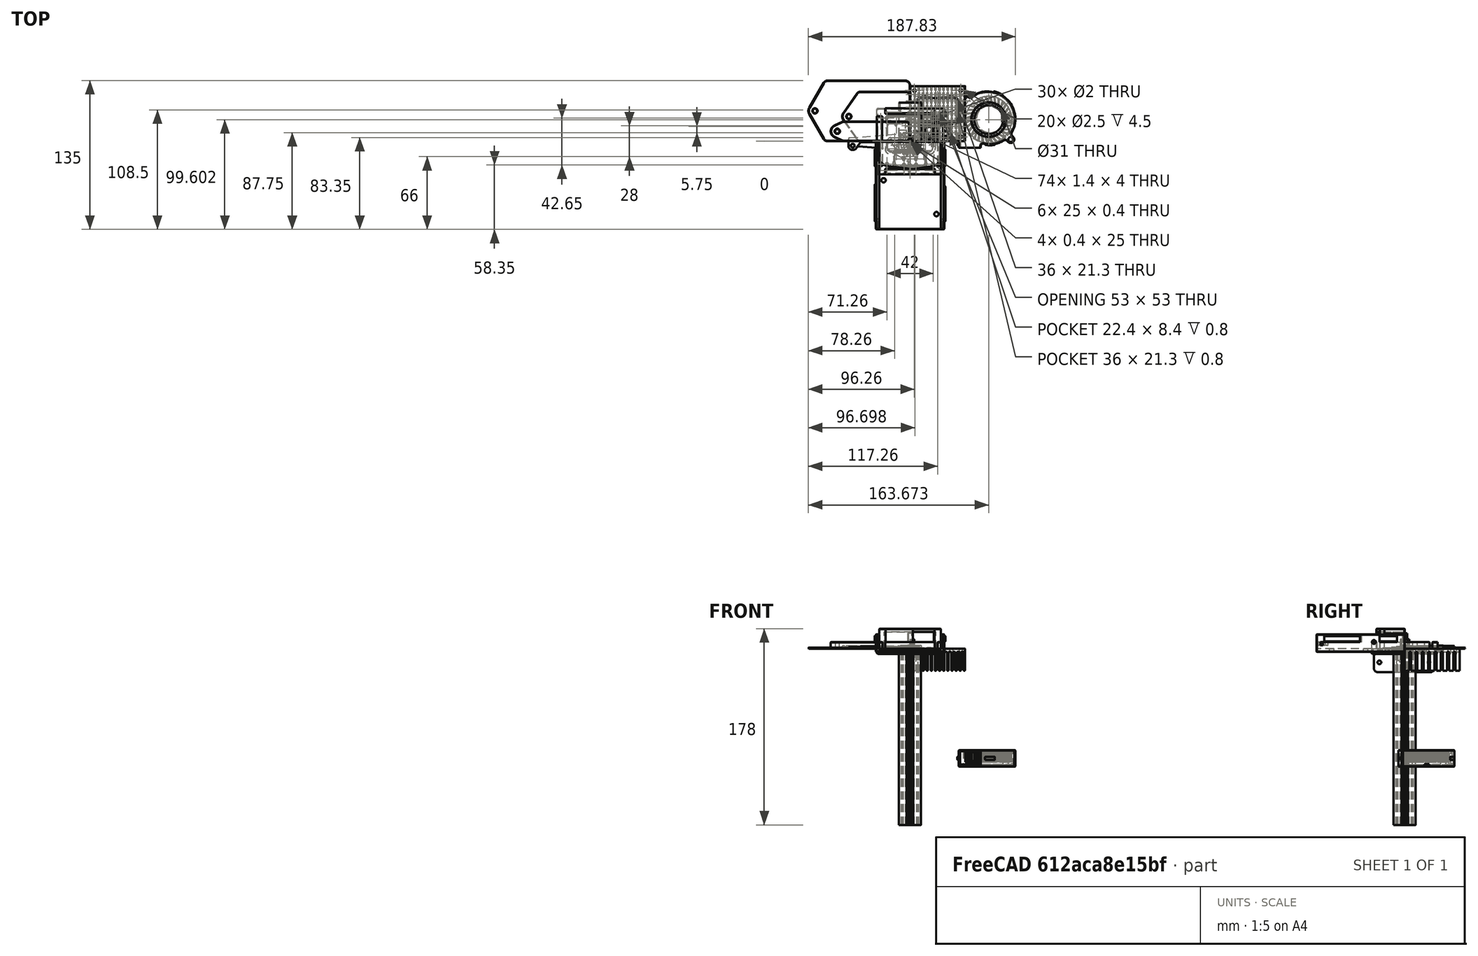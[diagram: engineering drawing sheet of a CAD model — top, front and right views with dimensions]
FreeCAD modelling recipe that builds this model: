
FCSTD DOCUMENT  (FreeCAD 1.1R20260325 (Git shallow))
Label: bedburner
License: All rights reserved
LicenseURL: https://www.gnu.org/licenses/gpl-3.0.html
objects: TechDraw::DrawViewDimension×98, App::FeaturePython×65, Sketcher::SketchObject×46, App::Point×28, App::Link×27, PartDesign::Pocket×26, PartDesign::Body×25, PartDesign::Chamfer×22, Part::Cut×16, PartDesign::Pad×14, PartDesign::FeatureBase×14, Part::Feature×13, PartDesign::Fillet×12, TechDraw::DrawProjGroupItem×12, App::DocumentObjectGroup×10, Part::Part2DObjectPython×6, Part::Extrusion×6, PartDesign::FeaturePython×6, App::VarSet×4, TechDraw::DrawSVGTemplate×4, +8 more types
note: 609 computed .brp shape members not serialized (recipe doc carries the construction recipe); baked Part::Feature solids carry a one-line shape summary decoded from their .brp

FEATURE [Sketcher::SketchObject] Sketch059  label="hhtb_base_face_s"
  ArcFitTolerance = 0
  AttachmentSupport = -> [XY_Plane036]
  ExternalTypes = [0]
  FullyConstrained = true
  MakeInternals = false
  MapMode = 5
  _ExternalGeoVersion = 0
  expr: .Constraints.width = <<block_params>>.heatsink_width + 2 * <<template_params>>.feature_side_width
  sketch-geometry (5):
    g0: LineSegment StartX=-30 StartY=30 StartZ=0 EndX=30 EndY=30 EndZ=0
    g1: LineSegment StartX=30 StartY=30 StartZ=0 EndX=30 EndY=-30 EndZ=0
    g2: LineSegment StartX=30 StartY=-30 StartZ=0 EndX=-30 EndY=-30 EndZ=0
    g3: LineSegment StartX=-30 StartY=-30 StartZ=0 EndX=-30 EndY=30 EndZ=0
    g4: Circle [constr] CenterX=0 CenterY=0 CenterZ=0 NormalX=0 NormalY=0 NormalZ=1 AngleXU=0 Radius=30
  constraints (14):
    c: Coincident(g0,g1)
    c: Coincident(g1,g2)
    c: Coincident(g2,g3)
    c: Coincident(g3,g0)
    c: Horizontal(g0)
    c: Horizontal(g2)
    c: Vertical(g1)
    c: Vertical(g3)
    c: Coincident(g4,g-1)
    c: Tangent(g4,g0)
    c: Tangent(g4,g1)
    c: Tangent(g4,g2)
    c: Tangent(g3,g4)
    c: Diameter(g4) = 60  'width'
FEATURE [PartDesign::Pad] Pad021  label="hhtb_base_face"
  Direction = (0,0,1)
  Length = 5
  Length2 = 10
  Profile = -> Sketch059
  ReferenceAxis = -> Sketch059 [N_Axis]
  Reversed = true
  SideType = 0
  Suppressed = false
  Type = 0
  Type2 = 0
FEATURE [Sketcher::SketchObject] Sketch060  label="hhtb_base_side_s"
  ArcFitTolerance = 0
  AttachmentSupport = -> [XZ_Plane036]
  ExternalTypes = [0]
  FullyConstrained = true
  MakeInternals = false
  MapMode = 5
  Placement = pos=(0,0,0) rot=(1,0,0;1.5708rad)
  _ExternalGeoVersion = 0
  expr: .Constraints.height = <<template_params>>.feature_side_height
  expr: .Constraints.outer_offset = <<hhtb_base_face_s>>.Constraints.width / 2
  expr: .Constraints.relief = <<template_params>>.feature_side_relief
  expr: .Constraints.width = <<template_params>>.feature_side_width - <<template_params>>.feature_side_clearance
  sketch-geometry (7):
    g0: LineSegment StartX=-30 StartY=6 StartZ=0 EndX=-30 EndY=0 EndZ=0
    g1: LineSegment StartX=-30 StartY=0 StartZ=0 EndX=-25.6 EndY=0 EndZ=0
    g2: LineSegment StartX=-25.6 StartY=0 StartZ=0 EndX=-25 EndY=0.6 EndZ=0
    g3: LineSegment StartX=-25 StartY=0.6 StartZ=0 EndX=-25 EndY=6 EndZ=0
    g4: LineSegment StartX=-25 StartY=6 StartZ=0 EndX=-30 EndY=6 EndZ=0
    g5: LineSegment [constr] StartX=-25.6 StartY=0 StartZ=0 EndX=-25 EndY=0 EndZ=0
    g6: LineSegment [constr] StartX=-25 StartY=0 StartZ=0 EndX=-25 EndY=0.6 EndZ=0
  constraints (20):
    c: Vertical(g0)
    c: Coincident(g0,g1)
    c: Horizontal(g1)
    c: Coincident(g1,g2)
    c: Coincident(g2,g3)
    c: Vertical(g3)
    c: Coincident(g3,g4)
    c: Coincident(g4,g0)
    c: Coincident(g1,g5)
    c: Horizontal(g5)
    c: Coincident(g5,g6)
    c: Coincident(g6,g2)
    c: Vertical(g6)
    c: Equal(g5,g6)
    c: Horizontal(g4)
    c: PointOnObject(g0,g-1)
    c: Distance(g6) = 0.6  'relief'
    c: DistanceX(g0,g-1) = 30  'outer_offset'
    c: Distance(g4) = 5  'width'
    c: Distance(g0) = 6  'height'
FEATURE [PartDesign::Pad] Pad022  label="hhtb_base_side1"
  BaseFeature = -> Pad021
  Direction = (0,-1,2e-16)
  Length = 45
  Length2 = 10
  Profile = -> Sketch060
  ReferenceAxis = -> Sketch060 [N_Axis]
  SideType = 2
  Suppressed = false
  Type = 0
  Type2 = 0
  expr: Length = <<template_params>>.feature_side_length
FEATURE [PartDesign::PolarPattern] PolarPattern001  label="hhtb_base_side234"
  Angle = 360
  Axis = -> Z_Axis036
  BaseFeature = -> Pad022
  Mode = 0
  Occurrences = 4
  Offset = 120
  Originals = -> [Pad022]
  SpacingPattern = [0]
  Spacings = [-1,-1,-1]
  Suppressed = false
  TransformMode = 0
FEATURE [PartDesign::Chamfer] Chamfer021  label="hhtb_base_corner_chmf"
  Angle = 45
  Base = -> PolarPattern001 [Edge12,Edge7,Edge1,Edge2]
  BaseFeature = -> PolarPattern001
  ChamferType = 0
  FlipDirection = false
  Size = 1
  Size2 = 1
  SupportTransform = false
  Suppressed = false
  UseAllEdges = false
FEATURE [PartDesign::Chamfer] Chamfer022  label="hhtb_base_bottom_chmf"
  Angle = 45
  Base = -> Chamfer021 [Face5]
  BaseFeature = -> Chamfer021
  ChamferType = 0
  FlipDirection = false
  Size = 0.8
  Size2 = 1
  SupportTransform = false
  Suppressed = false
  UseAllEdges = false
FEATURE [PartDesign::Fillet] Fillet013  label="hhtb_base_inner_flt"
  Base = -> Chamfer022 [Edge51,Edge52,Edge57,Edge58,Edge63,Edge65,Edge80,Edge86,Edge82,Edge83,Edge89,Edge91,Edge73,Edge74,Edge60,Edge55]
  BaseFeature = -> Chamfer022
  Radius = 0.4
  SupportTransform = false
  Suppressed = false
  UseAllEdges = false
FEATURE [Sketcher::SketchObject] Sketch061  label="hhdg_holes_s"
  ArcFitTolerance = 0
  AttachmentSupport = -> [XY_Plane037]
  ExternalTypes = [0]
  FullyConstrained = true
  MakeInternals = false
  MapMode = 5
  _ExternalGeoVersion = 0
  expr: .Constraints.block_spacing = <<block_params>>.heatsink_screw_spacing
  expr: .Constraints.block_width = <<block_params>>.heatsink_width
  expr: .Constraints.hole_diam = <<template_params>>.drill_hole_diam
  sketch-geometry (14):
    g0: Circle CenterX=-21 CenterY=21 CenterZ=0 NormalX=0 NormalY=0 NormalZ=1 AngleXU=0 Radius=1
    g1: Circle CenterX=21 CenterY=21 CenterZ=0 NormalX=0 NormalY=0 NormalZ=1 AngleXU=0 Radius=1
    g2: Circle CenterX=-21 CenterY=-21 CenterZ=0 NormalX=0 NormalY=0 NormalZ=1 AngleXU=0 Radius=1
    g3: Circle CenterX=21 CenterY=-21 CenterZ=0 NormalX=0 NormalY=0 NormalZ=1 AngleXU=0 Radius=1
    g4: LineSegment [constr] StartX=-25 StartY=25 StartZ=0 EndX=-25 EndY=-25 EndZ=0
    g5: LineSegment [constr] StartX=-25 StartY=-25 StartZ=0 EndX=25 EndY=-25 EndZ=0
    g6: LineSegment [constr] StartX=25 StartY=-25 StartZ=0 EndX=25 EndY=25 EndZ=0
    g7: LineSegment [constr] StartX=25 StartY=25 StartZ=0 EndX=-25 EndY=25 EndZ=0
    g8: Circle [constr] CenterX=0 CenterY=0 CenterZ=0 NormalX=0 NormalY=0 NormalZ=1 AngleXU=0 Radius=25
    g9: Circle [constr] CenterX=0 CenterY=0 CenterZ=0 NormalX=0 NormalY=0 NormalZ=1 AngleXU=0 Radius=21
    g10: LineSegment [constr] StartX=-21 StartY=21 StartZ=0 EndX=-21 EndY=-21 EndZ=0
    g11: LineSegment [constr] StartX=-21 StartY=-21 StartZ=0 EndX=21 EndY=-21 EndZ=0
    g12: LineSegment [constr] StartX=21 StartY=-21 StartZ=0 EndX=21 EndY=21 EndZ=0
    g13: LineSegment [constr] StartX=21 StartY=21 StartZ=0 EndX=-21 EndY=21 EndZ=0
  constraints (36):
    c: Diameter(g2) = 2  'hole_diam'
    c: Equal(g2,g0)
    c: Equal(g2,g3)
    c: Equal(g2,g1)
    c: Coincident(g4,g5)
    c: Coincident(g5,g6)
    c: Coincident(g6,g7)
    c: Coincident(g7,g4)
    c: Vertical(g4)
    c: Vertical(g6)
    c: Horizontal(g5)
    c: Horizontal(g7)
    c: Coincident(g8,g-1)
    c: Tangent(g8,g7)
    c: Tangent(g8,g6)
    c: Tangent(g8,g4)
    c: Tangent(g8,g5)
    c: Diameter(g8) = 50  'block_width'
    c: Coincident(g9,g8)
    c: Coincident(g10,g11)
    c: Coincident(g11,g12)
    c: Coincident(g12,g13)
    c: Coincident(g13,g10)
    c: Vertical(g10)
    c: Vertical(g12)
    c: Horizontal(g11)
    c: Horizontal(g13)
    c: Tangent(g9,g13)
    c: Tangent(g9,g12)
    c: Tangent(g9,g11)
    c: Tangent(g9,g10)
    c: Diameter(g9) = 42  'block_spacing'
    c: Coincident(g2,g10)
    c: Coincident(g3,g11)
    c: Coincident(g12,g1)
    c: Coincident(g10,g0)
FEATURE [Sketcher::SketchObject] Sketch062  label="hht_ptc_1-16_pocket_s"
  ArcFitTolerance = 0
  AttachmentSupport = -> [XY_Plane038]
  ExternalTypes = [0]
  FullyConstrained = true
  MakeInternals = false
  MapMode = 5
  _ExternalGeoVersion = 0
  expr: .Constraints.block_width = <<block_params>>.heatsink_width
  expr: .Constraints.corner_length = <<block_params>>.ptc_pocket_length + 2 * <<template_params>>.router_dogbone
  expr: .Constraints.corner_width = <<block_params>>.ptc_pocket_width + 2 * <<template_params>>.router_dogbone
  expr: .Constraints.edge_length = <<block_params>>.ptc_pocket_length + 2 * <<template_params>>.router_offset_1_16
  expr: .Constraints.edge_width = <<block_params>>.ptc_pocket_width + 2 * <<template_params>>.router_offset_1_16
  expr: .Constraints.placement_length = <<block_params>>.ptc_placement_length
  expr: .Constraints.placement_width = <<block_params>>.ptc_placement_width
  expr: .Constraints.router_bushing = <<template_params>>.router_bushing
  sketch-geometry (21):
    g0: LineSegment [constr] StartX=-18.3 StartY=14.45 StartZ=0 EndX=18.3 EndY=14.45 EndZ=0
    g1: LineSegment [constr] StartX=18.3 StartY=14.45 StartZ=0 EndX=18.3 EndY=-7.45 EndZ=0
    g2: LineSegment [constr] StartX=18.3 StartY=-7.45 StartZ=0 EndX=-18.3 EndY=-7.45 EndZ=0
    g3: LineSegment [constr] StartX=-18.3 StartY=-7.45 StartZ=0 EndX=-18.3 EndY=14.45 EndZ=0
    g4: LineSegment StartX=-21.375 StartY=11.9409 StartZ=0 EndX=-21.375 EndY=-4.94095 EndZ=0
    g5: LineSegment StartX=-15.7909 StartY=-10.525 StartZ=0 EndX=15.7909 EndY=-10.525 EndZ=0
    g6: LineSegment StartX=21.375 StartY=11.9409 StartZ=0 EndX=21.375 EndY=-4.94095 EndZ=0
    g7: LineSegment StartX=-15.7909 StartY=17.525 StartZ=0 EndX=15.7909 EndY=17.525 EndZ=0
    g8: ArcOfCircle CenterX=18.3 CenterY=14.45 CenterZ=0 NormalX=0 NormalY=0 NormalZ=1 AngleXU=0 Radius=3.96875 StartAngle=5.59879 EndAngle=8.53837
    g9: ArcOfCircle CenterX=18.3 CenterY=-7.45 CenterZ=0 NormalX=0 NormalY=0 NormalZ=1 AngleXU=0 Radius=3.96875 StartAngle=4.028 EndAngle=6.96758
    g10: ArcOfCircle CenterX=-18.3 CenterY=14.45 CenterZ=0 NormalX=0 NormalY=0 NormalZ=1 AngleXU=0 Radius=3.96875 StartAngle=0.886404 EndAngle=3.82599
    g11: ArcOfCircle CenterX=-18.3 CenterY=-7.45 CenterZ=0 NormalX=0 NormalY=0 NormalZ=1 AngleXU=0 Radius=3.96875 StartAngle=2.4572 EndAngle=5.39678
    g12: Circle [constr] CenterX=-1.8e-15 CenterY=3.5 CenterZ=0 NormalX=0 NormalY=0 NormalZ=1 AngleXU=0 Radius=14.025
    g13: Circle [constr] CenterX=-1.8e-15 CenterY=3.5 CenterZ=0 NormalX=0 NormalY=0 NormalZ=1 AngleXU=0 Radius=21.375
    g14: Circle [constr] CenterX=0 CenterY=0 CenterZ=0 NormalX=0 NormalY=0 NormalZ=1 AngleXU=0 Radius=25
    g15: LineSegment [constr] StartX=-25 StartY=25 StartZ=0 EndX=-25 EndY=-25 EndZ=0
    g16: LineSegment [constr] StartX=-25 StartY=-25 StartZ=0 EndX=25 EndY=-25 EndZ=0
    g17: LineSegment [constr] StartX=25 StartY=-25 StartZ=0 EndX=25 EndY=25 EndZ=0
    g18: LineSegment [constr] StartX=25 StartY=25 StartZ=0 EndX=-25 EndY=25 EndZ=0
    g19: Circle [constr] CenterX=-1.8e-15 CenterY=3.5 CenterZ=0 NormalX=0 NormalY=0 NormalZ=1 AngleXU=0 Radius=18.3
    g20: Circle [constr] CenterX=-1.8e-15 CenterY=3.5 CenterZ=0 NormalX=0 NormalY=0 NormalZ=1 AngleXU=0 Radius=10.95
  constraints (59):
    c: Coincident(g0,g1)
    c: Coincident(g1,g2)
    c: Coincident(g2,g3)
    c: Coincident(g3,g0)
    c: Horizontal(g0)
    c: Horizontal(g2)
    c: Vertical(g1)
    c: Vertical(g3)
    c: Vertical(g4)
    c: Horizontal(g5)
    c: Vertical(g6)
    c: Horizontal(g7)
    c: Equal(g10,g11)
    c: Equal(g11,g9)
    c: Equal(g9,g8)
    c: Diameter(g9) = 7.9375  'router_bushing'
    c: Coincident(g4,g10)
    c: Coincident(g10,g7)
    c: Coincident(g7,g8)
    c: Coincident(g6,g8)
    c: Coincident(g6,g9)
    c: Coincident(g5,g9)
    c: Coincident(g11,g5)
    c: Coincident(g11,g4)
    c: Coincident(g0,g8)
    c: Coincident(g1,g9)
    c: Coincident(g2,g11)
    c: Coincident(g0,g10)
    c: Coincident(g13,g12)
    c: Coincident(g14,g-1)
    c: Diameter(g14) = 50  'block_width'
    c: Coincident(g15,g16)
    c: Coincident(g16,g17)
    c: Coincident(g17,g18)
    c: Coincident(g18,g15)
    c: Vertical(g15)
    c: Vertical(g17)
    c: Horizontal(g16)
    c: Horizontal(g18)
    c: Tangent(g18,g14)
    c: Tangent(g17,g14)
    c: Tangent(g16,g14)
    c: Tangent(g15,g14)
    c: Tangent(g6,g13)
    c: Tangent(g13,g4)
    c: Tangent(g12,g7)
    c: Tangent(g12,g5)
    c: Diameter(g13) = 42.75  'edge_length'
    c: Diameter(g12) = 28.05  'edge_width'
    c: Coincident(g19,g12)
    c: Diameter(g19) = 36.6  'corner_length'
    c: Tangent(g1,g19)
    c: Tangent(g3,g19)
    c: Coincident(g20,g12)
    c: Tangent(g20,g0)
    c: Tangent(g20,g2)
    c: Diameter(g20) = 21.9  'corner_width'
    c: DistanceY(g16,g12) = 28.5  'placement_width'
    c: DistanceX(g12,g16) = 25  'placement_length'
FEATURE [Sketcher::SketchObject] Sketch064  label="hht_tswitch_1-16_pocket_s"
  ArcFitTolerance = 0
  AttachmentSupport = -> [XY_Plane039]
  ExternalTypes = [0]
  FullyConstrained = true
  MakeInternals = false
  MapMode = 5
  _ExternalGeoVersion = 0
  expr: .Constraints.block_width = <<block_params>>.heatsink_width
  expr: .Constraints.corner_length = <<block_params>>.tswitch_pocket_length + 2 * <<template_params>>.router_dogbone
  expr: .Constraints.corner_width = <<block_params>>.tswitch_pocket_width + 2 * <<template_params>>.router_dogbone
  expr: .Constraints.edge_length = <<block_params>>.tswitch_pocket_length + 2 * <<template_params>>.router_offset_1_16
  expr: .Constraints.edge_width = <<block_params>>.tswitch_pocket_width + 2 * <<template_params>>.router_offset_1_16
  expr: .Constraints.placement_length = <<block_params>>.tswitch_placement_length
  expr: .Constraints.placement_width = <<block_params>>.tswitch_placement_width
  expr: .Constraints.router_bushing = <<template_params>>.router_bushing
  sketch-geometry (21):
    g0: ArcOfCircle CenterX=-11.5 CenterY=-11.5 CenterZ=0 NormalX=0 NormalY=0 NormalZ=1 AngleXU=0 Radius=3.96875 StartAngle=0.886404 EndAngle=3.82599
    g1: ArcOfCircle CenterX=11.5 CenterY=-11.5 CenterZ=0 NormalX=0 NormalY=0 NormalZ=1 AngleXU=0 Radius=3.96875 StartAngle=5.59879 EndAngle=8.53837
    g2: ArcOfCircle CenterX=-11.5 CenterY=-20.5 CenterZ=0 NormalX=0 NormalY=0 NormalZ=1 AngleXU=0 Radius=3.96875 StartAngle=2.4572 EndAngle=5.39678
    g3: ArcOfCircle CenterX=11.5 CenterY=-20.5 CenterZ=0 NormalX=0 NormalY=0 NormalZ=1 AngleXU=0 Radius=3.96875 StartAngle=4.028 EndAngle=6.96758
    g4: LineSegment StartX=-8.99095 StartY=-8.425 StartZ=0 EndX=8.99095 EndY=-8.425 EndZ=0
    g5: LineSegment StartX=-8.99095 StartY=-23.575 StartZ=0 EndX=8.99095 EndY=-23.575 EndZ=0
    g6: LineSegment StartX=-14.575 StartY=-14.0091 StartZ=0 EndX=-14.575 EndY=-17.9909 EndZ=0
    g7: LineSegment StartX=14.575 StartY=-14.0091 StartZ=0 EndX=14.575 EndY=-17.9909 EndZ=0
    g8: LineSegment [constr] StartX=-11.5 StartY=-11.5 StartZ=0 EndX=-11.5 EndY=-20.5 EndZ=0
    g9: LineSegment [constr] StartX=-11.5 StartY=-20.5 StartZ=0 EndX=11.5 EndY=-20.5 EndZ=0
    g10: LineSegment [constr] StartX=11.5 StartY=-20.5 StartZ=0 EndX=11.5 EndY=-11.5 EndZ=0
    g11: LineSegment [constr] StartX=11.5 StartY=-11.5 StartZ=0 EndX=-11.5 EndY=-11.5 EndZ=0
    g12: Circle [constr] CenterX=0 CenterY=0 CenterZ=0 NormalX=0 NormalY=0 NormalZ=1 AngleXU=0 Radius=25
    g13: LineSegment [constr] StartX=-25 StartY=25 StartZ=0 EndX=-25 EndY=-25 EndZ=0
    g14: LineSegment [constr] StartX=-25 StartY=-25 StartZ=0 EndX=25 EndY=-25 EndZ=0
    g15: LineSegment [constr] StartX=25 StartY=-25 StartZ=0 EndX=25 EndY=25 EndZ=0
    g16: LineSegment [constr] StartX=25 StartY=25 StartZ=0 EndX=-25 EndY=25 EndZ=0
    g17: Circle [constr] CenterX=3e-16 CenterY=-16 CenterZ=0 NormalX=0 NormalY=0 NormalZ=1 AngleXU=0 Radius=4.5
    g18: Circle [constr] CenterX=3e-16 CenterY=-16 CenterZ=0 NormalX=0 NormalY=0 NormalZ=1 AngleXU=0 Radius=11.5
    g19: Circle [constr] CenterX=3e-16 CenterY=-16 CenterZ=0 NormalX=0 NormalY=0 NormalZ=1 AngleXU=0 Radius=7.575
    g20: Circle [constr] CenterX=3e-16 CenterY=-16 CenterZ=0 NormalX=0 NormalY=0 NormalZ=1 AngleXU=0 Radius=14.575
  constraints (59):
    c: Equal(g0,g1)
    c: Equal(g1,g3)
    c: Equal(g3,g2)
    c: Horizontal(g4)
    c: Horizontal(g5)
    c: Vertical(g6)
    c: Vertical(g7)
    c: Diameter(g1) = 7.9375  'router_bushing'
    c: Coincident(g0,g4)
    c: Coincident(g4,g1)
    c: Coincident(g6,g0)
    c: Coincident(g2,g6)
    c: Coincident(g2,g5)
    c: Coincident(g5,g3)
    c: Coincident(g3,g7)
    c: Coincident(g7,g1)
    c: Coincident(g8,g9)
    c: Coincident(g9,g10)
    c: Coincident(g10,g11)
    c: Coincident(g11,g8)
    c: Vertical(g8)
    c: Vertical(g10)
    c: Horizontal(g9)
    c: Horizontal(g11)
    c: Coincident(g10,g1)
    c: Coincident(g8,g0)
    c: Coincident(g8,g2)
    c: Coincident(g9,g3)
    c: Coincident(g12,g-1)
    c: Coincident(g13,g14)
    c: Coincident(g14,g15)
    c: Coincident(g15,g16)
    c: Coincident(g16,g13)
    c: Vertical(g13)
    c: Vertical(g15)
    c: Horizontal(g14)
    c: Horizontal(g16)
    c: Tangent(g15,g12)
    c: Tangent(g12,g16)
    c: Tangent(g13,g12)
    c: Tangent(g14,g12)
    c: Diameter(g12) = 50  'block_width'
    c: Coincident(g18,g17)
    c: Coincident(g19,g17)
    c: Coincident(g20,g17)
    c: Tangent(g20,g7)
    c: Tangent(g20,g6)
    c: Diameter(g20) = 29.15  'edge_length'
    c: Tangent(g19,g4)
    c: Tangent(g19,g5)
    c: Diameter(g19) = 15.15  'edge_width'
    c: Tangent(g18,g10)
    c: Tangent(g18,g8)
    c: Diameter(g18) = 23  'corner_length'
    c: Tangent(g17,g11)
    c: Tangent(g17,g9)
    c: Diameter(g17) = 9  'corner_width'
    c: DistanceY(g14,g17) = 9  'placement_width'
    c: DistanceX(g17,g14) = 25  'placement_length'
FEATURE [PartDesign::Chamfer] Chamfer026  label="hhtb_base_top_chmf"
  Angle = 45
  Base = -> Fillet013 [Edge121,Edge108,Edge131,Edge141]
  BaseFeature = -> Fillet013
  ChamferType = 0
  FlipDirection = false
  Size = 0.39
  Size2 = 1
  SupportTransform = false
  Suppressed = false
  UseAllEdges = false
FEATURE [Part::Part2DObjectPython] ShapeString001  label="hht_text_1-16_s"  # Draft 2D object (typed FeaturePython)
  FontFile = <userpath>/Documents/fdm/fdm_fonts/Overpass/static/Overpass-Bold.ttf
  Fuse = false
  Justification = 6
  JustificationReference = 0
  KeepLeftMargin = true
  MakeFace = true
  ObliqueAngle = 0
  Placement = pos=(22,22,-5) rot=(0,1,0;3.14159rad)
  ScaleToSize = false
  Size = 4
  String = 1/16" bit
  Tracking = 0
  expr: .Placement.Base.z = -<<hhtb_base_face>>.Length
FEATURE [Part::Part2DObjectPython] ShapeString002  label="hht_text_1-8_s"  # Draft 2D object (typed FeaturePython)
  FontFile = <userpath>/Documents/fdm/fdm_fonts/Overpass/static/Overpass-Bold.ttf
  Fuse = false
  Justification = 6
  JustificationReference = 0
  KeepLeftMargin = true
  MakeFace = true
  ObliqueAngle = 0
  Placement = pos=(22,22,-5) rot=(0,1,0;3.14159rad)
  ScaleToSize = false
  Size = 4
  String = 1/8" bit
  Tracking = 0
  expr: .Placement.Base.z = -<<hhtb_base_face>>.Length
FEATURE [Part::Extrusion] Extrude001  label="hht_text_l_1-16"
  Base = -> ShapeString001
  Dir = (0,0,-1)
  DirMode = 2
  FaceMakerClass = Part::FaceMakerBullseye
  FaceMakerMode = 3
  InnerWireTaper = 1
  LengthFwd = 0.2
  LengthRev = 0
  Reversed = true
  Solid = false
  Symmetric = false
FEATURE [Part::Extrusion] Extrude002  label="hht_text_l_1-8"
  Base = -> ShapeString002
  Dir = (0,0,-1)
  DirMode = 2
  FaceMakerClass = Part::FaceMakerBullseye
  FaceMakerMode = 3
  InnerWireTaper = 1
  LengthFwd = 0.2
  LengthRev = 0
  Reversed = true
  Solid = true
  Symmetric = false
FEATURE [Sketcher::SketchObject] Sketch080  label="hht_ptc_1-8_pocket_s"
  ArcFitTolerance = 0
  AttachmentSupport = -> [XY_Plane043]
  ExternalTypes = [0]
  FullyConstrained = true
  MakeInternals = false
  MapMode = 5
  _ExternalGeoVersion = 0
  expr: .Constraints.block_width = <<block_params>>.heatsink_width
  expr: .Constraints.edge_length = <<block_params>>.ptc_pocket_length + 2 * <<template_params>>.router_offset_1_8
  expr: .Constraints.edge_width = <<block_params>>.ptc_pocket_width + 2 * <<template_params>>.router_offset_1_8
  expr: .Constraints.placement_length = <<block_params>>.ptc_placement_length
  expr: .Constraints.placement_width = <<block_params>>.ptc_placement_width
  expr: .Constraints.router_bushing = <<template_params>>.router_bushing
  sketch-geometry (15):
    g0: LineSegment StartX=-16.6125 StartY=16.7313 StartZ=0 EndX=16.6125 EndY=16.7313 EndZ=0
    g1: LineSegment StartX=20.5813 StartY=12.7625 StartZ=0 EndX=20.5813 EndY=-5.7625 EndZ=0
    g2: LineSegment StartX=16.6125 StartY=-9.73125 StartZ=0 EndX=-16.6125 EndY=-9.73125 EndZ=0
    g3: LineSegment StartX=-20.5812 StartY=-5.7625 StartZ=0 EndX=-20.5812 EndY=12.7625 EndZ=0
    g4: ArcOfCircle CenterX=-16.6125 CenterY=12.7625 CenterZ=0 NormalX=0 NormalY=0 NormalZ=1 AngleXU=0 Radius=3.96875 StartAngle=1.5708 EndAngle=3.14159
    g5: ArcOfCircle CenterX=16.6125 CenterY=12.7625 CenterZ=0 NormalX=0 NormalY=0 NormalZ=1 AngleXU=0 Radius=3.96875 StartAngle=0 EndAngle=1.5708
    g6: ArcOfCircle CenterX=16.6125 CenterY=-5.7625 CenterZ=0 NormalX=0 NormalY=0 NormalZ=1 AngleXU=0 Radius=3.96875 StartAngle=4.71239 EndAngle=6.28319
    g7: ArcOfCircle CenterX=-16.6125 CenterY=-5.7625 CenterZ=0 NormalX=0 NormalY=0 NormalZ=1 AngleXU=0 Radius=3.96875 StartAngle=3.14159 EndAngle=4.71239
    g8: Circle [constr] CenterX=0 CenterY=0 CenterZ=0 NormalX=0 NormalY=0 NormalZ=1 AngleXU=0 Radius=25
    g9: LineSegment [constr] StartX=-25 StartY=25 StartZ=0 EndX=-25 EndY=-25 EndZ=0
    g10: LineSegment [constr] StartX=-25 StartY=-25 StartZ=0 EndX=25 EndY=-25 EndZ=0
    g11: LineSegment [constr] StartX=25 StartY=-25 StartZ=0 EndX=25 EndY=25 EndZ=0
    g12: LineSegment [constr] StartX=25 StartY=25 StartZ=0 EndX=-25 EndY=25 EndZ=0
    g13: Circle [constr] CenterX=8e-16 CenterY=3.5 CenterZ=0 NormalX=0 NormalY=0 NormalZ=1 AngleXU=0 Radius=13.2313
    g14: Circle [constr] CenterX=8e-16 CenterY=3.5 CenterZ=0 NormalX=0 NormalY=0 NormalZ=1 AngleXU=0 Radius=20.5813
  constraints (39):
    c: Horizontal(g0)
    c: Horizontal(g2)
    c: Vertical(g1)
    c: Vertical(g3)
    c: Tangent(g3,g4) = 1.5708
    c: Tangent(g0,g4) = 1.5708
    c: Tangent(g0,g5) = 1.5708
    c: Tangent(g1,g5) = 1.5708
    c: Tangent(g1,g6) = 1.5708
    c: Tangent(g2,g6) = 1.5708
    c: Tangent(g2,g7) = 1.5708
    c: Tangent(g3,g7) = 1.5708
    c: Equal(g4,g5)
    c: Equal(g5,g6)
    c: Equal(g6,g7)
    c: Diameter(g6) = 7.9375  'router_bushing'
    c: Coincident(g8,g-1)
    c: Coincident(g9,g10)
    c: Coincident(g10,g11)
    c: Coincident(g11,g12)
    c: Coincident(g12,g9)
    c: Vertical(g9)
    c: Vertical(g11)
    c: Horizontal(g10)
    c: Horizontal(g12)
    c: Tangent(g8,g11)
    c: Tangent(g8,g12)
    c: Tangent(g8,g9)
    c: Tangent(g8,g10)
    c: Diameter(g8) = 50  'block_width'
    c: Coincident(g14,g13)
    c: Tangent(g14,g1)
    c: Tangent(g14,g3)
    c: Tangent(g13,g0)
    c: Tangent(g13,g2)
    c: Diameter(g14) = 41.1625  'edge_length'
    c: Diameter(g13) = 26.4625  'edge_width'
    c: DistanceX(g13,g10) = 25  'placement_length'
    c: DistanceY(g10,g13) = 28.5  'placement_width'
FEATURE [Sketcher::SketchObject] Sketch081  label="hht_tswitch_1-8_pocket_s"
  ArcFitTolerance = 0
  AttachmentSupport = -> [XY_Plane044]
  ExternalTypes = [0]
  FullyConstrained = true
  MakeInternals = false
  MapMode = 5
  _ExternalGeoVersion = 0
  expr: .Constraints.block_width = <<block_params>>.heatsink_width
  expr: .Constraints.edge_length = <<block_params>>.tswitch_pocket_length + 2 * <<template_params>>.router_offset_1_8
  expr: .Constraints.edge_width = <<block_params>>.tswitch_pocket_width + 2 * <<template_params>>.router_offset_1_8
  expr: .Constraints.placement_length = <<block_params>>.tswitch_placement_length
  expr: .Constraints.placement_width = <<block_params>>.tswitch_placement_width
  expr: .Constraints.router_bushing = <<template_params>>.router_bushing
  sketch-geometry (15):
    g0: LineSegment StartX=-9.8125 StartY=-9.21875 StartZ=0 EndX=9.8125 EndY=-9.21875 EndZ=0
    g1: LineSegment StartX=13.7813 StartY=-13.1875 StartZ=0 EndX=13.7813 EndY=-18.8125 EndZ=0
    g2: LineSegment StartX=9.8125 StartY=-22.7812 StartZ=0 EndX=-9.8125 EndY=-22.7812 EndZ=0
    g3: LineSegment StartX=-13.7813 StartY=-18.8125 StartZ=0 EndX=-13.7813 EndY=-13.1875 EndZ=0
    g4: ArcOfCircle CenterX=9.8125 CenterY=-13.1875 CenterZ=0 NormalX=0 NormalY=0 NormalZ=1 AngleXU=0 Radius=3.96875 StartAngle=0 EndAngle=1.5708
    g5: ArcOfCircle CenterX=-9.8125 CenterY=-18.8125 CenterZ=0 NormalX=0 NormalY=0 NormalZ=1 AngleXU=0 Radius=3.96875 StartAngle=3.14159 EndAngle=4.71239
    g6: ArcOfCircle CenterX=9.8125 CenterY=-18.8125 CenterZ=0 NormalX=0 NormalY=0 NormalZ=1 AngleXU=0 Radius=3.96875 StartAngle=4.71239 EndAngle=6.28319
    g7: ArcOfCircle CenterX=-9.8125 CenterY=-13.1875 CenterZ=0 NormalX=0 NormalY=0 NormalZ=1 AngleXU=0 Radius=3.96875 StartAngle=1.5708 EndAngle=3.14159
    g8: Circle [constr] CenterX=0 CenterY=0 CenterZ=0 NormalX=0 NormalY=0 NormalZ=1 AngleXU=0 Radius=25
    g9: LineSegment [constr] StartX=-25 StartY=25 StartZ=0 EndX=-25 EndY=-25 EndZ=0
    g10: LineSegment [constr] StartX=-25 StartY=-25 StartZ=0 EndX=25 EndY=-25 EndZ=0
    g11: LineSegment [constr] StartX=25 StartY=-25 StartZ=0 EndX=25 EndY=25 EndZ=0
    g12: LineSegment [constr] StartX=25 StartY=25 StartZ=0 EndX=-25 EndY=25 EndZ=0
    g13: Circle [constr] CenterX=7e-16 CenterY=-16 CenterZ=0 NormalX=0 NormalY=0 NormalZ=1 AngleXU=0 Radius=6.78125
    g14: Circle [constr] CenterX=7e-16 CenterY=-16 CenterZ=0 NormalX=0 NormalY=0 NormalZ=1 AngleXU=0 Radius=13.7812
  constraints (39):
    c: Horizontal(g0)
    c: Horizontal(g2)
    c: Vertical(g1)
    c: Vertical(g3)
    c: Tangent(g0,g4) = 1.5708
    c: Tangent(g1,g4) = 1.5708
    c: Tangent(g3,g5) = 1.5708
    c: Tangent(g2,g5) = 1.5708
    c: Tangent(g1,g6) = 1.5708
    c: Tangent(g2,g6) = 1.5708
    c: Tangent(g3,g7) = 1.5708
    c: Tangent(g0,g7) = 1.5708
    c: Equal(g6,g4)
    c: Equal(g6,g7)
    c: Equal(g6,g5)
    c: Diameter(g6) = 7.9375  'router_bushing'
    c: Coincident(g8,g-1)
    c: Coincident(g9,g10)
    c: Coincident(g10,g11)
    c: Coincident(g11,g12)
    c: Coincident(g12,g9)
    c: Vertical(g9)
    c: Vertical(g11)
    c: Horizontal(g10)
    c: Horizontal(g12)
    c: Tangent(g8,g12)
    c: Tangent(g8,g9)
    c: Tangent(g8,g10)
    c: Tangent(g8,g11)
    c: Diameter(g8) = 50  'block_width'
    c: Coincident(g14,g13)
    c: Tangent(g14,g1)
    c: Tangent(g14,g3)
    c: Diameter(g14) = 27.5625  'edge_length'
    c: Tangent(g13,g0)
    c: Tangent(g13,g2)
    c: Diameter(g13) = 13.5625  'edge_width'
    c: DistanceY(g10,g13) = 9  'placement_width'
    c: DistanceX(g13,g10) = 25  'placement_length'
FEATURE [Part::Part2DObjectPython] ShapeString004  label="hht_text_screws_s"  # Draft 2D object (typed FeaturePython)
  FontFile = <userpath>/Documents/fdm/fdm_fonts/Overpass/static/Overpass-Bold.ttf
  Fuse = false
  Justification = 6
  JustificationReference = 0
  KeepLeftMargin = true
  MakeFace = true
  ObliqueAngle = 0
  Placement = pos=(-2,22,-5) rot=(0,1,0;3.14159rad)
  ScaleToSize = false
  Size = 4
  String = Screws
  Tracking = 0
  expr: .Placement.Base.z = -<<hhtb_base_face>>.Length
FEATURE [Part::Part2DObjectPython] ShapeString005  label="hht_text_ptc_s"  # Draft 2D object (typed FeaturePython)
  FontFile = <userpath>/Documents/fdm/fdm_fonts/Overpass/static/Overpass-Bold.ttf
  Fuse = false
  Justification = 6
  JustificationReference = 0
  KeepLeftMargin = true
  MakeFace = true
  ObliqueAngle = 0
  Placement = pos=(-2,22,-5) rot=(0,1,0;3.14159rad)
  ScaleToSize = false
  Size = 4
  String = PTC
  Tracking = 0
  expr: .Placement.Base.z = -<<hhtb_base_face>>.Length
FEATURE [Part::Part2DObjectPython] ShapeString006  label="hht_text_tswitch_s"  # Draft 2D object (typed FeaturePython)
  FontFile = <userpath>/Documents/fdm/fdm_fonts/Overpass/static/Overpass-Bold.ttf
  Fuse = false
  Justification = 6
  JustificationReference = 0
  KeepLeftMargin = true
  MakeFace = true
  ObliqueAngle = 0
  Placement = pos=(-2,22,-5) rot=(0,1,0;3.14159rad)
  ScaleToSize = false
  Size = 4
  String = TSwitch
  Tracking = 0
  expr: .Placement.Base.z = -<<hhtb_base_face>>.Length
FEATURE [Sketcher::SketchObject] Sketch085  label="hrb_block_plate_s"
  ArcFitTolerance = 0
  AttachmentSupport = -> [XY_Plane138]
  ExternalTypes = [0]
  FullyConstrained = true
  MakeInternals = false
  MapMode = 5
  _ExternalGeoVersion = 0
  expr: .Constraints.bend_straight = <<bracket_params>>.feature_bend_straight
  expr: .Constraints.block_screw_spacing = <<block_params>>.heatsink_screw_spacing
  expr: .Constraints.block_side_offset = <<bracket_params>>.feature_block_offset
  expr: .Constraints.block_width = <<block_params>>.heatsink_width
  expr: .Constraints.height_block_bottom = <<bracket_params>>.feature_deck_clear_block
  expr: .Constraints.height_block_top = <<bracket_params>>.feature_deck_clear_block + <<block_params>>.heatsink_height
  expr: .Constraints.height_bracket_bottom = <<bracket_params>>.feature_deck_clear_bracket
  expr: .Constraints.height_component_top = <<bracket_params>>.feature_deck_clear_block + <<block_params>>.heatsink_height + <<bracket_params>>.height_componets
  expr: .Constraints.height_extrusion = <<bracket_params>>.height_extrusion
  expr: .Constraints.height_stock_bed = <<bracket_params>>.height_extrusion + <<bracket_params>>.height_stock
  expr: .Constraints.height_stock_silicone = <<bracket_params>>.height_extrusion + <<bracket_params>>.height_stock - <<bracket_params>>.height_silicone_heater
  expr: .Constraints.height_whop_bed = <<bracket_params>>.height_extrusion + <<bracket_params>>.height_whopKinematic
  expr: .Constraints.height_whop_silicone = <<bracket_params>>.height_extrusion + <<bracket_params>>.height_whopKinematic - <<bracket_params>>.height_silicone_heater
  expr: .Constraints.plate_block_overlap = <<bracket_params>>.rear_overlap
  expr: .Constraints.plate_overhang = <<bracket_params>>.rear_overhang_inner
  expr: .Constraints.plate_overhang_outer = <<bracket_params>>.rear_overhang_outer
  expr: .Constraints.screw_head = <<bracket_params>>.feature_screw_head
  expr: .Constraints.screw_hole = <<bracket_params>>.feature_screw_hole
  expr: .Constraints.screw_pad_diam = <<bracket_params>>.rear_pad_diam
  expr: .Constraints.side_extension = <<bracket_params>>.rear_side_extension
  expr: .Constraints.side_screw_inset1 = <<bracket_params>>.rear_side_screw_inset
  expr: .Constraints.side_screw_inset2 = <<bracket_params>>.rear_side_screw_inset + <<bracket_params>>.rear_side_screw_spacing
  sketch-geometry (50):
    g0: Circle CenterX=-10 CenterY=-4 CenterZ=0 NormalX=0 NormalY=0 NormalZ=1 AngleXU=0 Radius=1.7
    g1: Circle CenterX=-52 CenterY=-4 CenterZ=0 NormalX=0 NormalY=0 NormalZ=1 AngleXU=0 Radius=1.7
    g2: ArcOfCircle CenterX=-52 CenterY=-4 CenterZ=0 NormalX=0 NormalY=0 NormalZ=1 AngleXU=0 Radius=4 StartAngle=3.14159 EndAngle=5.67232
    g3: ArcOfCircle CenterX=-10 CenterY=-4 CenterZ=0 NormalX=0 NormalY=0 NormalZ=1 AngleXU=0 Radius=4 StartAngle=3.75246 EndAngle=6.28319
    g4: LineSegment [constr] StartX=-52 StartY=-2.3 StartZ=0 EndX=-52 EndY=0 EndZ=0
    g5: LineSegment StartX=-48.7234 StartY=-6.29431 StartZ=0 EndX=-45.0163 EndY=-1 EndZ=0
    g6: LineSegment StartX=-13.2766 StartY=-6.29431 StartZ=0 EndX=-16.9837 EndY=-1 EndZ=0
    g7: LineSegment StartX=-56 StartY=-4 StartZ=0 EndX=-56 EndY=3 EndZ=0
    g8: LineSegment StartX=-45.0163 StartY=-1 StartZ=0 EndX=-16.9837 EndY=-1 EndZ=0
    g9: LineSegment StartX=-6 StartY=-1 StartZ=0 EndX=-6 EndY=-4 EndZ=0
    g10: LineSegment StartX=-6 StartY=-1 StartZ=0 EndX=0 EndY=-1 EndZ=0
    g11: LineSegment StartX=0 StartY=-1 StartZ=0 EndX=0 EndY=7 EndZ=0
    g12: LineSegment [constr] StartX=0 StartY=0 StartZ=0 EndX=20 EndY=0 EndZ=0
    g13: LineSegment [constr] StartX=20 StartY=0 StartZ=0 EndX=20 EndY=-20 EndZ=0
    g14: LineSegment [constr] StartX=20 StartY=-20 StartZ=0 EndX=0 EndY=-20 EndZ=0
    g15: LineSegment [constr] StartX=0 StartY=-20 StartZ=0 EndX=0 EndY=0 EndZ=0
    g16: Circle [constr] CenterX=10 CenterY=-10 CenterZ=0 NormalX=0 NormalY=0 NormalZ=1 AngleXU=0 Radius=10
    g17: LineSegment [constr] StartX=29.5 StartY=0 StartZ=0 EndX=29.5 EndY=-20 EndZ=0
    g18: LineSegment [constr] StartX=35.5 StartY=0 StartZ=0 EndX=35.5 EndY=-20 EndZ=0
    g19: LineSegment [constr] StartX=29.5 StartY=-20 StartZ=0 EndX=27.5 EndY=-20 EndZ=0
    g20: LineSegment [constr] StartX=27.5 StartY=-20 StartZ=0 EndX=27.5 EndY=-10 EndZ=0
    g21: LineSegment [constr] StartX=35.5 StartY=-20 StartZ=0 EndX=33.5 EndY=-20 EndZ=0
    g22: LineSegment [constr] StartX=33.5 StartY=-20 StartZ=0 EndX=33.5 EndY=-10 EndZ=0
    g23: Circle [constr] CenterX=0 CenterY=5 CenterZ=0 NormalX=0 NormalY=0 NormalZ=1 AngleXU=0 Radius=1.7
    g24: Circle [constr] CenterX=0 CenterY=5 CenterZ=0 NormalX=0 NormalY=0 NormalZ=1 AngleXU=0 Radius=2.75
    g25: Circle [constr] CenterX=0 CenterY=22 CenterZ=0 NormalX=0 NormalY=0 NormalZ=1 AngleXU=0 Radius=1.7
    g26: Circle [constr] CenterX=0 CenterY=22 CenterZ=0 NormalX=0 NormalY=0 NormalZ=1 AngleXU=0 Radius=2.75
    g27: LineSegment [constr] StartX=0 StartY=27 StartZ=0 EndX=0 EndY=23.7 EndZ=0
    g28: LineSegment StartX=-56 StartY=3 StartZ=0 EndX=-4 EndY=7 EndZ=0
    g29: LineSegment StartX=-4 StartY=7 StartZ=0 EndX=0 EndY=7 EndZ=0
    g30: LineSegment [constr] StartX=-56 StartY=0 StartZ=0 EndX=-56 EndY=-50 EndZ=0
    g31: LineSegment [constr] StartX=-56 StartY=-50 StartZ=0 EndX=-6 EndY=-50 EndZ=0
    g32: LineSegment [constr] StartX=-6 StartY=-50 StartZ=0 EndX=-6 EndY=0 EndZ=0
    g33: LineSegment [constr] StartX=-6 StartY=0 StartZ=0 EndX=-56 EndY=0 EndZ=0
    g34: LineSegment [constr] StartX=-52 StartY=-4 StartZ=0 EndX=-52 EndY=-46 EndZ=0
    g35: LineSegment [constr] StartX=-52 StartY=-46 StartZ=0 EndX=-10 EndY=-46 EndZ=0
    g36: LineSegment [constr] StartX=-10 StartY=-46 StartZ=0 EndX=-10 EndY=-4 EndZ=0
    g37: LineSegment [constr] StartX=-10 StartY=-4 StartZ=0 EndX=-52 EndY=-4 EndZ=0
    g38: Circle [constr] CenterX=-31 CenterY=-25 CenterZ=0 NormalX=0 NormalY=0 NormalZ=1 AngleXU=0 Radius=21
    g39: Circle [constr] CenterX=-31 CenterY=-25 CenterZ=0 NormalX=0 NormalY=0 NormalZ=1 AngleXU=0 Radius=25
    g40: Circle [constr] CenterX=-10 CenterY=-4 CenterZ=0 NormalX=0 NormalY=0 NormalZ=1 AngleXU=0 Radius=2.75
    g41: Circle [constr] CenterX=-52 CenterY=-4 CenterZ=0 NormalX=0 NormalY=0 NormalZ=1 AngleXU=0 Radius=2.75
    g42: LineSegment [constr] StartX=29 StartY=0 StartZ=0 EndX=22.5 EndY=0 EndZ=0
    g43: LineSegment [constr] StartX=22.5 StartY=-10 StartZ=0 EndX=29 EndY=-10 EndZ=0
    g44: LineSegment [constr] StartX=29 StartY=-10 StartZ=0 EndX=29 EndY=0 EndZ=0
    g45: LineSegment [constr] StartX=2.5 StartY=0 StartZ=0 EndX=2.5 EndY=-20 EndZ=0
    g46: LineSegment [constr] StartX=2.5 StartY=-20 StartZ=0 EndX=22.5 EndY=-20 EndZ=0
    g47: LineSegment [constr] StartX=22.5 StartY=-20 StartZ=0 EndX=22.5 EndY=0 EndZ=0
    g48: LineSegment [constr] StartX=22.5 StartY=0 StartZ=0 EndX=2.5 EndY=0 EndZ=0
    g49: LineSegment [constr] StartX=1 StartY=0 StartZ=0 EndX=1 EndY=-20 EndZ=0
  constraints (147):
    c: Equal(g0,g1)
    c: Diameter(g1) = 3.4  'screw_hole'
    c: Coincident(g2,g1)
    c: Coincident(g3,g0)
    c: Equal(g2,g3)
    c: PointOnObject(g4,g1)
    c: PointOnObject(g4,g2)
    c: Vertical(g4)
    c: PointOnObject(g1,g4)
    c: Diameter(g2) = 8  'screw_pad_diam'
    c: Vertical(g7)
    c: Tangent(g7,g2) = 1.5708
    c: Tangent(g2,g5) = -1.5708
    c: Tangent(g6,g3) = 1.5708
    c: Coincident(g8,g5)
    c: Coincident(g8,g6)
    c: Horizontal(g8)
    c: Equal(g5,g6)
    c: Angle(g5,g7) = 0.610865  'screw_pad_angle'
    c: Distance(g8) = 28.0326  'plate_overlay_width'
    c: Vertical(g9)
    c: Coincident(g10,g9)
    c: PointOnObject(g10,g-2)
    c: Horizontal(g10)
    c: Tangent(g9,g3) = 1.5708
    c: Coincident(g11,g10)
    c: PointOnObject(g11,g-2)
    c: DistanceY(g-1,g11) = 7  'plate_overhang'
    c: PointOnObject(g10,g8)
    c: Coincident(g12,g13)
    c: Coincident(g13,g14)
    c: Coincident(g14,g15)
    c: Coincident(g15,g12)
    c: Horizontal(g12)
    c: Horizontal(g14)
    c: Vertical(g13)
    c: Vertical(g15)
    c: Tangent(g15,g16)
    c: Tangent(g16,g12)
    c: Tangent(g16,g13)
    c: Tangent(g14,g16)
    c: Distance(g14) = 20  'height_extrusion'
    c: Vertical(g17)
    c: Vertical(g18)
    c: PointOnObject(g17,g14)
    c: PointOnObject(g18,g14)
    c: PointOnObject(g17,g12)
    c: PointOnObject(g18,g12)
    c: Coincident(g19,g17)
    c: Coincident(g20,g19)
    c: Coincident(g21,g18)
    c: Coincident(g22,g21)
    c: Vertical(g22)
    c: Horizontal(g21)
    c: Horizontal(g19)
    c: Coincident(g24,g23)
    c: Coincident(g26,g25)
    c: Equal(g23,g25)
    c: Equal(g26,g24)
    c: Equal(g23,g0)
    c: PointOnObject(g25,g-2)
    c: PointOnObject(g23,g-2)
    c: PointOnObject(g27,g25)
    c: PointOnObject(g27,g-2)
    c: PointOnObject(g27,g-2)
    c: Distance(g27) = 3.3  'side_screw_outer'
    c: DistanceY(g11,g27) = 20  'side_extension'
    c: Coincident(g7,g28)
    c: Coincident(g28,g29)
    c: Coincident(g29,g11)
    c: Horizontal(g29)
    c: DistanceX(g29,g29) = 4  'bend_straight'
    c: Coincident(g30,g31)
    c: Coincident(g31,g32)
    c: Coincident(g32,g33)
    c: Coincident(g33,g30)
    c: Vertical(g30)
    c: Vertical(g32)
    c: Horizontal(g31)
    c: Horizontal(g33)
    c: Coincident(g34,g35)
    c: Coincident(g35,g36)
    c: Coincident(g36,g37)
    c: Coincident(g37,g34)
    c: Vertical(g34)
    c: Vertical(g36)
    c: Horizontal(g35)
    c: Horizontal(g37)
    c: Coincident(g39,g38)
    c: Tangent(g39,g33)
    c: Tangent(g39,g32)
    c: Tangent(g39,g31)
    c: Tangent(g39,g30)
    c: Diameter(g39) = 50  'block_width'
    c: Tangent(g37,g38)
    c: Tangent(g38,g36)
    c: Tangent(g38,g35)
    c: Tangent(g38,g34)
    c: Diameter(g38) = 42  'block_screw_spacing'
    c: Distance(g6,g-1) = 1  'plate_block_overlap'
    c: DistanceY(g-1,g7) = 3  'plate_overhang_outer'
    c: Coincident(g34,g1)
    c: Coincident(g36,g0)
    c: PointOnObject(g32,g-1)
    c: Distance(g32,g-1) = 6  'block_side_offset'
    c: Coincident(g40,g0)
    c: Coincident(g41,g1)
    c: Equal(g24,g40)
    c: Equal(g40,g41)
    c: Diameter(g41) = 5.5  'screw_head'
    c: DistanceY(g-1,g23) = 5  'side_screw_inset1'
    c: DistanceY(g-1,g25) = 22  'side_screw_inset2'
    c: Coincident(g12,g-1)
    c: DistanceX(g-1,g17) = 29.5  'height_stock_bed'
    c: DistanceX(g-1,g19) = 27.5  'height_stock_silicone'
    c: DistanceX(g-1,g21) = 33.5  'height_whop_silicone'
    c: DistanceX(g-1,g18) = 35.5  'height_whop_bed'
    c: Coincident(g43,g44)
    c: Coincident(g44,g42)
    c: Horizontal(g42)
    c: Horizontal(g43)
    c: Vertical(g44)
    c: PointOnObject(g20,g43)
    c: PointOnObject(g22,g43)
    c: PointOnObject(g16,g43)
    c: PointOnObject(g42,g-1)
    c: Coincident(g45,g46)
    c: Coincident(g46,g47)
    c: Coincident(g47,g48)
    c: Coincident(g48,g45)
    c: Vertical(g45)
    c: Vertical(g47)
    c: Horizontal(g46)
    c: Horizontal(g48)
    c: Coincident(g47,g42)
    c: PointOnObject(g43,g47)
    c: Vertical(g49)
    c: PointOnObject(g49,g12)
    c: PointOnObject(g49,g14)
    c: DistanceX(g-1,g45) = 2.5  'height_block_bottom'
    c: PointOnObject(g45,g14)
    c: DistanceX(g-1,g49) = 1  'height_bracket_bottom'
    c: DistanceX(g-1,g46) = 22.5  'height_block_top'
    c: DistanceX(g-1,g43) = 29  'height_component_top'
    c: DistanceX(g43,g22) = 4.5  'height_clear_whop'
    c: DistanceX(g19,g43) = 1.5  'height_crash_stock'
    c: Vertical(g20)
FEATURE [Sketcher::SketchObject] Sketch086  label="hrb_side_features_s"
  ArcFitTolerance = 0
  AttachmentSupport = -> [YZ_Plane138]
  ExternalTypes = [0]
  FullyConstrained = true
  MakeInternals = false
  MapMode = 5
  Placement = pos=(0,0,0) rot=(0.57735,0.57735,0.57735;2.0944rad)
  _ExternalGeoVersion = 0
  expr: .Constraints.cut_end = <<bracket_params>>.rear_overhang_inner + <<bracket_params>>.rear_side_extension + 1 mm
  expr: .Constraints.plate_overhang = <<bracket_params>>.rear_overhang_inner
  expr: .Constraints.screw_head = <<bracket_params>>.feature_screw_head
  expr: .Constraints.screw_height = <<bracket_params>>.feature_side_height + <<bracket_params>>.feature_deck_clear_bracket - <<bracket_params>>.height_extrusion / 2
  expr: .Constraints.screw_hole = <<bracket_params>>.feature_screw_hole
  expr: .Constraints.screw_inset1 = <<bracket_params>>.rear_side_screw_inset
  expr: .Constraints.screw_inset2 = <<bracket_params>>.rear_side_screw_inset + <<bracket_params>>.rear_side_screw_spacing
  expr: .Constraints.side_recess_top = <<bracket_params>>.feature_side_height + <<bracket_params>>.feature_deck_clear_bracket - <<bracket_params>>.height_extrusion + <<bracket_params>>.feature_side_recess
  sketch-geometry (9):
    g0: Circle CenterX=5 CenterY=-12.5 CenterZ=0 NormalX=0 NormalY=0 NormalZ=1 AngleXU=0 Radius=1.7
    g1: Circle CenterX=22 CenterY=-12.5 CenterZ=0 NormalX=0 NormalY=0 NormalZ=1 AngleXU=0 Radius=1.7
    g2: LineSegment [constr] StartX=5 StartY=-12.5 StartZ=0 EndX=22 EndY=-12.5 EndZ=0
    g3: Circle [constr] CenterX=5 CenterY=-12.5 CenterZ=0 NormalX=0 NormalY=0 NormalZ=1 AngleXU=0 Radius=2.75
    g4: Circle [constr] CenterX=22 CenterY=-12.5 CenterZ=0 NormalX=0 NormalY=0 NormalZ=1 AngleXU=0 Radius=2.75
    g5: LineSegment StartX=28 StartY=-3.5 StartZ=0 EndX=28 EndY=0 EndZ=0
    g6: LineSegment StartX=7 StartY=0 StartZ=0 EndX=7 EndY=-3.5 EndZ=0
    g7: LineSegment StartX=7 StartY=-3.5 StartZ=0 EndX=28 EndY=-3.5 EndZ=0
    g8: LineSegment StartX=7 StartY=0 StartZ=0 EndX=28 EndY=0 EndZ=0
  constraints (24):
    c: Coincident(g2,g0)
    c: Coincident(g2,g1)
    c: Horizontal(g2)
    c: Diameter(g0) = 3.4  'screw_hole'
    c: Equal(g1,g0)
    c: Coincident(g3,g0)
    c: Coincident(g4,g1)
    c: Diameter(g3) = 5.5  'screw_head'
    c: Equal(g3,g4)
    c: Coincident(g6,g7)
    c: Coincident(g7,g5)
    c: Vertical(g5)
    c: Vertical(g6)
    c: Horizontal(g7)
    c: PointOnObject(g5,g-1)
    c: Coincident(g8,g6)
    c: PointOnObject(g6,g-1)
    c: DistanceX(g-1,g6) = 7  'plate_overhang'
    c: Coincident(g8,g5)
    c: DistanceX(g-1,g5) = 28  'cut_end'
    c: DistanceY(g0,g-1) = 12.5  'screw_height'
    c: DistanceX(g-1,g0) = 5  'screw_inset1'
    c: DistanceX(g-1,g1) = 22  'screw_inset2'
    c: DistanceY(g6,g-1) = 3.5  'side_recess_top'
FEATURE [PartDesign::FeaturePython] BaseBend  label="hrb_block_plate"  # WARN: FeaturePython — macro-defined, semantics opaque (R4)
  BendSide = 0
  BendSketch = -> Sketch085
  MidPlane = false
  Reverse = false
  Suppressed = false
  length = 100
  radius = 1.6
  thickness = 1.5
  expr: radius = <<bracket_params>>.material_bend
  expr: thickness = <<bracket_params>>.material_thickness
FEATURE [PartDesign::FeaturePython] Bend  label="hrb_side_bend"  # WARN: FeaturePython — macro-defined, semantics opaque (R4)
  AutoMiter = true
  BaseFeature = -> BaseBend
  BendType = 1
  LengthList = [21.5]
  LengthSpec = 2
  NonperforationMaxLength = 5
  Perforate = false
  PerforationAngle = 0
  PerforationInitialLength = 5
  PerforationMaxLength = 5
  ReliefFactor = 0.7
  Suppressed = false
  UseReliefFactor = false
  angle = 90
  baseObject = -> BaseBend [Edge27]
  bendAList = [90]
  extend1 = 0
  extend2 = 0
  gap1 = 0
  gap2 = 0
  invert = false
  kfactor = 0.5
  length = 21.5
  maxExtendDist = 5
  minGap = 0.2
  minReliefGap = 1
  miterangle1 = 0
  miterangle2 = 0
  offset = 0
  radius = 1.6
  reliefType = 0
  reliefd = 1
  reliefw = 0.8
  sketchflip = false
  sketchinvert = false
  unfold = false
  expr: length = <<bracket_params>>.feature_side_height
  expr: radius = <<bracket_params>>.material_bend
FEATURE [Sketcher::SketchObject] Sketch087  label="hcs_ptc_s"
  ArcFitTolerance = 1e-06
  AttachmentSupport = -> [XY_Plane]
  ExternalTypes = [0]
  FullyConstrained = true
  MakeInternals = false
  MapMode = 5
  _ExternalGeoVersion = 0
  expr: .Constraints.hole_spacing = sqrt(<<block_params>>.ptc_screw_spacing_length ^ 2 + <<block_params>>.ptc_screw_spacing_width ^ 2)
  expr: .Constraints.screw_hole = <<block_params>>.strap_hole
  expr: .Constraints.width = <<block_params>>.strap_width
  sketch-geometry (6):
    g0: Circle CenterX=17.3971 CenterY=0 CenterZ=0 NormalX=0 NormalY=0 NormalZ=1 AngleXU=0 Radius=1.65
    g1: Circle CenterX=-17.3971 CenterY=0 CenterZ=0 NormalX=0 NormalY=0 NormalZ=1 AngleXU=0 Radius=1.65
    g2: LineSegment StartX=-17.3971 StartY=3.25 StartZ=0 EndX=17.3971 EndY=3.25 EndZ=0
    g3: LineSegment StartX=-17.3971 StartY=-3.25 StartZ=0 EndX=17.3971 EndY=-3.25 EndZ=0
    g4: ArcOfCircle CenterX=17.3971 CenterY=0 CenterZ=0 NormalX=0 NormalY=0 NormalZ=1 AngleXU=0 Radius=3.25 StartAngle=4.71239 EndAngle=7.85398
    g5: ArcOfCircle CenterX=-17.3971 CenterY=0 CenterZ=0 NormalX=0 NormalY=0 NormalZ=1 AngleXU=0 Radius=3.25 StartAngle=1.5708 EndAngle=4.71239
  constraints (13):
    c: Coincident(g4,g0)
    c: Coincident(g5,g1)
    c: Diameter(g1) = 3.3  'screw_hole'
    c: Equal(g5,g4)
    c: Equal(g1,g0)
    c: Diameter(g5) = 6.5  'width'
    c: Tangent(g2,g5) = 1.5708
    c: Tangent(g3,g5) = -1.5708
    c: Tangent(g2,g4) = 1.5708
    c: Tangent(g4,g3) = -1.5708
    c: Distance(g1,g0) = 34.7943  'hole_spacing'
    c: Symmetric(g0,g1,g-2)
    c: PointOnObject(g0,g-1)
FEATURE [Sketcher::SketchObject] Sketch088  label="hcs_tswitch_s"
  ArcFitTolerance = 1e-06
  AttachmentSupport = -> [XY_Plane139]
  ExternalTypes = [0]
  FullyConstrained = true
  MakeInternals = false
  MapMode = 5
  _ExternalGeoVersion = 0
  expr: .Constraints.hole_spacing = sqrt(<<block_params>>.tswitch_screw_spacing_length ^ 2 + <<block_params>>.tswitch_screw_spacing_width ^ 2)
  expr: .Constraints.screw_hole = <<block_params>>.strap_hole
  expr: .Constraints.width = <<block_params>>.strap_width
  sketch-geometry (6):
    g0: LineSegment StartX=7.88495 StartY=3.25 StartZ=0 EndX=-7.88495 EndY=3.25 EndZ=0
    g1: LineSegment StartX=7.88495 StartY=-3.25 StartZ=0 EndX=-7.88495 EndY=-3.25 EndZ=0
    g2: Circle CenterX=7.88495 CenterY=0 CenterZ=0 NormalX=0 NormalY=0 NormalZ=1 AngleXU=0 Radius=1.65
    g3: Circle CenterX=-7.88495 CenterY=0 CenterZ=0 NormalX=0 NormalY=0 NormalZ=1 AngleXU=0 Radius=1.65
    g4: ArcOfCircle CenterX=-7.88495 CenterY=0 CenterZ=0 NormalX=0 NormalY=0 NormalZ=1 AngleXU=0 Radius=3.25 StartAngle=1.5708 EndAngle=4.71239
    g5: ArcOfCircle CenterX=7.88495 CenterY=0 CenterZ=0 NormalX=0 NormalY=0 NormalZ=1 AngleXU=0 Radius=3.25 StartAngle=4.71239 EndAngle=7.85398
  constraints (13):
    c: Equal(g3,g2)
    c: Equal(g4,g5)
    c: Diameter(g3) = 3.3  'screw_hole'
    c: Diameter(g4) = 6.5  'width'
    c: Tangent(g4,g0) = -1.5708
    c: Tangent(g4,g1) = 1.5708
    c: Tangent(g0,g5) = -1.5708
    c: Tangent(g1,g5) = 1.5708
    c: Distance(g3,g2) = 15.7699  'hole_spacing'
    c: Coincident(g3,g4)
    c: Coincident(g2,g5)
    c: Symmetric(g3,g2,g-2)
    c: PointOnObject(g2,g-1)
FEATURE [PartDesign::FeaturePython] Extend  label="hrb_side_ext"  # WARN: FeaturePython — macro-defined, semantics opaque (R4)
  BaseFeature = -> Bend
  Offset = 0.02
  Refine = true
  Suppressed = false
  UseSubtraction = false
  baseObject = -> Bend [Face21]
  gap1 = 0
  gap2 = 0
  length = 20
  expr: length = <<bracket_params>>.rear_side_extension
FEATURE [PartDesign::Pocket] Pocket  label="hrb_side_features"
  BaseFeature = -> Extend
  Direction = (-1,0,0)
  Length = 1.5
  Length2 = 5
  Profile = -> Sketch086
  ReferenceAxis = -> Sketch086 [N_Axis]
  Refine = true
  SideType = 0
  Suppressed = false
  Type = 0
  Type2 = 0
  expr: Length = <<bracket_params>>.material_thickness
FEATURE [PartDesign::Fillet] Fillet  label="hrb_outer_flt"
  Base = -> Pocket [Edge2]
  BaseFeature = -> Pocket
  Radius = 1.5
  Refine = true
  SupportTransform = false
  Suppressed = false
  UseAllEdges = false
FEATURE [PartDesign::Fillet] Fillet014  label="hrb_side_flt"
  Base = -> Fillet [Edge59,Edge46,Edge65]
  BaseFeature = -> Fillet
  Radius = 4
  Refine = true
  SupportTransform = false
  Suppressed = false
  UseAllEdges = false
FEATURE [PartDesign::Fillet] Fillet015  label="hrb_ext_flt"
  Base = -> Fillet014 [Edge62]
  BaseFeature = -> Fillet014
  Radius = 1.5
  Refine = true
  SupportTransform = false
  Suppressed = false
  UseAllEdges = false
FEATURE [Sketcher::SketchObject] Sketch  label="hfd_base_s"
  ArcFitTolerance = 1e-06
  AttachmentSupport = -> [XY_Plane140]
  ExternalTypes = [0]
  FullyConstrained = true
  MakeInternals = false
  MapMode = 5
  _ExternalGeoVersion = 0
  expr: .Constraints.base_width = <<block_params>>.heatsink_width + 2 * <<bracket_params>>.feature_block_offset
  expr: .Constraints.ref_block_spacing = <<bracket_params>>.feature_block_offset
  expr: .Constraints.ref_block_width = <<block_params>>.heatsink_width
  sketch-geometry (65):
    g0: LineSegment [constr] StartX=21.7128 StartY=-20.5407 StartZ=0 EndX=-28.635 EndY=-28.6713 EndZ=0
    g1: LineSegment [constr] StartX=-28.635 StartY=-28.6713 StartZ=0 EndX=-20.5044 EndY=-79.019 EndZ=0
    g2: LineSegment [constr] StartX=-20.5044 StartY=-79.019 StartZ=0 EndX=29.8433 EndY=-70.8884 EndZ=0
    g3: LineSegment [constr] StartX=29.8433 StartY=-70.8884 StartZ=0 EndX=21.7128 EndY=-20.5407 EndZ=0
    g4: LineSegment [constr] StartX=2.46216 StartY=-23.6495 StartZ=0 EndX=2.781 EndY=-25.6239 EndZ=0
    g5: Circle [constr] CenterX=24 CenterY=-66.1595 CenterZ=0 NormalX=0 NormalY=0 NormalZ=1 AngleXU=0 Radius=2.25
    g6: Circle [constr] CenterX=-24 CenterY=-35.4187 CenterZ=0 NormalX=0 NormalY=0 NormalZ=1 AngleXU=0 Radius=2.25
    g7: Circle [constr] CenterX=-1.38618 CenterY=-50 CenterZ=0 NormalX=0 NormalY=0 NormalZ=1 AngleXU=0 Radius=16.25
    g8: LineSegment [constr] StartX=-5.43552 StartY=-24.9249 StartZ=0 EndX=-1.38618 EndY=-50 EndZ=0
    g9: LineSegment [constr] StartX=-1.38618 StartY=-50 StartZ=0 EndX=2.69506 EndY=-75.2726 EndZ=0
    g10: LineSegment [constr] StartX=-24.5856 StartY=-53.7464 StartZ=0 EndX=-1.38618 EndY=-50 EndZ=0
    g11: LineSegment [constr] StartX=-1.38618 StartY=-50 StartZ=0 EndX=25.7621 EndY=-45.6159 EndZ=0
    g12: LineSegment [constr] StartX=-25 StartY=50 StartZ=0 EndX=-25 EndY=0 EndZ=0
    g13: LineSegment [constr] StartX=-25 StartY=0 StartZ=0 EndX=25 EndY=0 EndZ=0
    g14: LineSegment [constr] StartX=25 StartY=0 StartZ=0 EndX=25 EndY=50 EndZ=0
    g15: LineSegment [constr] StartX=25 StartY=50 StartZ=0 EndX=-25 EndY=50 EndZ=0
    g16: LineSegment [constr] StartX=-24 StartY=-35.4187 StartZ=0 EndX=24 EndY=-66.1595 EndZ=0
    g17: LineSegment [constr] StartX=-21.1304 StartY=-53.1885 StartZ=0 EndX=-24 EndY=-35.4187 EndZ=0
    g18: LineSegment [constr] StartX=-24 StartY=-35.4187 StartZ=0 EndX=-4.25579 EndY=-32.2302 EndZ=0
    g19: LineSegment [constr] StartX=20.8115 StartY=-46.4153 StartZ=0 EndX=24 EndY=-66.1595 EndZ=0
    g20: LineSegment [constr] StartX=24 StartY=-66.1595 StartZ=0 EndX=1.80229 EndY=-69.7442 EndZ=0
    g21: LineSegment [constr] StartX=25 StartY=0 StartZ=0 EndX=31 EndY=0 EndZ=0
    g22: LineSegment [constr] StartX=-25 StartY=0 StartZ=0 EndX=-31 EndY=0 EndZ=0
    g23: LineSegment [constr] StartX=8.51935 StartY=0 StartZ=0 EndX=12.0875 EndY=-22.0951 EndZ=0
    g24: LineSegment [constr] StartX=-31 StartY=0 StartZ=0 EndX=-31 EndY=-50 EndZ=0
    g25: LineSegment [constr] StartX=-31 StartY=-50 StartZ=0 EndX=-31 EndY=-100 EndZ=0
    g26: LineSegment [constr] StartX=-31 StartY=-100 StartZ=0 EndX=-31 EndY=-150 EndZ=0
    g27: LineSegment [constr] StartX=31 StartY=0 StartZ=0 EndX=31 EndY=-50 EndZ=0
    g28: LineSegment [constr] StartX=31 StartY=-50 StartZ=0 EndX=31 EndY=-100 EndZ=0
    g29: LineSegment [constr] StartX=31 StartY=-100 StartZ=0 EndX=31 EndY=-150 EndZ=0
    g30: Circle [constr] CenterX=-24 CenterY=-35.4187 CenterZ=0 NormalX=0 NormalY=0 NormalZ=1 AngleXU=0 Radius=3.5
    g31: Circle [constr] CenterX=24 CenterY=-66.1595 CenterZ=0 NormalX=0 NormalY=0 NormalZ=1 AngleXU=0 Radius=3.5
    g32: LineSegment [constr] StartX=31 StartY=-66.1595 StartZ=0 EndX=27.5 EndY=-66.1595 EndZ=0
    g33: ArcOfCircle [constr] CenterX=9.43542 CenterY=-50.8861 CenterZ=0 NormalX=0 NormalY=0 NormalZ=1 AngleXU=0 Radius=16.9581 StartAngle=5.41384 EndAngle=6.44329
    g34: ArcOfCircle [constr] CenterX=-2.46465 CenterY=-50.1742 CenterZ=0 NormalX=0 NormalY=0 NormalZ=1 AngleXU=0 Radius=22.4076 StartAngle=2.53575 EndAngle=3.3017
    g35: LineSegment [constr] StartX=21.7128 StartY=-20.5407 StartZ=0 EndX=18.3957 EndY=0 EndZ=0
    g36: LineSegment [constr] StartX=2.46216 StartY=-23.6495 StartZ=0 EndX=-1.35696 EndY=0 EndZ=0
    g37: Circle CenterX=-24 CenterY=-35.4187 CenterZ=0 NormalX=0 NormalY=0 NormalZ=1 AngleXU=0 Radius=2
    g38: Circle CenterX=24 CenterY=-66.1595 CenterZ=0 NormalX=0 NormalY=0 NormalZ=1 AngleXU=0 Radius=2
    g39: LineSegment StartX=-31 StartY=0 StartZ=0 EndX=-31 EndY=-80 EndZ=0
    g40: LineSegment StartX=-31 StartY=-80 StartZ=0 EndX=31 EndY=-80 EndZ=0
    g41: LineSegment StartX=31 StartY=-80 StartZ=0 EndX=31 EndY=0 EndZ=0
    g42: LineSegment StartX=31 StartY=0 StartZ=0 EndX=-31 EndY=0 EndZ=0
    g43: LineSegment [constr] StartX=-31 StartY=-19.6 StartZ=0 EndX=-31 EndY=-36.4 EndZ=0
    g44: LineSegment [constr] StartX=-31 StartY=-36.4 StartZ=0 EndX=-28 EndY=-36.4 EndZ=0
    g45: LineSegment [constr] StartX=-28 StartY=-19.6 StartZ=0 EndX=-31 EndY=-19.6 EndZ=0
    g46: LineSegment [constr] StartX=-28 StartY=-19.6 StartZ=0 EndX=-28 EndY=-25.2 EndZ=0
    g47: LineSegment [constr] StartX=-28 StartY=-25.2 StartZ=0 EndX=-28 EndY=-30.8 EndZ=0
    g48: LineSegment [constr] StartX=-28 StartY=-30.8 StartZ=0 EndX=-28 EndY=-36.4 EndZ=0
    g49: LineSegment [constr] StartX=28 StartY=-19.6 StartZ=0 EndX=28 EndY=-25.2 EndZ=0
    g50: LineSegment [constr] StartX=28 StartY=-25.2 StartZ=0 EndX=28 EndY=-30.8 EndZ=0
    g51: LineSegment [constr] StartX=28 StartY=-30.8 StartZ=0 EndX=28 EndY=-36.4 EndZ=0
    g52: LineSegment [constr] StartX=28 StartY=-36.4 StartZ=0 EndX=31 EndY=-36.4 EndZ=0
    g53: LineSegment [constr] StartX=31 StartY=-36.4 StartZ=0 EndX=31 EndY=-19.6 EndZ=0
    g54: LineSegment [constr] StartX=31 StartY=-19.6 StartZ=0 EndX=28 EndY=-19.6 EndZ=0
    g55: LineSegment [constr] StartX=-28 StartY=-25.2 StartZ=0 EndX=-28 EndY=-30.8 EndZ=0
    g56: LineSegment [constr] StartX=-28 StartY=-30.8 StartZ=0 EndX=-25.2 EndY=-30.8 EndZ=0
    g57: LineSegment [constr] StartX=-25.2 StartY=-30.8 StartZ=0 EndX=-25.2 EndY=-25.2 EndZ=0
    g58: LineSegment [constr] StartX=-25.2 StartY=-25.2 StartZ=0 EndX=-28 EndY=-25.2 EndZ=0
    g59: LineSegment [constr] StartX=28 StartY=-25.2 StartZ=0 EndX=25.2 EndY=-25.2 EndZ=0
    g60: LineSegment [constr] StartX=25.2 StartY=-25.2 StartZ=0 EndX=25.2 EndY=-30.8 EndZ=0
    g61: LineSegment [constr] StartX=25.2 StartY=-30.8 StartZ=0 EndX=28 EndY=-30.8 EndZ=0
    g62: LineSegment [constr] StartX=28 StartY=-30.8 StartZ=0 EndX=28 EndY=-25.2 EndZ=0
    g63: LineSegment [constr] StartX=31 StartY=-28 StartZ=0 EndX=28 EndY=-28 EndZ=0
    g64: LineSegment [constr] StartX=-31 StartY=-28 StartZ=0 EndX=-28 EndY=-28 EndZ=0
  constraints (186):
    c: Coincident(g0,g1)
    c: Coincident(g1,g2)
    c: Coincident(g2,g3)
    c: Coincident(g3,g0)
    c: Parallel(g0,g2)
    c: Perpendicular(g2,g3)
    c: Perpendicular(g1,g2)
    c: Perpendicular(g0,g4)
    c: Diameter(g7) = 32.5  'fan_spec_open'
    c: Equal(g6,g5)
    c: Diameter(g5) = 4.5  'fan_spec_screw_diam'
    c: Coincident(g8,g9)
    c: Coincident(g8,g7)
    c: Perpendicular(g8,g0) = 4.71239
    c: Perpendicular(g9,g2) = 1.5708
    c: Coincident(g10,g7)
    c: Coincident(g10,g11)
    c: Perpendicular(g11,g3) = 1.5708
    c: Perpendicular(g10,g1) = 4.71239
    c: Distance(g8,g8) = 25.4  'fan_spec_center_offset1'
    c: Distance(g11,g11) = 27.5  'fan_spec_center_offset2'
    c: Coincident(g12,g13)
    c: Coincident(g13,g14)
    c: Coincident(g14,g15)
    c: Coincident(g15,g12)
    c: Vertical(g12)
    c: Vertical(g14)
    c: Horizontal(g13)
    c: Equal(g15,g12)
    c: Symmetric(g12,g14,g-2)
    c: Distance(g1,g1) = 51  'fan_spec_width1'
    c: Distance(g2,g2) = 51  'fan_spec_width2'
    c: Coincident(g16,g6)
    c: Coincident(g16,g5)
    c: Distance(g16,g16) = 57  'fan_spec_screw_spacing'
    c: Coincident(g17,g18)
    c: Coincident(g19,g20)
    c: Perpendicular(g20,g9) = 1.5708
    c: Perpendicular(g19,g11) = 1.5708
    c: Perpendicular(g18,g8) = 4.71239
    c: Perpendicular(g17,g10) = 4.71239
    c: Coincident(g17,g6)
    c: Coincident(g5,g19)
    c: Distance(g18,g18) = 20  'fan_spec_screw1_offset2'
    c: Distance(g17,g17) = 18  'fan_spec_screw1_offset1'
    c: Distance(g19,g19) = 20  'fan_spec_screw2_offset1'
    c: Distance(g20,g20) = 22.4853  'fan_spec_screw2_offset2'
    c: Distance(g4,g0) = 19.5  'fan_spec_opening_width'
    c: Distance(g4,g4) = 2  'fan_spec_opening_depth'
    c: Coincident(g21,g13)
    c: Horizontal(g21)
    c: Coincident(g22,g12)
    c: Horizontal(g22)
    c: Equal(g21,g22)
    c: DistanceX(g15,g15) = 50  'ref_block_width'
    c: DistanceX(g21,g21) = 6  'ref_block_spacing'
    c: Perpendicular(g23,g0) = 4.71239
    c: PointOnObject(g13,g-1)
    c: PointOnObject(g23,g-1)
    c: Coincident(g22,g24)
    c: Coincident(g24,g25)
    c: Coincident(g25,g26)
    c: Coincident(g21,g27)
    c: Coincident(g27,g28)
    c: Coincident(g28,g29)
    c: Equal(g29,g26)
    c: Equal(g28,g25)
    c: Equal(g27,g24)
    c: Equal(g26,g25)
    c: Equal(g28,g27)
    c: Equal(g24,g12)
    c: Vertical(g24)
    c: Vertical(g25)
    c: Vertical(g26)
    c: Vertical(g27)
    c: Vertical(g28)
    c: Vertical(g29)
    c: Symmetric(g4,g0,g23)
    c: Distance(g23,g23) = 22.3813  'duct_flow_length'
    c: DistanceY(g6,g-1) = 35.4187  'screw1_offset_y'
    c: DistanceX(g6,g-1) = 24  'screw1_offset_x'
    c: DistanceY(g5,g-1) = 66.1595  'screw2_offset_y'
    c: DistanceX(g-1,g5) = 24  'screw2_offset_x'
    c: Coincident(g30,g6)
    c: Coincident(g31,g5)
    c: Equal(g30,g31)
    c: Diameter(g31) = 7  'fan_spec_screw_knob'
    c: Horizontal(g32)
    c: PointOnObject(g32,g28)
    c: DistanceX(g32,g32) = 3.5  'screw_knob_clearance'
    c: Perpendicular(g32,g31) = 4.71239
    c: Tangent(g33,g3) = -1.5708
    c: PointOnObject(g33,g16)
    c: Tangent(g34,g1) = -1.5708
    c: PointOnObject(g34,g16)
    c: Distance(g34,g6) = 3.7  'fan_spec_aprox_scroll_intersect1'
    c: PointOnObject(g34,g10)
    c: Distance(g33,g5) = 4.3  'fan_spec_aprox_scroll_intersect2'
    c: Distance(g33,g0) = 28  'fan_spec_aprox_scroll_intersect3'
    c: DistanceY(g7,g-1) = 50  'fan_center_offset'
    c: Coincident(g36,g4)
    c: Coincident(g35,g0)
    c: PointOnObject(g35,g-1)
    c: PointOnObject(g36,g-1)
    c: Parallel(g23,g35)
    c: Parallel(g23,g36)
    c: Angle(g-1,g0) = 0.160106  'fan_angle'
    c: Coincident(g37,g6)
    c: Coincident(g38,g5)
    c: Equal(g37,g38)
    c: Diameter(g37) = 4  'fan_screw_insert'
    c: DistanceY(g0,g-1) = 20.5407  'fan_corner_offset_y'
    c: DistanceX(g-1,g0) = 21.7128  'fan_corner_offset_x'
    c: Coincident(g39,g40)
    c: Coincident(g40,g41)
    c: Coincident(g41,g42)
    c: Coincident(g42,g39)
    c: Vertical(g39)
    c: Vertical(g41)
    c: Horizontal(g40)
    c: Symmetric(g41,g39,g-2)
    c: PointOnObject(g39,g-1)
    c: DistanceY(g41,g41) = 80  'base_length'
    c: DistanceX(g40,g40) = 62  'base_width'
    c: Coincident(g43,g44)
    c: Coincident(g45,g43)
    c: Vertical(g43)
    c: Horizontal(g44)
    c: Horizontal(g45)
    c: Coincident(g45,g46)
    c: Vertical(g46)
    c: Coincident(g46,g47)
    c: Vertical(g47)
    c: Coincident(g47,g48)
    c: Coincident(g48,g44)
    c: Vertical(g48)
    c: Coincident(g49,g50)
    c: Vertical(g50)
    c: Coincident(g50,g51)
    c: Vertical(g51)
    c: Coincident(g51,g52)
    c: Horizontal(g52)
    c: Coincident(g52,g53)
    c: Vertical(g53)
    c: Coincident(g53,g54)
    c: Coincident(g54,g49)
    c: Horizontal(g54)
    c: Equal(g48,g47)
    c: Equal(g47,g46)
    c: Equal(g51,g50)
    c: Equal(g50,g49)
    c: Equal(g50,g47)
    c: Coincident(g55,g56)
    c: Coincident(g56,g57)
    c: Coincident(g57,g58)
    c: Coincident(g58,g55)
    c: Vertical(g57)
    c: Horizontal(g56)
    c: Horizontal(g58)
    c: Coincident(g55,g46)
    c: Coincident(g59,g60)
    c: Coincident(g60,g61)
    c: Coincident(g61,g62)
    c: Coincident(g62,g59)
    c: Horizontal(g59)
    c: Horizontal(g61)
    c: Vertical(g60)
    c: Coincident(g59,g49)
    c: Coincident(g61,g50)
    c: Coincident(g55,g47)
    c: Equal(g58,g59)
    c: Equal(g54,g45)
    c: Vertical(g49)
    c: Distance(g45,g45) = 3  'estimated_side_thickness'
    c: Distance(g58,g58) = 2.8  'estimated_screw_head_height'
    c: DistanceY(g57,g57) = 5.6  'estimated_screw_head_width'
    c: PointOnObject(g64,g47)
    c: PointOnObject(g63,g51)
    c: Symmetric(g50,g49,g63)
    c: Symmetric(g46,g47,g64)
    c: PointOnObject(g63,g53)
    c: PointOnObject(g64,g43)
    c: PointOnObject(g43,g39)
    c: PointOnObject(g53,g41)
    c: DistanceY(g63,g-1) = 28  'estimated_side_screw_offset_right'
    c: DistanceY(g64,g-1) = 28  'estimated_side_screw_offset_left'
FEATURE [PartDesign::Pad] Pad  label="hfd_base"
  Direction = (0,0,1)
  Length = 3
  Length2 = 10
  Profile = -> Sketch
  ReferenceAxis = -> Sketch [N_Axis]
  Refine = true
  Reversed = true
  SideType = 0
  Suppressed = false
  Type = 0
  Type2 = 0
FEATURE [Sketcher::SketchObject] Sketch089  label="hfd_side_s"
  ArcFitTolerance = 1e-06
  AttachmentSupport = -> [XZ_Plane140]
  ExternalTypes = [0]
  FullyConstrained = true
  MakeInternals = false
  MapMode = 5
  Placement = pos=(0,0,0) rot=(1,0,0;1.5708rad)
  _ExternalGeoVersion = 0
  expr: .Constraints.base_thickness = <<hfd_base>>.Length
  expr: .Constraints.base_width = <<hfd_base_s>>.Constraints.base_width
  expr: .Constraints.duct_edge = <<bracket_params>>.feature_block_offset
  sketch-geometry (31):
    g0: LineSegment StartX=-31 StartY=0 StartZ=0 EndX=-28 EndY=0 EndZ=0
    g1: LineSegment StartX=-28 StartY=0 StartZ=0 EndX=-28 EndY=13 EndZ=0
    g2: LineSegment StartX=-28 StartY=13 StartZ=0 EndX=-31 EndY=13 EndZ=0
    g3: LineSegment [constr] StartX=-31 StartY=9 StartZ=0 EndX=-32 EndY=9 EndZ=0
    g4: LineSegment [constr] StartX=-32 StartY=9 StartZ=0 EndX=-32 EndY=3 EndZ=0
    g5: LineSegment [constr] StartX=-32 StartY=3 StartZ=0 EndX=-31 EndY=3 EndZ=0
    g6: LineSegment StartX=31 StartY=0 StartZ=0 EndX=28 EndY=0 EndZ=0
    g7: LineSegment StartX=28 StartY=0 StartZ=0 EndX=28 EndY=13 EndZ=0
    g8: LineSegment StartX=28 StartY=13 StartZ=0 EndX=31 EndY=13 EndZ=0
    g9: LineSegment [constr] StartX=31 StartY=9 StartZ=0 EndX=32 EndY=9 EndZ=0
    g10: LineSegment [constr] StartX=32 StartY=9 StartZ=0 EndX=32 EndY=3 EndZ=0
    g11: LineSegment [constr] StartX=32 StartY=3 StartZ=0 EndX=31 EndY=3 EndZ=0
    g12: LineSegment [constr] StartX=-28 StartY=13 StartZ=0 EndX=28 EndY=13 EndZ=0
    g13: LineSegment [constr] StartX=-31 StartY=9 StartZ=0 EndX=31 EndY=9 EndZ=0
    g14: LineSegment [constr] StartX=-31 StartY=3 StartZ=0 EndX=31 EndY=3 EndZ=0
    g15: LineSegment [constr] StartX=-32 StartY=6 StartZ=0 EndX=-31 EndY=6 EndZ=0
    g16: LineSegment [constr] StartX=-31 StartY=6 StartZ=0 EndX=0 EndY=6 EndZ=0
    g17: LineSegment [constr] StartX=0 StartY=6 StartZ=0 EndX=31 EndY=6 EndZ=0
    g18: LineSegment [constr] StartX=31 StartY=6 StartZ=0 EndX=32 EndY=6 EndZ=0
    g19: LineSegment [constr] StartX=-10 StartY=16 StartZ=0 EndX=-10 EndY=-4 EndZ=0
    g20: LineSegment [constr] StartX=-10 StartY=-4 StartZ=0 EndX=10 EndY=-4 EndZ=0
    g21: LineSegment [constr] StartX=10 StartY=-4 StartZ=0 EndX=10 EndY=16 EndZ=0
    g22: LineSegment [constr] StartX=10 StartY=16 StartZ=0 EndX=-10 EndY=16 EndZ=0
    g23: Circle [constr] CenterX=0 CenterY=6 CenterZ=0 NormalX=0 NormalY=0 NormalZ=1 AngleXU=0 Radius=10
    g24: LineSegment [constr] StartX=-28 StartY=0 StartZ=0 EndX=-28 EndY=-3 EndZ=0
    g25: LineSegment [constr] StartX=0 StartY=15 StartZ=0 EndX=28 EndY=15 EndZ=0
    g26: LineSegment [constr] StartX=0 StartY=16.2 StartZ=0 EndX=28 EndY=16.2 EndZ=0
    g27: LineSegment [constr] StartX=25 StartY=16.2 StartZ=0 EndX=25 EndY=13 EndZ=0
    g28: LineSegment [constr] StartX=25.4 StartY=16.2 StartZ=0 EndX=28 EndY=13.6 EndZ=0
    g29: LineSegment StartX=-31 StartY=0 StartZ=0 EndX=-31 EndY=13 EndZ=0
    g30: LineSegment StartX=31 StartY=13 StartZ=0 EndX=31 EndY=0 EndZ=0
  constraints (99):
    c: Coincident(g0,g1)
    c: Vertical(g1)
    c: Coincident(g1,g2)
    c: Coincident(g3,g4)
    c: Coincident(g4,g5)
    c: Coincident(g6,g7)
    c: Vertical(g7)
    c: Coincident(g7,g8)
    c: Horizontal(g8)
    c: Coincident(g9,g10)
    c: Coincident(g10,g11)
    c: Coincident(g12,g1)
    c: Coincident(g12,g7)
    c: Horizontal(g12)
    c: Horizontal(g13)
    c: Coincident(g14,g5)
    c: Horizontal(g14)
    c: Vertical(g4)
    c: Horizontal(g2)
    c: Vertical(g10)
    c: PointOnObject(g6,g-1)
    c: PointOnObject(g0,g-1)
    c: PointOnObject(g0,g-1)
    c: Equal(g2,g8)
    c: Symmetric(g0,g6,g-2)
    c: DistanceX(g2,g8) = 62  'base_width'
    c: Distance(g2,g2) = 3  'side_width'
    c: Horizontal(g15)
    c: Coincident(g15,g16)
    c: Horizontal(g16)
    c: Coincident(g16,g17)
    c: Horizontal(g17)
    c: Coincident(g17,g18)
    c: Equal(g15,g18)
    c: Equal(g17,g16)
    c: PointOnObject(g16,g-2)
    c: PointOnObject(g15,g4)
    c: PointOnObject(g18,g10)
    c: Symmetric(g10,g9,g18)
    c: Horizontal(g9)
    c: Horizontal(g11)
    c: Horizontal(g3)
    c: Horizontal(g5)
    c: DistanceY(g4,g4) = 6  'tab_width'
    c: Coincident(g19,g20)
    c: Coincident(g20,g21)
    c: Coincident(g21,g22)
    c: Coincident(g22,g19)
    c: Vertical(g19)
    c: Vertical(g21)
    c: Horizontal(g20)
    c: Horizontal(g22)
    c: Tangent(g23,g22)
    c: Tangent(g23,g19)
    c: Tangent(g23,g20)
    c: Tangent(g23,g21)
    c: DistanceX(g22,g22) = 20  'extrusion_width'
    c: Coincident(g23,g16)
    c: Coincident(g24,g0)
    c: DistanceY(g24,g24) = 3  'base_thickness'
    c: DistanceY(g19,g24) = 1  'base_rise'
    c: Distance(g3,g3) = 1  'tab_depth'
    c: DistanceY(g1,g19) = 3  'side_recess'
    c: DistanceY(g0,g5) = 3  'height_side_to_tab'
    c: DistanceY(g24,g4) = 6  'height_base_to_tab'
    c: Distance(g2,g3) = 4  'height_side_above_tab'
    c: Vertical(g24)
    c: DistanceY(g24,g7) = 16  'side_height'
    c: Horizontal(g25)
    c: Horizontal(g26)
    c: PointOnObject(g25,g7)
    c: PointOnObject(g26,g7)
    c: PointOnObject(g25,g-2)
    c: PointOnObject(g26,g-2)
    c: DistanceY(g-1,g25) = 15  'fan_top'
    c: DistanceY(g25,g26) = 1.2  'estimate_duct_thick'
    c: PointOnObject(g27,g26)
    c: PointOnObject(g27,g12)
    c: Vertical(g27)
    c: DistanceX(g27,g8) = 6  'duct_edge'
    c: PointOnObject(g28,g26)
    c: PointOnObject(g28,g7)
    c: Angle(g28,g26) = 0.785398  'estimate_duct_chmf_angle'
    c: Distance(g26,g28) = 2.6  'estimate_duct_chmf'
    c: Coincident(g29,g0)
    c: Coincident(g29,g2)
    c: Vertical(g29)
    c: Coincident(g3,g13)
    c: Coincident(g9,g13)
    c: Coincident(g11,g14)
    c: Coincident(g30,g8)
    c: Coincident(g30,g6)
    c: Vertical(g30)
    c: PointOnObject(g3,g29)
    c: PointOnObject(g15,g29)
    c: PointOnObject(g5,g29)
    c: PointOnObject(g9,g30)
    c: PointOnObject(g11,g30)
    c: Distance(g-1,g16) = 6  'tab_plane'
FEATURE [PartDesign::Pad] Pad023  label="hfd_side"
  BaseFeature = -> Pad
  Direction = (0,-1,2e-16)
  Length = 80
  Length2 = 10
  Profile = -> Sketch089
  ReferenceAxis = -> Sketch089 [N_Axis]
  Refine = true
  SideType = 0
  Suppressed = false
  Type = 0
  Type2 = 0
  expr: Length = <<hfd_base_s>>.Constraints.base_length
FEATURE [Sketcher::SketchObject] Sketch090  label="hfd_side_tabs_s"
  ArcFitTolerance = 1e-06
  AttachmentOffset = pos=(0,0,6) rot=(0,0,1;0rad)
  AttachmentSupport = -> [XY_Plane140]
  ExternalTypes = [0]
  FullyConstrained = true
  MakeInternals = false
  MapMode = 5
  Placement = pos=(0,0,6) rot=(0,0,1;0rad)
  _ExternalGeoVersion = 0
  expr: .AttachmentOffset.Base.z = <<hfd_side_s>>.Constraints.tab_plane
  expr: .Constraints.base_length = <<hfd_base_s>>.Constraints.base_length
  expr: .Constraints.base_width = <<hfd_base_s>>.Constraints.base_width
  sketch-geometry (29):
    g0: LineSegment StartX=-32 StartY=-7 StartZ=0 EndX=-32 EndY=-23 EndZ=0
    g1: LineSegment StartX=-32 StartY=-23 StartZ=0 EndX=-31 EndY=-23 EndZ=0
    g2: LineSegment StartX=-31 StartY=-23 StartZ=0 EndX=-31 EndY=-7 EndZ=0
    g3: LineSegment StartX=-31 StartY=-7 StartZ=0 EndX=-32 EndY=-7 EndZ=0
    g4: LineSegment StartX=-32 StartY=-39 StartZ=0 EndX=-32 EndY=-73 EndZ=0
    g5: LineSegment StartX=-32 StartY=-73 StartZ=0 EndX=-31 EndY=-73 EndZ=0
    g6: LineSegment StartX=-31 StartY=-73 StartZ=0 EndX=-31 EndY=-39 EndZ=0
    g7: LineSegment StartX=-31 StartY=-39 StartZ=0 EndX=-32 EndY=-39 EndZ=0
    g8: LineSegment StartX=31 StartY=-7 StartZ=0 EndX=31 EndY=-23 EndZ=0
    g9: LineSegment StartX=31 StartY=-23 StartZ=0 EndX=32 EndY=-23 EndZ=0
    g10: LineSegment StartX=32 StartY=-23 StartZ=0 EndX=32 EndY=-7 EndZ=0
    g11: LineSegment StartX=32 StartY=-7 StartZ=0 EndX=31 EndY=-7 EndZ=0
    g12: LineSegment StartX=31 StartY=-40.5 StartZ=0 EndX=31 EndY=-73 EndZ=0
    g13: LineSegment StartX=31 StartY=-73 StartZ=0 EndX=32 EndY=-73 EndZ=0
    g14: LineSegment StartX=32 StartY=-73 StartZ=0 EndX=32 EndY=-40.5 EndZ=0
    g15: LineSegment StartX=32 StartY=-40.5 StartZ=0 EndX=31 EndY=-40.5 EndZ=0
    g16: LineSegment [constr] StartX=-31 StartY=-23 StartZ=0 EndX=-31 EndY=-39 EndZ=0
    g17: LineSegment [constr] StartX=31 StartY=-23 StartZ=0 EndX=31 EndY=-40.5 EndZ=0
    g18: LineSegment [constr] StartX=31 StartY=-73 StartZ=0 EndX=31 EndY=-80 EndZ=0
    g19: LineSegment [constr] StartX=31 StartY=-80 StartZ=0 EndX=-31 EndY=-80 EndZ=0
    g20: LineSegment [constr] StartX=-31 StartY=-80 StartZ=0 EndX=-31 EndY=-73 EndZ=0
    g21: LineSegment [constr] StartX=-31 StartY=-7 StartZ=0 EndX=-31 EndY=0 EndZ=0
    g22: LineSegment [constr] StartX=31 StartY=-7 StartZ=0 EndX=31 EndY=0 EndZ=0
    g23: LineSegment [constr] StartX=0 StartY=-28 StartZ=0 EndX=-32 EndY=-28 EndZ=0
    g24: LineSegment [constr] StartX=0 StartY=-28 StartZ=0 EndX=32 EndY=-28 EndZ=0
    g25: LineSegment [constr] StartX=32 StartY=-23 StartZ=0 EndX=32 EndY=-28 EndZ=0
    g26: LineSegment [constr] StartX=32 StartY=-28 StartZ=0 EndX=32 EndY=-40.5 EndZ=0
    g27: LineSegment [constr] StartX=-32 StartY=-23 StartZ=0 EndX=-32 EndY=-28 EndZ=0
    g28: LineSegment [constr] StartX=-32 StartY=-28 StartZ=0 EndX=-32 EndY=-39 EndZ=0
  constraints (85):
    c: Coincident(g0,g1)
    c: Coincident(g1,g2)
    c: Coincident(g2,g3)
    c: Coincident(g3,g0)
    c: Vertical(g0)
    c: Vertical(g2)
    c: Horizontal(g1)
    c: Horizontal(g3)
    c: Coincident(g4,g5)
    c: Coincident(g5,g6)
    c: Coincident(g6,g7)
    c: Coincident(g7,g4)
    c: Vertical(g4)
    c: Vertical(g6)
    c: Horizontal(g5)
    c: Horizontal(g7)
    c: Coincident(g8,g9)
    c: Coincident(g9,g10)
    c: Coincident(g10,g11)
    c: Coincident(g11,g8)
    c: Vertical(g8)
    c: Vertical(g10)
    c: Horizontal(g9)
    c: Horizontal(g11)
    c: Coincident(g12,g13)
    c: Coincident(g13,g14)
    c: Coincident(g14,g15)
    c: Coincident(g15,g12)
    c: Vertical(g12)
    c: Vertical(g14)
    c: Horizontal(g13)
    c: Horizontal(g15)
    c: Coincident(g16,g1)
    c: Coincident(g16,g6)
    c: Coincident(g17,g8)
    c: Coincident(g17,g12)
    c: Vertical(g17)
    c: Coincident(g18,g12)
    c: Coincident(g19,g18)
    c: Horizontal(g19)
    c: Coincident(g20,g19)
    c: Coincident(g20,g5)
    c: Coincident(g21,g2)
    c: PointOnObject(g21,g-1)
    c: Coincident(g22,g8)
    c: Vertical(g21)
    c: Vertical(g22)
    c: Vertical(g16)
    c: Vertical(g20)
    c: Vertical(g18)
    c: Equal(g1,g9)
    c: Equal(g9,g15)
    c: Equal(g15,g7)
    c: Distance(g3,g3) = 1  'tab_depth'
    c: Symmetric(g21,g22,g-2)
    c: DistanceX(g21,g22) = 62  'base_width'
    c: DistanceY(g18,g-1) = 80  'base_length'
    c: Equal(g20,g18)
    c: Equal(g21,g22)
    c: DistanceY(g21,g21) = 7  'end_offset1'
    c: DistanceY(g20,g20) = 7  'end_offset2'
    c: PointOnObject(g23,g-2)
    c: PointOnObject(g24,g-2)
    c: Coincident(g25,g9)
    c: Coincident(g26,g25)
    c: Coincident(g26,g14)
    c: Coincident(g27,g0)
    c: Coincident(g28,g27)
    c: Coincident(g28,g4)
    c: Vertical(g27)
    c: Vertical(g25)
    c: Coincident(g24,g25)
    c: Coincident(g23,g27)
    c: Horizontal(g24)
    c: Horizontal(g23)
    c: DistanceY(g10,g10) = 16  'tab1_right'
    c: DistanceY(g0,g0) = 16  'tab1_left'
    c: DistanceY(g4,g4) = 34  'tab2_left'
    c: DistanceY(g14,g14) = 32.5  'tab2_right'
    c: DistanceY(g23,g-1) = 28  'screw_placement_left'
    c: DistanceY(g24,g-1) = 28  'screw_placement_right'
    c: DistanceY(g27,g27) = 5  'nut_clear_left_front'
    c: Distance(g25,g25) = 5  'nut_clear_right_front'
    c: Distance(g28,g28) = 11  'nut_clear_left_rear'
    c: Distance(g26,g26) = 12.5  'nut_clear_right_rear'
FEATURE [PartDesign::Pad] Pad024  label="hfd_side_tabs"
  BaseFeature = -> Pad023
  Direction = (0,0,1)
  Length = 6
  Length2 = 10
  Profile = -> Sketch090
  ReferenceAxis = -> Sketch090 [N_Axis]
  Refine = true
  SideType = 0
  Suppressed = false
  Type = 0
  Type2 = 0
  expr: Length = <<hfd_side_s>>.Constraints.tab_width
FEATURE [PartDesign::Chamfer] Chamfer  label="hfd_side_tab_chmf"
  Angle = 45
  Base = -> Pad024 [Edge67,Edge70,Edge75,Edge78,Edge58,Edge62,Edge50,Edge54]
  BaseFeature = -> Pad024
  ChamferType = 0
  FlipDirection = false
  Refine = true
  Size = 0.6
  Size2 = 1
  SupportTransform = false
  Suppressed = false
  UseAllEdges = false
FEATURE [PartDesign::Fillet] Fillet016  label="hfd_side_tab_flt"
  Base = -> Chamfer [Edge82,Edge7,Edge1,Edge52,Edge45,Edge94,Edge87,Edge75]
  BaseFeature = -> Chamfer
  Radius = 0.8
  Refine = true
  SupportTransform = false
  Suppressed = false
  UseAllEdges = false
FEATURE [Sketcher::SketchObject] Sketch091  label="hfd_side_screw_left_s"
  ArcFitTolerance = 1e-06
  AttachmentSupport = -> [YZ_Plane140]
  ExternalTypes = [0]
  FullyConstrained = true
  MakeInternals = false
  MapMode = 5
  Placement = pos=(0,0,0) rot=(0.57735,0.57735,0.57735;2.0944rad)
  _ExternalGeoVersion = 0
  expr: .Constraints.screw_height = <<hfd_side_s>>.Constraints.tab_plane
  expr: .Constraints.screw_offset = <<hfd_side_tabs_s>>.Constraints.screw_placement_left
  sketch-geometry (2):
    g0: Circle CenterX=-28 CenterY=6 CenterZ=0 NormalX=0 NormalY=0 NormalZ=1 AngleXU=0 Radius=1.7
    g1: Circle [constr] CenterX=-28 CenterY=6 CenterZ=0 NormalX=0 NormalY=0 NormalZ=1 AngleXU=0 Radius=2.8
  constraints (5):
    c: Coincident(g1,g0)
    c: Diameter(g0) = 3.4  'hole_diam'
    c: Diameter(g1) = 5.6  'screw_head'
    c: DistanceY(g-1,g0) = 6  'screw_height'
    c: DistanceX(g0,g-1) = 28  'screw_offset'
FEATURE [PartDesign::Pocket] Pocket031  label="hfd_side_screw_left"
  BaseFeature = -> Fillet016
  Direction = (-1,0,0)
  Length = 5
  Length2 = 5
  Profile = -> Sketch091
  ReferenceAxis = -> Sketch091 [N_Axis]
  Refine = true
  SideType = 0
  Suppressed = false
  Type = 1
  Type2 = 0
FEATURE [Sketcher::SketchObject] Sketch092  label="hfd_side_screw_right_s"
  ArcFitTolerance = 1e-06
  AttachmentSupport = -> [YZ_Plane140]
  ExternalTypes = [0]
  FullyConstrained = true
  MakeInternals = false
  MapMode = 5
  Placement = pos=(0,0,0) rot=(0.57735,0.57735,0.57735;2.0944rad)
  _ExternalGeoVersion = 0
  expr: .Constraints.hole_diam = <<hfd_side_screw_left_s>>.Constraints.hole_diam
  expr: .Constraints.screw_head = <<hfd_side_screw_left_s>>.Constraints.screw_head
  expr: .Constraints.screw_height = <<hfd_side_s>>.Constraints.tab_plane
  expr: .Constraints.screw_offset = <<hfd_side_tabs_s>>.Constraints.screw_placement_right
  sketch-geometry (2):
    g0: Circle CenterX=-28 CenterY=6 CenterZ=0 NormalX=0 NormalY=0 NormalZ=1 AngleXU=0 Radius=1.7
    g1: Circle [constr] CenterX=-28 CenterY=6 CenterZ=0 NormalX=0 NormalY=0 NormalZ=1 AngleXU=0 Radius=2.8
  constraints (5):
    c: Coincident(g1,g0)
    c: Diameter(g0) = 3.4  'hole_diam'
    c: Diameter(g1) = 5.6  'screw_head'
    c: DistanceY(g-1,g0) = 6  'screw_height'
    c: DistanceX(g0,g-1) = 28  'screw_offset'
FEATURE [PartDesign::Pocket] Pocket032  label="hfd_side_screw_right"
  BaseFeature = -> Pocket031
  Direction = (-1,0,0)
  Length = 5
  Length2 = 5
  Profile = -> Sketch092
  ReferenceAxis = -> Sketch092 [N_Axis]
  Refine = true
  Reversed = true
  SideType = 0
  Suppressed = false
  Type = 1
  Type2 = 0
FEATURE [Sketcher::SketchObject] Sketch093  label="hfd_duct_wall_s"
  ArcFitTolerance = 1e-06
  AttachmentSupport = -> [XY_Plane140]
  ExternalTypes = [0]
  FullyConstrained = false
  MakeInternals = false
  MapMode = 5
  _ExternalGeoVersion = 0
  expr: .Constraints.block_width = <<hfd_base_s>>.Constraints.ref_block_width
  expr: .Constraints.fan_angle = <<hfd_base_s>>.Constraints.fan_angle
  expr: .Constraints.fan_corner_x = <<hfd_base_s>>.Constraints.fan_corner_offset_x
  expr: .Constraints.fan_corner_y = <<hfd_base_s>>.Constraints.fan_corner_offset_y
  expr: .Constraints.fan_open_depth = <<hfd_base_s>>.Constraints.fan_spec_opening_depth
  expr: .Constraints.fan_opening = <<hfd_base_s>>.Constraints.fan_spec_opening_width
  expr: .Constraints.inner_width = <<hfd_side_s>>.Constraints.base_width - 2 * <<hfd_side_s>>.Constraints.side_width
  sketch-geometry (40):
    g0: LineSegment [constr] StartX=2.46216 StartY=-23.6495 StartZ=0 EndX=2.781 EndY=-25.6239 EndZ=0
    g1: LineSegment [constr] StartX=2.781 StartY=-25.6239 StartZ=0 EndX=22.0316 EndY=-22.5151 EndZ=0
    g2: LineSegment [constr] StartX=22.0316 StartY=-22.5151 StartZ=0 EndX=21.7128 EndY=-20.5407 EndZ=0
    g3: LineSegment [constr] StartX=21.7128 StartY=-20.5407 StartZ=0 EndX=2.46216 EndY=-23.6495 EndZ=0
    g4: LineSegment [constr] StartX=-25 StartY=0 StartZ=0 EndX=25 EndY=0 EndZ=0
    g5: LineSegment StartX=21.8495 StartY=-19.5057 StartZ=0 EndX=22.3278 EndY=-22.4673 EndZ=0
    g6: LineSegment StartX=23.6 StartY=0 StartZ=0 EndX=23.6 EndY=-1 EndZ=0
    g7: LineSegment StartX=-23.6 StartY=0 StartZ=0 EndX=-23.6 EndY=-1 EndZ=0
    g8: LineSegment [constr] StartX=-25 StartY=0 StartZ=0 EndX=-23.6 EndY=0 EndZ=0
    g9: LineSegment [constr] StartX=25 StartY=0 StartZ=0 EndX=23.6 EndY=0 EndZ=0
    g10: LineSegment [constr] StartX=21.7128 StartY=-20.5407 StartZ=0 EndX=22.0089 EndY=-20.4929 EndZ=0
    g11: LineSegment [constr] StartX=2.46216 StartY=-23.6495 StartZ=0 EndX=2.16599 EndY=-23.6973 EndZ=0
    g12: LineSegment [constr] StartX=2.48484 StartY=-25.6717 StartZ=0 EndX=22.3278 EndY=-22.4673 EndZ=0
    g13: LineSegment StartX=2.48484 StartY=-25.6717 StartZ=0 EndX=2.00657 EndY=-22.7101 EndZ=0
    g14: LineSegment [constr] StartX=2.00657 StartY=-22.7101 StartZ=0 EndX=21.8495 EndY=-19.5057 EndZ=0
    g15-g18: Circle [constr] x4 (B-spline internal-alignment scaffolding for g19; pole/knot coordinates omitted)
    g19: BSplineCurve PolesCount=4 KnotsCount=2 Degree=3 IsPeriodic=0
    g20: GeomPoint [constr] X=21.8495 Y=-19.5057 Z=0
    g21: GeomPoint [constr] X=23.6 Y=-1 Z=0
    g22-g25: Circle [constr] x4 (B-spline internal-alignment scaffolding for g26; pole/knot coordinates omitted)
    g26: BSplineCurve PolesCount=4 KnotsCount=2 Degree=3 IsPeriodic=0
    g27: GeomPoint [constr] X=2.00657 Y=-22.7101 Z=0
    g28: GeomPoint [constr] X=-23.6 Y=-1 Z=0
    g29: LineSegment StartX=28 StartY=0 StartZ=0 EndX=23.6 EndY=0 EndZ=0
    g30: LineSegment StartX=-23.6 StartY=0 StartZ=0 EndX=-28 EndY=0 EndZ=0
    g31: LineSegment StartX=28 StartY=0 StartZ=0 EndX=28 EndY=-18.4956 EndZ=0
    g32: LineSegment StartX=2.48484 StartY=-25.6717 StartZ=0 EndX=-22.3278 EndY=-22.4673 EndZ=0
    g33: LineSegment StartX=22.3278 StartY=-22.4673 StartZ=0 EndX=28 EndY=-18.4956 EndZ=0
    g34: LineSegment [constr] StartX=28 StartY=-18.4956 StartZ=0 EndX=28 EndY=-21.5513 EndZ=0
    g35: LineSegment [constr] StartX=-28 StartY=-18.4956 StartZ=0 EndX=28 EndY=-18.4956 EndZ=0
    g36: LineSegment StartX=-28 StartY=0 StartZ=0 EndX=-28 EndY=-18.4956 EndZ=0
    g37: LineSegment StartX=-28 StartY=-18.4956 StartZ=0 EndX=-22.3278 EndY=-22.4673 EndZ=0
    g38: LineSegment [constr] StartX=-28 StartY=-18.4956 StartZ=0 EndX=-28 EndY=-21.5513 EndZ=0
    g39: LineSegment [constr] StartX=-22.3278 StartY=-22.4673 StartZ=0 EndX=22.3278 EndY=-22.4673 EndZ=0
  constraints (92):
    c: Coincident(g0,g1)
    c: Coincident(g1,g2)
    c: Coincident(g2,g3)
    c: Coincident(g3,g0)
    c: DistanceY(g2,g-1) = 20.5407  'fan_corner_y'
    c: DistanceX(g-1,g2) = 21.7128  'fan_corner_x'
    c: Angle(g-1,g3) = 0.160106  'fan_angle'
    c: Distance(g3,g3) = 19.5  'fan_opening'
    c: Perpendicular(g3,g0)
    c: Perpendicular(g3,g2)
    c: Parallel(g1,g3)
    c: Distance(g0,g0) = 2  'fan_open_depth'
    c: Symmetric(g4,g4,g-2)
    c: DistanceX(g4,g4) = 50  'block_width'
    c: PointOnObject(g4,g-1)
    c: Equal(g8,g9)
    c: Coincident(g8,g4)
    c: Coincident(g7,g8)
    c: Coincident(g9,g4)
    c: Coincident(g6,g9)
    c: Equal(g7,g6)
    c: Distance(g8,g8) = 1.4  'block_inset'
    c: PointOnObject(g7,g-1)
    c: PointOnObject(g6,g-1)
    c: Vertical(g7)
    c: Vertical(g6)
    c: Distance(g7,g7) = 1  'duct_final_straight'
    c: Perpendicular(g3,g5)
    c: Coincident(g10,g2)
    c: PointOnObject(g10,g5)
    c: Coincident(g11,g0)
    c: Equal(g11,g10)
    c: Parallel(g11,g3)
    c: Parallel(g3,g10)
    c: Coincident(g12,g5)
    c: Parallel(g12,g3)
    c: Distance(g10,g10) = 0.3  'fan_clear'
    c: Distance(g11,g12) = 2  'fan_overlap'
    c: Coincident(g13,g12)
    c: PointOnObject(g11,g13)
    c: Perpendicular(g3,g13)
    c: Coincident(g14,g13)
    c: Coincident(g14,g5)
    c: Parallel(g14,g3)
    c: Distance(g11,g13) = 1  'start_straight'
    c: Weight(g15) = 1
    c: Equal(g15,g16)
    c: Equal(g15,g17)
    c: Equal(g15,g18)
    c: InternalAlignment(g15-g18 -> g19) x4
    c: InternalAlignment(g20,g19)
    c: InternalAlignment(g21,g19)
    c: Weight(g22) = 1
    c: Equal(g22,g23)
    c: Equal(g22,g24)
    c: Equal(g22,g25)
    c: InternalAlignment(g22-g25 -> g26) x4
    c: InternalAlignment(g27,g26)
    c: InternalAlignment(g28,g26)
    c: Tangent(g19,g6) = 1.5708
    c: Tangent(g26,g7) = 1.5708
    c: Tangent(g26,g13) = -1.5708
    c: Tangent(g19,g5) = 1.5708
    c: Coincident(g31,g29)
    c: Coincident(g6,g29)
    c: Coincident(g30,g7)
    c: Equal(g30,g29)
    c: PointOnObject(g29,g-1)
    c: PointOnObject(g30,g-1)
    c: DistanceX(g30,g29) = 56  'inner_width'
    c: Vertical(g31)
    c: Coincident(g32,g12)
    c: Coincident(g33,g5)
    c: Coincident(g33,g31)
    c: Coincident(g34,g31)
    c: Parallel(g34,g31)
    c: PointOnObject(g34,g1)
    c: Angle(g33,g34) = 0.959931  'back_angle_wall_right'
    c: Horizontal(g35)
    c: Coincident(g35,g31)
    c: Coincident(g30,g36)
    c: Vertical(g36)
    c: Coincident(g36,g37)
    c: Coincident(g37,g32)
    c: Coincident(g35,g36)
    c: Coincident(g38,g35)
    c: Vertical(g38)
    c: Angle(g38,g37) = 0.959931  'back_angle_wall_left'
    c: Equal(g34,g38)
    c: Horizontal(g39)
    c: Coincident(g39,g32)
    c: Coincident(g39,g5)
FEATURE [PartDesign::Pad] Pad025  label="hfd_duct_wall"
  BaseFeature = -> Pocket032
  Direction = (0,0,1)
  Length = 15.2
  Length2 = 10
  Profile = -> Sketch093
  ReferenceAxis = -> Sketch093 [N_Axis]
  Refine = true
  SideType = 0
  Suppressed = false
  Type = 0
  Type2 = 0
FEATURE [Sketcher::SketchObject] Sketch094  label="hfd_duct_top_s"
  ArcFitTolerance = 1e-06
  AttachmentSupport = -> [Pad025]
  ExternalGeometry = -> [Pad025]
  ExternalTypes = [0]
  FullyConstrained = true
  MakeInternals = false
  MapMode = 5
  Placement = pos=(0,0,15.2) rot=(0,0,1;0rad)
  _ExternalGeoVersion = 0
  expr: .Constraints.base_rise = <<hfd_side_s>>.Constraints.base_rise
  expr: .Constraints.depth_base = <<hfd_base>>.Length
  expr: .Constraints.depth_duct_side = <<hfd_duct_wall>>.Length
  sketch-geometry (14):
    g0: LineSegment StartX=-28 StartY=0 StartZ=0 EndX=28 EndY=0 EndZ=0
    g1: LineSegment StartX=28 StartY=0 StartZ=0 EndX=28 EndY=-18.4956 EndZ=0
    g2: LineSegment StartX=28 StartY=-18.4956 StartZ=0 EndX=22.3278 EndY=-22.4673 EndZ=0
    g3: LineSegment StartX=22.3278 StartY=-22.4673 StartZ=0 EndX=2.48484 EndY=-25.6717 EndZ=0
    g4: LineSegment StartX=-28 StartY=0 StartZ=0 EndX=-28 EndY=-18.4956 EndZ=0
    g5: LineSegment StartX=-28 StartY=-18.4956 StartZ=0 EndX=-22.3278 EndY=-22.4673 EndZ=0
    g6: LineSegment StartX=-22.3278 StartY=-22.4673 StartZ=0 EndX=2.48484 EndY=-25.6717 EndZ=0
    g7: GeomPoint [constr] X=0 Y=1 Z=0
    g8: GeomPoint [constr] X=0 Y=4 Z=0
    g9: GeomPoint [constr] X=0 Y=19.2 Z=0
    g10: GeomPoint [constr] X=0 Y=22 Z=0
    g11: GeomPoint [constr] X=0 Y=2.5 Z=0
    g12: GeomPoint [constr] X=0 Y=22.5 Z=0
    g13: GeomPoint [constr] X=0 Y=19.6 Z=0
  constraints (29):
    c: Coincident(g0,g-5)
    c: Coincident(g0,g1)
    c: Coincident(g1,g-4)
    c: Coincident(g1,g2)
    c: Coincident(g2,g-3)
    c: Coincident(g2,g3)
    c: Coincident(g3,g-7)
    c: Coincident(g4,g0)
    c: Coincident(g4,g-9)
    c: Coincident(g5,g4)
    c: Coincident(g5,g-8)
    c: Coincident(g6,g5)
    c: Coincident(g6,g3)
    c: Coincident(g0,g-6)
    c: PointOnObject(g7,g-2)
    c: PointOnObject(g8,g-2)
    c: PointOnObject(g9,g-2)
    c: PointOnObject(g10,g-2)
    c: Distance(g-1,g7) = 1  'base_rise'
    c: DistanceY(g7,g8) = 3  'depth_base'
    c: DistanceY(g8,g9) = 15.2  'depth_duct_side'
    c: Distance(g9,g10) = 2.8  'extrude'
    c: PointOnObject(g11,g-2)
    c: PointOnObject(g12,g-2)
    c: DistanceY(g11,g12) = 20  'depth_block'
    c: PointOnObject(g13,g-2)
    c: Distance(g13,g12) = 2.9  'depth_block_base'
    c: Distance(g-1,g10) = 22  'height_duct_top'
    c: Distance(g-1,g11) = 2.5  'block_rise'
FEATURE [Sketcher::SketchObject] Sketch095  label="hfss_s"
  ArcFitTolerance = 1e-06
  AttachmentSupport = -> [XY_Plane141]
  ExternalTypes = [0]
  FullyConstrained = true
  MakeInternals = false
  MapMode = 5
  _ExternalGeoVersion = 0
  sketch-geometry (10):
    g0: Circle [constr] CenterX=0 CenterY=0 CenterZ=0 NormalX=0 NormalY=0 NormalZ=1 AngleXU=0 Radius=1.45
    g1: Circle [constr] CenterX=0 CenterY=0 CenterZ=0 NormalX=0 NormalY=0 NormalZ=1 AngleXU=0 Radius=2.25
    g2: Circle CenterX=0 CenterY=0 CenterZ=0 NormalX=0 NormalY=0 NormalZ=1 AngleXU=0 Radius=2.2
    g3: Circle CenterX=0 CenterY=0 CenterZ=0 NormalX=0 NormalY=0 NormalZ=1 AngleXU=0 Radius=1.55
    g4: GeomPoint X=-2.25 Y=0 Z=0
    g5: GeomPoint X=-2.2 Y=0 Z=0
    g6: GeomPoint X=1.55 Y=0 Z=0
    g7: GeomPoint X=1.45 Y=0 Z=0
    g8: GeomPoint X=0 Y=-2.2 Z=0
    g9: GeomPoint X=0 Y=-1.55 Z=0
  constraints (23):
    c: Coincident(g0,g-1)
    c: Coincident(g1,g0)
    c: Diameter(g0) = 2.9  'screw_diam'
    c: Diameter(g1) = 4.5  'fan_hole_diam'
    c: Coincident(g2,g0)
    c: Coincident(g3,g0)
    c: PointOnObject(g4,g1)
    c: PointOnObject(g5,g2)
    c: PointOnObject(g6,g3)
    c: PointOnObject(g7,g0)
    c: PointOnObject(g4,g-1)
    c: PointOnObject(g5,g-1)
    c: PointOnObject(g7,g-1)
    c: PointOnObject(g6,g-1)
    c: Distance(g5,g4) = 0.05  'fan_clearance'
    c: Distance(g7,g6) = 0.1  'screw_clearance'
    c: PointOnObject(g8,g2)
    c: PointOnObject(g9,g3)
    c: PointOnObject(g9,g-2)
    c: PointOnObject(g8,g-2)
    c: Distance(g9,g8) = 0.65  'thickness'
    c: Diameter(g3) = 3.1  'inner_diam'
    c: Diameter(g2) = 4.4  'outer_diam'
FEATURE [PartDesign::Pad] Pad027  label="hfss_e"
  Direction = (0,0,1)
  Length = 14
  Length2 = 10
  Profile = -> Sketch095
  ReferenceAxis = -> Sketch095 [N_Axis]
  Refine = true
  SideType = 0
  Suppressed = false
  Type = 0
  Type2 = 0
FEATURE [PartDesign::Body] Body051  label="heater_fan_screw_spacer"
  AllowCompound = false
  Group = -> [Sketch095,Pad027]
  Origin = -> Origin141
  Tip = -> Pad027
FEATURE [PartDesign::Pad] Pad028  label="hfd_duct_top"
  BaseFeature = -> Pad025
  Direction = (0,0,1)
  Length = 2.8
  Length2 = 10
  Profile = -> Sketch094
  ReferenceAxis = -> Sketch094 [N_Axis]
  Refine = true
  SideType = 0
  Suppressed = false
  Type = 0
  Type2 = 0
  expr: Length = <<hfd_duct_top_s>>.Constraints.extrude
FEATURE [PartDesign::Chamfer] Chamfer037  label="hfd_outer_chmf"
  Angle = 45
  Base = -> Pad028 [Edge35,Edge34,Edge14,Edge36,Edge63,Edge39,Edge16,Edge43,Edge42,Edge41,Edge15,Edge17,Edge44,Edge62,Edge40,Edge170,Edge97,Edge47,Edge169,Edge163,Edge164,Edge165,Edge162,Edge166,Edge167,Edge168,Edge95,Edge45]
  BaseFeature = -> Pad028
  ChamferType = 0
  FlipDirection = false
  Refine = true
  Size = 0.4
  Size2 = 1
  SupportTransform = false
  Suppressed = false
  UseAllEdges = false
FEATURE [Sketcher::SketchObject] Sketch096  label="hfd_wire_tie_slot_s"
  ArcFitTolerance = 1e-06
  AttachmentOffset = pos=(0,0,6) rot=(0,0,1;0rad)
  AttachmentSupport = -> [XY_Plane140]
  ExternalTypes = [0]
  FullyConstrained = true
  MakeInternals = false
  MapMode = 5
  Placement = pos=(0,0,6) rot=(0,0,1;0rad)
  _ExternalGeoVersion = 0
  expr: .AttachmentOffset.Base.z = <<hfd_side_s>>.Constraints.tab_plane
  expr: .Constraints.base_length = <<hfd_base_s>>.Constraints.base_length
  expr: .Constraints.side_inner = <<hfd_base_s>>.Constraints.base_width - 2 * <<hfd_side_s>>.Constraints.side_width
  sketch-geometry (13):
    g0: Circle CenterX=24.1 CenterY=-75.3129 CenterZ=0 NormalX=0 NormalY=0 NormalZ=1 AngleXU=0 Radius=5.5
    g1: Circle CenterX=24.1 CenterY=-75.3129 CenterZ=0 NormalX=0 NormalY=0 NormalZ=1 AngleXU=0 Radius=7
    g2: Circle CenterX=-24.1 CenterY=-75.3129 CenterZ=0 NormalX=0 NormalY=0 NormalZ=1 AngleXU=0 Radius=5.5
    g3: Circle CenterX=-24.1 CenterY=-75.3129 CenterZ=0 NormalX=0 NormalY=0 NormalZ=1 AngleXU=0 Radius=7
    g4: LineSegment [constr] StartX=-24.1 StartY=-75.3129 StartZ=0 EndX=0 EndY=-75.3129 EndZ=0
    g5: LineSegment [constr] StartX=0 StartY=-75.3129 StartZ=0 EndX=24.1 EndY=-75.3129 EndZ=0
    g6: LineSegment [constr] StartX=24.1 StartY=-69.8129 StartZ=0 EndX=24.1 EndY=-68.3129 EndZ=0
    g7: LineSegment [constr] StartX=-28 StartY=-69.5 StartZ=0 EndX=-28 EndY=-81.1258 EndZ=0
    g8: LineSegment [constr] StartX=28 StartY=-69.5 StartZ=0 EndX=28 EndY=-81.1258 EndZ=0
    g9: LineSegment [constr] StartX=-28 StartY=-75.3129 StartZ=0 EndX=-29.6 EndY=-75.3129 EndZ=0
    g10: GeomPoint [constr] X=-28 Y=-71.4348 Z=0
    g11: GeomPoint [constr] X=-28 Y=-79.1911 Z=0
    g12: GeomPoint [constr] X=-28 Y=-80 Z=0
  constraints (37):
    c: Coincident(g1,g0)
    c: Coincident(g3,g2)
    c: Equal(g0,g2)
    c: Equal(g1,g3)
    c: Coincident(g4,g2)
    c: PointOnObject(g4,g-2)
    c: Coincident(g5,g4)
    c: Coincident(g5,g0)
    c: Horizontal(g5)
    c: Horizontal(g4)
    c: Equal(g5,g4)
    c: PointOnObject(g6,g0)
    c: PointOnObject(g6,g1)
    c: Vertical(g6)
    c: PointOnObject(g0,g6)
    c: Distance(g6,g6) = 1.5  'tie_thickness'
    c: Radius(g2) = 5.5  'loop_radius'
    c: DistanceY(g4,g-1) = 75.3129  'slot_front_inset'
    c: Vertical(g7)
    c: PointOnObject(g7,g3)
    c: PointOnObject(g7,g3)
    c: PointOnObject(g8,g1)
    c: Vertical(g8)
    c: Symmetric(g7,g8,g-2)
    c: DistanceX(g7,g8) = 56  'side_inner'
    c: Horizontal(g9)
    c: PointOnObject(g9,g2)
    c: PointOnObject(g9,g7)
    c: PointOnObject(g2,g9)
    c: Distance(g9,g9) = 1.6  'inset_depth'
    c: PointOnObject(g10,g2)
    c: PointOnObject(g11,g2)
    c: PointOnObject(g11,g7)
    c: PointOnObject(g10,g7)
    c: PointOnObject(g12,g7)
    c: DistanceY(g12,g-1) = 80  'base_length'
    c: DistanceY(g12,g7) = 10.5  'slot_end_inset'
FEATURE [PartDesign::Pocket] Pocket033  label="hfd_wire_tie_slot"
  BaseFeature = -> Chamfer037
  Direction = (0,0,-1)
  Length = 3
  Length2 = 5
  Profile = -> Sketch096
  ReferenceAxis = -> Sketch096 [N_Axis]
  Refine = true
  SideType = 0
  Suppressed = false
  Type = 0
  Type2 = 0
FEATURE [PartDesign::Fillet] Fillet017  label="hfd_wire_tie_slot_flt"
  Base = -> Pocket033 [Edge120,Edge124,Edge243,Edge245]
  BaseFeature = -> Pocket033
  Radius = 0.4
  Refine = true
  SupportTransform = false
  Suppressed = false
  UseAllEdges = false
FEATURE [PartDesign::Body] Body050  label="heater_fan_duct"
  AllowCompound = false
  Group = -> [Sketch,Pad,Sketch089,Pad023,Sketch090,Pad024,Chamfer,Fillet016,Sketch091,Pocket031,Sketch092,Pocket032,Sketch093,Pad025,Sketch094,Pad028,Chamfer037,Sketch096,Pocket033,Fillet017]
  Origin = -> Origin140
  Tip = -> Fillet017
FEATURE [App::DocumentObjectGroup] Group022  label="heater_fan"
  Group = -> [Body050,Body051]
FEATURE [Sketcher::SketchObject] Sketch097  label="hij_spc_blockframe_s"
  ArcFitTolerance = 1e-06
  AttachmentSupport = -> [XY_Plane142]
  ExternalTypes = [0]
  FullyConstrained = true
  MakeInternals = false
  MapMode = 5
  _ExternalGeoVersion = 0
  sketch-geometry (14):
    g0: LineSegment StartX=-60 StartY=0 StartZ=0 EndX=-4 EndY=0 EndZ=0
    g1: LineSegment StartX=0 StartY=4 StartZ=0 EndX=0 EndY=14 EndZ=0
    g2: LineSegment StartX=-4 StartY=18 StartZ=0 EndX=-60 EndY=18 EndZ=0
    g3: Circle CenterX=-65.9901 CenterY=9 CenterZ=0 NormalX=0 NormalY=0 NormalZ=1 AngleXU=0 Radius=2
    g4: ArcOfCircle CenterX=-65.9901 CenterY=9 CenterZ=0 NormalX=0 NormalY=0 NormalZ=1 AngleXU=0 Radius=6 StartAngle=2.00713 EndAngle=4.27606
    g5: ArcOfCircle CenterX=-60 CenterY=14 CenterZ=0 NormalX=0 NormalY=0 NormalZ=1 AngleXU=0 Radius=4 StartAngle=1.5708 EndAngle=2.00713
    g6: ArcOfCircle CenterX=-60 CenterY=4 CenterZ=0 NormalX=0 NormalY=0 NormalZ=1 AngleXU=0 Radius=4 StartAngle=4.27606 EndAngle=4.71239
    g7: ArcOfCircle CenterX=-4 CenterY=14 CenterZ=0 NormalX=0 NormalY=0 NormalZ=1 AngleXU=0 Radius=4 StartAngle=1e-16 EndAngle=1.5708
    g8: GeomPoint [constr] X=0 Y=18 Z=0
    g9: ArcOfCircle CenterX=-4 CenterY=4 CenterZ=0 NormalX=0 NormalY=0 NormalZ=1 AngleXU=0 Radius=4 StartAngle=4.71239 EndAngle=6.28319
    g10: GeomPoint [constr] X=0 Y=0 Z=0
    g11: LineSegment StartX=-61.6905 StartY=17.6252 StartZ=0 EndX=-68.5258 EndY=14.4378 EndZ=0
    g12: LineSegment StartX=-68.5258 StartY=3.56215 StartZ=0 EndX=-61.6905 EndY=0.374769 EndZ=0
    g13: LineSegment [constr] StartX=-71.9901 StartY=9 StartZ=0 EndX=-67.9901 EndY=9 EndZ=0
  constraints (35):
    c: Vertical(g1)
    c: Horizontal(g0)
    c: Horizontal(g2)
    c: Coincident(g4,g3)
    c: PointOnObject(g8,g2)
    c: PointOnObject(g8,g1)
    c: Tangent(g2,g7) = -1.5708
    c: Tangent(g1,g7) = -1.5708
    c: PointOnObject(g10,g1)
    c: PointOnObject(g10,g0)
    c: Tangent(g1,g9) = -1.5708
    c: Tangent(g0,g9) = -1.5708
    c: Tangent(g4,g12) = -1.5708
    c: Tangent(g4,g11) = -1.5708
    c: Tangent(g5,g2) = -1.5708
    c: Tangent(g6,g0) = -1.5708
    c: Tangent(g6,g12) = -1.5708
    c: Tangent(g5,g11) = -1.5708
    c: Equal(g5,g6)
    c: Equal(g9,g7)
    c: Equal(g11,g12)
    c: Equal(g0,g2)
    c: Equal(g5,g7)
    c: PointOnObject(g1,g-2)
    c: PointOnObject(g0,g-1)
    c: DistanceY(g0,g2) = 18  'width'
    c: DistanceX(g5,g1) = 60  'length'
    c: Diameter(g3) = 4
    c: PointOnObject(g13,g3)
    c: PointOnObject(g13,g4)
    c: PointOnObject(g3,g13)
    c: Horizontal(g13)
    c: Distance(g13,g13) = 4
    c: Radius(g7) = 4
    c: Angle(g12,g-1) = 0.436332
FEATURE [PartDesign::Pad] Pad029  label="hij_spc_blockframe_e"
  Direction = (0,0,1)
  Length = 6
  Length2 = 10
  Profile = -> Sketch097
  ReferenceAxis = -> Sketch097 [N_Axis]
  Refine = true
  SideType = 0
  Suppressed = false
  Type = 0
  Type2 = 0
  expr: Length = <<bracket_params>>.feature_block_offset
FEATURE [PartDesign::Chamfer] Chamfer038  label="hij_spc_blockframe_chmf"
  Angle = 45
  Base = -> Pad029 [Face13,Face12]
  BaseFeature = -> Pad029
  ChamferType = 0
  FlipDirection = false
  Refine = true
  Size = 0.4
  Size2 = 1
  SupportTransform = false
  Suppressed = false
  UseAllEdges = false
FEATURE [PartDesign::Body] Body052  label="spacer_block_frame"
  AllowCompound = false
  Group = -> [Sketch097,Pad029,Chamfer038]
  Origin = -> Origin142
  Tip = -> Chamfer038
FEATURE [Sketcher::SketchObject] Sketch098  label="hij_spc_blockdeck_s"
  ArcFitTolerance = 1e-06
  AttachmentSupport = -> [XY_Plane143]
  ExternalTypes = [0]
  FullyConstrained = true
  MakeInternals = false
  MapMode = 5
  _ExternalGeoVersion = 0
  sketch-geometry (14):
    g0: LineSegment StartX=-45 StartY=0 StartZ=0 EndX=-4 EndY=0 EndZ=0
    g1: LineSegment StartX=0 StartY=4 StartZ=0 EndX=0 EndY=41 EndZ=0
    g2: LineSegment StartX=-4 StartY=45 StartZ=0 EndX=-45 EndY=45 EndZ=0
    g3: ArcOfCircle CenterX=-4 CenterY=41 CenterZ=0 NormalX=0 NormalY=0 NormalZ=1 AngleXU=0 Radius=4 StartAngle=-9e-16 EndAngle=1.5708
    g4: GeomPoint [constr] X=0 Y=45 Z=0
    g5: ArcOfCircle CenterX=-4 CenterY=4 CenterZ=0 NormalX=0 NormalY=0 NormalZ=1 AngleXU=0 Radius=4 StartAngle=4.71239 EndAngle=6.28319
    g6: GeomPoint [constr] X=0 Y=0 Z=0
    g7: ArcOfCircle CenterX=-45 CenterY=4 CenterZ=0 NormalX=0 NormalY=0 NormalZ=1 AngleXU=0 Radius=4 StartAngle=3.75246 EndAngle=4.71239
    g8: ArcOfCircle CenterX=-45 CenterY=41 CenterZ=0 NormalX=0 NormalY=0 NormalZ=1 AngleXU=0 Radius=4 StartAngle=1.5708 EndAngle=2.53073
    g9: Circle CenterX=-55.5123 CenterY=22.5 CenterZ=0 NormalX=0 NormalY=0 NormalZ=1 AngleXU=0 Radius=2
    g10: ArcOfCircle CenterX=-55.5123 CenterY=22.5 CenterZ=0 NormalX=0 NormalY=0 NormalZ=1 AngleXU=0 Radius=6 StartAngle=2.53073 EndAngle=3.75246
    g11: LineSegment StartX=-48.2766 StartY=43.2943 StartZ=0 EndX=-60.4272 EndY=25.9415 EndZ=0
    g12: LineSegment StartX=-60.4272 StartY=19.0585 StartZ=0 EndX=-48.2766 EndY=1.70569 EndZ=0
    g13: LineSegment [constr] StartX=-57.5123 StartY=22.5 StartZ=0 EndX=-61.5123 EndY=22.5 EndZ=0
  constraints (35):
    c: Vertical(g1)
    c: Horizontal(g0)
    c: Horizontal(g2)
    c: PointOnObject(g4,g2)
    c: PointOnObject(g4,g1)
    c: Tangent(g2,g3) = -1.5708
    c: Tangent(g1,g3) = -1.5708
    c: PointOnObject(g6,g1)
    c: PointOnObject(g6,g0)
    c: Tangent(g1,g5) = -1.5708
    c: Tangent(g0,g5) = -1.5708
    c: Tangent(g0,g7) = -1.5708
    c: Tangent(g2,g8) = -1.5708
    c: Equal(g8,g7)
    c: Equal(g3,g5)
    c: Equal(g8,g3)
    c: Radius(g3) = 4
    c: PointOnObject(g1,g-2)
    c: PointOnObject(g0,g-1)
    c: DistanceX(g8,g1) = 45  'length'
    c: DistanceY(g0,g2) = 45  'width'
    c: Coincident(g10,g9)
    c: Tangent(g11,g8) = -1.5708
    c: Tangent(g12,g7) = -1.5708
    c: Tangent(g12,g10) = -1.5708
    c: Tangent(g11,g10) = -1.5708
    c: Equal(g0,g2)
    c: Equal(g11,g12)
    c: PointOnObject(g13,g9)
    c: PointOnObject(g13,g10)
    c: PointOnObject(g9,g13)
    c: Horizontal(g13)
    c: Diameter(g9) = 4
    c: Distance(g13,g13) = 4
    c: Angle(g12,g-1) = 0.959931
FEATURE [PartDesign::Pad] Pad030  label="hij_spc_blockdeck_e"
  Direction = (0,0,1)
  Length = 2.5
  Length2 = 10
  Profile = -> Sketch098
  ReferenceAxis = -> Sketch098 [N_Axis]
  Refine = true
  SideType = 0
  Suppressed = false
  Type = 0
  Type2 = 0
  expr: Length = <<bracket_params>>.feature_deck_clear_block
FEATURE [PartDesign::Chamfer] Chamfer039  label="hij_spc_blockdeck_chmf"
  Angle = 45
  Base = -> Pad030 [Face13,Face12]
  BaseFeature = -> Pad030
  ChamferType = 0
  FlipDirection = false
  Refine = true
  Size = 0.4
  Size2 = 1
  SupportTransform = false
  Suppressed = false
  UseAllEdges = false
FEATURE [PartDesign::Body] Body053  label="spacer_block_deck"
  AllowCompound = false
  Group = -> [Sketch098,Pad030,Chamfer039]
  Origin = -> Origin143
  Tip = -> Chamfer039
FEATURE [Sketcher::SketchObject] Sketch099  label="hij_spc_ductdeck_s"
  ArcFitTolerance = 1e-06
  AttachmentSupport = -> [XY_Plane144]
  ExternalTypes = [0]
  FullyConstrained = true
  MakeInternals = false
  MapMode = 5
  _ExternalGeoVersion = 0
  sketch-geometry (12):
    g0: LineSegment [constr] StartX=-88.2583 StartY=27.5 StartZ=0 EndX=-92.2583 EndY=27.5 EndZ=0
    g1: LineSegment StartX=-75 StartY=0 StartZ=0 EndX=-4 EndY=0 EndZ=0
    g2: LineSegment StartX=0 StartY=4 StartZ=0 EndX=0 EndY=51 EndZ=0
    g3: LineSegment StartX=-4 StartY=55 StartZ=0 EndX=-75 EndY=55 EndZ=0
    g4: LineSegment StartX=-78.4641 StartY=53 StartZ=0 EndX=-91.4545 EndY=30.5 EndZ=0
    g5: LineSegment StartX=-91.4545 StartY=24.5 StartZ=0 EndX=-78.4641 EndY=2 EndZ=0
    g6: Circle CenterX=-86.2583 CenterY=27.5 CenterZ=0 NormalX=0 NormalY=0 NormalZ=1 AngleXU=0 Radius=2
    g7: ArcOfCircle CenterX=-86.2583 CenterY=27.5 CenterZ=0 NormalX=0 NormalY=0 NormalZ=1 AngleXU=0 Radius=6 StartAngle=2.61799 EndAngle=3.66519
    g8: ArcOfCircle CenterX=-75 CenterY=51 CenterZ=0 NormalX=0 NormalY=0 NormalZ=1 AngleXU=0 Radius=4 StartAngle=1.5708 EndAngle=2.61799
    g9: ArcOfCircle CenterX=-4 CenterY=51 CenterZ=0 NormalX=0 NormalY=0 NormalZ=1 AngleXU=0 Radius=4 StartAngle=0 EndAngle=1.5708
    g10: ArcOfCircle CenterX=-4 CenterY=4 CenterZ=0 NormalX=0 NormalY=0 NormalZ=1 AngleXU=0 Radius=4 StartAngle=4.71239 EndAngle=6.28319
    g11: ArcOfCircle CenterX=-75 CenterY=4 CenterZ=0 NormalX=0 NormalY=0 NormalZ=1 AngleXU=0 Radius=4 StartAngle=3.66519 EndAngle=4.71239
  constraints (31):
    c: Horizontal(g0)
    c: Vertical(g2)
    c: Horizontal(g1)
    c: Horizontal(g3)
    c: Coincident(g7,g6)
    c: Tangent(g3,g8) = -1.5708
    c: Tangent(g3,g9) = -1.5708
    c: Tangent(g2,g9) = -1.5708
    c: Tangent(g2,g10) = -1.5708
    c: Tangent(g1,g10) = -1.5708
    c: Tangent(g1,g11) = -1.5708
    c: Equal(g8,g11)
    c: Equal(g1,g3)
    c: Equal(g9,g8)
    c: Equal(g4,g5)
    c: PointOnObject(g0,g6)
    c: PointOnObject(g0,g7)
    c: DistanceX(g0,g0) = 4
    c: Diameter(g6) = 4
    c: Tangent(g7,g4) = -1.5708
    c: Tangent(g7,g5) = -1.5708
    c: Tangent(g5,g11) = -1.5708
    c: Tangent(g4,g8) = -1.5708
    c: Radius(g9) = 4
    c: PointOnObject(g6,g0)
    c: DistanceY(g1,g3) = 55  'width'
    c: DistanceX(g8,g2) = 75  'length'
    c: PointOnObject(g2,g-2)
    c: PointOnObject(g1,g-1)
    c: Equal(g10,g9)
    c: Angle(g5,g-1) = 1.0472
FEATURE [PartDesign::Pad] Pad031  label="hij_spc_ductdeck_e"
  Direction = (0,0,1)
  Length = 1
  Length2 = 10
  Profile = -> Sketch099
  ReferenceAxis = -> Sketch099 [N_Axis]
  Refine = true
  SideType = 0
  Suppressed = false
  Type = 0
  Type2 = 0
  expr: Length = <<fan_params>>.feature_deck_clearance
FEATURE [PartDesign::Chamfer] Chamfer040  label="hij_spc_ductduck_chmf"
  Angle = 45
  Base = -> Pad031 [Face13,Face12]
  BaseFeature = -> Pad031
  ChamferType = 0
  FlipDirection = false
  Refine = true
  Size = 0.4
  Size2 = 1
  SupportTransform = false
  Suppressed = false
  UseAllEdges = false
FEATURE [PartDesign::Body] Body054  label="spacer_duct_deck"
  AllowCompound = false
  Group = -> [Sketch099,Pad031,Chamfer040]
  Origin = -> Origin144
  Tip = -> Chamfer040
FEATURE [App::DocumentObjectGroup] Group024  label="heater_install_spacers"
  Group = -> [Body052,Body053,Body054]
FEATURE [Sketcher::SketchObject] Sketch100  label="hhb_base_s"
  ArcFitTolerance = 1e-06
  AttachmentSupport = -> [XY_Plane145]
  ExternalTypes = [0]
  FullyConstrained = true
  MakeInternals = false
  MapMode = 5
  _ExternalGeoVersion = 0
  expr: .Constraints.width = <<block_params>>.heatsink_width
  sketch-geometry (5):
    g0: LineSegment StartX=0 StartY=50 StartZ=0 EndX=0 EndY=0 EndZ=0
    g1: LineSegment StartX=0 StartY=0 StartZ=0 EndX=50 EndY=0 EndZ=0
    g2: LineSegment StartX=50 StartY=0 StartZ=0 EndX=50 EndY=50 EndZ=0
    g3: LineSegment StartX=50 StartY=50 StartZ=0 EndX=0 EndY=50 EndZ=0
    g4: Circle [constr] CenterX=25 CenterY=25 CenterZ=0 NormalX=0 NormalY=0 NormalZ=1 AngleXU=0 Radius=25
  constraints (14):
    c: Coincident(g0,g1)
    c: Coincident(g1,g2)
    c: Coincident(g2,g3)
    c: Coincident(g3,g0)
    c: Vertical(g0)
    c: Vertical(g2)
    c: Horizontal(g1)
    c: Horizontal(g3)
    c: Coincident(g-1,g0)
    c: Tangent(g4,g3)
    c: Tangent(g4,g2)
    c: Tangent(g4,g1)
    c: Tangent(g4,g0)
    c: Diameter(g4) = 50  'width'
FEATURE [PartDesign::Pad] Pad032  label="hhb_base"
  Direction = (0,0,1)
  Length = 20
  Length2 = 10
  Profile = -> Sketch100
  ReferenceAxis = -> Sketch100 [N_Axis]
  Refine = true
  Reversed = true
  SideType = 0
  Suppressed = false
  Type = 0
  Type2 = 0
  expr: Length = <<block_params>>.heatsink_height
FEATURE [PartDesign::Pad] Pad033  label="hcs_ptc_e"
  Direction = (0,0,1)
  Length = 0.76
  Length2 = 10
  Profile = -> Sketch087
  ReferenceAxis = -> Sketch087 [N_Axis]
  Refine = true
  SideType = 0
  Suppressed = false
  Type = 0
  Type2 = 0
  expr: Length = <<block_params>>.strap_thickness
FEATURE [PartDesign::Body] Body  label="heater_strap_ptc"
  AllowCompound = false
  Group = -> [Sketch087,Pad033]
  Origin = -> Origin
  Tip = -> Pad033
FEATURE [PartDesign::Pad] Pad034  label="hcs_tswitch_e"
  Direction = (0,0,1)
  Length = 0.76
  Length2 = 10
  Profile = -> Sketch088
  ReferenceAxis = -> Sketch088 [N_Axis]
  Refine = true
  SideType = 0
  Suppressed = false
  Type = 0
  Type2 = 0
  expr: Length = <<block_params>>.strap_thickness
FEATURE [PartDesign::Body] Body049  label="heater_strap_tswitch"
  AllowCompound = false
  Group = -> [Sketch088,Pad034]
  Origin = -> Origin139
  Tip = -> Pad034
FEATURE [App::DocumentObjectGroup] Group021  label="heater_strap"
  Group = -> [Body,Body049]
FEATURE [Part::Feature] Part__Feature001  label="m3x4_bhcs"
  shape: bbox 5.7 x 5.7 x 5.65 mm, 20 faces (baked)
FEATURE [Part::Feature] Part__Feature002  label="m3x6_bhcs"
  shape: bbox 5.7 x 5.7 x 7.65 mm, 20 faces (baked)
FEATURE [Part::Feature] Part__Feature003  label="m3x8_bhcs"
  shape: bbox 5.7 x 5.7 x 9.65 mm, 20 faces (baked)
FEATURE [Part::Feature] Part__Feature  label="heatset_m3_short_cnck"
  shape: bbox 4.752 x 4.752 x 3.322 mm, 313 faces (baked)
FEATURE [Part::Feature] Part__Feature004  label="ptc_mini_element_v1"
  shape: bbox 20.8 x 49 x 5.3 mm, 42 faces (baked)
FEATURE [Part::Feature] Part__Feature005  label="thermal_switch_ksd9700_v1"
  shape: bbox 8.4 x 28.4 x 4.4 mm, 35 faces (baked)
FEATURE [Part::Feature] Part__Feature006  label="fan_radial_50x15"
  shape: bbox 52.61 x 51.31 x 15 mm, 310 faces (baked)
FEATURE [Part::Feature] Part__Feature007  label="m3x18_bhcs"
  shape: bbox 5.7 x 5.7 x 19.65 mm, 20 faces (baked)
FEATURE [App::DocumentObjectGroup] Group025  label="screws"
  Group = -> [Part__Feature001,Part__Feature002,Part__Feature003,Part__Feature007]
FEATURE [Part::Feature] Part__Feature008  label="tnut_2020_m3_roll"
  shape: bbox 4.7 x 8.3 x 17 mm, 28 faces (baked)
FEATURE [App::DocumentObjectGroup] Group026  label="nut"
  Group = -> [Part__Feature,Part__Feature008]
FEATURE [Part::Feature] Part__Feature009  label="HFS5-2020-160"
  shape: bbox 20 x 20 x 160 mm, 63 faces (baked)
FEATURE [App::DocumentObjectGroup] Group  label="hardware"
  Group = -> [Group025,Group026,Part__Feature004,Part__Feature005,Part__Feature006,Part__Feature009]
FEATURE [App::VarSet] VarSet  label="block_params"
  heatsink_base = 3
  heatsink_base_roundover = 0.2
  heatsink_fin_count = 14
  heatsink_fin_roundover = 0.58
  heatsink_fin_segment_count = 9
  heatsink_fin_segment_length = 4
  heatsink_fin_segment_spacing = 5.75
  heatsink_fin_spacing = 3.738
  heatsink_fin_thickness = 1.4
  heatsink_height = 20
  heatsink_screw_spacing = 42
  heatsink_width = 50
  ptc_clearance_length = 1
  ptc_clearance_width = 0.8
  ptc_length = 35
  ptc_offset_length = 0
  ptc_offset_width = 3.5
  ptc_placement_length = 25
  ptc_placement_width = 28.5
  ptc_pocket_depth = 0.8
  ptc_pocket_length = 36
  ptc_pocket_width = 21.3
  ptc_screw_spacing_length = 25
  ptc_screw_spacing_width = 24.2
  ptc_width = 20.5
  screw_drill_depth = 4.5
  screw_drill_diam = 2.5
  screw_head_diam = 5.5
  screw_thread_diam = 2.9
  strap_hole = 3.3
  strap_thickness = 0.76
  strap_width = 6.5
  tfuse_clearance_length = 1.2
  tfuse_clearance_width = 0.6
  tfuse_length = 22
  tfuse_offset_length = 0
  tfuse_offset_width = -16
  tfuse_placement_length = 25
  tfuse_placement_width = 9
  tfuse_pocket_depth = 0.8
  tfuse_pocket_length = 23.2
  tfuse_pocket_width = 11.6
  tfuse_screw_hole = 5
  tfuse_screw_spacing = 11
  tfuse_width = 11
  tswitch_clearance_length = 0.4
  tswitch_clearance_width = 0.4
  tswitch_length = 22
  tswitch_offset_length = 0
  tswitch_offset_width = -16
  tswitch_placement_length = 25
  tswitch_placement_width = 9
  tswitch_pocket_depth = 0.8
  tswitch_pocket_length = 22.4
  tswitch_pocket_width = 8.4
  tswitch_screw_spacing_length = 11
  tswitch_screw_spacing_width = 11.3
  tswitch_width = 8
  expr: ptc_placement_length = heatsink_width / 2 + ptc_offset_length
  expr: ptc_placement_width = heatsink_width / 2 + ptc_offset_width
  expr: ptc_pocket_length = ptc_length + ptc_clearance_length
  expr: ptc_pocket_width = ptc_width + ptc_clearance_width
  expr: tfuse_placement_length = heatsink_width / 2 + tfuse_offset_length
  expr: tfuse_placement_width = heatsink_width / 2 + tfuse_offset_width
  expr: tfuse_pocket_length = tfuse_length + tfuse_clearance_length
  expr: tfuse_pocket_width = tfuse_width + tfuse_clearance_width
  expr: tfuse_screw_spacing = tfuse_length - tfuse_width
  expr: tswitch_placement_length = heatsink_width / 2 + tswitch_offset_length
  expr: tswitch_placement_width = heatsink_width / 2 + tswitch_offset_width
  expr: tswitch_pocket_length = tswitch_length + tswitch_clearance_length
  expr: tswitch_pocket_width = tswitch_width + tswitch_clearance_width
FEATURE [PartDesign::Fillet] Fillet018  label="hhb_base_flt"
  Base = -> Pad032 [Edge3,Edge9]
  BaseFeature = -> Pad032
  Radius = 0.2
  Refine = true
  SupportTransform = false
  Suppressed = false
  UseAllEdges = false
  expr: Radius = <<block_params>>.heatsink_base_roundover
FEATURE [Sketcher::SketchObject] Sketch107  label="hhb_fin_outerRound_s"
  ArcFitTolerance = 1e-06
  AttachmentSupport = -> [XZ_Plane145]
  ExternalTypes = [0]
  FullyConstrained = true
  MakeInternals = false
  MapMode = 5
  Placement = pos=(0,0,0) rot=(1,0,0;1.5708rad)
  _ExternalGeoVersion = 0
  expr: .Constraints.radius = <<block_params>>.heatsink_fin_roundover
  expr: Constraints[13] = <<block_params>>.heatsink_height
  expr: Constraints[29] = <<block_params>>.heatsink_width
  sketch-geometry (11):
    g0: LineSegment StartX=0.58 StartY=-20 StartZ=0 EndX=0.58 EndY=-21 EndZ=0
    g1: LineSegment StartX=0.58 StartY=-21 StartZ=0 EndX=-1 EndY=-21 EndZ=0
    g2: LineSegment StartX=-1 StartY=-21 StartZ=0 EndX=-1 EndY=-19.42 EndZ=0
    g3: LineSegment StartX=-1 StartY=-19.42 StartZ=0 EndX=0 EndY=-19.42 EndZ=0
    g4: ArcOfCircle CenterX=0.58 CenterY=-19.42 CenterZ=0 NormalX=0 NormalY=0 NormalZ=1 AngleXU=0 Radius=0.58 StartAngle=3.14159 EndAngle=4.71239
    g5: LineSegment StartX=50 StartY=-19.42 StartZ=0 EndX=51 EndY=-19.42 EndZ=0
    g6: LineSegment StartX=51 StartY=-19.42 StartZ=0 EndX=51 EndY=-21 EndZ=0
    g7: LineSegment StartX=51 StartY=-21 StartZ=0 EndX=49.42 EndY=-21 EndZ=0
    g8: LineSegment StartX=49.42 StartY=-21 StartZ=0 EndX=49.42 EndY=-20 EndZ=0
    g9: ArcOfCircle CenterX=49.42 CenterY=-19.42 CenterZ=0 NormalX=0 NormalY=0 NormalZ=1 AngleXU=0 Radius=0.58 StartAngle=4.71239 EndAngle=6.28319
    g10: LineSegment [constr] StartX=0.58 StartY=-20 StartZ=0 EndX=49.42 EndY=-20 EndZ=0
  constraints (30):
    c: Vertical(g0)
    c: Coincident(g0,g1)
    c: Horizontal(g1)
    c: Coincident(g1,g2)
    c: Vertical(g2)
    c: Coincident(g2,g3)
    c: Horizontal(g3)
    c: Perpendicular(g4,g3) = 1.5708
    c: Perpendicular(g4,g0) = 4.71239
    c: Equal(g0,g3)
    c: Distance(g0,g0) = 1  'overcut'
    c: Radius(g4) = 0.58  'radius'
    c: PointOnObject(g3,g-2)
    c: DistanceY(g0,g-1) = 20
    c: Horizontal(g5)
    c: Coincident(g5,g6)
    c: Vertical(g6)
    c: Coincident(g6,g7)
    c: Horizontal(g7)
    c: Coincident(g7,g8)
    c: Vertical(g8)
    c: Perpendicular(g9,g5) = 4.71239
    c: Perpendicular(g9,g8) = 1.5708
    c: Equal(g9,g4)
    c: Equal(g0,g5)
    c: Equal(g5,g8)
    c: Coincident(g10,g0)
    c: Coincident(g10,g8)
    c: Horizontal(g10)
    c: DistanceX(g-1,g5) = 50
FEATURE [Sketcher::SketchObject] Sketch108  label="hhb_fin_cut_s001"
  ArcFitTolerance = 1e-06
  AttachmentSupport = -> [XZ_Plane145]
  ExternalTypes = [0]
  FullyConstrained = true
  MakeInternals = false
  MapMode = 5
  Placement = pos=(0,0,0) rot=(1,0,0;1.5708rad)
  _ExternalGeoVersion = 0
  expr: .Constraints.base_thickness = <<block_params>>.heatsink_base
  expr: .Constraints.fin_spacing = <<block_params>>.heatsink_fin_spacing
  expr: .Constraints.fin_thickness = <<block_params>>.heatsink_fin_thickness
  expr: .Constraints.roundover = <<block_params>>.heatsink_fin_roundover
  expr: Constraints[17] = <<block_params>>.heatsink_height
  sketch-geometry (8):
    g0: LineSegment StartX=1.4 StartY=-3 StartZ=0 EndX=1.4 EndY=-19.42 EndZ=0
    g1: LineSegment StartX=3.738 StartY=-19.42 StartZ=0 EndX=3.738 EndY=-3 EndZ=0
    g2: LineSegment StartX=3.738 StartY=-3 StartZ=0 EndX=1.4 EndY=-3 EndZ=0
    g3: ArcOfCircle CenterX=0.82 CenterY=-19.42 CenterZ=0 NormalX=0 NormalY=0 NormalZ=1 AngleXU=0 Radius=0.58 StartAngle=4.71239 EndAngle=6.28319
    g4: ArcOfCircle CenterX=4.318 CenterY=-19.42 CenterZ=0 NormalX=0 NormalY=0 NormalZ=1 AngleXU=0 Radius=0.58 StartAngle=3.14159 EndAngle=4.71239
    g5: LineSegment StartX=0.82 StartY=-20 StartZ=0 EndX=0.82 EndY=-21 EndZ=0
    g6: LineSegment StartX=0.82 StartY=-21 StartZ=0 EndX=4.318 EndY=-21 EndZ=0
    g7: LineSegment StartX=4.318 StartY=-21 StartZ=0 EndX=4.318 EndY=-20 EndZ=0
  constraints (22):
    c: Coincident(g1,g2)
    c: Coincident(g2,g0)
    c: Vertical(g0)
    c: Vertical(g1)
    c: Horizontal(g2)
    c: Vertical(g5)
    c: Coincident(g5,g6)
    c: Horizontal(g6)
    c: Coincident(g6,g7)
    c: Vertical(g7)
    c: Tangent(g3,g0) = 1.5708
    c: Tangent(g4,g1) = 1.5708
    c: Perpendicular(g3,g5) = 4.71239
    c: Perpendicular(g4,g7) = 1.5708
    c: Equal(g3,g4)
    c: Equal(g5,g7)
    c: Radius(g3) = 0.58  'roundover'
    c: DistanceY(g3,g-1) = 20
    c: DistanceY(g0,g-1) = 3  'base_thickness'
    c: DistanceX(g-1,g0) = 1.4  'fin_thickness'
    c: DistanceX(g-1,g1) = 3.738  'fin_spacing'
    c: DistanceY(g5,g5) = 1  'overcut'
FEATURE [PartDesign::Pocket] Pocket040  label="hhb_fin_outerRound"
  BaseFeature = -> Fillet018
  Direction = (0,1,-2e-16)
  Length = 5
  Length2 = 5
  Profile = -> Sketch107
  ReferenceAxis = -> Sketch107 [N_Axis]
  Refine = true
  SideType = 0
  Suppressed = false
  Type = 1
  Type2 = 0
FEATURE [PartDesign::Pocket] Pocket041  label="hhb_fin_cut"
  BaseFeature = -> Pocket040
  Direction = (0,1,-2e-16)
  Length = 5
  Length2 = 5
  Profile = -> Sketch108
  ReferenceAxis = -> Sketch108 [N_Axis]
  Refine = true
  SideType = 0
  Suppressed = false
  Type = 1
  Type2 = 0
FEATURE [PartDesign::LinearPattern] LinearPattern  label="hhb_fin_cuts"
  BaseFeature = -> Pocket041
  Direction = -> Sketch108 [H_Axis]
  Length = 44.856
  Length2 = 100
  Mode = 1
  Mode2 = 0
  Occurrences = 13
  Occurrences2 = 1
  Offset = 3.738
  Offset2 = 10
  Originals = -> [Pocket041]
  Refine = true
  Reversed2 = false
  SpacingPattern = [0]
  SpacingPattern2 = [0]
  Spacings = [-1,-1,-1,-1,-1,-1,-1,-1,-1,-1,-1,-1]
  Suppressed = false
  TransformMode = 0
  expr: Occurrences = <<block_params>>.heatsink_fin_count - 1
  expr: Offset = <<block_params>>.heatsink_fin_spacing
FEATURE [Sketcher::SketchObject] Sketch109  label="hhb_segment_cut_s"
  ArcFitTolerance = 1e-06
  AttachmentSupport = -> [YZ_Plane145]
  ExternalTypes = [0]
  FullyConstrained = true
  MakeInternals = false
  MapMode = 5
  Placement = pos=(0,0,0) rot=(0.57735,0.57735,0.57735;2.0944rad)
  _ExternalGeoVersion = 0
  expr: .Constraints.base_thickness = <<block_params>>.heatsink_base
  expr: .Constraints.fin_segment_length = <<block_params>>.heatsink_fin_segment_length
  expr: .Constraints.fin_segment_spacing = <<block_params>>.heatsink_fin_segment_spacing
  expr: Constraints[11] = <<block_params>>.heatsink_height + 1 mm
  sketch-geometry (4):
    g0: LineSegment StartX=4 StartY=-21 StartZ=0 EndX=5.75 EndY=-21 EndZ=0
    g1: LineSegment StartX=5.75 StartY=-21 StartZ=0 EndX=5.75 EndY=-3 EndZ=0
    g2: LineSegment StartX=5.75 StartY=-3 StartZ=0 EndX=4 EndY=-3 EndZ=0
    g3: LineSegment StartX=4 StartY=-3 StartZ=0 EndX=4 EndY=-21 EndZ=0
  constraints (12):
    c: Coincident(g0,g1)
    c: Coincident(g1,g2)
    c: Coincident(g2,g3)
    c: Coincident(g3,g0)
    c: Horizontal(g0)
    c: Horizontal(g2)
    c: Vertical(g1)
    c: Vertical(g3)
    c: DistanceX(g-1,g2) = 4  'fin_segment_length'
    c: DistanceX(g-1,g1) = 5.75  'fin_segment_spacing'
    c: DistanceY(g2,g-1) = 3  'base_thickness'
    c: DistanceY(g0,g-1) = 21
FEATURE [PartDesign::Pocket] Pocket042  label="hhb_segment_cut"
  BaseFeature = -> LinearPattern
  Direction = (-1,0,0)
  Length = 5
  Length2 = 5
  Profile = -> Sketch109
  ReferenceAxis = -> Sketch109 [N_Axis]
  Refine = true
  Reversed = true
  SideType = 0
  Suppressed = false
  Type = 1
  Type2 = 0
FEATURE [PartDesign::LinearPattern] LinearPattern001  label="hhb_segment_cuts"
  BaseFeature = -> Pocket042
  Direction = -> Sketch109 [H_Axis]
  Length = 40.25
  Length2 = 100
  Mode = 1
  Mode2 = 0
  Occurrences = 8
  Occurrences2 = 1
  Offset = 5.75
  Offset2 = 10
  Originals = -> [Pocket042]
  Refine = true
  Reversed2 = false
  SpacingPattern = [0]
  SpacingPattern2 = [0]
  Spacings = [-1,-1,-1,-1,-1,-1,-1]
  Suppressed = false
  TransformMode = 0
  expr: Occurrences = <<block_params>>.heatsink_fin_segment_count - 1
  expr: Offset = <<block_params>>.heatsink_fin_segment_spacing
FEATURE [PartDesign::Body] Body055  label="heater_heatsink_blank"
  AllowCompound = false
  Group = -> [Sketch100,Pad032,Fillet018,Sketch107,Sketch108,Pocket040,Pocket041,LinearPattern,Sketch109,Pocket042,LinearPattern001]
  Origin = -> Origin145
  Tip = -> LinearPattern001
FEATURE [PartDesign::FeatureBase] Clone  label="hhm_cln"
  BaseFeature = -> Body055
  Suppressed = false
FEATURE [Sketcher::SketchObject] Sketch103  label="hhm_mount_holes_s"
  ArcFitTolerance = 1e-06
  AttachmentSupport = -> [XY_Plane146]
  ExternalTypes = [0]
  FullyConstrained = true
  MakeInternals = false
  MapMode = 5
  _ExternalGeoVersion = 0
  expr: .Constraints.diam = <<block_params>>.screw_drill_diam
  expr: .Constraints.heatsink = <<block_params>>.heatsink_width
  expr: .Constraints.spacing = <<block_params>>.heatsink_screw_spacing
  sketch-geometry (10):
    g0: Circle CenterX=4 CenterY=4 CenterZ=0 NormalX=0 NormalY=0 NormalZ=1 AngleXU=0 Radius=1.25
    g1: Circle CenterX=46 CenterY=4 CenterZ=0 NormalX=0 NormalY=0 NormalZ=1 AngleXU=0 Radius=1.25
    g2: Circle CenterX=46 CenterY=46 CenterZ=0 NormalX=0 NormalY=0 NormalZ=1 AngleXU=0 Radius=1.25
    g3: Circle CenterX=4 CenterY=46 CenterZ=0 NormalX=0 NormalY=0 NormalZ=1 AngleXU=0 Radius=1.25
    g4: LineSegment [constr] StartX=4 StartY=46 StartZ=0 EndX=46 EndY=46 EndZ=0
    g5: LineSegment [constr] StartX=4 StartY=4 StartZ=0 EndX=46 EndY=4 EndZ=0
    g6: LineSegment [constr] StartX=4 StartY=4 StartZ=0 EndX=4 EndY=46 EndZ=0
    g7: LineSegment [constr] StartX=46 StartY=46 StartZ=0 EndX=46 EndY=4 EndZ=0
    g8: Circle [constr] CenterX=25 CenterY=25 CenterZ=0 NormalX=0 NormalY=0 NormalZ=1 AngleXU=0 Radius=21
    g9: Circle [constr] CenterX=25 CenterY=25 CenterZ=0 NormalX=0 NormalY=0 NormalZ=1 AngleXU=0 Radius=25
  constraints (25):
    c: Equal(g0,g3)
    c: Equal(g3,g2)
    c: Equal(g2,g1)
    c: Diameter(g0) = 2.5  'diam'
    c: Coincident(g4,g3)
    c: Coincident(g4,g2)
    c: Horizontal(g4)
    c: Coincident(g5,g0)
    c: Coincident(g5,g1)
    c: Horizontal(g5)
    c: Coincident(g6,g0)
    c: Coincident(g6,g3)
    c: Vertical(g6)
    c: Coincident(g7,g2)
    c: Coincident(g7,g1)
    c: Vertical(g7)
    c: Tangent(g8,g4)
    c: Tangent(g8,g6)
    c: Tangent(g8,g5)
    c: Tangent(g8,g7)
    c: Diameter(g8) = 42  'spacing'
    c: Coincident(g9,g8)
    c: Diameter(g9) = 50  'heatsink'
    c: Tangent(g9,g-1)
    c: Tangent(g9,g-2)
FEATURE [PartDesign::Pocket] Pocket036  label="hhm_mount_holes"
  BaseFeature = -> Clone
  Direction = (0,0,-1)
  Length = 4.5
  Length2 = 5
  Profile = -> Sketch103
  ReferenceAxis = -> Sketch103 [N_Axis]
  Refine = true
  SideType = 0
  Suppressed = false
  Type = 0
  Type2 = 0
  expr: Length = <<block_params>>.screw_drill_depth
FEATURE [PartDesign::Body] Body056  label="heater_heatsink_mounted"
  AllowCompound = false
  Group = -> [Clone,Sketch103,Pocket036]
  Origin = -> Origin146
  Tip = -> Pocket036
FEATURE [PartDesign::FeatureBase] Clone024  label="hhp_cln"
  BaseFeature = -> Body056
  Suppressed = false
FEATURE [Sketcher::SketchObject] Sketch110  label="hhp_pocket_s"
  ArcFitTolerance = 1e-06
  AttachmentSupport = -> [XY_Plane147]
  ExternalTypes = [0]
  FullyConstrained = true
  MakeInternals = false
  MapMode = 5
  _ExternalGeoVersion = 0
  expr: .Constraints.placement_length = <<block_params>>.ptc_placement_length
  expr: .Constraints.placement_width = <<block_params>>.ptc_placement_width
  expr: .Constraints.pocket_length = <<block_params>>.ptc_pocket_length
  expr: .Constraints.pocket_width = <<block_params>>.ptc_pocket_width
  sketch-geometry (6):
    g0: Circle [constr] CenterX=25 CenterY=28.5 CenterZ=0 NormalX=0 NormalY=0 NormalZ=1 AngleXU=0 Radius=18
    g1: Circle [constr] CenterX=25 CenterY=28.5 CenterZ=0 NormalX=0 NormalY=0 NormalZ=1 AngleXU=0 Radius=10.65
    g2: LineSegment StartX=7 StartY=39.15 StartZ=0 EndX=7 EndY=17.85 EndZ=0
    g3: LineSegment StartX=7 StartY=17.85 StartZ=0 EndX=43 EndY=17.85 EndZ=0
    g4: LineSegment StartX=43 StartY=17.85 StartZ=0 EndX=43 EndY=39.15 EndZ=0
    g5: LineSegment StartX=43 StartY=39.15 StartZ=0 EndX=7 EndY=39.15 EndZ=0
  constraints (17):
    c: Coincident(g1,g0)
    c: DistanceY(g-1,g0) = 28.5  'placement_width'
    c: DistanceX(g-1,g0) = 25  'placement_length'
    c: Coincident(g2,g3)
    c: Coincident(g3,g4)
    c: Coincident(g4,g5)
    c: Coincident(g5,g2)
    c: Vertical(g2)
    c: Vertical(g4)
    c: Horizontal(g3)
    c: Horizontal(g5)
    c: Tangent(g1,g5)
    c: Tangent(g1,g3)
    c: Tangent(g0,g4)
    c: Tangent(g0,g2)
    c: Diameter(g0) = 36  'pocket_length'
    c: Diameter(g1) = 21.3  'pocket_width'
FEATURE [Sketcher::SketchObject] Sketch111  label="hhp_screws_s"
  ArcFitTolerance = 1e-06
  AttachmentSupport = -> [XY_Plane147]
  ExternalTypes = [0]
  FullyConstrained = true
  MakeInternals = false
  MapMode = 5
  _ExternalGeoVersion = 0
  expr: .Constraints.diam = <<block_params>>.screw_drill_diam
  expr: .Constraints.placement_length = <<block_params>>.ptc_placement_length
  expr: .Constraints.placement_width = <<block_params>>.ptc_placement_width
  expr: .Constraints.spacing_length = <<block_params>>.ptc_screw_spacing_length
  expr: .Constraints.spacing_width = <<block_params>>.ptc_screw_spacing_width
  sketch-geometry (10):
    g0: LineSegment [constr] StartX=12.5 StartY=40.6 StartZ=0 EndX=12.5 EndY=16.4 EndZ=0
    g1: LineSegment [constr] StartX=12.5 StartY=16.4 StartZ=0 EndX=37.5 EndY=16.4 EndZ=0
    g2: LineSegment [constr] StartX=37.5 StartY=16.4 StartZ=0 EndX=37.5 EndY=40.6 EndZ=0
    g3: LineSegment [constr] StartX=37.5 StartY=40.6 StartZ=0 EndX=12.5 EndY=40.6 EndZ=0
    g4: Circle CenterX=37.5 CenterY=40.6 CenterZ=0 NormalX=0 NormalY=0 NormalZ=1 AngleXU=0 Radius=1.25
    g5: Circle CenterX=12.5 CenterY=40.6 CenterZ=0 NormalX=0 NormalY=0 NormalZ=1 AngleXU=0 Radius=1.25
    g6: Circle CenterX=12.5 CenterY=16.4 CenterZ=0 NormalX=0 NormalY=0 NormalZ=1 AngleXU=0 Radius=1.25
    g7: Circle CenterX=37.5 CenterY=16.4 CenterZ=0 NormalX=0 NormalY=0 NormalZ=1 AngleXU=0 Radius=1.25
    g8: Circle [constr] CenterX=25 CenterY=28.5 CenterZ=0 NormalX=0 NormalY=0 NormalZ=1 AngleXU=0 Radius=12.1
    g9: Circle [constr] CenterX=25 CenterY=28.5 CenterZ=0 NormalX=0 NormalY=0 NormalZ=1 AngleXU=0 Radius=12.5
  constraints (25):
    c: Coincident(g0,g1)
    c: Coincident(g1,g2)
    c: Coincident(g2,g3)
    c: Coincident(g3,g0)
    c: Vertical(g0)
    c: Vertical(g2)
    c: Horizontal(g1)
    c: Horizontal(g3)
    c: Coincident(g4,g2)
    c: Coincident(g5,g0)
    c: Coincident(g6,g0)
    c: Coincident(g7,g1)
    c: Equal(g5,g4)
    c: Equal(g4,g7)
    c: Equal(g7,g6)
    c: Coincident(g9,g8)
    c: Tangent(g9,g2)
    c: Tangent(g9,g0)
    c: Tangent(g8,g3)
    c: Tangent(g8,g1)
    c: DistanceY(g-1,g8) = 28.5  'placement_width'
    c: DistanceX(g-1,g8) = 25  'placement_length'
    c: Diameter(g9) = 25  'spacing_length'
    c: Diameter(g8) = 24.2  'spacing_width'
    c: Diameter(g6) = 2.5  'diam'
FEATURE [PartDesign::Pocket] Pocket043  label="hhp_pocket"
  BaseFeature = -> Clone024
  Direction = (0,0,-1)
  Length = 0.8
  Length2 = 5
  Profile = -> Sketch110
  ReferenceAxis = -> Sketch110 [N_Axis]
  Refine = true
  SideType = 0
  Suppressed = false
  Type = 0
  Type2 = 0
  expr: Length = <<block_params>>.ptc_pocket_depth
FEATURE [PartDesign::Pocket] Pocket044  label="hhp_screws"
  BaseFeature = -> Pocket043
  Direction = (0,0,-1)
  Length = 4.5
  Length2 = 5
  Profile = -> Sketch111
  ReferenceAxis = -> Sketch111 [N_Axis]
  Refine = true
  SideType = 0
  Suppressed = false
  Type = 0
  Type2 = 0
  expr: Length = <<block_params>>.screw_drill_depth
FEATURE [PartDesign::Body] Body057  label="heater_heatsink_ptc"
  AllowCompound = false
  Group = -> [Clone024,Sketch110,Sketch111,Pocket043,Pocket044]
  Origin = -> Origin147
  Tip = -> Pocket044
FEATURE [PartDesign::FeatureBase] Clone025  label="hhp_ts_cln"
  BaseFeature = -> Body057
  Suppressed = false
FEATURE [Sketcher::SketchObject] Sketch112  label="hhp_ts_pocket_s"
  ArcFitTolerance = 1e-06
  AttachmentSupport = -> [XY_Plane148]
  ExternalTypes = [0]
  FullyConstrained = true
  MakeInternals = false
  MapMode = 5
  _ExternalGeoVersion = 0
  expr: .Constraints.placement_length = <<block_params>>.tswitch_placement_length
  expr: .Constraints.placement_width = <<block_params>>.tswitch_placement_width
  expr: .Constraints.pocket_length = <<block_params>>.tswitch_pocket_length
  expr: .Constraints.pocket_width = <<block_params>>.tswitch_pocket_width
  sketch-geometry (6):
    g0: Circle [constr] CenterX=25 CenterY=9 CenterZ=0 NormalX=0 NormalY=0 NormalZ=1 AngleXU=0 Radius=4.2
    g1: Circle [constr] CenterX=25 CenterY=9 CenterZ=0 NormalX=0 NormalY=0 NormalZ=1 AngleXU=0 Radius=11.2
    g2: LineSegment StartX=13.8 StartY=13.2 StartZ=0 EndX=13.8 EndY=4.8 EndZ=0
    g3: LineSegment StartX=13.8 StartY=4.8 StartZ=0 EndX=36.2 EndY=4.8 EndZ=0
    g4: LineSegment StartX=36.2 StartY=4.8 StartZ=0 EndX=36.2 EndY=13.2 EndZ=0
    g5: LineSegment StartX=36.2 StartY=13.2 StartZ=0 EndX=13.8 EndY=13.2 EndZ=0
  constraints (17):
    c: Coincident(g1,g0)
    c: DistanceY(g-1,g0) = 9  'placement_width'
    c: DistanceX(g-1,g0) = 25  'placement_length'
    c: Coincident(g2,g3)
    c: Coincident(g3,g4)
    c: Coincident(g4,g5)
    c: Coincident(g5,g2)
    c: Vertical(g2)
    c: Vertical(g4)
    c: Horizontal(g3)
    c: Horizontal(g5)
    c: Tangent(g1,g4)
    c: Tangent(g1,g2)
    c: Tangent(g0,g5)
    c: Tangent(g0,g3)
    c: Diameter(g1) = 22.4  'pocket_length'
    c: Diameter(g0) = 8.4  'pocket_width'
FEATURE [Sketcher::SketchObject] Sketch113  label="hhp_ts_screws_s"
  ArcFitTolerance = 1e-06
  AttachmentSupport = -> [XY_Plane148]
  ExternalTypes = [0]
  FullyConstrained = true
  MakeInternals = false
  MapMode = 5
  _ExternalGeoVersion = 0
  expr: .Constraints.diam = <<block_params>>.screw_drill_diam
  expr: .Constraints.placement_length = <<block_params>>.tswitch_placement_length
  expr: .Constraints.placement_width = <<block_params>>.tswitch_placement_width
  expr: .Constraints.spacing_length = <<block_params>>.tswitch_screw_spacing_length
  expr: .Constraints.spacing_width = <<block_params>>.tswitch_screw_spacing_width
  sketch-geometry (10):
    g0: Circle [constr] CenterX=25 CenterY=9 CenterZ=0 NormalX=0 NormalY=0 NormalZ=1 AngleXU=0 Radius=5.65
    g1: Circle [constr] CenterX=25 CenterY=9 CenterZ=0 NormalX=0 NormalY=0 NormalZ=1 AngleXU=0 Radius=5.5
    g2: LineSegment [constr] StartX=19.5 StartY=14.65 StartZ=0 EndX=19.5 EndY=3.35 EndZ=0
    g3: LineSegment [constr] StartX=19.5 StartY=3.35 StartZ=0 EndX=30.5 EndY=3.35 EndZ=0
    g4: LineSegment [constr] StartX=30.5 StartY=3.35 StartZ=0 EndX=30.5 EndY=14.65 EndZ=0
    g5: LineSegment [constr] StartX=30.5 StartY=14.65 StartZ=0 EndX=19.5 EndY=14.65 EndZ=0
    g6: Circle CenterX=30.5 CenterY=14.65 CenterZ=0 NormalX=0 NormalY=0 NormalZ=1 AngleXU=0 Radius=1.25
    g7: Circle CenterX=19.5 CenterY=14.65 CenterZ=0 NormalX=0 NormalY=0 NormalZ=1 AngleXU=0 Radius=1.25
    g8: Circle CenterX=19.5 CenterY=3.35 CenterZ=0 NormalX=0 NormalY=0 NormalZ=1 AngleXU=0 Radius=1.25
    g9: Circle CenterX=30.5 CenterY=3.35 CenterZ=0 NormalX=0 NormalY=0 NormalZ=1 AngleXU=0 Radius=1.25
  constraints (25):
    c: Coincident(g1,g0)
    c: DistanceY(g-1,g0) = 9  'placement_width'
    c: DistanceX(g-1,g0) = 25  'placement_length'
    c: Coincident(g2,g3)
    c: Coincident(g3,g4)
    c: Coincident(g4,g5)
    c: Coincident(g5,g2)
    c: Vertical(g2)
    c: Vertical(g4)
    c: Horizontal(g3)
    c: Horizontal(g5)
    c: Tangent(g0,g5)
    c: Tangent(g0,g3)
    c: Tangent(g1,g4)
    c: Tangent(g1,g2)
    c: Diameter(g1) = 11  'spacing_length'
    c: Diameter(g0) = 11.3  'spacing_width'
    c: Coincident(g6,g4)
    c: Coincident(g7,g2)
    c: Coincident(g8,g2)
    c: Coincident(g9,g3)
    c: Equal(g7,g6)
    c: Equal(g6,g9)
    c: Equal(g9,g8)
    c: Diameter(g8) = 2.5  'diam'
FEATURE [PartDesign::Pocket] Pocket045  label="hhp_ts_pocket"
  BaseFeature = -> Clone025
  Direction = (0,0,-1)
  Length = 0.8
  Length2 = 5
  Profile = -> Sketch112
  ReferenceAxis = -> Sketch112 [N_Axis]
  Refine = true
  SideType = 0
  Suppressed = false
  Type = 0
  Type2 = 0
  expr: Length = <<block_params>>.tswitch_pocket_depth
FEATURE [PartDesign::Pocket] Pocket046  label="hhp_ts_screws"
  BaseFeature = -> Pocket045
  Direction = (0,0,-1)
  Length = 4.5
  Length2 = 5
  Profile = -> Sketch113
  ReferenceAxis = -> Sketch113 [N_Axis]
  Refine = true
  SideType = 0
  Suppressed = false
  Type = 0
  Type2 = 0
  expr: Length = <<block_params>>.screw_drill_depth
FEATURE [PartDesign::Body] Body058  label="heater_heatsink_ptc_tswitch"
  AllowCompound = false
  Group = -> [Clone025,Sketch112,Sketch113,Pocket045,Pocket046]
  Origin = -> Origin148
  Tip = -> Pocket046
FEATURE [App::VarSet] VarSet003  label="bracket_params"
  feature_bend_flat = 4
  feature_bend_straight = 4
  feature_block_offset = 6
  feature_block_spacing = 6
  feature_deck_clear_block = 2.5
  feature_deck_clear_bracket = 1
  feature_screw_head = 5.5
  feature_screw_hole = 3.4
  feature_side_height = 21.5
  feature_side_recess = 1
  front_overlap_inner = 8
  front_overlap_outer = 4
  front_pad_diam = 8
  front_side_extension = 20
  front_side_screw_inset = 6
  front_side_screw_spacing = 17
  height_componets = 6.5
  height_extrusion = 20
  height_silicone_heater = 2
  height_stock = 9.5
  height_whopKinematic = 15.5
  material_bend = 1.6
  material_kfactor = 0.4
  material_thickness = 1.5
  rear_overhang_inner = 7
  rear_overhang_outer = 3
  rear_overlap = 1
  rear_pad_diam = 8
  rear_side_extension = 20
  rear_side_screw_inset = 5
  rear_side_screw_spacing = 17
FEATURE [PartDesign::Fillet] Fillet019  label="hrb_overlay_flt"
  Base = -> Fillet015 [Edge75,Edge76]
  BaseFeature = -> Fillet015
  Radius = 1.5
  Refine = true
  SupportTransform = false
  Suppressed = false
  UseAllEdges = false
FEATURE [PartDesign::Body] Body048  label="heater_rear_bracket"
  AllowCompound = false
  Group = -> [Sketch085,Sketch086,BaseBend,Bend,Extend,Pocket,Fillet,Fillet014,Fillet015,Fillet019]
  Origin = -> Origin138
  Tip = -> Fillet019
FEATURE [Part::FeaturePython] Unfold001  label="heater_rear_bracket_unfold"  # WARN: FeaturePython — macro-defined, semantics opaque (R4)
  baseObject = -> Fillet019 [Face19]
  kFactorStandard = 0
  kfactor = 0.4
  useManualKFactor = true
FEATURE [Sketcher::SketchObject] Unfold_Sketch002  label="heater_rear_bracket_unfold_cut"
  ArcFitTolerance = 1e-06
  ExternalTypes = [0]
  FullyConstrained = false
  MakeInternals = false
  _ExternalGeoVersion = 0
  sketch-geometry (25):
    g0: LineSegment StartX=47.4791 StartY=6.29431 StartZ=0 EndX=44.2199 EndY=1.63964 EndZ=0
    g1: ArcOfCircle CenterX=42.9912 CenterY=2.5 CenterZ=0 NormalX=0 NormalY=0 NormalZ=1 AngleXU=1.5708 Radius=1.5 StartAngle=3.14159 EndAngle=4.10152
    g2: LineSegment StartX=42.9912 StartY=1 StartZ=0 EndX=16.5203 EndY=1 EndZ=0
    g3: ArcOfCircle CenterX=16.5203 CenterY=2.5 CenterZ=0 NormalX=0 NormalY=0 NormalZ=1 AngleXU=1.5708 Radius=1.5 StartAngle=2.18166 EndAngle=3.14159
    g4: LineSegment StartX=12.0324 StartY=6.29431 StartZ=0 EndX=15.2916 EndY=1.63964 EndZ=0
    g5: ArcOfCircle CenterX=8.75575 CenterY=4 CenterZ=0 NormalX=0 NormalY=0 NormalZ=1 AngleXU=-3.14159 Radius=4 StartAngle=3.75246 EndAngle=6.28319
    g6: LineSegment StartX=4.75575 StartY=1 StartZ=0 EndX=4.75575 EndY=4 EndZ=0
    g7: LineSegment StartX=4.75575 StartY=1 StartZ=0 EndX=-17.5 EndY=1 EndZ=0
    g8: ArcOfCircle CenterX=-17.5 CenterY=-3 CenterZ=0 NormalX=0 NormalY=0 NormalZ=1 AngleXU=0 Radius=4 StartAngle=1.5708 EndAngle=3.14159
    g9: LineSegment StartX=-21.5 StartY=-3 StartZ=0 EndX=-21.5 EndY=-23 EndZ=0
    g10: ArcOfCircle CenterX=-17.5 CenterY=-23 CenterZ=0 NormalX=0 NormalY=0 NormalZ=1 AngleXU=0 Radius=4 StartAngle=3.14159 EndAngle=4.71239
    g11: LineSegment StartX=-17.5 StartY=-27 StartZ=0 EndX=-7.5 EndY=-27 EndZ=0
    g12: ArcOfCircle CenterX=-7.5 CenterY=-23 CenterZ=0 NormalX=0 NormalY=0 NormalZ=1 AngleXU=0 Radius=4 StartAngle=4.71239 EndAngle=6.28319
    g13: LineSegment StartX=-3.5 StartY=-8.5 StartZ=0 EndX=-3.5 EndY=-23 EndZ=0
    g14: ArcOfCircle CenterX=-2 CenterY=-8.5 CenterZ=0 NormalX=0 NormalY=0 NormalZ=1 AngleXU=-3.14159 Radius=1.5 StartAngle=4.71239 EndAngle=6.28319
    g15: LineSegment StartX=1.85575 StartY=-7 StartZ=0 EndX=-2 EndY=-7 EndZ=0
    g16: LineSegment StartX=2.75575 StartY=-7 StartZ=0 EndX=1.85575 EndY=-7 EndZ=0
    g17: LineSegment StartX=53.3708 StartY=-3.10654 StartZ=0 EndX=2.75575 EndY=-7 EndZ=0
    g18: ArcOfCircle CenterX=53.2558 CenterY=-1.61095 CenterZ=0 NormalX=0 NormalY=0 NormalZ=1 AngleXU=1.5708 Radius=1.5 StartAngle=3.21836 EndAngle=4.71239
    g19: LineSegment StartX=54.7558 StartY=4 StartZ=0 EndX=54.7558 EndY=-1.61095 EndZ=0
    g20: ArcOfCircle CenterX=50.7558 CenterY=4 CenterZ=0 NormalX=0 NormalY=0 NormalZ=1 AngleXU=-3.14159 Radius=4 StartAngle=3.14159 EndAngle=5.67232
    g21: Circle CenterX=50.7558 CenterY=4 CenterZ=0 NormalX=0 NormalY=0 NormalZ=1 AngleXU=-3.14159 Radius=1.7
    g22: Circle CenterX=8.75575 CenterY=4 CenterZ=0 NormalX=0 NormalY=0 NormalZ=1 AngleXU=-3.14159 Radius=1.7
    g23: Circle CenterX=-12.5 CenterY=-5 CenterZ=0 NormalX=0 NormalY=0 NormalZ=1 AngleXU=-1.5708 Radius=1.7
    g24: Circle CenterX=-12.5 CenterY=-22 CenterZ=0 NormalX=0 NormalY=0 NormalZ=1 AngleXU=-1.5708 Radius=1.7
FEATURE [Sketcher::SketchObject] Unfold_Sketch_bends001  label="heater_rear_bracket_unfold_bend"
  ArcFitTolerance = 1e-06
  ExternalTypes = [0]
  FullyConstrained = false
  MakeInternals = false
  Placement = pos=(0.063938,0,0.063938) rot=(0,1,0;0.785398rad)
  _ExternalGeoVersion = 0
  sketch-geometry (1):
    g0: LineSegment StartX=0.0904219 StartY=1 StartZ=0 EndX=0.0904219 EndY=-7 EndZ=0
FEATURE [App::VarSet] VarSet004  label="fan_params"
  feature_deck_clearance = 1
FEATURE [App::VarSet] VarSet005  label="template_params"
  drill_chamfer_face = 0.6
  drill_chamfer_inner = 0.4
  drill_hole_diam = 2
  feature_face_thickness = 5
  feature_side_clearance = 0
  feature_side_height = 6
  feature_side_length = 45
  feature_side_relief = 0.6
  feature_side_width = 5
  router_bit_1_16 = 1.5875
  router_bit_1_8 = 3.175
  router_bushing = 7.9375
  router_chamfer_face = 0.6
  router_clearance = 0.2
  router_dogbone = 0.3
  router_offset_1_16 = 3.375
  router_offset_1_8 = 2.58125
  expr: router_offset_1_16 = (router_bushing - router_bit_1_16) / 2 + router_clearance
  expr: router_offset_1_8 = (router_bushing - router_bit_1_8) / 2 + router_clearance
FEATURE [TechDraw::DrawSVGTemplate] Template
  EditableTexts = date_of_issue=1/28/26; document_type=Component Drawing; general_tolerances=ISO 2768-m; language_code=EN; part_material=6061/6063 Aluminum; revision_index=AAA; scale=1 : 1; sheet_number=1 / 1; title=Bedburner - Block (PTC & TSwitch)
  Height = 210
  Orientation = 1
  Template = <path>
  Width = 297
FEATURE [TechDraw::DrawProjGroupItem] View  label="td_block_ptc-ts_face_view"
  CoarseView = false
  Direction = (0,0,1)
  Focus = 100
  HardHidden = false
  IsoCount = 0
  IsoHidden = false
  IsoVisible = false
  LockPosition = false
  Perspective = false
  Rotation = 0
  RotationVector = (1,0,0)
  ScaleType = 0
  ScrubCount = 1
  SeamHidden = false
  SeamVisible = false
  SmoothHidden = false
  SmoothVisible = true
  Source = -> [Body058]
  Type = 0
  X = 197.566
  XDirection = (1,0,0)
  Y = 130.74
FEATURE [TechDraw::DrawViewSection] SectionView001  label="td_block_ptc-ts_cross-section"
  BaseView = -> View
  CoarseView = false
  CutSurfaceDisplay = 2
  Direction = (-1,-1e-16,0)
  FileGeomPattern = <path>
  FileHatchPattern = <path>
  Focus = 100
  FuseBeforeCut = false
  HardHidden = false
  HatchOffset = (0,0,0)
  HatchRotation = 0
  HatchScale = 1
  IsoCount = 0
  IsoHidden = false
  IsoVisible = false
  LockPosition = false
  NameGeomPattern = Diamond
  Perspective = false
  Rotation = -90
  ScaleType = 0
  ScrubCount = 1
  SeamHidden = false
  SeamVisible = false
  SectionDirection = 4
  SectionLineStretch = 1
  SectionNormal = (-1,-1e-16,0)
  SectionOrigin = (19.5,25,-10)
  SmoothHidden = false
  SmoothVisible = true
  Source = -> [Body058]
  TrimAfterCut = false
  UsePreviousCut = false
  X = 67.4829
  XDirection = (1e-16,-1,0)
  Y = 77.4189
FEATURE [TechDraw::DrawProjGroupItem] View008  label="td_block_ptc-ts_view"
  CoarseView = false
  Direction = (0.57735,-0.57735,0.57735)
  Focus = 100
  HardHidden = false
  IsoCount = 0
  IsoHidden = false
  IsoVisible = false
  LockPosition = false
  Perspective = false
  Rotation = 0
  RotationVector = (1,0,0)
  ScaleType = 0
  ScrubCount = 1
  SeamHidden = false
  SeamVisible = false
  SmoothHidden = false
  SmoothVisible = true
  Source = -> [Body058]
  Type = 0
  X = 86.1186
  XDirection = (0.707107,0.707107,0)
  Y = 155.198
FEATURE [TechDraw::DrawViewDimension] Dimension056
  AngleOverride = false
  Arbitrary = false
  ArbitraryTolerances = false
  BoxCorners = (2) [(-10,-25,-1e-07),(10,25,1e-07)]
  EqualTolerance = true
  ExtensionAngle = 0
  FormatSpec = %.2w
  FormatSpecOverTolerance = %+.2w
  FormatSpecUnderTolerance = %+.2w
  Inverted = false
  LineAngle = 0
  LockPosition = false
  MeasureType = 1
  OverTolerance = 0
  References2D = -> [SectionView001]
  Rotation = 0
  ScaleType = 0
  ShowUnits = false
  TheoreticalExact = false
  Type = 0
  UnderTolerance = 0
  UseActualArea = true
  X = -19.569
  Y = 38.7887
FEATURE [TechDraw::DrawViewDimension] Dimension057
  AngleOverride = false
  Arbitrary = false
  ArbitraryTolerances = false
  BoxCorners = (2) [(-10,-25,-1e-07),(10,25,1e-07)]
  EqualTolerance = true
  ExtensionAngle = 0
  FormatSpec = %.2w
  FormatSpecOverTolerance = %+.2w
  FormatSpecUnderTolerance = %+.2w
  Inverted = false
  LineAngle = 0
  LockPosition = false
  MeasureType = 1
  OverTolerance = 0
  References2D = -> [SectionView001]
  Rotation = 0
  ScaleType = 0
  ShowUnits = false
  TheoreticalExact = false
  Type = 0
  UnderTolerance = 0
  UseActualArea = true
  X = 22.222
  Y = 29.9809
FEATURE [TechDraw::DrawViewDimension] Dimension058
  AngleOverride = false
  Arbitrary = false
  ArbitraryTolerances = false
  BoxCorners = (2) [(-10,-25,-1e-07),(10,25,1e-07)]
  EqualTolerance = true
  ExtensionAngle = 0
  FormatSpec = %.2w
  FormatSpecOverTolerance = %+.2w
  FormatSpecUnderTolerance = %+.2w
  Inverted = false
  LineAngle = 0
  LockPosition = false
  MeasureType = 1
  OverTolerance = 0
  References2D = -> [SectionView001]
  Rotation = 0
  ScaleType = 0
  ShowUnits = false
  TheoreticalExact = false
  Type = 0
  UnderTolerance = 0
  UseActualArea = true
  X = 24.9277
  Y = 16.2793
FEATURE [TechDraw::DrawViewDimension] Dimension059
  AngleOverride = false
  Arbitrary = false
  ArbitraryTolerances = false
  BoxCorners = (2) [(-10,-25,-1e-07),(10,25,1e-07)]
  EqualTolerance = true
  ExtensionAngle = 0
  FormatSpec = %.2w
  FormatSpecOverTolerance = %+.2w
  FormatSpecUnderTolerance = %+.2w
  Inverted = false
  LineAngle = 0
  LockPosition = false
  MeasureType = 1
  OverTolerance = 0
  References2D = -> [SectionView001]
  Rotation = 0
  ScaleType = 0
  ShowUnits = false
  TheoreticalExact = false
  Type = 0
  UnderTolerance = 0
  UseActualArea = true
  X = 29.9087
  Y = -3.24971
FEATURE [TechDraw::DrawViewDimension] Dimension060
  AngleOverride = false
  Arbitrary = false
  ArbitraryTolerances = false
  BoxCorners = (2) [(-10,-25,-1e-07),(10,25,1e-07)]
  EqualTolerance = true
  ExtensionAngle = 0
  FormatSpec = %.2w
  FormatSpecOverTolerance = %+.2w
  FormatSpecUnderTolerance = %+.2w
  Inverted = false
  LineAngle = 0
  LockPosition = false
  MeasureType = 1
  OverTolerance = 0
  References2D = -> [SectionView001]
  Rotation = 0
  ScaleType = 0
  ShowUnits = false
  TheoreticalExact = false
  Type = 0
  UnderTolerance = 0
  UseActualArea = true
  X = 18.6223
  Y = -12.3299
FEATURE [TechDraw::DrawViewDimension] Dimension061
  AngleOverride = false
  Arbitrary = false
  ArbitraryTolerances = false
  BoxCorners = (2) [(-10,-25,-1e-07),(10,25,1e-07)]
  EqualTolerance = true
  ExtensionAngle = 0
  FormatSpec = %.2w
  FormatSpecOverTolerance = %+.2w
  FormatSpecUnderTolerance = %+.2w
  Inverted = false
  LineAngle = 0
  LockPosition = false
  MeasureType = 1
  OverTolerance = 0
  References2D = -> [SectionView001]
  Rotation = 0
  ScaleType = 0
  ShowUnits = false
  TheoreticalExact = false
  Type = 0
  UnderTolerance = 0
  UseActualArea = true
  X = 18.8586
  Y = 3.75029
FEATURE [TechDraw::DrawViewDimension] Dimension064
  AngleOverride = false
  Arbitrary = false
  ArbitraryTolerances = false
  BoxCorners = (2) [(-25,-25,-1e-07),(25,25,1e-07)]
  EqualTolerance = true
  ExtensionAngle = 0
  FormatSpec = %.2w
  FormatSpecOverTolerance = %+.2w
  FormatSpecUnderTolerance = %+.2w
  Inverted = false
  LineAngle = 0
  LockPosition = false
  MeasureType = 1
  OverTolerance = 0
  References2D = -> [View]
  Rotation = 0
  ScaleType = 0
  ShowUnits = false
  TheoreticalExact = false
  Type = 2
  UnderTolerance = 0
  UseActualArea = true
  X = 43.0458
  Y = 3.5
FEATURE [TechDraw::DrawViewDimension] Dimension067
  AngleOverride = false
  Arbitrary = false
  ArbitraryTolerances = false
  BoxCorners = (2) [(-25,-25,-1e-07),(25,25,1e-07)]
  EqualTolerance = true
  ExtensionAngle = 0
  FormatSpec = %.2w
  FormatSpecOverTolerance = %+.2w
  FormatSpecUnderTolerance = %+.2w
  Inverted = false
  LineAngle = 0
  LockPosition = false
  MeasureType = 1
  OverTolerance = 0
  References2D = -> [View]
  Rotation = 0
  ScaleType = 0
  ShowUnits = false
  TheoreticalExact = false
  Type = 2
  UnderTolerance = 0
  UseActualArea = true
  X = 50.0458
  Y = 32.1238
FEATURE [TechDraw::DrawViewDimension] Dimension068
  AngleOverride = false
  Arbitrary = false
  ArbitraryTolerances = false
  BoxCorners = (2) [(-25,-25,-1e-07),(25,25,1e-07)]
  EqualTolerance = true
  ExtensionAngle = 0
  FormatSpec = %.2w
  FormatSpecOverTolerance = %+.2w
  FormatSpecUnderTolerance = %+.2w
  Inverted = false
  LineAngle = 0
  LockPosition = false
  MeasureType = 1
  OverTolerance = 0
  References2D = -> [View]
  Rotation = 0
  ScaleType = 0
  ShowUnits = false
  TheoreticalExact = false
  Type = 1
  UnderTolerance = 0
  UseActualArea = true
  X = 43.9908
  Y = 49.928
FEATURE [TechDraw::DrawViewDimension] Dimension069
  AngleOverride = false
  Arbitrary = false
  ArbitraryTolerances = false
  BoxCorners = (2) [(-25,-25,-1e-07),(25,25,1e-07)]
  EqualTolerance = true
  ExtensionAngle = 0
  FormatSpec = %.2w
  FormatSpecOverTolerance = %+.2w
  FormatSpecUnderTolerance = %+.2w
  Inverted = false
  LineAngle = 0
  LockPosition = false
  MeasureType = 1
  OverTolerance = 0
  References2D = -> [View]
  Rotation = 0
  ScaleType = 0
  ShowUnits = false
  TheoreticalExact = false
  Type = 0
  UnderTolerance = 0
  UseActualArea = true
  X = 33.8749
  Y = 56.928
FEATURE [TechDraw::DrawViewDimension] Dimension070
  AngleOverride = false
  Arbitrary = false
  ArbitraryTolerances = false
  BoxCorners = (2) [(-25,-25,-1e-07),(25,25,1e-07)]
  EqualTolerance = true
  ExtensionAngle = 0
  FormatSpec = %.2w
  FormatSpecOverTolerance = %+.2w
  FormatSpecUnderTolerance = %+.2w
  Inverted = false
  LineAngle = 0
  LockPosition = false
  MeasureType = 1
  OverTolerance = 0
  References2D = -> [View]
  Rotation = 0
  ScaleType = 0
  ShowUnits = false
  TheoreticalExact = false
  Type = 0
  UnderTolerance = 0
  UseActualArea = true
  X = 57.0458
  Y = 43.3612
FEATURE [TechDraw::DrawViewDimension] Dimension073
  AngleOverride = false
  Arbitrary = false
  ArbitraryTolerances = false
  BoxCorners = (2) [(-25,-25,-1e-07),(25,25,1e-07)]
  EqualTolerance = true
  ExtensionAngle = 0
  FormatSpec = %.2w
  FormatSpecOverTolerance = %+.2w
  FormatSpecUnderTolerance = %+.2w
  Inverted = false
  LineAngle = 0
  LockPosition = false
  MeasureType = 1
  OverTolerance = 0
  References2D = -> [View]
  Rotation = 0
  ScaleType = 0
  ShowUnits = false
  TheoreticalExact = false
  Type = 0
  UnderTolerance = 0
  UseActualArea = true
  X = 23.1993
  Y = -46.2301
FEATURE [TechDraw::DrawViewDimension] Dimension075
  AngleOverride = false
  Arbitrary = false
  ArbitraryTolerances = false
  BoxCorners = (2) [(-25,-25,-1e-07),(25,25,1e-07)]
  EqualTolerance = true
  ExtensionAngle = 0
  FormatSpec = %.2w
  FormatSpecOverTolerance = %+.2w
  FormatSpecUnderTolerance = %+.2w
  Inverted = false
  LineAngle = 0
  LockPosition = false
  MeasureType = 1
  OverTolerance = 0
  References2D = -> [View]
  Rotation = 0
  ScaleType = 0
  ShowUnits = false
  TheoreticalExact = false
  Type = 1
  UnderTolerance = 0
  UseActualArea = true
  X = 17.8458
  Y = 38.936
FEATURE [TechDraw::DrawViewDimension] Dimension085
  AngleOverride = false
  Arbitrary = false
  ArbitraryTolerances = false
  BoxCorners = (2) [(-25,-25,-1e-07),(25,25,1e-07)]
  EqualTolerance = true
  ExtensionAngle = 0
  FormatSpec = %.2w
  FormatSpecOverTolerance = %+.2w
  FormatSpecUnderTolerance = %+.2w
  Inverted = false
  LineAngle = 0
  LockPosition = false
  MeasureType = 1
  OverTolerance = 0
  References2D = -> [View]
  Rotation = 0
  ScaleType = 0
  ShowUnits = false
  TheoreticalExact = false
  Type = 0
  UnderTolerance = 0
  UseActualArea = true
  X = 30.6503
  Y = 3.5
FEATURE [TechDraw::DrawViewDimension] Dimension086
  AngleOverride = false
  Arbitrary = false
  ArbitraryTolerances = false
  BoxCorners = (2) [(-25,-25,-1e-07),(25,25,1e-07)]
  EqualTolerance = true
  ExtensionAngle = 0
  FormatSpec = %.2w
  FormatSpecOverTolerance = %+.2w
  FormatSpecUnderTolerance = %+.2w
  Inverted = false
  LineAngle = 0
  LockPosition = false
  MeasureType = 1
  OverTolerance = 0
  References2D = -> [View]
  Rotation = 0
  ScaleType = 0
  ShowUnits = false
  TheoreticalExact = false
  Type = 0
  UnderTolerance = 0
  UseActualArea = true
  X = 31.9519
  Y = 36.8401
FEATURE [TechDraw::DrawViewDimension] Dimension088
  AngleOverride = false
  Arbitrary = false
  ArbitraryTolerances = false
  BoxCorners = (2) [(-25,-25,-1e-07),(25,25,1e-07)]
  EqualTolerance = true
  ExtensionAngle = 0
  FormatSpec = %.2w
  FormatSpecOverTolerance = %+.2w
  FormatSpecUnderTolerance = %+.2w
  Inverted = false
  LineAngle = 0
  LockPosition = false
  MeasureType = 1
  OverTolerance = 0
  References2D = -> [View]
  Rotation = 0
  ScaleType = 0
  ShowUnits = false
  TheoreticalExact = false
  Type = 1
  UnderTolerance = 0
  UseActualArea = true
  X = 20.4808
  Y = -34.7314
FEATURE [TechDraw::DrawViewDimension] Dimension089
  AngleOverride = false
  Arbitrary = false
  ArbitraryTolerances = false
  BoxCorners = (2) [(-25,-25,-1e-07),(25,25,1e-07)]
  EqualTolerance = true
  ExtensionAngle = 0
  FormatSpec = %.2w
  FormatSpecOverTolerance = %+.2w
  FormatSpecUnderTolerance = %+.2w
  Inverted = false
  LineAngle = 0
  LockPosition = false
  MeasureType = 1
  OverTolerance = 0
  References2D = -> [View]
  Rotation = 0
  ScaleType = 0
  ShowUnits = false
  TheoreticalExact = false
  Type = 0
  UnderTolerance = 0
  UseActualArea = true
  X = 25.8552
  Y = -33.59
FEATURE [TechDraw::DrawViewDimension] Dimension090
  AngleOverride = false
  Arbitrary = false
  ArbitraryTolerances = false
  BoxCorners = (2) [(-25,-25,-1e-07),(25,25,1e-07)]
  EqualTolerance = true
  ExtensionAngle = 0
  FormatSpec = %.2w
  FormatSpecOverTolerance = %+.2w
  FormatSpecUnderTolerance = %+.2w
  Inverted = false
  LineAngle = 0
  LockPosition = false
  MeasureType = 1
  OverTolerance = 0
  References2D = -> [View]
  Rotation = 0
  ScaleType = 0
  ShowUnits = false
  TheoreticalExact = false
  Type = 2
  UnderTolerance = 0
  UseActualArea = true
  X = 37.6503
  Y = -33.8007
FEATURE [TechDraw::DrawViewDimension] Dimension091
  AngleOverride = false
  Arbitrary = false
  ArbitraryTolerances = false
  BoxCorners = (2) [(-25,-25,-1e-07),(25,25,1e-07)]
  EqualTolerance = true
  ExtensionAngle = 0
  FormatSpec = %.2w
  FormatSpecOverTolerance = %+.2w
  FormatSpecUnderTolerance = %+.2w
  Inverted = false
  LineAngle = 0
  LockPosition = false
  MeasureType = 1
  OverTolerance = 0
  References2D = -> [View]
  Rotation = 0
  ScaleType = 0
  ShowUnits = false
  TheoreticalExact = false
  Type = 1
  UnderTolerance = 0
  UseActualArea = true
  X = -36.3756
  Y = -27.7314
FEATURE [TechDraw::DrawViewDimension] Dimension092
  AngleOverride = false
  Arbitrary = false
  ArbitraryTolerances = false
  BoxCorners = (2) [(-25,-25,-1e-07),(25,25,1e-07)]
  EqualTolerance = true
  ExtensionAngle = 0
  FormatSpec = %.2w
  FormatSpecOverTolerance = %+.2w
  FormatSpecUnderTolerance = %+.2w
  Inverted = false
  LineAngle = 0
  LockPosition = false
  MeasureType = 1
  OverTolerance = 0
  References2D = -> [View]
  Rotation = 0
  ScaleType = 0
  ShowUnits = false
  TheoreticalExact = false
  Type = 2
  UnderTolerance = 0
  UseActualArea = true
  X = -42.7532
  Y = -6.97119
FEATURE [TechDraw::DrawViewDimension] Dimension093
  AngleOverride = false
  Arbitrary = false
  ArbitraryTolerances = false
  BoxCorners = (2) [(-25,-25,-1e-07),(25,25,1e-07)]
  EqualTolerance = true
  ExtensionAngle = 0
  FormatSpec = %.2w
  FormatSpecOverTolerance = %+.2w
  FormatSpecUnderTolerance = %+.2w
  Inverted = false
  LineAngle = 0
  LockPosition = false
  MeasureType = 1
  OverTolerance = 0
  References2D = -> [View]
  Rotation = 0
  ScaleType = 0
  ShowUnits = false
  TheoreticalExact = false
  Type = 0
  UnderTolerance = 0
  UseActualArea = true
  X = -51.7429
  Y = 20.4595
FEATURE [TechDraw::DrawViewDimension] Dimension094
  AngleOverride = false
  Arbitrary = false
  ArbitraryTolerances = false
  BoxCorners = (2) [(-25,-25,-1e-07),(25,25,1e-07)]
  EqualTolerance = true
  ExtensionAngle = 0
  FormatSpec = %.2w
  FormatSpecOverTolerance = %+.2w
  FormatSpecUnderTolerance = %+.2w
  Inverted = false
  LineAngle = 0
  LockPosition = false
  MeasureType = 1
  OverTolerance = 0
  References2D = -> [View]
  Rotation = 0
  ScaleType = 0
  ShowUnits = false
  TheoreticalExact = false
  Type = 0
  UnderTolerance = 0
  UseActualArea = true
  X = -40.3294
  Y = 19.2638
FEATURE [TechDraw::DrawViewDimension] Dimension095
  AngleOverride = false
  Arbitrary = false
  ArbitraryTolerances = false
  BoxCorners = (2) [(-25,-25,-1e-07),(25,25,1e-07)]
  EqualTolerance = true
  ExtensionAngle = 0
  FormatSpec = %.2w
  FormatSpecOverTolerance = %+.2w
  FormatSpecUnderTolerance = %+.2w
  Inverted = false
  LineAngle = 0
  LockPosition = false
  MeasureType = 1
  OverTolerance = 0
  References2D = -> [View]
  Rotation = 0
  ScaleType = 0
  ShowUnits = false
  TheoreticalExact = false
  Type = 0
  UnderTolerance = 0
  UseActualArea = true
  X = -57.0518
  Y = -2.2991
FEATURE [TechDraw::DrawViewDimension] Dimension096
  AngleOverride = false
  Arbitrary = false
  ArbitraryTolerances = false
  BoxCorners = (2) [(-25,-25,-1e-07),(25,25,1e-07)]
  EqualTolerance = true
  ExtensionAngle = 0
  FormatSpec = %.2w
  FormatSpecOverTolerance = %+.2w
  FormatSpecUnderTolerance = %+.2w
  Inverted = false
  LineAngle = 0
  LockPosition = false
  MeasureType = 1
  OverTolerance = 0
  References2D = -> [View]
  Rotation = 0
  ScaleType = 0
  ShowUnits = false
  TheoreticalExact = false
  Type = 0
  UnderTolerance = 0
  UseActualArea = true
  X = -51.6972
  Y = 9.48386
FEATURE [TechDraw::DrawSVGTemplate] Template002
  EditableTexts = date_of_issue=1/28/26; document_type=Component Drawing; general_tolerances=ISO 2768-m; language_code=EN; part_material=A1008 Mild Steel - 16ga (1.5mm); revision_index=AAA; scale=1 : 1; sheet_number=1 / 1; title=Bedburner - Rear Bracket
  Height = 210
  Orientation = 1
  Template = <path>
  Width = 297
FEATURE [TechDraw::DrawProjGroupItem] View009  label="Front001"
  CoarseView = false
  Direction = (0,-1,0)
  Focus = 100
  HardHidden = false
  IsoCount = 0
  IsoHidden = false
  IsoVisible = false
  LockPosition = true
  Perspective = false
  Rotation = 0
  RotationVector = (1,0,0)
  ScaleType = 2
  ScrubCount = 1
  SeamHidden = false
  SeamVisible = false
  SmoothHidden = false
  SmoothVisible = true
  Source = -> [Body048]
  Type = 0
  X = 0
  XDirection = (1,0,0)
  Y = 0
FEATURE [TechDraw::DrawProjGroupItem] ProjItem006  label="FrontTopRight001"
  CoarseView = false
  Direction = (0.57735,-0.57735,0.57735)
  Focus = 100
  HardHidden = false
  IsoCount = 0
  IsoHidden = false
  IsoVisible = false
  LockPosition = false
  Perspective = false
  Rotation = 0
  RotationVector = (1,0,0)
  ScaleType = 0
  ScrubCount = 1
  SeamHidden = false
  SeamVisible = false
  SmoothHidden = false
  SmoothVisible = true
  Source = -> [Body048]
  Type = 7
  X = -109.637
  XDirection = (0.707107,0.707107,0)
  Y = -66.443
FEATURE [TechDraw::DrawProjGroupItem] ProjItem009  label="Top"
  CoarseView = false
  Direction = (0,0,1)
  Focus = 100
  HardHidden = false
  IsoCount = 0
  IsoHidden = false
  IsoVisible = false
  LockPosition = false
  Perspective = false
  Rotation = 0
  RotationVector = (1,0,0)
  ScaleType = 0
  ScrubCount = 1
  SeamHidden = false
  SeamVisible = false
  SmoothHidden = false
  SmoothVisible = true
  Source = -> [Body048]
  Type = 4
  X = 0
  XDirection = (1,0,0)
  Y = -55.9996
FEATURE [TechDraw::DrawProjGroupItem] ProjItem010  label="Right"
  CoarseView = false
  Direction = (1,-1e-16,0)
  Focus = 100
  HardHidden = false
  IsoCount = 0
  IsoHidden = false
  IsoVisible = false
  LockPosition = false
  Perspective = false
  Rotation = 0
  RotationVector = (1,0,0)
  ScaleType = 0
  ScrubCount = 1
  SeamHidden = false
  SeamVisible = false
  SmoothHidden = false
  SmoothVisible = true
  Source = -> [Body048]
  Type = 2
  X = -96.3122
  XDirection = (1e-16,1,0)
  Y = 0
FEATURE [TechDraw::DrawProjGroup] ProjGroup
  Anchor = -> View009
  AutoDistribute = false
  LockPosition = false
  ProjectionType = 0
  Rotation = 0
  ScaleType = 0
  Source = -> [Body048]
  Views = -> [View009,ProjItem006,ProjItem009,ProjItem010]
  X = 195.684
  Y = 160.028
  spacingX = 15
  spacingY = 15
FEATURE [TechDraw::DrawViewDimension] Dimension097
  AngleOverride = false
  Arbitrary = false
  ArbitraryTolerances = false
  BoxCorners = (2) [(-28,-11.5,-1e-07),(28,11.5,1e-07)]
  EqualTolerance = true
  ExtensionAngle = 0
  FormatSpec = %.2w
  FormatSpecOverTolerance = %+.2w
  FormatSpecUnderTolerance = %+.2w
  Inverted = false
  LineAngle = 0
  LockPosition = false
  MeasureType = 1
  OverTolerance = 0
  References2D = -> [View009]
  Rotation = 0
  ScaleType = 0
  ShowUnits = false
  TheoreticalExact = false
  Type = 6
  UnderTolerance = 0
  UseActualArea = true
  X = 17.793
  Y = -5.76893
FEATURE [TechDraw::DrawViewDimension] Dimension098
  AngleOverride = false
  Arbitrary = false
  ArbitraryTolerances = false
  BoxCorners = (2) [(-28,-11.5,-1e-07),(28,11.5,1e-07)]
  EqualTolerance = true
  ExtensionAngle = 0
  FormatSpec = %.2w
  FormatSpecOverTolerance = %+.2w
  FormatSpecUnderTolerance = %+.2w
  Inverted = false
  LineAngle = 0
  LockPosition = false
  MeasureType = 1
  OverTolerance = 0
  References2D = -> [View009]
  Rotation = 0
  ScaleType = 0
  ShowUnits = false
  TheoreticalExact = false
  Type = 0
  UnderTolerance = 0
  UseActualArea = true
  X = 53.8432
  Y = -22.08
FEATURE [TechDraw::DrawViewDimension] Dimension099
  AngleOverride = false
  Arbitrary = false
  ArbitraryTolerances = false
  BoxCorners = (2) [(-28,-11.5,-1e-07),(28,11.5,1e-07)]
  EqualTolerance = true
  ExtensionAngle = 0
  FormatSpec = %.2w
  FormatSpecOverTolerance = %+.2w
  FormatSpecUnderTolerance = %+.2w
  Inverted = false
  LineAngle = 0
  LockPosition = false
  MeasureType = 1
  OverTolerance = 0
  References2D = -> [View009]
  Rotation = 0
  ScaleType = 0
  ShowUnits = false
  TheoreticalExact = false
  Type = 0
  UnderTolerance = 0
  UseActualArea = true
  X = 3.4163
  Y = 26.4826
FEATURE [TechDraw::DrawViewDimension] Dimension100
  AngleOverride = false
  Arbitrary = false
  ArbitraryTolerances = false
  BoxCorners = (2) [(-28,-11.5,-1e-07),(28,11.5,1e-07)]
  EqualTolerance = true
  ExtensionAngle = 0
  FormatSpec = R%.2w
  FormatSpecOverTolerance = %+.2w
  FormatSpecUnderTolerance = %+.2w
  Inverted = false
  LineAngle = 0
  LockPosition = false
  MeasureType = 1
  OverTolerance = 0
  References2D = -> [View009]
  Rotation = 0
  ScaleType = 0
  ShowUnits = false
  TheoreticalExact = false
  Type = 4
  UnderTolerance = 0
  UseActualArea = true
  X = 33.041
  Y = 25.3704
FEATURE [TechDraw::DrawViewDimension] Dimension101
  AngleOverride = false
  Arbitrary = false
  ArbitraryTolerances = false
  BoxCorners = (2) [(-28,-17.5,-1e-07),(28,17.5,1e-07)]
  EqualTolerance = true
  ExtensionAngle = 0
  FormatSpec = %.2w
  FormatSpecOverTolerance = %+.2w
  FormatSpecUnderTolerance = %+.2w
  Inverted = false
  LineAngle = 0
  LockPosition = false
  MeasureType = 1
  OverTolerance = 0
  References2D = -> [ProjItem009]
  Rotation = 0
  ScaleType = 0
  ShowUnits = false
  TheoreticalExact = false
  Type = 0
  UnderTolerance = 0
  UseActualArea = true
  X = 38.8034
  Y = -22.6748
FEATURE [TechDraw::DrawViewDimension] Dimension102
  AngleOverride = false
  Arbitrary = false
  ArbitraryTolerances = false
  BoxCorners = (2) [(-28,-17.5,-1e-07),(28,17.5,1e-07)]
  EqualTolerance = true
  ExtensionAngle = 0
  FormatSpec = %.2w
  FormatSpecOverTolerance = %+.2w
  FormatSpecUnderTolerance = %+.2w
  Inverted = false
  LineAngle = 0
  LockPosition = false
  MeasureType = 1
  OverTolerance = 0
  References2D = -> [ProjItem009]
  Rotation = 0
  ScaleType = 0
  ShowUnits = false
  TheoreticalExact = false
  Type = 0
  UnderTolerance = 0
  UseActualArea = true
  X = 36.1659
  Y = 6.99827
FEATURE [TechDraw::DrawViewDimension] Dimension103
  AngleOverride = false
  Arbitrary = false
  ArbitraryTolerances = false
  BoxCorners = (2) [(-28,-17.5,-1e-07),(28,17.5,1e-07)]
  EqualTolerance = true
  ExtensionAngle = 0
  FormatSpec = %.2w
  FormatSpecOverTolerance = %+.2w
  FormatSpecUnderTolerance = %+.2w
  Inverted = false
  LineAngle = 0
  LockPosition = false
  MeasureType = 1
  OverTolerance = 0
  References2D = -> [ProjItem009]
  Rotation = 0
  ScaleType = 0
  ShowUnits = false
  TheoreticalExact = false
  Type = 0
  UnderTolerance = 0
  UseActualArea = true
  X = -0.75
  Y = -15.6748
FEATURE [TechDraw::DrawViewDimension] Dimension104
  AngleOverride = false
  Arbitrary = false
  ArbitraryTolerances = false
  BoxCorners = (2) [(-28,-17.5,-1e-07),(28,17.5,1e-07)]
  EqualTolerance = true
  ExtensionAngle = 0
  FormatSpec = %.2w
  FormatSpecOverTolerance = %+.2w
  FormatSpecUnderTolerance = %+.2w
  Inverted = false
  LineAngle = 0
  LockPosition = false
  MeasureType = 1
  OverTolerance = 0
  References2D = -> [ProjItem009]
  Rotation = 0
  ScaleType = 0
  ShowUnits = false
  TheoreticalExact = false
  Type = 1
  UnderTolerance = 0
  UseActualArea = true
  X = -3
  Y = 12.5132
FEATURE [TechDraw::DrawViewDimension] Dimension105
  AngleOverride = false
  Arbitrary = false
  ArbitraryTolerances = false
  BoxCorners = (2) [(-28,-17.5,-1e-07),(28,17.5,1e-07)]
  EqualTolerance = true
  ExtensionAngle = 0
  FormatSpec = ⌀%.2w
  FormatSpecOverTolerance = %+.2w
  FormatSpecUnderTolerance = %+.2w
  Inverted = false
  LineAngle = 0
  LockPosition = false
  MeasureType = 1
  OverTolerance = 0
  References2D = -> [ProjItem009]
  Rotation = 0
  ScaleType = 0
  ShowUnits = false
  TheoreticalExact = false
  Type = 5
  UnderTolerance = 0
  UseActualArea = true
  X = -39.2254
  Y = -6.05528
FEATURE [TechDraw::DrawViewDimension] Dimension106
  AngleOverride = false
  Arbitrary = false
  ArbitraryTolerances = false
  BoxCorners = (2) [(-28,-17.5,-1e-07),(28,17.5,1e-07)]
  EqualTolerance = true
  ExtensionAngle = 0
  FormatSpec = R%.2w
  FormatSpecOverTolerance = %+.2w
  FormatSpecUnderTolerance = %+.2w
  Inverted = false
  LineAngle = 0
  LockPosition = false
  MeasureType = 1
  OverTolerance = 0
  References2D = -> [ProjItem009]
  Rotation = 0
  ScaleType = 0
  ShowUnits = false
  TheoreticalExact = false
  Type = 4
  UnderTolerance = 0
  UseActualArea = true
  X = -42.8449
  Y = -22.4271
FEATURE [TechDraw::DrawViewDimension] Dimension107
  AngleOverride = false
  Arbitrary = false
  ArbitraryTolerances = false
  BoxCorners = (2) [(-17.5,-11.5,-1e-07),(17.5,11.5,1e-07)]
  EqualTolerance = true
  ExtensionAngle = 0
  FormatSpec = %.2w
  FormatSpecOverTolerance = %+.2w
  FormatSpecUnderTolerance = %+.2w
  Inverted = false
  LineAngle = 0
  LockPosition = false
  MeasureType = 1
  OverTolerance = 0
  References2D = -> [ProjItem010]
  Rotation = 0
  ScaleType = 0
  ShowUnits = false
  TheoreticalExact = false
  Type = 0
  UnderTolerance = 0
  UseActualArea = true
  X = 4
  Y = -11.9277
FEATURE [TechDraw::DrawViewDimension] Dimension108
  AngleOverride = false
  Arbitrary = false
  ArbitraryTolerances = false
  BoxCorners = (2) [(-17.5,-11.5,-1e-07),(17.5,11.5,1e-07)]
  EqualTolerance = true
  ExtensionAngle = 0
  FormatSpec = %.2w
  FormatSpecOverTolerance = %+.2w
  FormatSpecUnderTolerance = %+.2w
  Inverted = false
  LineAngle = 0
  LockPosition = false
  MeasureType = 1
  OverTolerance = 0
  References2D = -> [ProjItem010]
  Rotation = 0
  ScaleType = 0
  ShowUnits = false
  TheoreticalExact = false
  Type = 0
  UnderTolerance = 0
  UseActualArea = true
  X = 28.7525
  Y = -18.9277
FEATURE [TechDraw::DrawViewDimension] Dimension109
  AngleOverride = false
  Arbitrary = false
  ArbitraryTolerances = false
  BoxCorners = (2) [(-17.5,-11.5,-1e-07),(17.5,11.5,1e-07)]
  EqualTolerance = true
  ExtensionAngle = 0
  FormatSpec = %.2w
  FormatSpecOverTolerance = %+.2w
  FormatSpecUnderTolerance = %+.2w
  Inverted = false
  LineAngle = 0
  LockPosition = false
  MeasureType = 1
  OverTolerance = 0
  References2D = -> [ProjItem010]
  Rotation = 0
  ScaleType = 0
  ShowUnits = false
  TheoreticalExact = false
  Type = 0
  UnderTolerance = 0
  UseActualArea = true
  X = -38.2443
  Y = -0.75
FEATURE [TechDraw::DrawViewDimension] Dimension110
  AngleOverride = false
  Arbitrary = false
  ArbitraryTolerances = false
  BoxCorners = (2) [(-17.5,-11.5,-1e-07),(17.5,11.5,1e-07)]
  EqualTolerance = true
  ExtensionAngle = 0
  FormatSpec = %.2w
  FormatSpecOverTolerance = %+.2w
  FormatSpecUnderTolerance = %+.2w
  Inverted = false
  LineAngle = 0
  LockPosition = false
  MeasureType = 1
  OverTolerance = 0
  References2D = -> [ProjItem010]
  Rotation = 0
  ScaleType = 0
  ShowUnits = false
  TheoreticalExact = false
  Type = 0
  UnderTolerance = 0
  UseActualArea = true
  X = -26.1534
  Y = 3.75
FEATURE [TechDraw::DrawViewDimension] Dimension111
  AngleOverride = false
  Arbitrary = false
  ArbitraryTolerances = false
  BoxCorners = (2) [(-17.5,-11.5,-1e-07),(17.5,11.5,1e-07)]
  EqualTolerance = true
  ExtensionAngle = 0
  FormatSpec = %.2w
  FormatSpecOverTolerance = %+.2w
  FormatSpecUnderTolerance = %+.2w
  Inverted = false
  LineAngle = 0
  LockPosition = false
  MeasureType = 1
  OverTolerance = 0
  References2D = -> [ProjItem010]
  Rotation = 0
  ScaleType = 0
  ShowUnits = false
  TheoreticalExact = false
  Type = 0
  UnderTolerance = 0
  UseActualArea = true
  X = 23.7793
  Y = -2.5
FEATURE [TechDraw::DrawViewDimension] Dimension112
  AngleOverride = false
  Arbitrary = false
  ArbitraryTolerances = false
  BoxCorners = (2) [(-17.5,-11.5,-1e-07),(17.5,11.5,1e-07)]
  EqualTolerance = true
  ExtensionAngle = 0
  FormatSpec = R%.2w
  FormatSpecOverTolerance = %+.2w
  FormatSpecUnderTolerance = %+.2w
  Inverted = false
  LineAngle = 0
  LockPosition = false
  MeasureType = 1
  OverTolerance = 0
  References2D = -> [ProjItem010]
  Rotation = 0
  ScaleType = 0
  ShowUnits = false
  TheoreticalExact = false
  Type = 4
  UnderTolerance = 0
  UseActualArea = true
  X = 16.0414
  Y = 22.3765
FEATURE [TechDraw::DrawViewDimension] Dimension113
  AngleOverride = false
  Arbitrary = false
  ArbitraryTolerances = false
  BoxCorners = (2) [(-17.5,-11.5,-1e-07),(17.5,11.5,1e-07)]
  EqualTolerance = true
  ExtensionAngle = 0
  FormatSpec = R%.2w
  FormatSpecOverTolerance = %+.2w
  FormatSpecUnderTolerance = %+.2w
  Inverted = false
  LineAngle = 0
  LockPosition = false
  MeasureType = 1
  OverTolerance = 0
  References2D = -> [ProjItem010]
  Rotation = 0
  ScaleType = 0
  ShowUnits = false
  TheoreticalExact = false
  Type = 4
  UnderTolerance = 0
  UseActualArea = true
  X = 5.55371
  Y = 26.5083
FEATURE [TechDraw::DrawViewDimension] Dimension114
  AngleOverride = false
  Arbitrary = false
  ArbitraryTolerances = false
  BoxCorners = (2) [(-28,-17.5,-1e-07),(28,17.5,1e-07)]
  EqualTolerance = true
  ExtensionAngle = 0
  FormatSpec = %.2w
  FormatSpecOverTolerance = %+.2w
  FormatSpecUnderTolerance = %+.2w
  Inverted = false
  LineAngle = 0
  LockPosition = false
  MeasureType = 1
  OverTolerance = 0
  References2D = -> [ProjItem009]
  Rotation = 0
  ScaleType = 0
  ShowUnits = false
  TheoreticalExact = false
  Type = 0
  UnderTolerance = 0
  UseActualArea = true
  X = 31.5245
  Y = -5.88677
FEATURE [TechDraw::DrawViewDimension] Dimension115
  AngleOverride = false
  Arbitrary = false
  ArbitraryTolerances = false
  BoxCorners = (2) [(-17.5,-11.5,-1e-07),(17.5,11.5,1e-07)]
  EqualTolerance = true
  ExtensionAngle = 0
  FormatSpec = %.2w
  FormatSpecOverTolerance = %+.2w
  FormatSpecUnderTolerance = %+.2w
  Inverted = false
  LineAngle = 0
  LockPosition = false
  MeasureType = 1
  OverTolerance = 0
  References2D = -> [ProjItem010]
  Rotation = 0
  ScaleType = 0
  ShowUnits = false
  TheoreticalExact = false
  Type = 0
  UnderTolerance = 0
  UseActualArea = true
  X = -19.8445
  Y = 25.6923
FEATURE [App::Link] HFS5_2020_160  label="HFS5-2020-161"
  LinkPlacement = pos=(0,0,0) rot=(-1,0,0;1.5708rad)
  LinkedObject = -> Part__Feature009
  Placement = pos=(0,0,0) rot=(-1,0,0;1.5708rad)
FEATURE [App::FeaturePython] GroundedJoint  # Assembly grounded joint (typed FeaturePython)
  ObjectToGround = -> HFS5_2020_160
  Placement = pos=(0,0,0) rot=(-1,0,0;1.5708rad)
FEATURE [App::Link] tnut_2020_m3_roll  label="tnut_2020_m3_roll001"
  LinkPlacement = pos=(-4.8,-108.5,0.1) rot=(0,0.707107,0.707107;3.14159rad)
  LinkedObject = -> Part__Feature008
  Placement = pos=(-4.8,-108.5,0.1) rot=(0,0.707107,0.707107;3.14159rad)
FEATURE [App::Link] tnut_2020_m3_roll001  label="tnut_2020_m3_roll002"
  LinkPlacement = pos=(-4.8,-7.5,0.1) rot=(0,0.707107,0.707107;3.14159rad)
  LinkedObject = -> Part__Feature008
  Placement = pos=(-4.8,-7.5,0.1) rot=(0,0.707107,0.707107;3.14159rad)
FEATURE [App::Link] tnut_2020_m3_roll002  label="tnut_2020_m3_roll003"
  LinkPlacement = pos=(-4.8,-24.5,0.1) rot=(0,0.707107,0.707107;3.14159rad)
  LinkedObject = -> Part__Feature008
  Placement = pos=(-4.8,-24.5,0.1) rot=(0,0.707107,0.707107;3.14159rad)
FEATURE [App::FeaturePython] Joint  label="Distance"  # Assembly joint (typed FeaturePython)
  Angle = 0
  AngleMax = 0
  AngleMin = 0
  Detach1 = false
  Detach2 = false
  Distance = 0
  Distance2 = 0
  EnableAngleMax = false
  EnableAngleMin = false
  EnableLengthMax = false
  EnableLengthMin = false
  JointType = 5 (Distance)
  LengthMax = 0
  LengthMin = 0
  Placement1 = pos=(3.55,2.9,0) rot=(0.57735,0.57735,-0.57735;2.0944rad)
  Placement2 = pos=(-9,-3,-80) rot=(0.57735,0.57735,0.57735;4.18879rad)
  Reference1 = -> tnut_2020_m3_roll [Face15,Face15]
  Reference2 = -> HFS5_2020_160 [Face1,Face1]
  Suppressed = false
FEATURE [App::FeaturePython] Joint001  label="Distance001"  # Assembly joint (typed FeaturePython)
  Angle = 0
  AngleMax = 0
  AngleMin = 0
  Detach1 = false
  Detach2 = false
  Distance = 0
  Distance2 = 0
  EnableAngleMax = false
  EnableAngleMin = false
  EnableLengthMax = false
  EnableLengthMin = false
  JointType = 5 (Distance)
  LengthMax = 0
  LengthMin = 0
  Placement1 = pos=(3.2,3.525,0) rot=(0,-1,0;1.5708rad)
  Placement2 = pos=(-8,-4.5,-80) rot=(0.57735,0.57735,0.57735;2.0944rad)
  Reference1 = -> tnut_2020_m3_roll [Face17,Face17]
  Reference2 = -> HFS5_2020_160 [Face60,Vertex1]
  Suppressed = false
FEATURE [App::FeaturePython] Joint002  label="Distance002"  # Assembly joint (typed FeaturePython)
  Angle = 0
  AngleMax = 0
  AngleMin = 0
  Detach1 = false
  Detach2 = false
  Distance = 0
  Distance2 = 0
  EnableAngleMax = false
  EnableAngleMin = false
  EnableLengthMax = false
  EnableLengthMin = false
  JointType = 5 (Distance)
  LengthMax = 0
  LengthMin = 0
  Placement1 = pos=(3.55,2.9,0) rot=(0.57735,0.57735,-0.57735;2.0944rad)
  Placement2 = pos=(-9,-3,-80) rot=(0.57735,0.57735,0.57735;4.18879rad)
  Reference1 = -> tnut_2020_m3_roll002 [Face15,Face15]
  Reference2 = -> HFS5_2020_160 [Face1,Face1]
  Suppressed = false
FEATURE [App::FeaturePython] Joint003  label="Distance003"  # Assembly joint (typed FeaturePython)
  Angle = 0
  AngleMax = 0
  AngleMin = 0
  Detach1 = false
  Detach2 = false
  Distance = 0
  Distance2 = 0
  EnableAngleMax = false
  EnableAngleMin = false
  EnableLengthMax = false
  EnableLengthMin = false
  JointType = 5 (Distance)
  LengthMax = 0
  LengthMin = 0
  Placement1 = pos=(3.2,3.525,0) rot=(0,-1,0;1.5708rad)
  Placement2 = pos=(-8,-4.5,-80) rot=(0.57735,0.57735,0.57735;2.0944rad)
  Reference1 = -> tnut_2020_m3_roll002 [Face17,Face17]
  Reference2 = -> HFS5_2020_160 [Face60,Vertex1]
  Suppressed = false
FEATURE [App::FeaturePython] Joint004  label="Distance004"  # Assembly joint (typed FeaturePython)
  Angle = 0
  AngleMax = 0
  AngleMin = 0
  Detach1 = false
  Detach2 = false
  Distance = 0
  Distance2 = 0
  EnableAngleMax = false
  EnableAngleMin = false
  EnableLengthMax = false
  EnableLengthMin = false
  JointType = 5 (Distance)
  LengthMax = 0
  LengthMin = 0
  Placement1 = pos=(3.55,2.9,-9e-16) rot=(0.57735,0.57735,-0.57735;2.0944rad)
  Placement2 = pos=(-9,-3,-80) rot=(0.57735,0.57735,0.57735;4.18879rad)
  Reference1 = -> tnut_2020_m3_roll001 [Face15,Vertex34]
  Reference2 = -> HFS5_2020_160 [Face1,Vertex2]
  Suppressed = false
FEATURE [App::FeaturePython] Joint005  label="Distance005"  # Assembly joint (typed FeaturePython)
  Angle = 0
  AngleMax = 0
  AngleMin = 0
  Detach1 = false
  Detach2 = false
  Distance = 0
  Distance2 = 0
  EnableAngleMax = false
  EnableAngleMin = false
  EnableLengthMax = false
  EnableLengthMin = false
  JointType = 5 (Distance)
  LengthMax = 0
  LengthMin = 0
  Placement1 = pos=(3.2,3.525,0) rot=(0,-1,0;1.5708rad)
  Placement2 = pos=(-8,-4.5,-80) rot=(0.57735,0.57735,0.57735;2.0944rad)
  Reference1 = -> tnut_2020_m3_roll001 [Face17,Face17]
  Reference2 = -> HFS5_2020_160 [Face60,Vertex1]
  Suppressed = false
FEATURE [App::Link] heater_heatsink_ptc_tswitch  label="heater_heatsink_ptc_tswitch001"
  LinkedObject = -> Body058
FEATURE [App::FeaturePython] GroundedJoint001  # Assembly grounded joint (typed FeaturePython)
  ObjectToGround = -> heater_heatsink_ptc_tswitch
FEATURE [App::Link] ptc_mini_element_v1  label="ptc_mini_element_v002"
  LinkPlacement = pos=(7.5,28.7745,1.85) rot=(0,0,1;4.71239rad)
  LinkedObject = -> Part__Feature004
  Placement = pos=(7.5,28.7745,1.85) rot=(0,0,1;4.71239rad)
FEATURE [App::Link] thermal_switch_ksd9700_v1  label="thermal_switch_ksd9700_v002"
  LinkPlacement = pos=(15.8,9.2,1.2) rot=(0.707107,0.707107,0;3.14159rad)
  LinkedObject = -> Part__Feature005
  Placement = pos=(15.8,9.2,1.2) rot=(0.707107,0.707107,0;3.14159rad)
FEATURE [App::Link] heater_strap_ptc  label="heater_strap_ptc001"
  LinkPlacement = pos=(25,28.5,4.5) rot=(0,0,-1;0.769139rad)
  LinkedObject = -> Body
  Placement = pos=(25,28.5,4.5) rot=(0,0,-1;0.769139rad)
FEATURE [App::Link] heater_strap_tswitch  label="heater_strap_tswitch001"
  LinkPlacement = pos=(25,9,3.2) rot=(0,0,-1;0.79885rad)
  LinkedObject = -> Body049
  Placement = pos=(25,9,3.2) rot=(0,0,-1;0.79885rad)
FEATURE [App::Link] m3x8_bhcs  label="m3x8_bhcs001"
  LinkPlacement = pos=(19.5,14.65,3.96) rot=(0,0,1;1.95848rad)
  LinkedObject = -> Part__Feature003
  Placement = pos=(19.5,14.65,3.96) rot=(0,0,1;1.95848rad)
FEATURE [App::Link] m3x8_bhcs001  label="m3x8_bhcs002"
  LinkPlacement = pos=(30.5,3.35,3.96) rot=(0,0,1;0.938714rad)
  LinkedObject = -> Part__Feature003
  Placement = pos=(30.5,3.35,3.96) rot=(0,0,1;0.938714rad)
FEATURE [App::Link] m3x8_bhcs002  label="m3x8_bhcs003"
  LinkPlacement = pos=(12.5,40.6,5.26) rot=(0,0,1;0.718428rad)
  LinkedObject = -> Part__Feature003
  Placement = pos=(12.5,40.6,5.26) rot=(0,0,1;0.718428rad)
FEATURE [App::Link] m3x8_bhcs003  label="m3x8_bhcs004"
  LinkPlacement = pos=(37.5,16.4,5.26) rot=(0,0,1;1.04084rad)
  LinkedObject = -> Part__Feature003
  Placement = pos=(37.5,16.4,5.26) rot=(0,0,1;1.04084rad)
FEATURE [App::FeaturePython] Joint006  label="Distance006"  # Assembly joint (typed FeaturePython)
  Angle = 0
  AngleMax = 0
  AngleMin = 0
  Detach1 = false
  Detach2 = false
  Distance = 0
  Distance2 = 0
  EnableAngleMax = false
  EnableAngleMin = false
  EnableLengthMax = false
  EnableLengthMin = false
  JointType = 5 (Distance)
  LengthMax = 0
  LengthMin = 0
  Placement1 = pos=(25,28.5,-0.8) rot=(0,0,1;0rad)
  Placement2 = pos=(3.6e-15,17.5,-2.65) rot=(1,0,0;3.14159rad)
  Reference1 = -> heater_heatsink_ptc_tswitch [Face880,Face880]
  Reference2 = -> ptc_mini_element_v1 [Face3,Face3]
  Suppressed = false
FEATURE [App::FeaturePython] Joint009  label="Distance009"  # Assembly joint (typed FeaturePython)
  Angle = 0
  AngleMax = 0
  AngleMin = 0
  Detach1 = false
  Detach2 = false
  Distance = 0
  Distance2 = 0
  EnableAngleMax = false
  EnableAngleMin = false
  EnableLengthMax = false
  EnableLengthMin = false
  JointType = 5 (Distance)
  LengthMax = 0
  LengthMin = 0
  Placement1 = pos=(0,9.9,2) rot=(0,0,-1;3.14159rad)
  Placement2 = pos=(25,9,-0.8) rot=(0,0,1;0rad)
  Reference1 = -> thermal_switch_ksd9700_v1 [Face7,Face7]
  Reference2 = -> heater_heatsink_ptc_tswitch [Face879,Face879]
  Suppressed = false
FEATURE [App::FeaturePython] Joint012  label="Cylindrical"  # Assembly joint (typed FeaturePython)
  Angle = 0
  AngleMax = 0
  AngleMin = 0
  Detach1 = false
  Detach2 = false
  Distance = 0
  Distance2 = 0
  EnableAngleMax = false
  EnableAngleMin = false
  EnableLengthMax = false
  EnableLengthMin = false
  JointType = 2 (Cylindrical)
  LengthMax = 0
  LengthMin = 0
  Placement1 = pos=(9e-16,0,-7.625) rot=(1,0,0;3.14159rad)
  Placement2 = pos=(19.5,14.65,0) rot=(0,0,1;0rad)
  Reference1 = -> m3x8_bhcs [Face1,Edge3]
  Reference2 = -> heater_heatsink_ptc_tswitch [Edge768,Edge768]
  Suppressed = false
FEATURE [App::FeaturePython] Joint013  label="Cylindrical001"  # Assembly joint (typed FeaturePython)
  Angle = 0
  AngleMax = 0
  AngleMin = 0
  Detach1 = false
  Detach2 = false
  Distance = 0
  Distance2 = 0
  EnableAngleMax = false
  EnableAngleMin = false
  EnableLengthMax = false
  EnableLengthMin = false
  JointType = 2 (Cylindrical)
  LengthMax = 0
  LengthMin = 0
  Placement1 = pos=(30.5,3.35,0) rot=(0,0,1;0rad)
  Placement2 = pos=(3.6e-15,0,-7.625) rot=(1,0,0;3.14159rad)
  Reference1 = -> heater_heatsink_ptc_tswitch [Edge769,Edge769]
  Reference2 = -> m3x8_bhcs001 [Face1,Edge3]
  Suppressed = false
FEATURE [App::FeaturePython] Joint014  label="Cylindrical002"  # Assembly joint (typed FeaturePython)
  Angle = 0
  AngleMax = 0
  AngleMin = 0
  Detach1 = false
  Detach2 = false
  Distance = 0
  Distance2 = 0
  EnableAngleMax = false
  EnableAngleMin = false
  EnableLengthMax = false
  EnableLengthMin = false
  JointType = 2 (Cylindrical)
  LengthMax = 0
  LengthMin = 0
  Placement1 = pos=(12.5,40.6,0) rot=(0,0,1;0rad)
  Placement2 = pos=(7.1e-15,-3.6e-15,-7.625) rot=(1,0,0;3.14159rad)
  Reference1 = -> heater_heatsink_ptc_tswitch [Edge777,Edge777]
  Reference2 = -> m3x8_bhcs002 [Face1,Edge3]
  Suppressed = false
FEATURE [App::FeaturePython] Joint015  label="Cylindrical003"  # Assembly joint (typed FeaturePython)
  Angle = 0
  AngleMax = 0
  AngleMin = 0
  Detach1 = false
  Detach2 = false
  Distance = 0
  Distance2 = 0
  EnableAngleMax = false
  EnableAngleMin = false
  EnableLengthMax = false
  EnableLengthMin = false
  JointType = 2 (Cylindrical)
  LengthMax = 0
  LengthMin = 0
  Placement1 = pos=(0,0,-7.625) rot=(1,0,0;3.14159rad)
  Placement2 = pos=(37.5,16.4,0) rot=(0,0,1;0rad)
  Reference1 = -> m3x8_bhcs003 [Face1,Edge3]
  Reference2 = -> heater_heatsink_ptc_tswitch [Edge776,Edge776]
  Suppressed = false
FEATURE [App::FeaturePython] Joint016  label="Cylindrical004"  # Assembly joint (typed FeaturePython)
  Angle = 0
  AngleMax = 0
  AngleMin = 0
  Detach1 = false
  Detach2 = false
  Distance = 0
  Distance2 = 0
  EnableAngleMax = false
  EnableAngleMin = false
  EnableLengthMax = false
  EnableLengthMin = false
  JointType = 2 (Cylindrical)
  LengthMax = 0
  LengthMin = 0
  Placement1 = pos=(19.5,14.65,0) rot=(0,0,1;0rad)
  Placement2 = pos=(-7.88495,0,0.76) rot=(0,0,1;0rad)
  Reference1 = -> heater_heatsink_ptc_tswitch [Edge768,Edge768]
  Reference2 = -> heater_strap_tswitch [Edge18,Edge18]
  Suppressed = false
FEATURE [App::FeaturePython] Joint017  label="Cylindrical005"  # Assembly joint (typed FeaturePython)
  Angle = 0
  AngleMax = 0
  AngleMin = 0
  Detach1 = false
  Detach2 = false
  Distance = 0
  Distance2 = 0
  EnableAngleMax = false
  EnableAngleMin = false
  EnableLengthMax = false
  EnableLengthMin = false
  JointType = 2 (Cylindrical)
  LengthMax = 0
  LengthMin = 0
  Placement1 = pos=(7.88495,0,0.76) rot=(0,0,1;0rad)
  Placement2 = pos=(30.5,3.35,0) rot=(0,0,1;0rad)
  Reference1 = -> heater_strap_tswitch [Edge15,Edge15]
  Reference2 = -> heater_heatsink_ptc_tswitch [Edge769,Edge769]
  Suppressed = false
FEATURE [App::FeaturePython] Joint018  label="Distance012"  # Assembly joint (typed FeaturePython)
  Angle = 0
  AngleMax = 0
  AngleMin = 0
  Detach1 = false
  Detach2 = false
  Distance = 0
  Distance2 = 0
  EnableAngleMax = false
  EnableAngleMin = false
  EnableLengthMax = false
  EnableLengthMin = false
  JointType = 5 (Distance)
  LengthMax = 0
  LengthMin = 0
  Placement2 = pos=(0,9.9,-2) rot=(-1,0,0;3.14159rad)
  Reference1 = -> heater_strap_tswitch [Face7,Face7]
  Reference2 = -> thermal_switch_ksd9700_v1 [Face14,Face14]
  Suppressed = false
FEATURE [App::FeaturePython] Joint019  label="Distance013"  # Assembly joint (typed FeaturePython)
  Angle = 0
  AngleMax = 0
  AngleMin = 0
  Detach1 = false
  Detach2 = false
  Distance = 0
  Distance2 = 0
  EnableAngleMax = false
  EnableAngleMin = false
  EnableLengthMax = false
  EnableLengthMin = false
  JointType = 5 (Distance)
  LengthMax = 0
  LengthMin = 0
  Placement1 = pos=(1.8e-15,-3.6e-15,0.76) rot=(0,0,1;0rad)
  Placement2 = pos=(0,0,0) rot=(1,0,0;3.14159rad)
  Reference1 = -> heater_strap_tswitch [Face8,Face8]
  Reference2 = -> m3x8_bhcs001 [Face3,Face3]
  Suppressed = false
FEATURE [App::FeaturePython] Joint020  label="Distance014"  # Assembly joint (typed FeaturePython)
  Angle = 0
  AngleMax = 0
  AngleMin = 0
  Detach1 = false
  Detach2 = false
  Distance = 0
  Distance2 = 0
  EnableAngleMax = false
  EnableAngleMin = false
  EnableLengthMax = false
  EnableLengthMin = false
  JointType = 5 (Distance)
  LengthMax = 0
  LengthMin = 0
  Placement1 = pos=(1.8e-15,-3.6e-15,0.76) rot=(0,0,1;0rad)
  Placement2 = pos=(-1.8e-15,0,0) rot=(1,0,0;3.14159rad)
  Reference1 = -> heater_strap_tswitch [Face8,Face8]
  Reference2 = -> m3x8_bhcs [Face3,Vertex1]
  Suppressed = false
FEATURE [App::FeaturePython] Joint021  label="Cylindrical006"  # Assembly joint (typed FeaturePython)
  Angle = 0
  AngleMax = 0
  AngleMin = 0
  Detach1 = false
  Detach2 = false
  Distance = 0
  Distance2 = 0
  EnableAngleMax = false
  EnableAngleMin = false
  EnableLengthMax = false
  EnableLengthMin = false
  JointType = 2 (Cylindrical)
  LengthMax = 0
  LengthMin = 0
  Placement1 = pos=(12.5,40.6,0) rot=(0,0,1;0rad)
  Placement2 = pos=(-17.3971,0,0.76) rot=(0,0,1;0rad)
  Reference1 = -> heater_heatsink_ptc_tswitch [Edge777,Edge777]
  Reference2 = -> heater_strap_ptc [Edge18,Edge18]
  Suppressed = false
FEATURE [App::FeaturePython] Joint022  label="Cylindrical007"  # Assembly joint (typed FeaturePython)
  Angle = 0
  AngleMax = 0
  AngleMin = 0
  Detach1 = false
  Detach2 = false
  Distance = 0
  Distance2 = 0
  EnableAngleMax = false
  EnableAngleMin = false
  EnableLengthMax = false
  EnableLengthMin = false
  JointType = 2 (Cylindrical)
  LengthMax = 0
  LengthMin = 0
  Placement1 = pos=(37.5,16.4,0) rot=(0,0,1;0rad)
  Placement2 = pos=(17.3971,-7.1e-15,0.76) rot=(0,0,1;0rad)
  Reference1 = -> heater_heatsink_ptc_tswitch [Edge776,Edge776]
  Reference2 = -> heater_strap_ptc [Edge15,Edge15]
  Suppressed = false
FEATURE [App::FeaturePython] Joint023  label="Distance015"  # Assembly joint (typed FeaturePython)
  Angle = 0
  AngleMax = 0
  AngleMin = 0
  Detach1 = false
  Detach2 = false
  Distance = 0
  Distance2 = 0
  EnableAngleMax = false
  EnableAngleMin = false
  EnableLengthMax = false
  EnableLengthMin = false
  JointType = 5 (Distance)
  LengthMax = 0
  LengthMin = 0
  Placement2 = pos=(3.6e-15,17.5,2.65) rot=(0,0,1;3.14159rad)
  Reference1 = -> heater_strap_ptc [Face7,Face7]
  Reference2 = -> ptc_mini_element_v1 [Face10,Face10]
  Suppressed = false
FEATURE [App::FeaturePython] Joint024  label="Distance016"  # Assembly joint (typed FeaturePython)
  Angle = 0
  AngleMax = 0
  AngleMin = 0
  Detach1 = false
  Detach2 = false
  Distance = 0
  Distance2 = 0
  EnableAngleMax = false
  EnableAngleMin = false
  EnableLengthMax = false
  EnableLengthMin = false
  JointType = 5 (Distance)
  LengthMax = 0
  LengthMin = 0
  Placement1 = pos=(0,0,0.76) rot=(0,0,1;0rad)
  Placement2 = pos=(0,0,0) rot=(1,0,0;3.14159rad)
  Reference1 = -> heater_strap_ptc [Face8,Face8]
  Reference2 = -> m3x8_bhcs003 [Face3,Vertex1]
  Suppressed = false
FEATURE [App::FeaturePython] Joint025  label="Distance017"  # Assembly joint (typed FeaturePython)
  Angle = 0
  AngleMax = 0
  AngleMin = 0
  Detach1 = false
  Detach2 = false
  Distance = 0
  Distance2 = 0
  EnableAngleMax = false
  EnableAngleMin = false
  EnableLengthMax = false
  EnableLengthMin = false
  JointType = 5 (Distance)
  LengthMax = 0
  LengthMin = 0
  Placement1 = pos=(0,0,0.76) rot=(0,0,1;0rad)
  Placement2 = pos=(0,0,0) rot=(1,0,0;3.14159rad)
  Reference1 = -> heater_strap_ptc [Face8,Face8]
  Reference2 = -> m3x8_bhcs002 [Face3,Face3]
  Suppressed = false
FEATURE [App::FeaturePython] Joint026  label="Distance018"  # Assembly joint (typed FeaturePython)
  Angle = 0
  AngleMax = 0
  AngleMin = 0
  Detach1 = false
  Detach2 = false
  Distance = 0
  Distance2 = 0
  EnableAngleMax = false
  EnableAngleMin = false
  EnableLengthMax = false
  EnableLengthMin = false
  JointType = 5 (Distance)
  LengthMax = 0
  LengthMin = 0
  Placement1 = pos=(25,39.15,-0.4) rot=(0,0.707107,0.707107;3.14159rad)
  Placement2 = pos=(-10.3755,17.5,-2.11213) rot=(0.57735,0.57735,0.57735;4.18879rad)
  Reference1 = -> heater_heatsink_ptc_tswitch [Face581,Face581]
  Reference2 = -> ptc_mini_element_v1 [Edge1,Edge1]
  Suppressed = false
FEATURE [App::FeaturePython] Joint027  label="Distance019"  # Assembly joint (typed FeaturePython)
  Angle = 0
  AngleMax = 0
  AngleMin = 0
  Detach1 = false
  Detach2 = false
  Distance = 0.5
  Distance2 = 0
  EnableAngleMax = false
  EnableAngleMin = false
  EnableLengthMax = false
  EnableLengthMin = false
  JointType = 5 (Distance)
  LengthMax = 0
  LengthMin = 0
  Placement1 = pos=(-3.6e-15,35,9e-16) rot=(0.57735,0.57735,0.57735;4.18879rad)
  Placement2 = pos=(43,28.5,-0.4) rot=(0.57735,0.57735,0.57735;2.0944rad)
  Reference1 = -> ptc_mini_element_v1 [Face5,Vertex29]
  Reference2 = -> heater_heatsink_ptc_tswitch [Face583,Face583]
  Suppressed = false
FEATURE [App::FeaturePython] Joint028  label="Distance020"  # Assembly joint (typed FeaturePython)
  Angle = 0
  AngleMax = 0
  AngleMin = 0
  Detach1 = false
  Detach2 = false
  Distance = 0
  Distance2 = 0
  EnableAngleMax = false
  EnableAngleMin = false
  EnableLengthMax = false
  EnableLengthMin = false
  JointType = 5 (Distance)
  LengthMax = 0
  LengthMin = 0
  Placement1 = pos=(25,13.2,-0.4) rot=(0,0.707107,0.707107;3.14159rad)
  Placement2 = pos=(4,9.9,-2e-15) rot=(-0.707107,0,-0.707107;3.14159rad)
  Reference1 = -> heater_heatsink_ptc_tswitch [Face577,Face577]
  Reference2 = -> thermal_switch_ksd9700_v1 [Face26,Vertex39]
  Suppressed = false
FEATURE [App::FeaturePython] Joint029  label="Distance021"  # Assembly joint (typed FeaturePython)
  Angle = 0
  AngleMax = 0
  AngleMin = 0
  Detach1 = false
  Detach2 = false
  Distance = 0.4
  Distance2 = 0
  EnableAngleMax = false
  EnableAngleMin = false
  EnableLengthMax = false
  EnableLengthMin = false
  JointType = 5 (Distance)
  LengthMax = 0
  LengthMin = 0
  Placement1 = pos=(-1.8e-15,20,2e-16) rot=(-0.57735,-0.57735,-0.57735;2.0944rad)
  Placement2 = pos=(36.2,9,-0.4) rot=(0.57735,0.57735,0.57735;2.0944rad)
  Reference1 = -> thermal_switch_ksd9700_v1 [Face10,Face10]
  Reference2 = -> heater_heatsink_ptc_tswitch [Face579,Face579]
  Suppressed = false
FEATURE [Assembly::JointGroup] Joints001
  Group = -> [GroundedJoint001,Joint006,Joint009,Joint012,Joint013,Joint014,Joint015,Joint016,Joint017,Joint018,Joint019,Joint020,Joint021,Joint022,Joint023,Joint024,Joint025,Joint026,Joint027,Joint028,Joint029]
FEATURE [Assembly::AssemblyObject] Assembly001  label="BlockAssembly"
  Group = -> [Joints001,heater_heatsink_ptc_tswitch,GroundedJoint001,ptc_mini_element_v1,thermal_switch_ksd9700_v1,heater_strap_ptc,heater_strap_tswitch,m3x8_bhcs,m3x8_bhcs001,m3x8_bhcs002,m3x8_bhcs003,Joint006,Joint009,Joint012,Joint013,Joint014,Joint015,Joint016,Joint017,Joint018,Joint019,Joint020,Joint021,Joint022,Joint023,Joint024,Joint025,Joint026,Joint027,Joint028,Joint029]
  Origin = -> Origin150
  Placement = pos=(-16,-27,12.6) rot=(0,0,1;3.14159rad)
  Type = Assembly
FEATURE [App::Link] heater_bracket  label="heater_bracket001"
  LinkPlacement = pos=(-10,-27,12.6) rot=(0,0,1;0rad)
  LinkedObject = -> Body048
  Placement = pos=(-10,-27,12.6) rot=(0,0,1;0rad)
FEATURE [App::Link] m3x6_bhcs  label="m3x6_bhcs001"
  LinkPlacement = pos=(-11.5,-5,0.1) rot=(-0.6954,0.181212,0.6954;3.50013rad)
  LinkedObject = -> Part__Feature002
  Placement = pos=(-11.5,-5,0.1) rot=(-0.6954,0.181212,0.6954;3.50013rad)
FEATURE [App::Link] m3x6_bhcs001  label="m3x6_bhcs002"
  LinkPlacement = pos=(-11.5,-22,0.1) rot=(0.276397,-0.92044,-0.276397;1.6536rad)
  LinkedObject = -> Part__Feature002
  Placement = pos=(-11.5,-22,0.1) rot=(0.276397,-0.92044,-0.276397;1.6536rad)
FEATURE [App::FeaturePython] Joint031  label="Cylindrical009"  # Assembly joint (typed FeaturePython)
  Angle = 0
  AngleMax = 0
  AngleMin = 0
  Detach1 = false
  Detach2 = false
  Distance = 0
  Distance2 = 0
  EnableAngleMax = false
  EnableAngleMin = false
  EnableLengthMax = false
  EnableLengthMin = false
  JointType = 2 (Cylindrical)
  LengthMax = 0
  LengthMin = 0
  Placement1 = pos=(1.95,0,2.5) rot=(0,1,0;1.5708rad)
  Placement2 = pos=(0,0,-2.8125) rot=(0,0,1;0rad)
  Reference1 = -> tnut_2020_m3_roll002 [Face25,Face25]
  Reference2 = -> m3x6_bhcs001 [Face3,Face3]
  Suppressed = false
FEATURE [App::FeaturePython] Joint032  label="Cylindrical010"  # Assembly joint (typed FeaturePython)
  Angle = 0
  AngleMax = 0
  AngleMin = 0
  Detach1 = false
  Detach2 = false
  Distance = 0
  Distance2 = 0
  EnableAngleMax = false
  EnableAngleMin = false
  EnableLengthMax = false
  EnableLengthMin = false
  JointType = 2 (Cylindrical)
  LengthMax = 0
  LengthMin = 0
  Placement1 = pos=(1.95,-1e-16,2.5) rot=(0,1,0;1.5708rad)
  Placement2 = pos=(0,-9e-16,-5.625) rot=(0,0,1;0rad)
  Reference1 = -> tnut_2020_m3_roll001 [Face25,Face25]
  Reference2 = -> m3x6_bhcs [Face3,Edge3]
  Suppressed = false
FEATURE [App::FeaturePython] Joint033  label="Distance022"  # Assembly joint (typed FeaturePython)
  Angle = 0
  AngleMax = 0
  AngleMin = 0
  Detach1 = false
  Detach2 = false
  Distance = 0
  Distance2 = 0
  EnableAngleMax = false
  EnableAngleMin = false
  EnableLengthMax = false
  EnableLengthMin = false
  JointType = 5 (Distance)
  LengthMax = 0
  LengthMin = 0
  Placement1 = pos=(-10,-6,-80) rot=(0,-1,0;1.5708rad)
  Placement2 = pos=(1.8e-15,12.5749,-12.1263) rot=(0.707107,0,0.707107;3.14159rad)
  Reference1 = -> HFS5_2020_160 [Face2,Vertex2]
  Reference2 = -> heater_bracket [Face19,Face19]
  Suppressed = false
FEATURE [App::FeaturePython] Joint034  label="Cylindrical011"  # Assembly joint (typed FeaturePython)
  Angle = 0
  AngleMax = 0
  AngleMin = 0
  Detach1 = false
  Detach2 = false
  Distance = 0
  Distance2 = 0
  EnableAngleMax = false
  EnableAngleMin = false
  EnableLengthMax = false
  EnableLengthMin = false
  JointType = 2 (Cylindrical)
  LengthMax = 0
  LengthMin = 0
  Placement1 = pos=(1.95,0,2.5) rot=(0,-1,0;4.71239rad)
  Placement2 = pos=(-0.75,22,-12.5) rot=(0.57735,0.57735,0.57735;2.0944rad)
  Reference1 = -> tnut_2020_m3_roll001 [Face25,Face25]
  Reference2 = -> heater_bracket [Face29,Face29]
  Suppressed = false
FEATURE [App::FeaturePython] Joint035  label="Cylindrical012"  # Assembly joint (typed FeaturePython)
  Angle = 0
  AngleMax = 0
  AngleMin = 0
  Detach1 = false
  Detach2 = false
  Distance = 0
  Distance2 = 0
  EnableAngleMax = false
  EnableAngleMin = false
  EnableLengthMax = false
  EnableLengthMin = false
  JointType = 2 (Cylindrical)
  LengthMax = 0
  LengthMin = 0
  Placement1 = pos=(1.95,0,2.5) rot=(0,-1,0;4.71239rad)
  Placement2 = pos=(-0.75,5,-12.5) rot=(0.57735,0.57735,0.57735;2.0944rad)
  Reference1 = -> tnut_2020_m3_roll002 [Face25,Face25]
  Reference2 = -> heater_bracket [Face30,Face30]
  Suppressed = false
FEATURE [App::FeaturePython] Joint036  label="Distance023"  # Assembly joint (typed FeaturePython)
  Angle = 0
  AngleMax = 0
  AngleMin = 0
  Detach1 = false
  Detach2 = false
  Distance = 0
  Distance2 = 0
  EnableAngleMax = false
  EnableAngleMin = false
  EnableLengthMax = false
  EnableLengthMin = false
  JointType = 5 (Distance)
  LengthMax = 0
  LengthMin = 0
  Placement1 = pos=(-1.5,12.5749,-12.1263) rot=(-0.707107,0,0.707107;3.14159rad)
  Placement2 = pos=(0,0,0) rot=(1,0,0;3.14159rad)
  Reference1 = -> heater_bracket [Face21,Edge7]
  Reference2 = -> m3x6_bhcs001 [Face4,Face4]
  Suppressed = false
FEATURE [App::FeaturePython] Joint037  label="Distance024"  # Assembly joint (typed FeaturePython)
  Angle = 0
  AngleMax = 0
  AngleMin = 0
  Detach1 = false
  Detach2 = false
  Distance = 0
  Distance2 = 0
  EnableAngleMax = false
  EnableAngleMin = false
  EnableLengthMax = false
  EnableLengthMin = false
  JointType = 5 (Distance)
  LengthMax = 0
  LengthMin = 0
  Placement1 = pos=(-1.5,12.5749,-12.1263) rot=(-0.707107,0,0.707107;3.14159rad)
  Placement2 = pos=(4e-16,9e-16,0) rot=(1,0,0;3.14159rad)
  Reference1 = -> heater_bracket [Face21,Edge10]
  Reference2 = -> m3x6_bhcs [Face4,Face4]
  Suppressed = false
FEATURE [App::FeaturePython] Joint038  label="Distance025"  # Assembly joint (typed FeaturePython)
  Angle = 0
  AngleMax = 0
  AngleMin = 0
  Detach1 = false
  Detach2 = false
  Distance = 0
  Distance2 = 0
  EnableAngleMax = false
  EnableAngleMin = false
  EnableLengthMax = false
  EnableLengthMin = false
  JointType = 5 (Distance)
  LengthMax = 0
  LengthMin = 0
  Placement1 = pos=(-27.5521,0.758969,0) rot=(0,0,1;0rad)
  Placement2 = pos=(25,25.3903,0) rot=(0,0,1;0rad)
  Reference1 = -> heater_bracket [Face18,Vertex23]
  Reference2 = -> Assembly001 [heater_heatsink_ptc_tswitch.Face31,heater_heatsink_ptc_tswitch.Vertex708]
  Suppressed = false
FEATURE [App::FeaturePython] Joint045  label="Cylindrical017"  # Assembly joint (typed FeaturePython)
  Angle = 0
  AngleMax = 0
  AngleMin = 0
  Detach1 = false
  Detach2 = false
  Distance = 0
  Distance2 = 0
  EnableAngleMax = false
  EnableAngleMin = false
  EnableLengthMax = false
  EnableLengthMin = false
  JointType = 2 (Cylindrical)
  LengthMax = 0
  LengthMin = 0
  Placement1 = pos=(-10,-4,0.75) rot=(0,0,1;0rad)
  Placement2 = pos=(4,4,-1.71906) rot=(0,0,1;0rad)
  Reference1 = -> heater_bracket [Face17,Face17]
  Reference2 = -> Assembly001 [heater_heatsink_ptc_tswitch.Face101,heater_heatsink_ptc_tswitch.Face101]
  Suppressed = false
FEATURE [App::FeaturePython] Joint047  label="Cylindrical018"  # Assembly joint (typed FeaturePython)
  Angle = 0
  AngleMax = 0
  AngleMin = 0
  Detach1 = false
  Detach2 = false
  Distance = 0
  Distance2 = 0
  EnableAngleMax = false
  EnableAngleMin = false
  EnableLengthMax = false
  EnableLengthMin = false
  JointType = 2 (Cylindrical)
  LengthMax = 0
  LengthMin = 0
  Placement1 = pos=(46,4,-1.72006) rot=(0,0,1;0rad)
  Placement2 = pos=(-52,-4,0.75) rot=(0,0,1;0rad)
  Reference1 = -> Assembly001 [heater_heatsink_ptc_tswitch.Face112,heater_heatsink_ptc_tswitch.Face112]
  Reference2 = -> heater_bracket [Face16,Face16]
  Suppressed = false
FEATURE [App::Link] m3x4_bhcs  label="m3x4_bhcs001"
  LinkPlacement = pos=(-62,-31,14.1) rot=(0,0,1;3.87785rad)
  LinkedObject = -> Part__Feature001
  Placement = pos=(-62,-31,14.1) rot=(0,0,1;3.87785rad)
FEATURE [App::Link] m3x4_bhcs001  label="m3x4_bhcs002"
  LinkPlacement = pos=(-20,-31,14.1) rot=(0,0,1;2.35139rad)
  LinkedObject = -> Part__Feature001
  Placement = pos=(-20,-31,14.1) rot=(0,0,1;2.35139rad)
FEATURE [App::FeaturePython] Joint048  label="Cylindrical019"  # Assembly joint (typed FeaturePython)
  Angle = 0
  AngleMax = 0
  AngleMin = 0
  Detach1 = false
  Detach2 = false
  Distance = 0
  Distance2 = 0
  EnableAngleMax = false
  EnableAngleMin = false
  EnableLengthMax = false
  EnableLengthMin = false
  JointType = 2 (Cylindrical)
  LengthMax = 0
  LengthMin = 0
  Placement1 = pos=(4,4,-1.71906) rot=(0,0,1;0rad)
  Placement2 = pos=(-1.8e-15,0,-3.625) rot=(0,0,1;0rad)
  Reference1 = -> Assembly001 [heater_heatsink_ptc_tswitch.Face101,heater_heatsink_ptc_tswitch.Face101]
  Reference2 = -> m3x4_bhcs001 [Face3,Edge3]
  Suppressed = false
FEATURE [App::FeaturePython] Joint049  label="Cylindrical020"  # Assembly joint (typed FeaturePython)
  Angle = 0
  AngleMax = 0
  AngleMin = 0
  Detach1 = false
  Detach2 = false
  Distance = 0
  Distance2 = 0
  EnableAngleMax = false
  EnableAngleMin = false
  EnableLengthMax = false
  EnableLengthMin = false
  JointType = 2 (Cylindrical)
  LengthMax = 0
  LengthMin = 0
  Placement1 = pos=(0,0,-1.8125) rot=(0,0,1;0rad)
  Placement2 = pos=(46,4,-1.72006) rot=(0,0,1;0rad)
  Reference1 = -> m3x4_bhcs [Face3,Face3]
  Reference2 = -> Assembly001 [heater_heatsink_ptc_tswitch.Face112,heater_heatsink_ptc_tswitch.Face112]
  Suppressed = false
FEATURE [App::FeaturePython] Joint050  label="Distance026"  # Assembly joint (typed FeaturePython)
  Angle = 0
  AngleMax = 0
  AngleMin = 0
  Detach1 = false
  Detach2 = false
  Distance = 0
  Distance2 = 0
  EnableAngleMax = false
  EnableAngleMin = false
  EnableLengthMax = false
  EnableLengthMin = false
  JointType = 5 (Distance)
  LengthMax = 0
  LengthMin = 0
  Placement1 = pos=(-27.5521,0.758969,1.5) rot=(0,0,1;0rad)
  Placement2 = pos=(0,0,0) rot=(1,0,0;3.14159rad)
  Reference1 = -> heater_bracket [Face1,Vertex7]
  Reference2 = -> m3x4_bhcs001 [Face4,Face4]
  Suppressed = false
FEATURE [App::FeaturePython] Joint051  label="Distance027"  # Assembly joint (typed FeaturePython)
  Angle = 0
  AngleMax = 0
  AngleMin = 0
  Detach1 = false
  Detach2 = false
  Distance = 0
  Distance2 = 0
  EnableAngleMax = false
  EnableAngleMin = false
  EnableLengthMax = false
  EnableLengthMin = false
  JointType = 5 (Distance)
  LengthMax = 0
  LengthMin = 0
  Placement1 = pos=(-27.5521,0.758969,1.5) rot=(0,0,1;0rad)
  Placement2 = pos=(0,0,0) rot=(1,0,0;3.14159rad)
  Reference1 = -> heater_bracket [Face1,Vertex3]
  Reference2 = -> m3x4_bhcs [Face4,Face4]
  Suppressed = false
FEATURE [App::Link] heater_fan_duct  label="heater_fan_duct001"
  LinkedObject = -> Body050
FEATURE [App::FeaturePython] GroundedJoint002  # Assembly grounded joint (typed FeaturePython)
  ObjectToGround = -> heater_fan_duct
FEATURE [App::Link] heater_fan_screw_spacer  label="heater_fan_screw_spacer001"
  LinkPlacement = pos=(24,-66.1595,0) rot=(0,0,1;3.74142rad)
  LinkedObject = -> Body051
  Placement = pos=(24,-66.1595,0) rot=(0,0,1;3.74142rad)
FEATURE [App::Link] heater_fan_screw_spacer001  label="heater_fan_screw_spacer002"
  LinkPlacement = pos=(-24,-35.4187,0) rot=(0,0,-1;0.536837rad)
  LinkedObject = -> Body051
  Placement = pos=(-24,-35.4187,0) rot=(0,0,-1;0.536837rad)
FEATURE [App::Link] heatset_m3_short_cnck  label="heatset_m3_short_cnck001"
  LinkPlacement = pos=(24,-66.1595,-3) rot=(0,0,1;1.16559rad)
  LinkedObject = -> Part__Feature
  Placement = pos=(24,-66.1595,-3) rot=(0,0,1;1.16559rad)
FEATURE [App::Link] heatset_m3_short_cnck001  label="heatset_m3_short_cnck002"
  LinkPlacement = pos=(-24,-35.4187,-3) rot=(0,0,1;4.44919rad)
  LinkedObject = -> Part__Feature
  Placement = pos=(-24,-35.4187,-3) rot=(0,0,1;4.44919rad)
FEATURE [App::Link] fan_radial_50x15  label="fan_radial_50x016"
  LinkPlacement = pos=(66.1204,-20.0178,107.059) rot=(0,0,1;3.29333rad)
  LinkedObject = -> Part__Feature006
  Placement = pos=(66.1204,-20.0178,107.059) rot=(0,0,1;3.29333rad)
FEATURE [App::Link] m3x18_bhcs  label="m3x18_bhcs001"
  LinkPlacement = pos=(-24,-35.4187,15) rot=(0,0,-1;0.213613rad)
  LinkedObject = -> Part__Feature007
  Placement = pos=(-24,-35.4187,15) rot=(0,0,-1;0.213613rad)
FEATURE [App::Link] m3x18_bhcs001  label="m3x18_bhcs002"
  LinkPlacement = pos=(24,-66.1595,15) rot=(0,0,1;3.72009rad)
  LinkedObject = -> Part__Feature007
  Placement = pos=(24,-66.1595,15) rot=(0,0,1;3.72009rad)
FEATURE [App::FeaturePython] Joint052  label="Cylindrical021"  # Assembly joint (typed FeaturePython)
  Angle = 0
  AngleMax = 0
  AngleMin = 0
  Detach1 = false
  Detach2 = false
  Distance = 0
  Distance2 = 0
  EnableAngleMax = false
  EnableAngleMin = false
  EnableLengthMax = false
  EnableLengthMin = false
  JointType = 2 (Cylindrical)
  LengthMax = 0
  LengthMin = 0
  Placement1 = pos=(-24,-35.4187,-1.5) rot=(0,0,1;0rad)
  Placement2 = pos=(0,0,7) rot=(0,0,1;0rad)
  Reference1 = -> heater_fan_duct [Face50,Face50]
  Reference2 = -> heater_fan_screw_spacer001 [Face1,Face1]
  Suppressed = false
FEATURE [App::FeaturePython] Joint053  label="Cylindrical022"  # Assembly joint (typed FeaturePython)
  Angle = 0
  AngleMax = 0
  AngleMin = 0
  Detach1 = false
  Detach2 = false
  Distance = 0
  Distance2 = 0
  EnableAngleMax = false
  EnableAngleMin = false
  EnableLengthMax = false
  EnableLengthMin = false
  JointType = 2 (Cylindrical)
  LengthMax = 0
  LengthMin = 0
  Placement1 = pos=(24,-66.1595,-1.5) rot=(0,0,1;0rad)
  Placement2 = pos=(0,0,14) rot=(0,0,1;0rad)
  Reference1 = -> heater_fan_duct [Face49,Face49]
  Reference2 = -> heater_fan_screw_spacer [Face1,Edge3]
  Suppressed = false
FEATURE [App::FeaturePython] Joint054  label="Cylindrical023"  # Assembly joint (typed FeaturePython)
  Angle = 0
  AngleMax = 0
  AngleMin = 0
  Detach1 = false
  Detach2 = false
  Distance = 0
  Distance2 = 0
  EnableAngleMax = false
  EnableAngleMin = false
  EnableLengthMax = false
  EnableLengthMin = false
  JointType = 2 (Cylindrical)
  LengthMax = 0
  LengthMin = 0
  Placement1 = pos=(0,0,-8.8125) rot=(1,0,0;3.14159rad)
  Placement2 = pos=(-24,-35.4187,-1.5) rot=(0,0,1;0rad)
  Reference1 = -> m3x18_bhcs [Face1,Face1]
  Reference2 = -> heater_fan_duct [Face50,Face50]
  Suppressed = false
FEATURE [App::FeaturePython] Joint055  label="Cylindrical024"  # Assembly joint (typed FeaturePython)
  Angle = 0
  AngleMax = 0
  AngleMin = 0
  Detach1 = false
  Detach2 = false
  Distance = 0
  Distance2 = 0
  EnableAngleMax = false
  EnableAngleMin = false
  EnableLengthMax = false
  EnableLengthMin = false
  JointType = 2 (Cylindrical)
  LengthMax = 0
  LengthMin = 0
  Placement1 = pos=(24,-66.1595,-1.5) rot=(0,0,1;0rad)
  Placement2 = pos=(0,0,-8.8125) rot=(1,0,0;3.14159rad)
  Reference1 = -> heater_fan_duct [Face49,Face49]
  Reference2 = -> m3x18_bhcs001 [Face1,Face1]
  Suppressed = false
FEATURE [App::FeaturePython] Joint056  label="Cylindrical025"  # Assembly joint (typed FeaturePython)
  Angle = 0
  AngleMax = 0
  AngleMin = 0
  Detach1 = false
  Detach2 = false
  Distance = 0
  Distance2 = 0
  EnableAngleMax = false
  EnableAngleMin = false
  EnableLengthMax = false
  EnableLengthMin = false
  JointType = 2 (Cylindrical)
  LengthMax = 0
  LengthMin = 0
  Placement1 = pos=(-24,-35.4187,-1.5) rot=(0,0,1;0rad)
  Placement2 = pos=(0,0,0.4) rot=(0,0,1;0rad)
  Reference1 = -> heater_fan_duct [Face50,Face50]
  Reference2 = -> heatset_m3_short_cnck001 [Face118,Face118]
  Suppressed = false
FEATURE [App::FeaturePython] Joint057  label="Cylindrical026"  # Assembly joint (typed FeaturePython)
  Angle = 0
  AngleMax = 0
  AngleMin = 0
  Detach1 = false
  Detach2 = false
  Distance = 0
  Distance2 = 0
  EnableAngleMax = false
  EnableAngleMin = false
  EnableLengthMax = false
  EnableLengthMin = false
  JointType = 2 (Cylindrical)
  LengthMax = 0
  LengthMin = 0
  Placement1 = pos=(24,-66.1595,-1.5) rot=(0,0,1;0rad)
  Placement2 = pos=(0,0,0.4) rot=(0,0,1;0rad)
  Reference1 = -> heater_fan_duct [Face49,Face49]
  Reference2 = -> heatset_m3_short_cnck [Face118,Face118]
  Suppressed = false
FEATURE [App::FeaturePython] Joint058  label="Cylindrical027"  # Assembly joint (typed FeaturePython)
  Angle = 0
  AngleMax = 0
  AngleMin = 0
  Detach1 = false
  Detach2 = false
  Distance = 0
  Distance2 = 0
  EnableAngleMax = false
  EnableAngleMin = false
  EnableLengthMax = false
  EnableLengthMin = false
  JointType = 2 (Cylindrical)
  LengthMax = 0
  LengthMin = 0
  Placement1 = pos=(-24,-35.4187,-1.5) rot=(0,0,1;0rad)
  Placement2 = pos=(91.4129,1.60199,-92.0592) rot=(0,0,-1;4.71239rad)
  Reference1 = -> heater_fan_duct [Face50,Face50]
  Reference2 = -> fan_radial_50x15 [Face284,Edge2]
  Suppressed = false
FEATURE [App::FeaturePython] Joint059  label="Distance028"  # Assembly joint (typed FeaturePython)
  Angle = 0
  AngleMax = 0
  AngleMin = 0
  Detach1 = false
  Detach2 = false
  Distance = 0
  Distance2 = 0
  EnableAngleMax = false
  EnableAngleMin = false
  EnableLengthMax = false
  EnableLengthMin = false
  JointType = 5 (Distance)
  LengthMax = 0
  LengthMin = 0
  Placement1 = pos=(0.805891,-42.8048,0) rot=(0,0,1;0rad)
  Placement2 = pos=(0,0,3) rot=(0,0,1;0rad)
  Reference1 = -> heater_fan_duct [Face12,Vertex67]
  Reference2 = -> heatset_m3_short_cnck001 [Face64,Vertex133]
  Suppressed = false
FEATURE [App::FeaturePython] Joint060  label="Distance029"  # Assembly joint (typed FeaturePython)
  Angle = 0
  AngleMax = 0
  AngleMin = 0
  Detach1 = false
  Detach2 = false
  Distance = 0
  Distance2 = 0
  EnableAngleMax = false
  EnableAngleMin = false
  EnableLengthMax = false
  EnableLengthMin = false
  JointType = 5 (Distance)
  LengthMax = 0
  LengthMin = 0
  Placement1 = pos=(0.805891,-42.8048,0) rot=(0,0,1;0rad)
  Placement2 = pos=(0,0,3) rot=(0,0,1;0rad)
  Reference1 = -> heater_fan_duct [Face12,Edge14]
  Reference2 = -> heatset_m3_short_cnck [Face64,Vertex170]
  Suppressed = false
FEATURE [App::FeaturePython] Joint061  label="Distance030"  # Assembly joint (typed FeaturePython)
  Angle = 0
  AngleMax = 0
  AngleMin = 0
  Detach1 = false
  Detach2 = false
  Distance = 0
  Distance2 = 0
  EnableAngleMax = false
  EnableAngleMin = false
  EnableLengthMax = false
  EnableLengthMin = false
  JointType = 5 (Distance)
  LengthMax = 0
  LengthMin = 0
  Placement1 = pos=(0.805891,-42.8048,0) rot=(0,0,1;0rad)
  Reference1 = -> heater_fan_duct [Face12,Face12]
  Reference2 = -> heater_fan_screw_spacer001 [Face3,Face3]
  Suppressed = false
FEATURE [App::FeaturePython] Joint062  label="Distance031"  # Assembly joint (typed FeaturePython)
  Angle = 0
  AngleMax = 0
  AngleMin = 0
  Detach1 = false
  Detach2 = false
  Distance = 0
  Distance2 = 0
  EnableAngleMax = false
  EnableAngleMin = false
  EnableLengthMax = false
  EnableLengthMin = false
  JointType = 5 (Distance)
  LengthMax = 0
  LengthMin = 0
  Placement1 = pos=(0.805891,-42.8048,0) rot=(0,0,1;0rad)
  Reference1 = -> heater_fan_duct [Face12,Edge14]
  Reference2 = -> heater_fan_screw_spacer [Face3,Vertex3]
  Suppressed = false
FEATURE [App::FeaturePython] Joint063  label="Distance032"  # Assembly joint (typed FeaturePython)
  Angle = 0
  AngleMax = 0
  AngleMin = 0
  Detach1 = false
  Detach2 = false
  Distance = 0
  Distance2 = 0
  EnableAngleMax = false
  EnableAngleMin = false
  EnableLengthMax = false
  EnableLengthMin = false
  JointType = 5 (Distance)
  LengthMax = 0
  LengthMin = 0
  Placement1 = pos=(0.805891,-42.8048,0) rot=(0,0,1;0rad)
  Placement2 = pos=(67.1518,16.8528,-107.059) rot=(0,0,-1;4.71239rad)
  Reference1 = -> heater_fan_duct [Face12,Face12]
  Reference2 = -> fan_radial_50x15 [Face8,Edge4]
  Suppressed = false
FEATURE [App::FeaturePython] Joint064  label="Distance033"  # Assembly joint (typed FeaturePython)
  Angle = 0
  AngleMax = 0
  AngleMin = 0
  Detach1 = false
  Detach2 = false
  Distance = 0.3
  Distance2 = 0
  EnableAngleMax = false
  EnableAngleMin = false
  EnableLengthMax = false
  EnableLengthMin = false
  JointType = 5 (Distance)
  LengthMax = 0
  LengthMin = 0
  Placement1 = pos=(43.8629,-3.89801,-99.5592) rot=(-0.57735,0.57735,-0.57735;4.18879rad)
  Placement2 = pos=(22.3278,-22.4673,15.2) rot=(0,0,1;0rad)
  Reference1 = -> fan_radial_50x15 [Face95,Face95]
  Reference2 = -> heater_fan_duct [Vertex128,Vertex128]
  Suppressed = false
FEATURE [App::FeaturePython] Joint065  label="Distance034"  # Assembly joint (typed FeaturePython)
  Angle = 0
  AngleMax = 0
  AngleMin = 0
  Detach1 = false
  Detach2 = false
  Distance = 0
  Distance2 = 0
  EnableAngleMax = false
  EnableAngleMin = false
  EnableLengthMax = false
  EnableLengthMin = false
  JointType = 5 (Distance)
  LengthMax = 0
  LengthMin = 0
  Placement1 = pos=(66.7641,18.7603,-92.0592) rot=(0,0,-1;4.71239rad)
  Placement2 = pos=(0,0,0) rot=(1,0,0;3.14159rad)
  Reference1 = -> fan_radial_50x15 [Face267,Vertex501]
  Reference2 = -> m3x18_bhcs001 [Face3,Vertex1]
  Suppressed = false
FEATURE [App::FeaturePython] Joint066  label="Distance035"  # Assembly joint (typed FeaturePython)
  Angle = 0
  AngleMax = 0
  AngleMin = 0
  Detach1 = false
  Detach2 = false
  Distance = 0
  Distance2 = 0
  EnableAngleMax = false
  EnableAngleMin = false
  EnableLengthMax = false
  EnableLengthMin = false
  JointType = 5 (Distance)
  LengthMax = 0
  LengthMin = 0
  Placement1 = pos=(66.7641,18.7603,-92.0592) rot=(0,0,-1;4.71239rad)
  Placement2 = pos=(0,0,0) rot=(1,0,0;3.14159rad)
  Reference1 = -> fan_radial_50x15 [Face267,Vertex478]
  Reference2 = -> m3x18_bhcs [Face3,Face3]
  Suppressed = false
FEATURE [Assembly::JointGroup] Joints002
  Group = -> [GroundedJoint002,Joint052,Joint053,Joint054,Joint055,Joint056,Joint057,Joint058,Joint059,Joint060,Joint061,Joint062,Joint063,Joint064,Joint065,Joint066]
FEATURE [Assembly::AssemblyObject] Assembly002  label="FanAssembly"
  Group = -> [Joints002,heater_fan_duct,GroundedJoint002,heater_fan_screw_spacer,heater_fan_screw_spacer001,heatset_m3_short_cnck,heatset_m3_short_cnck001,fan_radial_50x15,m3x18_bhcs,m3x18_bhcs001,Joint052,Joint053,Joint054,Joint055,Joint056,Joint057,Joint058,Joint059,Joint060,Joint061,Joint062,Joint063,Joint064,Joint065,Joint066]
  Origin = -> Origin151
  Placement = pos=(-41,-78,-5.9) rot=(0,0,1;0rad)
  Type = Assembly
FEATURE [App::FeaturePython] Joint067  label="Parallel"  # Assembly joint (typed FeaturePython)
  Angle = 0
  AngleMax = 0
  AngleMin = 0
  Detach1 = false
  Detach2 = false
  Distance = 0
  Distance2 = 0
  EnableAngleMax = false
  EnableAngleMin = false
  EnableLengthMax = false
  EnableLengthMin = false
  JointType = 6 (Parallel)
  LengthMax = 0
  LengthMin = 0
  Placement1 = pos=(29.3398,-41.1067,13) rot=(0,0,1;0rad)
  Placement2 = pos=(-8,-3,-160) rot=(0.57735,0.57735,0.57735;4.18879rad)
  Reference1 = -> Assembly002 [heater_fan_duct.Face73,heater_fan_duct.Face73]
  Reference2 = -> HFS5_2020_160 [Face1,Vertex3]
  Suppressed = false
FEATURE [App::FeaturePython] Joint068  label="Distance036"  # Assembly joint (typed FeaturePython)
  Angle = 0
  AngleMax = 0
  AngleMin = 0
  Detach1 = false
  Detach2 = false
  Distance = 0
  Distance2 = 0
  EnableAngleMax = false
  EnableAngleMin = false
  EnableLengthMax = false
  EnableLengthMin = false
  JointType = 5 (Distance)
  LengthMax = 0
  LengthMin = 0
  Placement1 = pos=(31,-38.8769,3.69571) rot=(0.707107,0,0.707107;3.14159rad)
  Placement2 = pos=(-10,-6,-80) rot=(0,-1,0;1.5708rad)
  Reference1 = -> Assembly002 [heater_fan_duct.Face72,heater_fan_duct.Edge9]
  Reference2 = -> HFS5_2020_160 [Face2,Vertex4]
  Suppressed = false
FEATURE [App::Link] m3x8_bhcs004  label="m3x8_bhcs005"
  LinkPlacement = pos=(-13,-106,0.1) rot=(0.530986,-0.660385,-0.530986;1.97431rad)
  LinkedObject = -> Part__Feature003
  Placement = pos=(-13,-106,0.1) rot=(0.530986,-0.660385,-0.530986;1.97431rad)
FEATURE [App::FeaturePython] Joint069  label="Cylindrical028"  # Assembly joint (typed FeaturePython)
  Angle = 0
  AngleMax = 0
  AngleMin = 0
  Detach1 = false
  Detach2 = false
  Distance = 0
  Distance2 = 0
  EnableAngleMax = false
  EnableAngleMin = false
  EnableLengthMax = false
  EnableLengthMin = false
  JointType = 2 (Cylindrical)
  LengthMax = 0
  LengthMin = 0
  Placement1 = pos=(3.6295,0,2.5) rot=(0,-1,0;4.71239rad)
  Placement2 = pos=(0,-3.6e-15,-3.8125) rot=(1,0,0;3.14159rad)
  Reference1 = -> tnut_2020_m3_roll [Face25,Edge1]
  Reference2 = -> m3x8_bhcs004 [Face1,Face1]
  Suppressed = false
FEATURE [App::FeaturePython] Joint070  label="Cylindrical029"  # Assembly joint (typed FeaturePython)
  Angle = 0
  AngleMax = 0
  AngleMin = 0
  Detach1 = false
  Detach2 = false
  Distance = 0
  Distance2 = 0
  EnableAngleMax = false
  EnableAngleMin = false
  EnableLengthMax = false
  EnableLengthMin = false
  JointType = 2 (Cylindrical)
  LengthMax = 0
  LengthMin = 0
  Placement1 = pos=(28,-28,6) rot=(0.57735,0.57735,0.57735;2.0944rad)
  Placement2 = pos=(3.6295,-1e-16,2.5) rot=(0,-1,0;4.71239rad)
  Reference1 = -> Assembly002 [heater_fan_duct.Face76,heater_fan_duct.Edge1]
  Reference2 = -> tnut_2020_m3_roll [Face25,Edge1]
  Suppressed = false
FEATURE [App::FeaturePython] Joint071  label="Distance037"  # Assembly joint (typed FeaturePython)
  Angle = 0
  AngleMax = 0
  AngleMin = 0
  Detach1 = false
  Detach2 = false
  Distance = 0
  Distance2 = 0
  EnableAngleMax = false
  EnableAngleMin = false
  EnableLengthMax = false
  EnableLengthMin = false
  JointType = 5 (Distance)
  LengthMax = 0
  LengthMin = 0
  Placement1 = pos=(28,-48.854,6.54178) rot=(0,-1,0;1.5708rad)
  Placement2 = pos=(0,0,0) rot=(1,0,0;3.14159rad)
  Reference1 = -> Assembly002 [heater_fan_duct.Face39,heater_fan_duct.Edge11]
  Reference2 = -> m3x8_bhcs004 [Face3,Face3]
  Suppressed = false
FEATURE [App::FeaturePython] Joint072  label="Distance038"  # Assembly joint (typed FeaturePython)
  Angle = 0
  AngleMax = 0
  AngleMin = 0
  Detach1 = false
  Detach2 = false
  Distance = 1
  Distance2 = 0
  EnableAngleMax = false
  EnableAngleMin = false
  EnableLengthMax = false
  EnableLengthMin = false
  JointType = 5 (Distance)
  LengthMax = 0
  LengthMin = 0
  Placement1 = pos=(3.1e-15,3e-16,6.8946) rot=(0.57735,0.57735,0.57735;4.18879rad)
  Placement2 = pos=(25.0032,50,-8.34846) rot=(0,0.707107,0.707107;3.14159rad)
  Reference1 = -> Assembly002 [heater_fan_duct.Face46,heater_fan_duct.Vertex138]
  Reference2 = -> Assembly001 [heater_heatsink_ptc_tswitch.Face30,heater_heatsink_ptc_tswitch.Vertex208]
  Suppressed = false
FEATURE [App::FeaturePython] Joint073  label="Distance039"  # Assembly joint (typed FeaturePython)
  Angle = 0
  AngleMax = 0
  AngleMin = 0
  Detach1 = false
  Detach2 = false
  Distance = 0
  Distance2 = 0
  EnableAngleMax = false
  EnableAngleMin = false
  EnableLengthMax = false
  EnableLengthMin = false
  JointType = 5 (Distance)
  LengthMax = 0
  LengthMin = 0
  Placement1 = pos=(1e-15,-3.6e-15,0) rot=(0,0,1;0rad)
  Placement2 = pos=(-0.75,27,-12.5) rot=(0.57735,-0.57735,0.57735;2.0944rad)
  Reference1 = -> HFS5_2020_160 [Face62,Vertex85]
  Reference2 = -> heater_bracket [Face26,Face26]
  Suppressed = false
FEATURE [Assembly::JointGroup] Joints
  Group = -> [GroundedJoint,Joint,Joint001,Joint002,Joint003,Joint004,Joint005,Joint031,Joint032,Joint033,Joint034,Joint035,Joint036,Joint037,Joint038,Joint045,Joint047,Joint048,Joint049,Joint050,Joint051,Joint067,Joint068,Joint069,Joint070,Joint071,Joint072,Joint073]
FEATURE [Assembly::AssemblyObject] Assembly
  Group = -> [Joints,HFS5_2020_160,GroundedJoint,tnut_2020_m3_roll,tnut_2020_m3_roll001,tnut_2020_m3_roll002,Joint,Joint001,Joint002,Joint003,Joint004,Joint005,Assembly001,Assembly002,heater_bracket,m3x6_bhcs,m3x6_bhcs001,Joint031,Joint032,Joint033,Joint034,Joint035,Joint036,Joint037,Joint038,Joint045,Joint047,m3x4_bhcs,m3x4_bhcs001,Joint048,Joint049,Joint050,Joint051,Joint067,Joint068,m3x8_bhcs004,Joint069,+4 more]
  Origin = -> Origin149
  Type = Assembly
FEATURE [Sketcher::SketchObject] Sketch114  label="hfb_block_plate_s"
  ArcFitTolerance = 1e-06
  AttachmentSupport = -> [Origin173]
  ExternalTypes = [0]
  FullyConstrained = true
  MakeInternals = false
  MapMode = 5
  _ExternalGeoVersion = 0
  expr: .Constraints.bend_straight = <<bracket_params>>.feature_bend_straight
  expr: .Constraints.block_screw_spacing = <<block_params>>.heatsink_screw_spacing
  expr: .Constraints.block_side_offset = <<bracket_params>>.feature_block_offset
  expr: .Constraints.block_width = <<block_params>>.heatsink_width
  expr: .Constraints.overlap_inner = <<bracket_params>>.front_overlap_inner
  expr: .Constraints.overlap_outer = <<bracket_params>>.front_overlap_outer
  expr: .Constraints.screw_head = <<bracket_params>>.feature_screw_head
  expr: .Constraints.screw_hole = <<bracket_params>>.feature_screw_hole
  expr: .Constraints.screw_pad_diam = <<bracket_params>>.front_pad_diam
  expr: .Constraints.screw_side_inset1 = <<bracket_params>>.front_side_screw_inset
  expr: .Constraints.side_extension = <<bracket_params>>.front_side_extension
  expr: .Constraints.side_screw_inset2 = <<bracket_params>>.front_side_screw_inset + <<bracket_params>>.front_side_screw_spacing
  sketch-geometry (30):
    g0: LineSegment [constr] StartX=-56 StartY=0 StartZ=0 EndX=-56 EndY=-50 EndZ=0
    g1: LineSegment [constr] StartX=-56 StartY=-50 StartZ=0 EndX=-6 EndY=-50 EndZ=0
    g2: LineSegment [constr] StartX=-6 StartY=-50 StartZ=0 EndX=-6 EndY=0 EndZ=0
    g3: LineSegment [constr] StartX=-6 StartY=0 StartZ=0 EndX=-56 EndY=0 EndZ=0
    g4: LineSegment [constr] StartX=-52 StartY=-4 StartZ=0 EndX=-52 EndY=-46 EndZ=0
    g5: LineSegment [constr] StartX=-52 StartY=-46 StartZ=0 EndX=-10 EndY=-46 EndZ=0
    g6: LineSegment [constr] StartX=-10 StartY=-46 StartZ=0 EndX=-10 EndY=-4 EndZ=0
    g7: LineSegment [constr] StartX=-10 StartY=-4 StartZ=0 EndX=-52 EndY=-4 EndZ=0
    g8: Circle [constr] CenterX=-31 CenterY=-25 CenterZ=0 NormalX=0 NormalY=0 NormalZ=1 AngleXU=0 Radius=21
    g9: Circle [constr] CenterX=-31 CenterY=-25 CenterZ=0 NormalX=0 NormalY=0 NormalZ=1 AngleXU=0 Radius=25
    g10: Circle CenterX=-52 CenterY=-4 CenterZ=0 NormalX=0 NormalY=0 NormalZ=1 AngleXU=0 Radius=1.7
    g11: Circle CenterX=-10 CenterY=-4 CenterZ=0 NormalX=0 NormalY=0 NormalZ=1 AngleXU=0 Radius=1.7
    g12: Circle [constr] CenterX=-52 CenterY=-4 CenterZ=0 NormalX=0 NormalY=0 NormalZ=1 AngleXU=0 Radius=2.75
    g13: Circle [constr] CenterX=-10 CenterY=-4 CenterZ=0 NormalX=0 NormalY=0 NormalZ=1 AngleXU=0 Radius=2.75
    g14: LineSegment StartX=0 StartY=0 StartZ=0 EndX=-56 EndY=0 EndZ=0
    g15: LineSegment StartX=0 StartY=0 StartZ=0 EndX=0 EndY=-8 EndZ=0
    g16: LineSegment StartX=0 StartY=-8 StartZ=0 EndX=-4 EndY=-8 EndZ=0
    g17: ArcOfCircle CenterX=-52 CenterY=-4 CenterZ=0 NormalX=0 NormalY=0 NormalZ=1 AngleXU=0 Radius=4 StartAngle=3.14159 EndAngle=5.67232
    g18: ArcOfCircle CenterX=-10 CenterY=-4 CenterZ=0 NormalX=0 NormalY=0 NormalZ=1 AngleXU=0 Radius=4 StartAngle=4.14493 EndAngle=5.1263
    g19: LineSegment [constr] StartX=-56 StartY=-4 StartZ=0 EndX=-4 EndY=-8 EndZ=0
    g20: LineSegment StartX=-4 StartY=-8 StartZ=0 EndX=-8.39122 EndY=-7.66221 EndZ=0
    g21: LineSegment StartX=-12.15 StartY=-7.37308 StartZ=0 EndX=-47.5709 EndY=-4.64839 EndZ=0
    g22: LineSegment StartX=-48.7234 StartY=-6.29431 StartZ=0 EndX=-47.5709 EndY=-4.64839 EndZ=0
    g23: LineSegment StartX=-56 StartY=0 StartZ=0 EndX=-56 EndY=-4 EndZ=0
    g24: Circle [constr] CenterX=0 CenterY=-23 CenterZ=0 NormalX=0 NormalY=0 NormalZ=1 AngleXU=0 Radius=1.7
    g25: Circle [constr] CenterX=0 CenterY=-23 CenterZ=0 NormalX=0 NormalY=0 NormalZ=1 AngleXU=0 Radius=2.75
    g26: Circle [constr] CenterX=0 CenterY=-6 CenterZ=0 NormalX=0 NormalY=0 NormalZ=1 AngleXU=0 Radius=1.7
    g27: Circle [constr] CenterX=0 CenterY=-6 CenterZ=0 NormalX=0 NormalY=0 NormalZ=1 AngleXU=0 Radius=2.75
    g28: GeomPoint [constr] X=0 Y=-28 Z=0
    g29: GeomPoint [constr] X=0 Y=-24.7 Z=0
  constraints (79):
    c: Coincident(g0,g1)
    c: Coincident(g1,g2)
    c: Coincident(g2,g3)
    c: Coincident(g3,g0)
    c: Vertical(g0)
    c: Vertical(g2)
    c: Horizontal(g1)
    c: Horizontal(g3)
    c: Coincident(g4,g5)
    c: Coincident(g5,g6)
    c: Coincident(g6,g7)
    c: Coincident(g7,g4)
    c: Vertical(g4)
    c: Vertical(g6)
    c: Horizontal(g5)
    c: Horizontal(g7)
    c: Coincident(g9,g8)
    c: Tangent(g8,g7)
    c: Tangent(g5,g8)
    c: Tangent(g6,g8)
    c: Tangent(g4,g8)
    c: Tangent(g9,g3)
    c: Tangent(g9,g2)
    c: Tangent(g9,g1)
    c: Tangent(g9,g0)
    c: PointOnObject(g2,g-1)
    c: Diameter(g8) = 42  'block_screw_spacing'
    c: Diameter(g9) = 50  'block_width'
    c: Distance(g2,g-1) = 6  'block_side_offset'
    c: Coincident(g10,g4)
    c: Coincident(g11,g6)
    c: Equal(g11,g10)
    c: Diameter(g10) = 3.4  'screw_hole'
    c: Coincident(g12,g4)
    c: Coincident(g13,g6)
    c: Equal(g12,g13)
    c: Diameter(g12) = 5.5  'screw_head'
    c: Coincident(g15,g14)
    c: Coincident(g16,g15)
    c: Horizontal(g16)
    c: PointOnObject(g15,g-2)
    c: Coincident(g14,g-1)
    c: Coincident(g17,g4)
    c: Coincident(g18,g6)
    c: Equal(g17,g18)
    c: Diameter(g17) = 8  'screw_pad_diam'
    c: DistanceY(g19,g-1) = 8  'overlap_inner'
    c: DistanceY(g19,g-1) = 4  'overlap_outer'
    c: DistanceX(g16,g-1) = 4  'bend_straight'
    c: Coincident(g16,g19)
    c: PointOnObject(g14,g-1)
    c: Coincident(g21,g18)
    c: Coincident(g18,g20)
    c: Coincident(g20,g16)
    c: PointOnObject(g18,g19)
    c: PointOnObject(g18,g19)
    c: Coincident(g22,g21)
    c: PointOnObject(g21,g19)
    c: Coincident(g23,g14)
    c: Tangent(g23,g17) = -1.5708
    c: Vertical(g23)
    c: Tangent(g17,g22) = -1.5708
    c: Angle(g22,g23) = 0.610865  'screw_pad_angle'
    c: PointOnObject(g19,g23)
    c: PointOnObject(g24,g-2)
    c: Coincident(g25,g24)
    c: PointOnObject(g26,g-2)
    c: Coincident(g27,g26)
    c: Equal(g10,g26)
    c: Equal(g10,g24)
    c: Equal(g12,g27)
    c: Equal(g12,g25)
    c: Distance(g26,g-1) = 6  'screw_side_inset1'
    c: DistanceY(g24,g-1) = 23  'side_screw_inset2'
    c: PointOnObject(g28,g-2)
    c: DistanceY(g28,g15) = 20  'side_extension'
    c: PointOnObject(g29,g24)
    c: PointOnObject(g29,g-2)
    c: DistanceY(g28,g29) = 3.3  'side_screw_outer'
FEATURE [PartDesign::FeaturePython] BaseBend001  label="hfb_block_plate"  # WARN: FeaturePython — macro-defined, semantics opaque (R4)
  BendSide = 0
  BendSketch = -> Sketch114
  MidPlane = false
  Reverse = false
  Suppressed = false
  length = 100
  radius = 1.6
  thickness = 1.5
  expr: radius = <<bracket_params>>.material_bend
  expr: thickness = <<bracket_params>>.material_thickness
FEATURE [PartDesign::FeaturePython] Bend001  label="hfb_side_bend"  # WARN: FeaturePython — macro-defined, semantics opaque (R4)
  AutoMiter = true
  BaseFeature = -> BaseBend001
  BendType = 1
  LengthList = [21.5]
  LengthSpec = 2
  NonperforationMaxLength = 5
  Perforate = false
  PerforationAngle = 0
  PerforationInitialLength = 5
  PerforationMaxLength = 5
  ReliefFactor = 0.7
  Suppressed = false
  UseReliefFactor = false
  angle = 90
  baseObject = -> BaseBend001 [Face4]
  bendAList = [90]
  extend1 = 0
  extend2 = 0
  gap1 = 0
  gap2 = 0
  invert = true
  kfactor = 0.5
  length = 21.5
  maxExtendDist = 5
  minGap = 0.2
  minReliefGap = 1
  miterangle1 = 0
  miterangle2 = 0
  offset = 0
  radius = 1.6
  reliefType = 0
  reliefd = 1
  reliefw = 0.8
  sketchflip = false
  sketchinvert = false
  unfold = false
  expr: length = <<bracket_params>>.feature_side_height
  expr: radius = <<bracket_params>>.material_bend
FEATURE [PartDesign::FeaturePython] Extend001  label="hfb_side_ext"  # WARN: FeaturePython — macro-defined, semantics opaque (R4)
  BaseFeature = -> Bend001
  Offset = 0.02
  Refine = true
  Suppressed = false
  UseSubtraction = false
  baseObject = -> Bend001 [Face19]
  gap1 = 0
  gap2 = 0
  length = 20
  expr: length = <<bracket_params>>.front_side_extension
FEATURE [Sketcher::SketchObject] Sketch115  label="hfb_side_features_s"
  ArcFitTolerance = 1e-06
  AttachmentSupport = -> [YZ_Plane152]
  ExternalTypes = [0]
  FullyConstrained = true
  MakeInternals = false
  MapMode = 5
  Placement = pos=(0,0,0) rot=(0.57735,0.57735,0.57735;2.0944rad)
  _ExternalGeoVersion = 0
  expr: .Constraints.cut_end = <<bracket_params>>.front_overlap_inner + <<bracket_params>>.front_side_extension
  expr: .Constraints.plate_overlap = <<bracket_params>>.front_overlap_inner
  expr: .Constraints.screw_head = <<bracket_params>>.feature_screw_head
  expr: .Constraints.screw_height = <<bracket_params>>.feature_side_height + <<bracket_params>>.feature_deck_clear_bracket - <<bracket_params>>.height_extrusion / 2
  expr: .Constraints.screw_hole = <<bracket_params>>.feature_screw_hole
  expr: .Constraints.screw_inset1 = <<bracket_params>>.front_side_screw_inset
  expr: .Constraints.screw_inset2 = <<bracket_params>>.front_side_screw_inset + <<bracket_params>>.front_side_screw_spacing
  expr: .Constraints.side_recess_top = <<bracket_params>>.feature_side_height + <<bracket_params>>.feature_deck_clear_bracket - <<bracket_params>>.height_extrusion + <<bracket_params>>.feature_side_recess
  sketch-geometry (9):
    g0: Circle CenterX=-23 CenterY=-12.5 CenterZ=0 NormalX=0 NormalY=0 NormalZ=1 AngleXU=0 Radius=1.7
    g1: Circle CenterX=-6 CenterY=-12.5 CenterZ=0 NormalX=0 NormalY=0 NormalZ=1 AngleXU=0 Radius=1.7
    g2: Circle [constr] CenterX=-23 CenterY=-12.5 CenterZ=0 NormalX=0 NormalY=0 NormalZ=1 AngleXU=0 Radius=2.75
    g3: Circle [constr] CenterX=-6 CenterY=-12.5 CenterZ=0 NormalX=0 NormalY=0 NormalZ=1 AngleXU=0 Radius=2.75
    g4: LineSegment [constr] StartX=-23 StartY=-12.5 StartZ=0 EndX=-6 EndY=-12.5 EndZ=0
    g5: LineSegment StartX=-28 StartY=0 StartZ=0 EndX=-28 EndY=-3.5 EndZ=0
    g6: LineSegment StartX=-28 StartY=-3.5 StartZ=0 EndX=-8 EndY=-3.5 EndZ=0
    g7: LineSegment StartX=-8 StartY=-3.5 StartZ=0 EndX=-8 EndY=0 EndZ=0
    g8: LineSegment StartX=-8 StartY=0 StartZ=0 EndX=-28 EndY=0 EndZ=0
  constraints (24):
    c: Coincident(g2,g0)
    c: Coincident(g3,g1)
    c: Coincident(g4,g0)
    c: Coincident(g4,g1)
    c: Horizontal(g4)
    c: Equal(g1,g0)
    c: Equal(g3,g2)
    c: Coincident(g5,g6)
    c: Coincident(g6,g7)
    c: Coincident(g7,g8)
    c: Coincident(g8,g5)
    c: Vertical(g5)
    c: Vertical(g7)
    c: Horizontal(g6)
    c: Diameter(g1) = 3.4  'screw_hole'
    c: Diameter(g3) = 5.5  'screw_head'
    c: DistanceX(g1,g-1) = 6  'screw_inset1'
    c: DistanceX(g0,g-1) = 23  'screw_inset2'
    c: PointOnObject(g5,g-1)
    c: PointOnObject(g7,g-1)
    c: DistanceX(g7,g-1) = 8  'plate_overlap'
    c: DistanceX(g5,g-1) = 28  'cut_end'
    c: DistanceY(g1,g-1) = 12.5  'screw_height'
    c: DistanceY(g6,g-1) = 3.5  'side_recess_top'
FEATURE [PartDesign::Pocket] Pocket047  label="hfb_side_features"
  BaseFeature = -> Extend001
  Direction = (-1,0,0)
  Length = 1.5
  Length2 = 5
  Profile = -> Sketch115
  ReferenceAxis = -> Sketch115 [N_Axis]
  Refine = true
  SideType = 0
  Suppressed = false
  Type = 0
  Type2 = 0
  expr: Length = <<bracket_params>>.material_thickness
FEATURE [PartDesign::Fillet] Fillet020  label="hfb_outer_flt"
  Base = -> Pocket047 [Edge29]
  BaseFeature = -> Pocket047
  Radius = 1.5
  Refine = true
  SupportTransform = false
  Suppressed = false
  UseAllEdges = false
FEATURE [PartDesign::Fillet] Fillet021  label="hfb_side_flt"
  Base = -> Fillet020 [Edge59,Edge54,Edge24]
  BaseFeature = -> Fillet020
  Radius = 4
  Refine = true
  SupportTransform = false
  Suppressed = false
  UseAllEdges = false
FEATURE [PartDesign::Fillet] Fillet022  label="hfb_ext_flt"
  Base = -> Fillet021 [Edge57]
  BaseFeature = -> Fillet021
  Radius = 1.5
  Refine = true
  SupportTransform = false
  Suppressed = false
  UseAllEdges = false
FEATURE [PartDesign::Fillet] Fillet023  label="hfb_overlay_flt"
  Base = -> Fillet022 [Edge70,Edge57,Edge71]
  BaseFeature = -> Fillet022
  Radius = 1.5
  Refine = true
  SupportTransform = false
  Suppressed = false
  UseAllEdges = false
FEATURE [PartDesign::Body] Body059  label="heater_front_bracket"
  AllowCompound = false
  Group = -> [Sketch114,BaseBend001,Bend001,Extend001,Sketch115,Pocket047,Fillet020,Fillet021,Fillet022,Fillet023]
  Origin = -> Origin173
  Tip = -> Fillet023
FEATURE [Part::FeaturePython] Unfold  label="heater_front_bracket_unfold"  # WARN: FeaturePython — macro-defined, semantics opaque (R4)
  baseObject = -> Fillet023 [Face20]
  kFactorStandard = 0
  kfactor = 0.4
  useManualKFactor = true
FEATURE [Sketcher::SketchObject] Unfold_Sketch  label="heater_front_bracket_unfold_cut"
  ArcFitTolerance = 1e-06
  ExternalTypes = [0]
  FullyConstrained = false
  MakeInternals = false
  _ExternalGeoVersion = 0
  sketch-geometry (24):
    g0: LineSegment StartX=47.4791 StartY=6.29431 StartZ=0 EndX=46.8174 EndY=5.34923 EndZ=0
    g1: ArcOfCircle CenterX=45.5887 CenterY=6.20959 CenterZ=0 NormalX=0 NormalY=0 NormalZ=1 AngleXU=1.5708 Radius=1.5 StartAngle=3.06482 EndAngle=4.10152
    g2: LineSegment StartX=11.2489 StartY=7.34668 StartZ=0 EndX=45.4736 EndY=4.71401 EndZ=0
    g3: ArcOfCircle CenterX=11.3639 CenterY=8.84227 CenterZ=0 NormalX=0 NormalY=0 NormalZ=1 AngleXU=1.5708 Radius=1.5 StartAngle=2.64753 EndAngle=3.06482
    g4: ArcOfCircle CenterX=8.75575 CenterY=4 CenterZ=0 NormalX=0 NormalY=0 NormalZ=1 AngleXU=-3.14159 Radius=4 StartAngle=4.21832 EndAngle=5.05291
    g5: ArcOfCircle CenterX=6.91886 CenterY=9.18419 CenterZ=0 NormalX=0 NormalY=0 NormalZ=1 AngleXU=1.5708 Radius=1.5 StartAngle=3.06482 EndAngle=3.48211
    g6: LineSegment StartX=2.75575 StartY=8 StartZ=0 EndX=6.80382 EndY=7.68861 EndZ=0
    g7: LineSegment StartX=1.85575 StartY=8 StartZ=0 EndX=2.75575 EndY=8 EndZ=0
    g8: LineSegment StartX=1.85575 StartY=8 StartZ=0 EndX=-2 EndY=8 EndZ=0
    g9: ArcOfCircle CenterX=-2 CenterY=9.5 CenterZ=0 NormalX=0 NormalY=0 NormalZ=1 AngleXU=-3.14159 Radius=1.5 StartAngle=0 EndAngle=1.5708
    g10: LineSegment StartX=-3.5 StartY=24 StartZ=0 EndX=-3.5 EndY=9.5 EndZ=0
    g11: ArcOfCircle CenterX=-7.5 CenterY=24 CenterZ=0 NormalX=0 NormalY=0 NormalZ=1 AngleXU=-3.14159 Radius=4 StartAngle=3.14159 EndAngle=4.71239
    g12: LineSegment StartX=-7.5 StartY=28 StartZ=0 EndX=-17.5 EndY=28 EndZ=0
    g13: ArcOfCircle CenterX=-17.5 CenterY=24 CenterZ=0 NormalX=0 NormalY=0 NormalZ=1 AngleXU=0 Radius=4 StartAngle=1.5708 EndAngle=3.14159
    g14: LineSegment StartX=-21.5 StartY=24 StartZ=0 EndX=-21.5 EndY=4 EndZ=0
    g15: ArcOfCircle CenterX=-17.5 CenterY=4 CenterZ=0 NormalX=0 NormalY=0 NormalZ=1 AngleXU=0 Radius=4 StartAngle=3.14159 EndAngle=4.71239
    g16: LineSegment StartX=-17.5 StartY=0 StartZ=0 EndX=53.2558 EndY=0 EndZ=0
    g17: ArcOfCircle CenterX=53.2558 CenterY=1.5 CenterZ=0 NormalX=0 NormalY=0 NormalZ=1 AngleXU=1.5708 Radius=1.5 StartAngle=3.14159 EndAngle=4.71239
    g18: LineSegment StartX=54.7558 StartY=1.5 StartZ=0 EndX=54.7558 EndY=4 EndZ=0
    g19: ArcOfCircle CenterX=50.7558 CenterY=4 CenterZ=0 NormalX=0 NormalY=0 NormalZ=1 AngleXU=-3.14159 Radius=4 StartAngle=3.14159 EndAngle=5.67232
    g20: Circle CenterX=50.7558 CenterY=4 CenterZ=0 NormalX=0 NormalY=0 NormalZ=1 AngleXU=-3.14159 Radius=1.7
    g21: Circle CenterX=8.75575 CenterY=4 CenterZ=0 NormalX=0 NormalY=0 NormalZ=1 AngleXU=-3.14159 Radius=1.7
    g22: Circle CenterX=-12.5 CenterY=6 CenterZ=0 NormalX=0 NormalY=0 NormalZ=1 AngleXU=-1.5708 Radius=1.7
    g23: Circle CenterX=-12.5 CenterY=23 CenterZ=0 NormalX=0 NormalY=0 NormalZ=1 AngleXU=-1.5708 Radius=1.7
FEATURE [Sketcher::SketchObject] Unfold_Sketch_bends  label="heater_front_bracket_unfold_bend"
  ArcFitTolerance = 1e-06
  ExternalTypes = [0]
  FullyConstrained = false
  MakeInternals = false
  Placement = pos=(0.06604,0,0.0639034) rot=(0,1,0;0.801839rad)
  _ExternalGeoVersion = 0
  sketch-geometry (1):
    g0: LineSegment StartX=0.0889232 StartY=8 StartZ=0 EndX=0.0889232 EndY=0 EndZ=0
FEATURE [App::DocumentObjectGroup] Group018  label="heater_mounting"
  Group = -> [Body048,Unfold001,Unfold_Sketch002,Unfold_Sketch_bends001,Body059,Unfold,Unfold_Sketch,Unfold_Sketch_bends]
FEATURE [TechDraw::DrawSVGTemplate] Template003
  EditableTexts = date_of_issue=4/11/26; document_type=Component Drawing; general_tolerances=ISO 2768-m; language_code=EN; part_material=A1008 Mild Steel - 16ga (1.5mm); revision_index=AAA; scale=1 : 1; sheet_number=1 / 1; title=Bedburner - Front Bracket
  Height = 210
  Orientation = 1
  Template = <path>
  Width = 297
FEATURE [TechDraw::DrawProjGroupItem] View010  label="Front"
  CoarseView = false
  Direction = (0,-1,0)
  Focus = 100
  HardHidden = false
  IsoCount = 0
  IsoHidden = false
  IsoVisible = false
  LockPosition = true
  Perspective = false
  Rotation = 0
  RotationVector = (1,0,0)
  ScaleType = 2
  ScrubCount = 1
  SeamHidden = false
  SeamVisible = false
  SmoothHidden = false
  SmoothVisible = true
  Source = -> [Body059]
  Type = 0
  X = 0
  XDirection = (1,0,0)
  Y = 0
FEATURE [TechDraw::DrawProjGroupItem] ProjItem012  label="Top001"
  CoarseView = false
  Direction = (0,0,1)
  Focus = 100
  HardHidden = false
  IsoCount = 0
  IsoHidden = false
  IsoVisible = false
  LockPosition = false
  Perspective = false
  Rotation = 0
  RotationVector = (1,0,0)
  ScaleType = 0
  ScrubCount = 1
  SeamHidden = false
  SeamVisible = false
  SmoothHidden = false
  SmoothVisible = true
  Source = -> [Body059]
  Type = 4
  X = 0
  XDirection = (1,0,0)
  Y = -62.233
FEATURE [TechDraw::DrawProjGroupItem] ProjItem  label="FrontTopRight"
  CoarseView = false
  Direction = (0.57735,-0.57735,0.57735)
  Focus = 100
  HardHidden = false
  IsoCount = 0
  IsoHidden = false
  IsoVisible = false
  LockPosition = false
  Perspective = false
  Rotation = 0
  RotationVector = (1,0,0)
  ScaleType = 0
  ScrubCount = 1
  SeamHidden = false
  SeamVisible = false
  SmoothHidden = false
  SmoothVisible = true
  Source = -> [Body059]
  Type = 7
  X = -74.799
  XDirection = (0.707107,0.707107,0)
  Y = -62.233
FEATURE [TechDraw::DrawProjGroupItem] ProjItem013  label="Left"
  CoarseView = false
  Direction = (-1,-1e-16,0)
  Focus = 100
  HardHidden = false
  IsoCount = 0
  IsoHidden = false
  IsoVisible = false
  LockPosition = false
  Perspective = false
  Rotation = 0
  RotationVector = (1,0,0)
  ScaleType = 0
  ScrubCount = 1
  SeamHidden = false
  SeamVisible = false
  SmoothHidden = false
  SmoothVisible = true
  Source = -> [Body059]
  Type = 1
  X = 67
  XDirection = (1e-16,-1,0)
  Y = 0
FEATURE [TechDraw::DrawProjGroup] ProjGroup001
  Anchor = -> View010
  AutoDistribute = true
  LockPosition = false
  ProjectionType = 0
  Rotation = 0
  ScaleType = 0
  Source = -> [Body059]
  Views = -> [View010,ProjItem012,ProjItem,ProjItem013]
  X = 163.421
  Y = 165.474
  spacingX = 25
  spacingY = 25
FEATURE [TechDraw::DrawViewDimension] Dimension
  AngleOverride = false
  Arbitrary = false
  ArbitraryTolerances = false
  BoxCorners = (2) [(-28,-11.5,-1e-07),(28,11.5,1e-07)]
  EqualTolerance = true
  ExtensionAngle = 0
  FormatSpec = %.2w
  FormatSpecOverTolerance = %+.2w
  FormatSpecUnderTolerance = %+.2w
  Inverted = false
  LineAngle = 0
  LockPosition = false
  MeasureType = 1
  OverTolerance = 0
  References2D = -> [View010]
  Rotation = 0
  ScaleType = 0
  ShowUnits = false
  TheoreticalExact = false
  Type = 6
  UnderTolerance = 0
  UseActualArea = true
  X = 13.1028
  Y = -5.30839
FEATURE [TechDraw::DrawViewDimension] Dimension116
  AngleOverride = false
  Arbitrary = false
  ArbitraryTolerances = false
  BoxCorners = (2) [(-28,-11.5,-1e-07),(28,11.5,1e-07)]
  EqualTolerance = true
  ExtensionAngle = 0
  FormatSpec = %.2w
  FormatSpecOverTolerance = %+.2w
  FormatSpecUnderTolerance = %+.2w
  Inverted = false
  LineAngle = 0
  LockPosition = false
  MeasureType = 1
  OverTolerance = 0
  References2D = -> [View010]
  Rotation = 0
  ScaleType = 0
  ShowUnits = false
  TheoreticalExact = false
  Type = 0
  UnderTolerance = 0
  UseActualArea = true
  X = 0
  Y = 27.9136
FEATURE [TechDraw::DrawViewDimension] Dimension117
  AngleOverride = false
  Arbitrary = false
  ArbitraryTolerances = false
  BoxCorners = (2) [(-28,-11.5,-1e-07),(28,11.5,1e-07)]
  EqualTolerance = true
  ExtensionAngle = 0
  FormatSpec = %.2w
  FormatSpecOverTolerance = %+.2w
  FormatSpecUnderTolerance = %+.2w
  Inverted = false
  LineAngle = 0
  LockPosition = false
  MeasureType = 1
  OverTolerance = 0
  References2D = -> [View010]
  Rotation = 0
  ScaleType = 0
  ShowUnits = false
  TheoreticalExact = false
  Type = 0
  UnderTolerance = 0
  UseActualArea = true
  X = 44.5369
  Y = 0
FEATURE [TechDraw::DrawViewDimension] Dimension118
  AngleOverride = false
  Arbitrary = false
  ArbitraryTolerances = false
  BoxCorners = (2) [(-14,-11.5,-1e-07),(14,11.5,1e-07)]
  EqualTolerance = true
  ExtensionAngle = 0
  FormatSpec = %.2w
  FormatSpecOverTolerance = %+.2w
  FormatSpecUnderTolerance = %+.2w
  Inverted = false
  LineAngle = 0
  LockPosition = false
  MeasureType = 1
  OverTolerance = 0
  References2D = -> [ProjItem013]
  Rotation = 0
  ScaleType = 0
  ShowUnits = false
  TheoreticalExact = false
  Type = 2
  UnderTolerance = 0
  UseActualArea = true
  X = 9.4229
  Y = 22.0015
FEATURE [TechDraw::DrawViewDimension] Dimension119
  AngleOverride = false
  Arbitrary = false
  ArbitraryTolerances = false
  BoxCorners = (2) [(-14,-11.5,-1e-07),(14,11.5,1e-07)]
  EqualTolerance = true
  ExtensionAngle = 0
  FormatSpec = %.2w
  FormatSpecOverTolerance = %+.2w
  FormatSpecUnderTolerance = %+.2w
  Inverted = false
  LineAngle = 0
  LockPosition = false
  MeasureType = 1
  OverTolerance = 0
  References2D = -> [ProjItem013]
  Rotation = 0
  ScaleType = 0
  ShowUnits = false
  TheoreticalExact = false
  Type = 2
  UnderTolerance = 0
  UseActualArea = true
  X = 14.9364
  Y = -21.4275
FEATURE [TechDraw::DrawViewDimension] Dimension120
  AngleOverride = false
  Arbitrary = false
  ArbitraryTolerances = false
  BoxCorners = (2) [(-14,-11.5,-1e-07),(14,11.5,1e-07)]
  EqualTolerance = true
  ExtensionAngle = 0
  FormatSpec = %.2w
  FormatSpecOverTolerance = %+.2w
  FormatSpecUnderTolerance = %+.2w
  Inverted = false
  LineAngle = 0
  LockPosition = false
  MeasureType = 1
  OverTolerance = 0
  References2D = -> [ProjItem013]
  Rotation = 0
  ScaleType = 0
  ShowUnits = false
  TheoreticalExact = false
  Type = 1
  UnderTolerance = 0
  UseActualArea = true
  X = 0.5
  Y = -14.9008
FEATURE [TechDraw::DrawViewDimension] Dimension121
  AngleOverride = false
  Arbitrary = false
  ArbitraryTolerances = false
  BoxCorners = (2) [(-14,-11.5,-1e-07),(14,11.5,1e-07)]
  EqualTolerance = true
  ExtensionAngle = 0
  FormatSpec = %.2w
  FormatSpecOverTolerance = %+.2w
  FormatSpecUnderTolerance = %+.2w
  Inverted = false
  LineAngle = 0
  LockPosition = false
  MeasureType = 1
  OverTolerance = 0
  References2D = -> [ProjItem013]
  Rotation = 0
  ScaleType = 0
  ShowUnits = false
  TheoreticalExact = false
  Type = 0
  UnderTolerance = 0
  UseActualArea = true
  X = -24.3976
  Y = -19.3093
FEATURE [TechDraw::DrawViewDimension] Dimension122
  AngleOverride = false
  Arbitrary = false
  ArbitraryTolerances = false
  BoxCorners = (2) [(-14,-11.5,-1e-07),(14,11.5,1e-07)]
  EqualTolerance = true
  ExtensionAngle = 0
  FormatSpec = %.2w
  FormatSpecOverTolerance = %+.2w
  FormatSpecUnderTolerance = %+.2w
  Inverted = false
  LineAngle = 0
  LockPosition = false
  MeasureType = 1
  OverTolerance = 0
  References2D = -> [ProjItem013]
  Rotation = 0
  ScaleType = 0
  ShowUnits = false
  TheoreticalExact = false
  Type = 0
  UnderTolerance = 0
  UseActualArea = true
  X = -3.03268
  Y = 19.298
FEATURE [TechDraw::DrawViewDimension] Dimension123
  AngleOverride = false
  Arbitrary = false
  ArbitraryTolerances = false
  BoxCorners = (2) [(-14,-11.5,-1e-07),(14,11.5,1e-07)]
  EqualTolerance = true
  ExtensionAngle = 0
  FormatSpec = R%.2w
  FormatSpecOverTolerance = %+.2w
  FormatSpecUnderTolerance = %+.2w
  Inverted = false
  LineAngle = 0
  LockPosition = false
  MeasureType = 1
  OverTolerance = 0
  References2D = -> [ProjItem013]
  Rotation = 0
  ScaleType = 0
  ShowUnits = false
  TheoreticalExact = false
  Type = 4
  UnderTolerance = 0
  UseActualArea = true
  X = -23.9041
  Y = -6.41655
FEATURE [TechDraw::DrawViewDimension] Dimension124
  AngleOverride = false
  Arbitrary = false
  ArbitraryTolerances = false
  BoxCorners = (2) [(-14,-11.5,-1e-07),(14,11.5,1e-07)]
  EqualTolerance = true
  ExtensionAngle = 0
  FormatSpec = R%.2w
  FormatSpecOverTolerance = %+.2w
  FormatSpecUnderTolerance = %+.2w
  Inverted = false
  LineAngle = 0
  LockPosition = false
  MeasureType = 1
  OverTolerance = 0
  References2D = -> [ProjItem013]
  Rotation = 0
  ScaleType = 0
  ShowUnits = false
  TheoreticalExact = false
  Type = 4
  UnderTolerance = 0
  UseActualArea = true
  X = 0.176514
  Y = 4.70948
FEATURE [TechDraw::DrawViewDimension] Dimension125
  AngleOverride = false
  Arbitrary = false
  ArbitraryTolerances = false
  BoxCorners = (2) [(-14,-11.5,-1e-07),(14,11.5,1e-07)]
  EqualTolerance = true
  ExtensionAngle = 0
  FormatSpec = %.2w
  FormatSpecOverTolerance = %+.2w
  FormatSpecUnderTolerance = %+.2w
  Inverted = false
  LineAngle = 0
  LockPosition = false
  MeasureType = 1
  OverTolerance = 0
  References2D = -> [ProjItem013]
  Rotation = 0
  ScaleType = 0
  ShowUnits = false
  TheoreticalExact = false
  Type = 0
  UnderTolerance = 0
  UseActualArea = true
  X = -16.7047
  Y = 24.3693
FEATURE [TechDraw::DrawViewDimension] Dimension126
  AngleOverride = false
  Arbitrary = false
  ArbitraryTolerances = false
  BoxCorners = (2) [(-28,-14,-1e-07),(28,14,1e-07)]
  EqualTolerance = true
  ExtensionAngle = 0
  FormatSpec = ⌀%.2w
  FormatSpecOverTolerance = %+.2w
  FormatSpecUnderTolerance = %+.2w
  Inverted = false
  LineAngle = 0
  LockPosition = false
  MeasureType = 1
  OverTolerance = 0
  References2D = -> [ProjItem012]
  Rotation = 0
  ScaleType = 0
  ShowUnits = false
  TheoreticalExact = false
  Type = 5
  UnderTolerance = 0
  UseActualArea = true
  X = -43.0112
  Y = 14.573
FEATURE [TechDraw::DrawViewDimension] Dimension127
  AngleOverride = false
  Arbitrary = false
  ArbitraryTolerances = false
  BoxCorners = (2) [(-28,-14,-1e-07),(28,14,1e-07)]
  EqualTolerance = true
  ExtensionAngle = 0
  FormatSpec = R%.2w
  FormatSpecOverTolerance = %+.2w
  FormatSpecUnderTolerance = %+.2w
  Inverted = false
  LineAngle = 0
  LockPosition = false
  MeasureType = 1
  OverTolerance = 0
  References2D = -> [ProjItem012]
  Rotation = 0
  ScaleType = 0
  ShowUnits = false
  TheoreticalExact = false
  Type = 4
  UnderTolerance = 0
  UseActualArea = true
  X = -42.9132
  Y = 0.319748
FEATURE [TechDraw::DrawViewDimension] Dimension128
  AngleOverride = false
  Arbitrary = false
  ArbitraryTolerances = false
  BoxCorners = (2) [(-28,-14,-1e-07),(28,14,1e-07)]
  EqualTolerance = true
  ExtensionAngle = 0
  FormatSpec = %.2w
  FormatSpecOverTolerance = %+.2w
  FormatSpecUnderTolerance = %+.2w
  Inverted = false
  LineAngle = 0
  LockPosition = false
  MeasureType = 1
  OverTolerance = 0
  References2D = -> [ProjItem012]
  Rotation = 0
  ScaleType = 0
  ShowUnits = false
  TheoreticalExact = false
  Type = 0
  UnderTolerance = 0
  UseActualArea = true
  X = 0
  Y = -16.0779
FEATURE [TechDraw::DrawViewDimension] Dimension129
  AngleOverride = false
  Arbitrary = false
  ArbitraryTolerances = false
  BoxCorners = (2) [(-28,-14,-1e-07),(28,14,1e-07)]
  EqualTolerance = true
  ExtensionAngle = 0
  FormatSpec = %.2w
  FormatSpecOverTolerance = %+.2w
  FormatSpecUnderTolerance = %+.2w
  Inverted = false
  LineAngle = 0
  LockPosition = false
  MeasureType = 1
  OverTolerance = 0
  References2D = -> [ProjItem012]
  Rotation = 0
  ScaleType = 0
  ShowUnits = false
  TheoreticalExact = false
  Type = 1
  UnderTolerance = 0
  UseActualArea = true
  X = -3
  Y = 29.2738
FEATURE [TechDraw::DrawViewDimension] Dimension130
  AngleOverride = false
  Arbitrary = false
  ArbitraryTolerances = false
  BoxCorners = (2) [(-28,-14,-1e-07),(28,14,1e-07)]
  EqualTolerance = true
  ExtensionAngle = 0
  FormatSpec = %.2w
  FormatSpecOverTolerance = %+.2w
  FormatSpecUnderTolerance = %+.2w
  Inverted = false
  LineAngle = 0
  LockPosition = false
  MeasureType = 1
  OverTolerance = 0
  References2D = -> [ProjItem012]
  Rotation = 0
  ScaleType = 0
  ShowUnits = false
  TheoreticalExact = false
  Type = 0
  UnderTolerance = 0
  UseActualArea = true
  X = 41.2266
  Y = 0
FEATURE [TechDraw::DrawViewDimension] Dimension131
  AngleOverride = false
  Arbitrary = false
  ArbitraryTolerances = false
  BoxCorners = (2) [(-28,-14,-1e-07),(28,14,1e-07)]
  EqualTolerance = true
  ExtensionAngle = 0
  FormatSpec = %.2w
  FormatSpecOverTolerance = %+.2w
  FormatSpecUnderTolerance = %+.2w
  Inverted = false
  LineAngle = 0
  LockPosition = false
  MeasureType = 1
  OverTolerance = 0
  References2D = -> [ProjItem012]
  Rotation = 0
  ScaleType = 0
  ShowUnits = false
  TheoreticalExact = false
  Type = 0
  UnderTolerance = 0
  UseActualArea = true
  X = 11.8594
  Y = 31.0371
FEATURE [TechDraw::DrawViewDimension] Dimension132
  AngleOverride = false
  Arbitrary = false
  ArbitraryTolerances = false
  BoxCorners = (2) [(-28,-14,-1e-07),(28,14,1e-07)]
  EqualTolerance = true
  ExtensionAngle = 0
  FormatSpec = %.2w
  FormatSpecOverTolerance = %+.2w
  FormatSpecUnderTolerance = %+.2w
  Inverted = false
  LineAngle = 0
  LockPosition = false
  MeasureType = 1
  OverTolerance = 0
  References2D = -> [ProjItem012]
  Rotation = 0
  ScaleType = 0
  ShowUnits = false
  TheoreticalExact = false
  Type = 1
  UnderTolerance = 0
  UseActualArea = true
  X = 30.2883
  Y = 32.0865
FEATURE [TechDraw::DrawViewDimension] Dimension133
  AngleOverride = false
  Arbitrary = false
  ArbitraryTolerances = false
  BoxCorners = (2) [(-28,-14,-1e-07),(28,14,1e-07)]
  EqualTolerance = true
  ExtensionAngle = 0
  FormatSpec = %.2w
  FormatSpecOverTolerance = %+.2w
  FormatSpecUnderTolerance = %+.2w
  Inverted = false
  LineAngle = 0
  LockPosition = false
  MeasureType = 1
  OverTolerance = 0
  References2D = -> [ProjItem012]
  Rotation = 0
  ScaleType = 0
  ShowUnits = false
  TheoreticalExact = false
  Type = 1
  UnderTolerance = 0
  UseActualArea = true
  X = -0.75
  Y = -5.18526
FEATURE [TechDraw::DrawViewDimension] Dimension134
  AngleOverride = false
  Arbitrary = false
  ArbitraryTolerances = false
  BoxCorners = (2) [(-28,-14,-1e-07),(28,14,1e-07)]
  EqualTolerance = true
  ExtensionAngle = 0
  FormatSpec = %.2w
  FormatSpecOverTolerance = %+.2w
  FormatSpecUnderTolerance = %+.2w
  Inverted = false
  LineAngle = 0
  LockPosition = false
  MeasureType = 1
  OverTolerance = 0
  References2D = -> [ProjItem012]
  Rotation = 0
  ScaleType = 0
  ShowUnits = false
  TheoreticalExact = false
  Type = 0
  UnderTolerance = 0
  UseActualArea = true
  X = 29.6344
  Y = -0.863087
FEATURE [TechDraw::DrawViewDimension] Dimension135
  AngleOverride = false
  Arbitrary = false
  ArbitraryTolerances = false
  BoxCorners = (2) [(-28,-14,-1e-07),(28,14,1e-07)]
  EqualTolerance = true
  ExtensionAngle = 0
  FormatSpec = R%.2w
  FormatSpecOverTolerance = %+.2w
  FormatSpecUnderTolerance = %+.2w
  Inverted = false
  LineAngle = 0
  LockPosition = false
  MeasureType = 1
  OverTolerance = 0
  References2D = -> [ProjItem012]
  Rotation = 0
  ScaleType = 0
  ShowUnits = false
  TheoreticalExact = false
  Type = 4
  UnderTolerance = 0
  UseActualArea = true
  X = 26.3038
  Y = -3.98863
FEATURE [TechDraw::DrawViewDimension] Dimension136
  AngleOverride = false
  Arbitrary = false
  ArbitraryTolerances = false
  BoxCorners = (2) [(-28,-14,-1e-07),(28,14,1e-07)]
  EqualTolerance = true
  ExtensionAngle = 0
  FormatSpec = %.2w
  FormatSpecOverTolerance = %+.2w
  FormatSpecUnderTolerance = %+.2w
  Inverted = false
  LineAngle = 0
  LockPosition = false
  MeasureType = 1
  OverTolerance = 0
  References2D = -> [ProjItem012]
  Rotation = 0
  ScaleType = 0
  ShowUnits = false
  TheoreticalExact = false
  Type = 6
  UnderTolerance = 0
  UseActualArea = true
  X = 13.6437
  Y = -0.230267
FEATURE [TechDraw::DrawViewDimension] Dimension137
  AngleOverride = false
  Arbitrary = false
  ArbitraryTolerances = false
  BoxCorners = (2) [(-28,-14,-1e-07),(28,14,1e-07)]
  EqualTolerance = true
  ExtensionAngle = 0
  FormatSpec = %.2w
  FormatSpecOverTolerance = %+.2w
  FormatSpecUnderTolerance = %+.2w
  Inverted = false
  LineAngle = 0
  LockPosition = false
  MeasureType = 1
  OverTolerance = 0
  References2D = -> [ProjItem012]
  Rotation = 0
  ScaleType = 0
  ShowUnits = false
  TheoreticalExact = false
  Type = 6
  UnderTolerance = 0
  UseActualArea = true
  X = -19.183
  Y = 1.72245
FEATURE [TechDraw::DrawViewDimension] Dimension138
  AngleOverride = false
  Arbitrary = false
  ArbitraryTolerances = false
  BoxCorners = (2) [(-28,-17.5,-1e-07),(28,17.5,1e-07)]
  EqualTolerance = true
  ExtensionAngle = 0
  FormatSpec = %.2w
  FormatSpecOverTolerance = %+.2w
  FormatSpecUnderTolerance = %+.2w
  Inverted = false
  LineAngle = 0
  LockPosition = false
  MeasureType = 1
  OverTolerance = 0
  References2D = -> [ProjItem009]
  Rotation = 0
  ScaleType = 0
  ShowUnits = false
  TheoreticalExact = false
  Type = 6
  UnderTolerance = 0
  UseActualArea = true
  X = 6.68416
  Y = 17.3131
FEATURE [TechDraw::DrawViewDimension] Dimension139
  AngleOverride = false
  Arbitrary = false
  ArbitraryTolerances = false
  BoxCorners = (2) [(-28,-17.5,-1e-07),(28,17.5,1e-07)]
  EqualTolerance = true
  ExtensionAngle = 0
  FormatSpec = %.2w
  FormatSpecOverTolerance = %+.2w
  FormatSpecUnderTolerance = %+.2w
  Inverted = false
  LineAngle = 0
  LockPosition = false
  MeasureType = 1
  OverTolerance = 0
  References2D = -> [ProjItem009]
  Rotation = 0
  ScaleType = 0
  ShowUnits = false
  TheoreticalExact = false
  Type = 6
  UnderTolerance = 0
  UseActualArea = true
  X = -7.35738
  Y = 11.5826
FEATURE [TechDraw::DrawViewDimension] Dimension140
  AngleOverride = false
  Arbitrary = false
  ArbitraryTolerances = false
  BoxCorners = (2) [(-28,-17.5,-1e-07),(28,17.5,1e-07)]
  EqualTolerance = true
  ExtensionAngle = 0
  FormatSpec = %.2w
  FormatSpecOverTolerance = %+.2w
  FormatSpecUnderTolerance = %+.2w
  Inverted = false
  LineAngle = 0
  LockPosition = false
  MeasureType = 1
  OverTolerance = 0
  References2D = -> [ProjItem009]
  Rotation = 0
  ScaleType = 0
  ShowUnits = false
  TheoreticalExact = false
  Type = 0
  UnderTolerance = 0
  UseActualArea = true
  X = 15.6017
  Y = 8.06797
FEATURE [TechDraw::DrawViewDimension] Dimension141
  AngleOverride = false
  Arbitrary = false
  ArbitraryTolerances = false
  BoxCorners = (2) [(-28,-17.5,-1e-07),(28,17.5,1e-07)]
  EqualTolerance = true
  ExtensionAngle = 0
  FormatSpec = %.2w
  FormatSpecOverTolerance = %+.2w
  FormatSpecUnderTolerance = %+.2w
  Inverted = false
  LineAngle = 0
  LockPosition = false
  MeasureType = 1
  OverTolerance = 0
  References2D = -> [ProjItem009]
  Rotation = 0
  ScaleType = 0
  ShowUnits = false
  TheoreticalExact = false
  Type = 1
  UnderTolerance = 0
  UseActualArea = true
  X = 34.8068
  Y = -12.732
FEATURE [TechDraw::DrawViewDimension] Dimension142
  AngleOverride = false
  Arbitrary = false
  ArbitraryTolerances = false
  BoxCorners = (2) [(-28,-17.5,-1e-07),(28,17.5,1e-07)]
  EqualTolerance = true
  ExtensionAngle = 0
  FormatSpec = R%.2w
  FormatSpecOverTolerance = %+.2w
  FormatSpecUnderTolerance = %+.2w
  Inverted = false
  LineAngle = 0
  LockPosition = false
  MeasureType = 1
  OverTolerance = 0
  References2D = -> [ProjItem009]
  Rotation = 0
  ScaleType = 0
  ShowUnits = false
  TheoreticalExact = false
  Type = 4
  UnderTolerance = 0
  UseActualArea = true
  X = 6.01556
  Y = -15.6324
FEATURE [TechDraw::DrawPage] Page003  label="td_bracket_rear"
  KeepUpdated = true
  NextBalloonIndex = 1
  ProjectionType = 0
  Template = -> Template002
  Views = -> [ProjGroup,Dimension097,Dimension098,Dimension099,Dimension100,Dimension101,Dimension102,Dimension103,Dimension104,Dimension105,Dimension106,Dimension107,Dimension108,Dimension109,Dimension110,Dimension111,Dimension112,Dimension113,Dimension114,Dimension115,Dimension138,Dimension139,Dimension140,Dimension141,Dimension142]
FEATURE [TechDraw::DrawViewDimension] Dimension143
  AngleOverride = false
  Arbitrary = false
  ArbitraryTolerances = false
  BoxCorners = (2) [(-28,-11.5,-1e-07),(28,11.5,1e-07)]
  EqualTolerance = true
  ExtensionAngle = 0
  FormatSpec = R%.2w
  FormatSpecOverTolerance = %+.2w
  FormatSpecUnderTolerance = %+.2w
  Inverted = false
  LineAngle = 0
  LockPosition = false
  MeasureType = 1
  OverTolerance = 0
  References2D = -> [View010]
  Rotation = 0
  ScaleType = 0
  ShowUnits = false
  TheoreticalExact = false
  Type = 4
  UnderTolerance = 0
  UseActualArea = true
  X = 33.9125
  Y = 23.8729
FEATURE [TechDraw::DrawPage] Page004  label="td_bracket_front"
  KeepUpdated = true
  NextBalloonIndex = 1
  ProjectionType = 0
  Template = -> Template003
  Views = -> [ProjGroup001,Dimension,Dimension116,Dimension117,Dimension118,Dimension119,Dimension120,Dimension121,Dimension122,Dimension123,Dimension124,Dimension125,Dimension126,Dimension127,Dimension128,Dimension129,Dimension130,Dimension131,Dimension132,Dimension133,Dimension134,Dimension135,Dimension136,Dimension137,Dimension143]
FEATURE [App::Point] Origin174  label="Origin"
  Role = Origin
FEATURE [App::Point] Origin175  label="Origin"
  Role = Origin
FEATURE [App::Point] Origin176  label="Origin"
  Role = Origin
FEATURE [App::Point] Origin177  label="Origin"
  Role = Origin
FEATURE [App::Point] Origin182  label="Origin"
  Role = Origin
FEATURE [App::Point] Origin183  label="Origin"
  Role = Origin
FEATURE [App::Point] Origin184  label="Origin"
  Role = Origin
FEATURE [App::Point] Origin185  label="Origin"
  Role = Origin
FEATURE [App::Point] Origin186  label="Origin"
  Role = Origin
FEATURE [App::Point] Origin187  label="Origin"
  Role = Origin
FEATURE [App::Point] Origin188  label="Origin"
  Role = Origin
FEATURE [App::Point] Origin189  label="Origin"
  Role = Origin
FEATURE [App::Point] Origin190  label="Origin"
  Role = Origin
FEATURE [App::Point] Origin191  label="Origin"
  Role = Origin
FEATURE [App::Point] Origin192  label="Origin"
  Role = Origin
FEATURE [App::Point] Origin193  label="Origin"
  Role = Origin
FEATURE [App::Point] Origin194  label="Origin"
  Role = Origin
FEATURE [App::Point] Origin195  label="Origin"
  Role = Origin
FEATURE [App::Point] Origin197
  Role = Origin
FEATURE [PartDesign::FeatureBase] Clone026  label="hhp_tf_cln"
  BaseFeature = -> Body057
  Suppressed = false
FEATURE [Sketcher::SketchObject] Sketch116  label="hhp_tf_pocket_s"
  ArcFitTolerance = 1e-06
  AttachmentSupport = -> [Origin196]
  ExternalTypes = [0]
  FullyConstrained = true
  MakeInternals = false
  MapMode = 5
  _ExternalGeoVersion = 1
  expr: .Constraints.placement_length = <<block_params>>.tfuse_placement_length
  expr: .Constraints.placement_width = <<block_params>>.tfuse_placement_width
  expr: .Constraints.pocket_length = <<block_params>>.tfuse_pocket_length
  expr: .Constraints.pocket_width = <<block_params>>.tfuse_pocket_width
  expr: .Constraints.screw_spacing = <<block_params>>.tfuse_screw_spacing
  expr: .Constraints.tfus_width = <<block_params>>.tfuse_width
  expr: .Constraints.tfuse_hole = <<block_params>>.tfuse_screw_hole
  expr: .Constraints.tfuse_length = <<block_params>>.tfuse_length
  sketch-geometry (13):
    g0: LineSegment StartX=13.4 StartY=14.8 StartZ=0 EndX=13.4 EndY=3.2 EndZ=0
    g1: LineSegment StartX=13.4 StartY=3.2 StartZ=0 EndX=36.6 EndY=3.2 EndZ=0
    g2: LineSegment StartX=36.6 StartY=3.2 StartZ=0 EndX=36.6 EndY=14.8 EndZ=0
    g3: LineSegment StartX=36.6 StartY=14.8 StartZ=0 EndX=13.4 EndY=14.8 EndZ=0
    g4: Circle [constr] CenterX=25 CenterY=9 CenterZ=0 NormalX=0 NormalY=0 NormalZ=1 AngleXU=0 Radius=5.8
    g5: Circle [constr] CenterX=25 CenterY=9 CenterZ=0 NormalX=0 NormalY=0 NormalZ=1 AngleXU=0 Radius=11.6
    g6: LineSegment [constr] StartX=19.5 StartY=3.5 StartZ=0 EndX=36 EndY=3.5 EndZ=0
    g7: LineSegment [constr] StartX=36 StartY=3.5 StartZ=0 EndX=36 EndY=14.5 EndZ=0
    g8: LineSegment [constr] StartX=36 StartY=14.5 StartZ=0 EndX=19.5 EndY=14.5 EndZ=0
    g9: ArcOfCircle [constr] CenterX=19.5 CenterY=9 CenterZ=0 NormalX=0 NormalY=0 NormalZ=1 AngleXU=0 Radius=5.5 StartAngle=1.5708 EndAngle=4.71239
    g10: LineSegment [constr] StartX=36 StartY=9 StartZ=0 EndX=14 EndY=9 EndZ=0
    g11: Circle [constr] CenterX=19.5 CenterY=9 CenterZ=0 NormalX=0 NormalY=0 NormalZ=1 AngleXU=0 Radius=2.5
    g12: Circle [constr] CenterX=25 CenterY=9 CenterZ=0 NormalX=0 NormalY=0 NormalZ=1 AngleXU=0 Radius=5.5
  constraints (36):
    c: Coincident(g0,g1)
    c: Coincident(g1,g2)
    c: Coincident(g2,g3)
    c: Coincident(g3,g0)
    c: Vertical(g0)
    c: Vertical(g2)
    c: Horizontal(g1)
    c: Horizontal(g3)
    c: Coincident(g5,g4)
    c: Tangent(g5,g2)
    c: Tangent(g5,g0)
    c: Tangent(g4,g3)
    c: Tangent(g4,g1)
    c: DistanceY(g-1,g4) = 9  'placement_width'
    c: DistanceX(g-1,g4) = 25  'placement_length'
    c: Diameter(g5) = 23.2  'pocket_length'
    c: Diameter(g4) = 11.6  'pocket_width'
    c: Coincident(g6,g7)
    c: Coincident(g7,g8)
    c: Vertical(g7)
    c: Horizontal(g6)
    c: Horizontal(g8)
    c: Tangent(g9,g8) = -1.5708
    c: Tangent(g9,g6) = -1.5708
    c: Diameter(g9) = 11  'tfus_width'
    c: PointOnObject(g9,g10)
    c: Horizontal(g10)
    c: PointOnObject(g10,g7)
    c: DistanceX(g10,g10) = 22  'tfuse_length'
    c: PointOnObject(g10,g9)
    c: Coincident(g11,g9)
    c: Diameter(g11) = 5  'tfuse_hole'
    c: PointOnObject(g12,g10)
    c: PointOnObject(g9,g12)
    c: Diameter(g12) = 11  'screw_spacing'
    c: Coincident(g12,g4)
FEATURE [PartDesign::Pocket] Pocket048  label="hhp_tf_pocket"
  BaseFeature = -> Clone026
  Direction = (0,0,-1)
  Length = 0.8
  Length2 = 5
  Profile = -> Sketch116
  Refine = true
  SideType = 0
  Suppressed = false
  Type = 0
  Type2 = 0
  expr: Length = <<block_params>>.tfuse_pocket_depth
FEATURE [Sketcher::SketchObject] Sketch117  label="hhp_tf_screw_s"
  ArcFitTolerance = 1e-06
  AttachmentSupport = -> [Origin196]
  ExternalTypes = [0]
  FullyConstrained = true
  MakeInternals = false
  MapMode = 5
  _ExternalGeoVersion = 1
  expr: .Constraints.placement_screw1 = <<block_params>>.tfuse_placement_length - <<block_params>>.tfuse_screw_spacing / 2
  expr: .Constraints.placement_screw2 = <<block_params>>.tfuse_placement_length + <<block_params>>.tfuse_screw_spacing / 2
  expr: .Constraints.placement_width = <<block_params>>.tfuse_placement_width
  expr: .Constraints.screw_hole = <<block_params>>.screw_drill_diam
  sketch-geometry (3):
    g0: Circle CenterX=19.5 CenterY=9 CenterZ=0 NormalX=0 NormalY=0 NormalZ=1 AngleXU=0 Radius=1.25
    g1: Circle CenterX=30.5 CenterY=9 CenterZ=0 NormalX=0 NormalY=0 NormalZ=1 AngleXU=0 Radius=1.25
    g2: LineSegment [constr] StartX=19.5 StartY=9 StartZ=0 EndX=30.5 EndY=9 EndZ=0
  constraints (8):
    c: Coincident(g2,g0)
    c: Coincident(g2,g1)
    c: Horizontal(g2)
    c: Equal(g0,g1)
    c: Diameter(g0) = 2.5  'screw_hole'
    c: DistanceY(g-1,g0) = 9  'placement_width'
    c: DistanceX(g-1,g0) = 19.5  'placement_screw1'
    c: DistanceX(g-1,g1) = 30.5  'placement_screw2'
FEATURE [PartDesign::Pocket] Pocket049  label="hhp_tf_screws"
  BaseFeature = -> Pocket048
  Direction = (0,0,-1)
  Length = 4.5
  Length2 = 5
  Profile = -> Sketch117
  ReferenceAxis = -> Sketch117 [N_Axis]
  Refine = true
  SideType = 0
  Suppressed = false
  Type = 0
  Type2 = 0
  expr: Length = <<block_params>>.screw_drill_depth
FEATURE [PartDesign::Body] Body060  label="heater_heatsink_ptc_tfuse"
  AllowCompound = false
  Group = -> [Clone026,Sketch116,Pocket048,Sketch117,Pocket049]
  Origin = -> Origin196
  Tip = -> Pocket049
FEATURE [App::DocumentObjectGroup] Group020  label="heater_block"
  Group = -> [Body055,Body056,Body057,Body058,Body060]
FEATURE [App::Point] Origin181  label="Origin"
  Role = Origin
FEATURE [App::Point] Origin180  label="Origin"
  Role = Origin
FEATURE [App::Point] Origin179  label="Origin"
  Role = Origin
FEATURE [App::Point] Origin178  label="Origin"
  Role = Origin
FEATURE [Part::Extrusion] Extrude004  label="hht_text_r_screws"
  Base = -> ShapeString004
  Dir = (0,0,-1)
  DirMode = 2
  FaceMakerClass = Part::FaceMakerBullseye
  FaceMakerMode = 3
  InnerWireTaper = 1
  LengthFwd = 0.2
  LengthRev = 0
  Reversed = true
  Solid = false
  Symmetric = false
FEATURE [Part::Extrusion] Extrude005  label="hht_text_r_ptc"
  Base = -> ShapeString005
  Dir = (0,0,-1)
  DirMode = 2
  FaceMakerClass = Part::FaceMakerBullseye
  FaceMakerMode = 3
  InnerWireTaper = 1
  LengthFwd = 0.2
  LengthRev = 0
  Reversed = true
  Solid = true
  Symmetric = false
FEATURE [Part::Extrusion] Extrude006  label="hht_text_r_tswitch"
  Base = -> ShapeString006
  Dir = (0,0,-1)
  DirMode = 2
  FaceMakerClass = Part::FaceMakerBullseye
  FaceMakerMode = 3
  InnerWireTaper = 1
  LengthFwd = 0.2
  LengthRev = 0
  Reversed = true
  Solid = true
  Symmetric = false
FEATURE [Sketcher::SketchObject] Sketch118  label="hhtb_base_marking_s"
  ArcFitTolerance = 1e-06
  AttachmentOffset = pos=(0,0,-5) rot=(0,0,1;0rad)
  AttachmentSupport = -> [Origin036]
  ExternalTypes = [0]
  FullyConstrained = true
  MakeInternals = false
  MapMode = 5
  Placement = pos=(0,0,-5) rot=(0,0,1;0rad)
  _ExternalGeoVersion = 1
  expr: .AttachmentOffset.Base.z = -<<hhtb_base_face>>.Length
  sketch-geometry (18):
    g0: LineSegment StartX=-0.2 StartY=26.5 StartZ=0 EndX=-0.2 EndY=1.5 EndZ=0
    g1: LineSegment StartX=-0.2 StartY=1.5 StartZ=0 EndX=0.2 EndY=1.5 EndZ=0
    g2: LineSegment StartX=0.2 StartY=1.5 StartZ=0 EndX=0.2 EndY=26.5 EndZ=0
    g3: LineSegment StartX=0.2 StartY=26.5 StartZ=0 EndX=-0.2 EndY=26.5 EndZ=0
    g4: LineSegment StartX=1.5 StartY=0.2 StartZ=0 EndX=1.5 EndY=-0.2 EndZ=0
    g5: LineSegment StartX=1.5 StartY=-0.2 StartZ=0 EndX=26.5 EndY=-0.2 EndZ=0
    g6: LineSegment StartX=26.5 StartY=-0.2 StartZ=0 EndX=26.5 EndY=0.2 EndZ=0
    g7: LineSegment StartX=26.5 StartY=0.2 StartZ=0 EndX=1.5 EndY=0.2 EndZ=0
    g8: LineSegment StartX=-26.5 StartY=0.2 StartZ=0 EndX=-26.5 EndY=-0.2 EndZ=0
    g9: LineSegment StartX=-26.5 StartY=-0.2 StartZ=0 EndX=-1.5 EndY=-0.2 EndZ=0
    g10: LineSegment StartX=-1.5 StartY=-0.2 StartZ=0 EndX=-1.5 EndY=0.2 EndZ=0
    g11: LineSegment StartX=-1.5 StartY=0.2 StartZ=0 EndX=-26.5 EndY=0.2 EndZ=0
    g12: LineSegment StartX=-0.2 StartY=-1.5 StartZ=0 EndX=-0.2 EndY=-26.5 EndZ=0
    g13: LineSegment StartX=-0.2 StartY=-26.5 StartZ=0 EndX=0.2 EndY=-26.5 EndZ=0
    g14: LineSegment StartX=0.2 StartY=-26.5 StartZ=0 EndX=0.2 EndY=-1.5 EndZ=0
    g15: LineSegment StartX=0.2 StartY=-1.5 StartZ=0 EndX=-0.2 EndY=-1.5 EndZ=0
    g16: Circle [constr] CenterX=0 CenterY=0 CenterZ=0 NormalX=0 NormalY=0 NormalZ=1 AngleXU=0 Radius=1.5
    g17: GeomPoint [constr] X=0 Y=0.2 Z=0
  constraints (48):
    c: Coincident(g0,g1)
    c: Coincident(g1,g2)
    c: Coincident(g2,g3)
    c: Coincident(g3,g0)
    c: Vertical(g0)
    c: Vertical(g2)
    c: Horizontal(g1)
    c: Coincident(g4,g5)
    c: Coincident(g5,g6)
    c: Coincident(g6,g7)
    c: Coincident(g7,g4)
    c: Vertical(g4)
    c: Horizontal(g5)
    c: Horizontal(g7)
    c: Coincident(g8,g9)
    c: Coincident(g9,g10)
    c: Coincident(g10,g11)
    c: Coincident(g11,g8)
    c: Vertical(g10)
    c: Horizontal(g9)
    c: Horizontal(g11)
    c: Coincident(g12,g13)
    c: Coincident(g13,g14)
    c: Coincident(g14,g15)
    c: Coincident(g15,g12)
    c: Vertical(g12)
    c: Vertical(g14)
    c: Horizontal(g15)
    c: Symmetric(g5,g6,g-1)
    c: Symmetric(g8,g8,g-1)
    c: Symmetric(g12,g13,g-2)
    c: Symmetric(g0,g2,g-2)
    c: Equal(g1,g10)
    c: Equal(g10,g4)
    c: Equal(g4,g15)
    c: Coincident(g16,g-1)
    c: Tangent(g1,g16)
    c: Tangent(g16,g15)
    c: Tangent(g4,g16)
    c: Tangent(g16,g10)
    c: Equal(g11,g0)
    c: Equal(g0,g7)
    c: Equal(g7,g14)
    c: Distance(g15,g15) = 0.4  'mark_width'
    c: PointOnObject(g17,g-2)
    c: Distance(g17,g-1) = 0.2  'mark_depth'
    c: Diameter(g16) = 3  'center_clear'
    c: DistanceY(g12,g12) = 25  'mark_length'
FEATURE [PartDesign::Pocket] Pocket050  label="hhtb_base_marking"
  BaseFeature = -> Chamfer026
  Direction = (0,0,-1)
  Length = 0.2
  Length2 = 5
  Profile = -> Sketch118
  ReferenceAxis = -> Sketch118 [N_Axis]
  Refine = true
  Reversed = true
  SideType = 0
  Suppressed = false
  Type = 0
  Type2 = 0
  expr: Length = <<hhtb_base_marking_s>>.Constraints.mark_depth
FEATURE [PartDesign::Body] Body036  label="heater_heatsink_template_base"
  AllowCompound = false
  Group = -> [Sketch059,Pad021,Sketch060,Pad022,PolarPattern001,Chamfer021,Chamfer022,Fillet013,Chamfer026,Sketch118,Pocket050]
  Origin = -> Origin036
  Tip = -> Pocket050
FEATURE [PartDesign::FeatureBase] Clone015  label="hhdg_cln"
  BaseFeature = -> Body036
  Suppressed = false
FEATURE [PartDesign::Pocket] Pocket015  label="hhdg_holes"
  BaseFeature = -> Clone015
  Direction = (0,0,-1)
  Length = 5
  Length2 = 5
  Profile = -> Sketch061
  ReferenceAxis = -> Sketch061 [N_Axis]
  SideType = 0
  Suppressed = false
  Type = 1
  Type2 = 0
FEATURE [PartDesign::FeatureBase] Clone016  label="hht_ptc_1-16_cln"
  BaseFeature = -> Body036
  Suppressed = false
FEATURE [PartDesign::Pocket] Pocket016  label="hht_ptc_1-16_pocket"
  BaseFeature = -> Clone016
  Direction = (0,0,-1)
  Length = 5
  Length2 = 5
  Profile = -> Sketch062
  ReferenceAxis = -> Sketch062 [N_Axis]
  SideType = 0
  Suppressed = false
  Type = 1
  Type2 = 0
FEATURE [PartDesign::FeatureBase] Clone017  label="hht_tswitch_1-16_cln"
  BaseFeature = -> Body036
  Suppressed = false
FEATURE [PartDesign::Pocket] Pocket018  label="hht_tswitch_1-16_pocket"
  BaseFeature = -> Clone017
  Direction = (0,0,-1)
  Length = 5
  Length2 = 5
  Profile = -> Sketch064
  ReferenceAxis = -> Sketch064 [N_Axis]
  SideType = 0
  Suppressed = false
  Type = 1
  Type2 = 0
FEATURE [PartDesign::FeatureBase] Clone020  label="hht_ptc_1-8_cln"
  BaseFeature = -> Body036
  Suppressed = false
FEATURE [PartDesign::FeatureBase] Clone021  label="hht_tswitch_1-8_cln"
  BaseFeature = -> Body036
  Suppressed = false
FEATURE [PartDesign::Pocket] Pocket027  label="hht_ptc_1-8_pocket"
  BaseFeature = -> Clone020
  Direction = (0,0,-1)
  Length = 5
  Length2 = 5
  Profile = -> Sketch080
  ReferenceAxis = -> Sketch080 [N_Axis]
  SideType = 0
  Suppressed = false
  Type = 1
  Type2 = 0
FEATURE [PartDesign::Pocket] Pocket028  label="hht_tswitch_1-8_pocket"
  BaseFeature = -> Clone021
  Direction = (0,0,-1)
  Length = 5
  Length2 = 5
  Profile = -> Sketch081
  ReferenceAxis = -> Sketch081 [N_Axis]
  SideType = 0
  Suppressed = false
  Type = 1
  Type2 = 0
FEATURE [PartDesign::Chamfer] Chamfer036  label="hhdg_holes_face_chmf"
  Angle = 45
  Base = -> Pocket015 [Edge42,Edge37,Edge23,Edge32]
  BaseFeature = -> Pocket015
  ChamferType = 0
  FlipDirection = false
  Size = 0.6
  Size2 = 1
  SupportTransform = false
  Suppressed = false
  UseAllEdges = false
  expr: Size = <<template_params>>.drill_chamfer_face
FEATURE [PartDesign::Chamfer] Chamfer041  label="hhdg_holes_inner_chmf"
  Angle = 45
  Base = -> Chamfer036 [Edge128,Edge86,Edge132,Edge130]
  BaseFeature = -> Chamfer036
  ChamferType = 0
  FlipDirection = false
  Refine = true
  Size = 0.4
  Size2 = 1
  SupportTransform = false
  Suppressed = false
  UseAllEdges = false
  expr: Size = <<template_params>>.drill_chamfer_inner
FEATURE [PartDesign::Body] Body037  label="heater_heatsink_drill_guide_mounted"
  AllowCompound = false
  Group = -> [Clone015,Sketch061,Pocket015,Chamfer036,Chamfer041]
  Origin = -> Origin037
  Tip = -> Chamfer041
FEATURE [Part::Cut] Cut  label="heater_heatsink_drill_guide_mounted_labeled"
  Base = -> Body037
  Tool = -> Extrude004
FEATURE [App::Point] Origin199  label="Origin200"
  Role = Origin
FEATURE [PartDesign::FeatureBase] Clone027  label="hhdg_ptc_cln"
  BaseFeature = -> Cut
  Suppressed = false
FEATURE [Sketcher::SketchObject] Sketch119  label="hhdg_ptc_holes_s"
  ArcFitTolerance = 1e-06
  AttachmentSupport = -> [Origin198]
  ExternalTypes = [0]
  FullyConstrained = true
  MakeInternals = false
  MapMode = 5
  _ExternalGeoVersion = 1
  expr: .Constraints.block_width = <<block_params>>.heatsink_width
  expr: .Constraints.hole_diam = <<template_params>>.drill_hole_diam
  expr: .Constraints.placement_length = <<block_params>>.ptc_placement_length
  expr: .Constraints.placement_width = <<block_params>>.ptc_placement_width
  expr: .Constraints.spacing_length = <<block_params>>.ptc_screw_spacing_length
  expr: .Constraints.spacing_width = <<block_params>>.ptc_screw_spacing_width
  sketch-geometry (15):
    g0: LineSegment [constr] StartX=-25 StartY=25 StartZ=0 EndX=-25 EndY=-25 EndZ=0
    g1: LineSegment [constr] StartX=-25 StartY=-25 StartZ=0 EndX=25 EndY=-25 EndZ=0
    g2: LineSegment [constr] StartX=25 StartY=-25 StartZ=0 EndX=25 EndY=25 EndZ=0
    g3: LineSegment [constr] StartX=25 StartY=25 StartZ=0 EndX=-25 EndY=25 EndZ=0
    g4: Circle [constr] CenterX=1e-16 CenterY=0 CenterZ=0 NormalX=0 NormalY=0 NormalZ=1 AngleXU=0 Radius=25
    g5: Circle [constr] CenterX=6.2e-15 CenterY=3.5 CenterZ=0 NormalX=0 NormalY=0 NormalZ=1 AngleXU=0 Radius=12.1
    g6: Circle [constr] CenterX=6.2e-15 CenterY=3.5 CenterZ=0 NormalX=0 NormalY=0 NormalZ=1 AngleXU=0 Radius=12.5
    g7: LineSegment [constr] StartX=-12.5 StartY=15.6 StartZ=0 EndX=-12.5 EndY=-8.6 EndZ=0
    g8: LineSegment [constr] StartX=-12.5 StartY=-8.6 StartZ=0 EndX=12.5 EndY=-8.6 EndZ=0
    g9: LineSegment [constr] StartX=12.5 StartY=-8.6 StartZ=0 EndX=12.5 EndY=15.6 EndZ=0
    g10: LineSegment [constr] StartX=12.5 StartY=15.6 StartZ=0 EndX=-12.5 EndY=15.6 EndZ=0
    g11: Circle CenterX=-12.5 CenterY=15.6 CenterZ=0 NormalX=0 NormalY=0 NormalZ=1 AngleXU=0 Radius=1
    g12: Circle CenterX=12.5 CenterY=15.6 CenterZ=0 NormalX=0 NormalY=0 NormalZ=1 AngleXU=0 Radius=1
    g13: Circle CenterX=-12.5 CenterY=-8.6 CenterZ=0 NormalX=0 NormalY=0 NormalZ=1 AngleXU=0 Radius=1
    g14: Circle CenterX=12.5 CenterY=-8.6 CenterZ=0 NormalX=0 NormalY=0 NormalZ=1 AngleXU=0 Radius=1
  constraints (39):
    c: Coincident(g0,g1)
    c: Coincident(g1,g2)
    c: Coincident(g2,g3)
    c: Coincident(g3,g0)
    c: Vertical(g0)
    c: Vertical(g2)
    c: Horizontal(g1)
    c: Horizontal(g3)
    c: Coincident(g4,g-1)
    c: Tangent(g4,g3)
    c: Tangent(g4,g1)
    c: Tangent(g4,g2)
    c: Tangent(g4,g0)
    c: Diameter(g4) = 50  'block_width'
    c: Coincident(g6,g5)
    c: Coincident(g7,g8)
    c: Coincident(g8,g9)
    c: Coincident(g9,g10)
    c: Coincident(g10,g7)
    c: Vertical(g7)
    c: Vertical(g9)
    c: Horizontal(g8)
    c: Horizontal(g10)
    c: Tangent(g6,g9)
    c: Tangent(g6,g7)
    c: Tangent(g5,g10)
    c: Tangent(g5,g8)
    c: Diameter(g6) = 25  'spacing_length'
    c: Diameter(g5) = 24.2  'spacing_width'
    c: DistanceY(g1,g5) = 28.5  'placement_width'
    c: DistanceX(g5,g1) = 25  'placement_length'
    c: Coincident(g11,g7)
    c: Coincident(g12,g9)
    c: Coincident(g13,g7)
    c: Coincident(g14,g8)
    c: Equal(g14,g13)
    c: Equal(g13,g11)
    c: Equal(g11,g12)
    c: Diameter(g13) = 2  'hole_diam'
FEATURE [PartDesign::Pocket] Pocket051  label="hhdf_ptc_holes"
  BaseFeature = -> Clone027
  Direction = (0,0,-1)
  Length = 5
  Length2 = 5
  Profile = -> Sketch119
  ReferenceAxis = -> Sketch119 [N_Axis]
  Refine = true
  SideType = 0
  Suppressed = false
  Type = 1
  Type2 = 0
FEATURE [PartDesign::Chamfer] Chamfer042  label="hhdg_ptc_holes_face_chmf"
  Angle = 45
  Base = -> Pocket051 [Edge124,Edge219,Edge66,Edge60]
  BaseFeature = -> Pocket051
  ChamferType = 0
  FlipDirection = false
  Refine = true
  Size = 0.6
  Size2 = 1
  SupportTransform = false
  Suppressed = false
  UseAllEdges = false
  expr: Size = <<template_params>>.drill_chamfer_face
FEATURE [PartDesign::Chamfer] Chamfer043  label="hhdg_ptc_holes_inner_chmf"
  Angle = 45
  Base = -> Chamfer042 [Edge524,Edge580,Edge582,Edge584]
  BaseFeature = -> Chamfer042
  ChamferType = 0
  FlipDirection = false
  Refine = true
  Size = 0.4
  Size2 = 1
  SupportTransform = false
  Suppressed = false
  UseAllEdges = false
  expr: Size = <<template_params>>.drill_chamfer_inner
FEATURE [PartDesign::Body] Body061  label="heater_heatsink_drill_guide_ptc"
  AllowCompound = false
  Group = -> [Clone027,Sketch119,Pocket051,Chamfer042,Chamfer043]
  Origin = -> Origin198
  Tip = -> Chamfer043
FEATURE [Part::Feature] Extrude007  label="hht_text_l_ptc"
  Placement = pos=(15,0,0) rot=(0,0,1;0rad)
  shape: bbox 8.532 x 3.508 x 0.2 mm, 64 faces, 3 solids (baked)
FEATURE [Part::Feature] Extrude008  label="hht_text_l_tswitch"
  Placement = pos=(21.5,0,0) rot=(0,0,1;0rad)
  shape: bbox 17.78 x 3.565 x 0.2 mm, 153 faces, 8 solids (baked)
FEATURE [Part::Part2DObjectPython] ShapeString  label="hht_text_tfuse_s"  # Draft 2D object (typed FeaturePython)
  FontFile = <userpath>/Documents/fdm/fdm_fonts/Overpass/static/Overpass-Bold.ttf
  Fuse = false
  Justification = 6
  JustificationReference = 0
  KeepLeftMargin = true
  MakeFace = true
  ObliqueAngle = 0
  Placement = pos=(-2,22,-5) rot=(0,1,0;3.14159rad)
  ScaleToSize = false
  Size = 4
  String = TFuse
  Tracking = 0
FEATURE [Part::Extrusion] Extrude  label="hht_text_r_tfuse"
  Base = -> ShapeString
  Dir = (0,0,-1)
  DirMode = 2
  FaceMakerClass = Part::FaceMakerBullseye
  FaceMakerMode = 3
  InnerWireTaper = 0
  LengthFwd = 0.2
  LengthRev = 0
  Reversed = true
  Solid = true
  Symmetric = false
FEATURE [Part::Feature] Extrude009  label="hht_text_l_tfuse"
  Placement = pos=(19,0,0) rot=(0,0,1;0rad)
  shape: bbox 13.27 x 3.458 x 0.2 mm, 97 faces, 5 solids (baked)
FEATURE [Part::Cut] Cut001  label="heater_heatsink_drill_guide_ptc_labeled"
  Base = -> Body061
  Tool = -> Extrude007
FEATURE [App::Point] Origin201  label="Origin203"
  Role = Origin
FEATURE [PartDesign::FeatureBase] Clone028  label="hhdg_tswitch_cln"
  BaseFeature = -> Body061
  Suppressed = false
FEATURE [App::Point] Origin203  label="Origin205"
  Role = Origin
FEATURE [PartDesign::FeatureBase] Clone029  label="hhdg_tfuse_cln"
  BaseFeature = -> Body061
  Suppressed = false
FEATURE [Sketcher::SketchObject] Sketch120  label="hhdg_tswitch_holes_s"
  ArcFitTolerance = 1e-06
  AttachmentSupport = -> [Origin200]
  ExternalTypes = [0]
  FullyConstrained = true
  MakeInternals = false
  MapMode = 5
  _ExternalGeoVersion = 1
  expr: .Constraints.block_width = <<block_params>>.heatsink_width
  expr: .Constraints.hole_diam = <<template_params>>.drill_hole_diam
  expr: .Constraints.placement_length = <<block_params>>.tswitch_placement_length
  expr: .Constraints.placement_width = <<block_params>>.tswitch_placement_width
  expr: .Constraints.spacing_length = <<block_params>>.tswitch_screw_spacing_length
  expr: .Constraints.spacing_width = <<block_params>>.tswitch_screw_spacing_width
  sketch-geometry (15):
    g0: LineSegment [constr] StartX=-25 StartY=25 StartZ=0 EndX=-25 EndY=-25 EndZ=0
    g1: LineSegment [constr] StartX=-25 StartY=-25 StartZ=0 EndX=25 EndY=-25 EndZ=0
    g2: LineSegment [constr] StartX=25 StartY=-25 StartZ=0 EndX=25 EndY=25 EndZ=0
    g3: LineSegment [constr] StartX=25 StartY=25 StartZ=0 EndX=-25 EndY=25 EndZ=0
    g4: Circle [constr] CenterX=0 CenterY=0 CenterZ=0 NormalX=0 NormalY=0 NormalZ=1 AngleXU=0 Radius=25
    g5: Circle [constr] CenterX=2.9e-15 CenterY=-16 CenterZ=0 NormalX=0 NormalY=0 NormalZ=1 AngleXU=0 Radius=5.65
    g6: Circle [constr] CenterX=2.9e-15 CenterY=-16 CenterZ=0 NormalX=0 NormalY=0 NormalZ=1 AngleXU=0 Radius=5.5
    g7: LineSegment [constr] StartX=-5.5 StartY=-10.35 StartZ=0 EndX=-5.5 EndY=-21.65 EndZ=0
    g8: LineSegment [constr] StartX=-5.5 StartY=-21.65 StartZ=0 EndX=5.5 EndY=-21.65 EndZ=0
    g9: LineSegment [constr] StartX=5.5 StartY=-21.65 StartZ=0 EndX=5.5 EndY=-10.35 EndZ=0
    g10: LineSegment [constr] StartX=5.5 StartY=-10.35 StartZ=0 EndX=-5.5 EndY=-10.35 EndZ=0
    g11: Circle CenterX=5.5 CenterY=-10.35 CenterZ=0 NormalX=0 NormalY=0 NormalZ=1 AngleXU=0 Radius=1
    g12: Circle CenterX=-5.5 CenterY=-10.35 CenterZ=0 NormalX=0 NormalY=0 NormalZ=1 AngleXU=0 Radius=1
    g13: Circle CenterX=-5.5 CenterY=-21.65 CenterZ=0 NormalX=0 NormalY=0 NormalZ=1 AngleXU=0 Radius=1
    g14: Circle CenterX=5.5 CenterY=-21.65 CenterZ=0 NormalX=0 NormalY=0 NormalZ=1 AngleXU=0 Radius=1
  constraints (39):
    c: Coincident(g0,g1)
    c: Coincident(g1,g2)
    c: Coincident(g2,g3)
    c: Coincident(g3,g0)
    c: Vertical(g0)
    c: Vertical(g2)
    c: Horizontal(g1)
    c: Horizontal(g3)
    c: Coincident(g4,g-1)
    c: Tangent(g4,g3)
    c: Tangent(g4,g2)
    c: Tangent(g4,g1)
    c: Tangent(g4,g0)
    c: Diameter(g4) = 50  'block_width'
    c: Coincident(g6,g5)
    c: Coincident(g7,g8)
    c: Coincident(g8,g9)
    c: Coincident(g9,g10)
    c: Coincident(g10,g7)
    c: Vertical(g7)
    c: Vertical(g9)
    c: Horizontal(g8)
    c: Horizontal(g10)
    c: Tangent(g6,g9)
    c: Tangent(g6,g7)
    c: Tangent(g5,g10)
    c: Tangent(g5,g8)
    c: Diameter(g6) = 11  'spacing_length'
    c: Diameter(g5) = 11.3  'spacing_width'
    c: Coincident(g11,g9)
    c: Coincident(g12,g7)
    c: Coincident(g13,g7)
    c: Coincident(g14,g8)
    c: Equal(g12,g11)
    c: Equal(g11,g14)
    c: Equal(g14,g13)
    c: Diameter(g13) = 2  'hole_diam'
    c: DistanceY(g1,g5) = 9  'placement_width'
    c: DistanceX(g5,g1) = 25  'placement_length'
FEATURE [PartDesign::Pocket] Pocket052  label="hhdg_tswitch_holes"
  BaseFeature = -> Clone028
  Direction = (0,0,-1)
  Length = 5
  Length2 = 5
  Profile = -> Sketch120
  ReferenceAxis = -> Sketch120 [N_Axis]
  Refine = true
  SideType = 0
  Suppressed = false
  Type = 1
  Type2 = 0
FEATURE [PartDesign::Chamfer] Chamfer044  label="hhdg_tswitch_holes_face_chmf"
  Angle = 45
  Base = -> Pocket052 [Edge66,Edge73,Edge67,Edge60]
  BaseFeature = -> Pocket052
  ChamferType = 0
  FlipDirection = false
  Refine = true
  Size = 0.6
  Size2 = 1
  SupportTransform = false
  Suppressed = false
  UseAllEdges = false
FEATURE [PartDesign::Chamfer] Chamfer045  label="hhdg_tswitch_holes_inner_chmf"
  Angle = 45
  Base = -> Chamfer044 [Edge536,Edge600,Edge602,Edge604]
  BaseFeature = -> Chamfer044
  ChamferType = 0
  FlipDirection = false
  Refine = true
  Size = 0.4
  Size2 = 1
  SupportTransform = false
  Suppressed = false
  UseAllEdges = false
FEATURE [PartDesign::Body] Body062  label="heater_heatsink_drill_guide_tswitch"
  AllowCompound = false
  Group = -> [Clone028,Sketch120,Pocket052,Chamfer044,Chamfer045]
  Origin = -> Origin200
  Tip = -> Chamfer045
FEATURE [Part::Cut] Cut002  label="heater_heatsink_drill_guide_tswitch_labeled"
  Base = -> Body062
  Tool = -> Extrude008
FEATURE [Sketcher::SketchObject] Sketch121  label="hhdg_tfuse_holes_s"
  ArcFitTolerance = 1e-06
  AttachmentSupport = -> [Origin202]
  ExternalTypes = [0]
  FullyConstrained = true
  MakeInternals = false
  MapMode = 5
  _ExternalGeoVersion = 1
  expr: .Constraints.block_width = <<block_params>>.heatsink_width
  expr: .Constraints.hole_diam = <<template_params>>.drill_hole_diam
  expr: .Constraints.placement_screw1 = <<block_params>>.tfuse_placement_length - <<block_params>>.tfuse_screw_spacing / 2
  expr: .Constraints.placement_screw2 = <<block_params>>.tfuse_placement_length + <<block_params>>.tfuse_screw_spacing / 2
  expr: .Constraints.placement_width = <<block_params>>.tfuse_placement_width
  sketch-geometry (8):
    g0: LineSegment [constr] StartX=-25 StartY=25 StartZ=0 EndX=-25 EndY=-25 EndZ=0
    g1: LineSegment [constr] StartX=-25 StartY=-25 StartZ=0 EndX=25 EndY=-25 EndZ=0
    g2: LineSegment [constr] StartX=25 StartY=-25 StartZ=0 EndX=25 EndY=25 EndZ=0
    g3: LineSegment [constr] StartX=25 StartY=25 StartZ=0 EndX=-25 EndY=25 EndZ=0
    g4: Circle [constr] CenterX=0 CenterY=0 CenterZ=0 NormalX=0 NormalY=0 NormalZ=1 AngleXU=0 Radius=25
    g5: Circle CenterX=-5.5 CenterY=-16 CenterZ=0 NormalX=0 NormalY=0 NormalZ=1 AngleXU=0 Radius=1
    g6: Circle CenterX=5.5 CenterY=-16 CenterZ=0 NormalX=0 NormalY=0 NormalZ=1 AngleXU=0 Radius=1
    g7: LineSegment [constr] StartX=-5.5 StartY=-16 StartZ=0 EndX=5.5 EndY=-16 EndZ=0
  constraints (22):
    c: Coincident(g0,g1)
    c: Coincident(g1,g2)
    c: Coincident(g2,g3)
    c: Coincident(g3,g0)
    c: Vertical(g0)
    c: Vertical(g2)
    c: Horizontal(g1)
    c: Horizontal(g3)
    c: Coincident(g4,g-1)
    c: Tangent(g4,g2)
    c: Tangent(g4,g3)
    c: Tangent(g4,g0)
    c: Tangent(g4,g1)
    c: Diameter(g4) = 50  'block_width'
    c: Coincident(g7,g5)
    c: Coincident(g7,g6)
    c: Horizontal(g7)
    c: Equal(g6,g5)
    c: Diameter(g6) = 2  'hole_diam'
    c: DistanceY(g1,g6) = 9  'placement_width'
    c: DistanceX(g6,g1) = 19.5  'placement_screw1'
    c: DistanceX(g5,g1) = 30.5  'placement_screw2'
FEATURE [PartDesign::Pocket] Pocket053  label="hhdg_tfuse_holes"
  BaseFeature = -> Clone029
  Direction = (0,0,-1)
  Length = 5
  Length2 = 5
  Profile = -> Sketch121
  ReferenceAxis = -> Sketch121 [N_Axis]
  Refine = true
  SideType = 0
  Suppressed = false
  Type = 1
  Type2 = 0
FEATURE [PartDesign::Chamfer] Chamfer046  label="hhdg_tfuse_holes_face_chmf"
  Angle = 45
  Base = -> Pocket053 [Edge68,Edge58]
  BaseFeature = -> Pocket053
  ChamferType = 0
  FlipDirection = false
  Refine = true
  Size = 0.6
  Size2 = 1
  SupportTransform = false
  Suppressed = false
  UseAllEdges = false
  expr: Size = <<template_params>>.drill_chamfer_face
FEATURE [PartDesign::Chamfer] Chamfer047  label="hhdg_tfuse_holes_inner_chmf"
  Angle = 45
  Base = -> Chamfer046 [Edge594,Edge530]
  BaseFeature = -> Chamfer046
  ChamferType = 0
  FlipDirection = false
  Refine = true
  Size = 0.4
  Size2 = 1
  SupportTransform = false
  Suppressed = false
  UseAllEdges = false
  expr: Size = <<template_params>>.drill_chamfer_inner
FEATURE [PartDesign::Body] Body063  label="heater_heatsink_drill_guide_tfuse"
  AllowCompound = false
  Group = -> [Clone029,Sketch121,Pocket053,Chamfer046,Chamfer047]
  Origin = -> Origin202
  Tip = -> Chamfer047
FEATURE [Part::Cut] Cut003  label="heater_heatsink_drill_guide_tfuse_labeled"
  Base = -> Body063
  Tool = -> Extrude009
FEATURE [PartDesign::Chamfer] Chamfer048  label="hht_ptc_1-16_face_chmf"
  Angle = 45
  Base = -> Pocket016 [Edge44,Edge38,Edge32,Edge26,Edge31,Edge27,Edge25,Edge45,Edge43,Edge39,Edge37,Edge33]
  BaseFeature = -> Pocket016
  ChamferType = 0
  FlipDirection = false
  Refine = true
  Size = 0.199
  Size2 = 1
  SupportTransform = false
  Suppressed = false
  UseAllEdges = false
FEATURE [PartDesign::Body] Body038  label="heater_heatsink_template_ptc_1-16"
  AllowCompound = false
  Group = -> [Clone016,Sketch062,Pocket016,Chamfer048]
  Origin = -> Origin038
  Tip = -> Chamfer048
FEATURE [PartDesign::Chamfer] Chamfer049  label="hht_tswitch_1-16_face_chmf"
  Angle = 45
  Base = -> Pocket018 [Edge29,Edge31,Edge32,Edge37,Edge38,Edge39,Edge40,Edge28,Edge36,Edge30]
  BaseFeature = -> Pocket018
  ChamferType = 0
  FlipDirection = false
  Refine = true
  Size = 0.199
  Size2 = 1
  SupportTransform = false
  Suppressed = false
  UseAllEdges = false
FEATURE [PartDesign::Body] Body039  label="heater_heatsink_template_tswitch_1-16"
  AllowCompound = false
  Group = -> [Clone017,Sketch064,Pocket018,Chamfer049]
  Origin = -> Origin039
  Tip = -> Chamfer049
FEATURE [PartDesign::Chamfer] Chamfer050  label="hht_ptc_1-8_face_chmf"
  Angle = 45
  Base = -> Pocket027 [Edge44,Edge38,Edge32,Edge26]
  BaseFeature = -> Pocket027
  ChamferType = 0
  FlipDirection = false
  Refine = true
  Size = 0.2
  Size2 = 1
  SupportTransform = false
  Suppressed = false
  UseAllEdges = false
FEATURE [PartDesign::Body] Body043  label="heater_heatsink_template_ptc_1-8"
  AllowCompound = false
  Group = -> [Clone020,Sketch080,Pocket027,Chamfer050]
  Origin = -> Origin043
  Tip = -> Chamfer050
FEATURE [PartDesign::Chamfer] Chamfer051  label="hht_tswtich_1-8_face_chmf"
  Angle = 45
  Base = -> Pocket028 [Edge29,Edge39]
  BaseFeature = -> Pocket028
  ChamferType = 0
  FlipDirection = false
  Refine = true
  Size = 0.2
  Size2 = 1
  SupportTransform = false
  Suppressed = false
  UseAllEdges = false
FEATURE [PartDesign::Body] Body044  label="heater_heatsink_template_tswitch_1-8"
  AllowCompound = false
  Group = -> [Clone021,Sketch081,Pocket028,Chamfer051]
  Origin = -> Origin044
  Tip = -> Chamfer051
FEATURE [App::Point] Origin205  label="Origin208"
  Role = Origin
FEATURE [PartDesign::FeatureBase] Clone030  label="hht_tfuse_1-16_cln"
  BaseFeature = -> Body036
  Suppressed = false
FEATURE [App::Point] Origin207  label="Origin211"
  Role = Origin
FEATURE [PartDesign::FeatureBase] Clone031  label="hht_tfuse_1-8_cln"
  BaseFeature = -> Body036
  Suppressed = false
FEATURE [Sketcher::SketchObject] Sketch122  label="hht_tfuse_1-16_pocket_s"
  ArcFitTolerance = 1e-06
  AttachmentSupport = -> [Origin204]
  ExternalTypes = [0]
  FullyConstrained = true
  MakeInternals = false
  MapMode = 5
  _ExternalGeoVersion = 1
  expr: .Constraints.block_width = <<block_params>>.heatsink_width
  expr: .Constraints.corner_length = <<block_params>>.tfuse_pocket_length + 2 * <<template_params>>.router_dogbone
  expr: .Constraints.corner_width = <<block_params>>.tfuse_pocket_width + 2 * <<template_params>>.router_dogbone
  expr: .Constraints.edge_length = <<block_params>>.tfuse_pocket_length + 2 * <<template_params>>.router_offset_1_16
  expr: .Constraints.edge_width = <<block_params>>.tfuse_pocket_width + 2 * <<template_params>>.router_offset_1_16
  expr: .Constraints.placement_length = <<block_params>>.tfuse_placement_length
  expr: .Constraints.placement_width = <<block_params>>.tfuse_placement_width
  expr: .Constraints.router_bushing = <<template_params>>.router_bushing
  sketch-geometry (21):
    g0: LineSegment [constr] StartX=-25 StartY=25 StartZ=0 EndX=-25 EndY=-25 EndZ=0
    g1: LineSegment [constr] StartX=-25 StartY=-25 StartZ=0 EndX=25 EndY=-25 EndZ=0
    g2: LineSegment [constr] StartX=25 StartY=-25 StartZ=0 EndX=25 EndY=25 EndZ=0
    g3: LineSegment [constr] StartX=25 StartY=25 StartZ=0 EndX=-25 EndY=25 EndZ=0
    g4: Circle [constr] CenterX=0 CenterY=0 CenterZ=0 NormalX=0 NormalY=0 NormalZ=1 AngleXU=0 Radius=25
    g5: Circle [constr] CenterX=-3e-16 CenterY=-16 CenterZ=0 NormalX=0 NormalY=0 NormalZ=1 AngleXU=0 Radius=6.1
    g6: LineSegment [constr] StartX=-11.9 StartY=-9.9 StartZ=0 EndX=-11.9 EndY=-22.1 EndZ=0
    g7: LineSegment [constr] StartX=-11.9 StartY=-22.1 StartZ=0 EndX=11.9 EndY=-22.1 EndZ=0
    g8: LineSegment [constr] StartX=11.9 StartY=-22.1 StartZ=0 EndX=11.9 EndY=-9.9 EndZ=0
    g9: LineSegment [constr] StartX=11.9 StartY=-9.9 StartZ=0 EndX=-11.9 EndY=-9.9 EndZ=0
    g10: Circle [constr] CenterX=-3e-16 CenterY=-16 CenterZ=0 NormalX=0 NormalY=0 NormalZ=1 AngleXU=0 Radius=11.9
    g11: Circle [constr] CenterX=-3e-16 CenterY=-16 CenterZ=0 NormalX=0 NormalY=0 NormalZ=1 AngleXU=0 Radius=9.175
    g12: Circle [constr] CenterX=-3e-16 CenterY=-16 CenterZ=0 NormalX=0 NormalY=0 NormalZ=1 AngleXU=0 Radius=14.975
    g13: ArcOfCircle CenterX=11.9 CenterY=-9.9 CenterZ=0 NormalX=0 NormalY=0 NormalZ=1 AngleXU=0 Radius=3.96875 StartAngle=5.59879 EndAngle=8.53837
    g14: ArcOfCircle CenterX=-11.9 CenterY=-9.9 CenterZ=0 NormalX=0 NormalY=0 NormalZ=1 AngleXU=0 Radius=3.96875 StartAngle=0.886404 EndAngle=3.82599
    g15: ArcOfCircle CenterX=11.9 CenterY=-22.1 CenterZ=0 NormalX=0 NormalY=0 NormalZ=1 AngleXU=0 Radius=3.96875 StartAngle=4.028 EndAngle=6.96758
    g16: ArcOfCircle CenterX=-11.9 CenterY=-22.1 CenterZ=0 NormalX=0 NormalY=0 NormalZ=1 AngleXU=0 Radius=3.96875 StartAngle=2.4572 EndAngle=5.39678
    g17: LineSegment StartX=-9.39095 StartY=-25.175 StartZ=0 EndX=9.39095 EndY=-25.175 EndZ=0
    g18: LineSegment StartX=14.975 StartY=-12.4091 StartZ=0 EndX=14.975 EndY=-19.5909 EndZ=0
    g19: LineSegment StartX=-14.975 StartY=-12.4091 StartZ=0 EndX=-14.975 EndY=-19.5909 EndZ=0
    g20: LineSegment StartX=-9.39095 StartY=-6.825 StartZ=0 EndX=9.39095 EndY=-6.825 EndZ=0
  constraints (59):
    c: Coincident(g0,g1)
    c: Coincident(g1,g2)
    c: Coincident(g2,g3)
    c: Coincident(g3,g0)
    c: Vertical(g0)
    c: Vertical(g2)
    c: Horizontal(g1)
    c: Horizontal(g3)
    c: Coincident(g4,g-1)
    c: Tangent(g4,g3)
    c: Tangent(g4,g2)
    c: Tangent(g1,g4)
    c: Tangent(g4,g0)
    c: Diameter(g4) = 50  'block_width'
    c: DistanceY(g1,g5) = 9  'placement_width'
    c: DistanceX(g5,g1) = 25  'placement_length'
    c: Coincident(g6,g7)
    c: Coincident(g7,g8)
    c: Coincident(g8,g9)
    c: Coincident(g9,g6)
    c: Vertical(g6)
    c: Vertical(g8)
    c: Horizontal(g7)
    c: Horizontal(g9)
    c: Tangent(g5,g9)
    c: Tangent(g5,g7)
    c: Coincident(g10,g5)
    c: Tangent(g10,g8)
    c: Tangent(g10,g6)
    c: Diameter(g5) = 12.2  'corner_width'
    c: Diameter(g10) = 23.8  'corner_length'
    c: Coincident(g11,g5)
    c: Coincident(g12,g5)
    c: Coincident(g13,g8)
    c: Coincident(g14,g6)
    c: Coincident(g15,g7)
    c: Coincident(g16,g6)
    c: Horizontal(g17)
    c: Vertical(g18)
    c: Vertical(g19)
    c: Horizontal(g20)
    c: Tangent(g11,g20)
    c: Tangent(g17,g11)
    c: Tangent(g18,g12)
    c: Tangent(g19,g12)
    c: Diameter(g14) = 7.9375  'router_bushing'
    c: Equal(g14,g13)
    c: Equal(g13,g15)
    c: Equal(g15,g16)
    c: Diameter(g11) = 18.35  'edge_width'
    c: Diameter(g12) = 29.95  'edge_length'
    c: Coincident(g20,g14)
    c: Coincident(g14,g19)
    c: Coincident(g16,g19)
    c: Coincident(g16,g17)
    c: Coincident(g15,g18)
    c: Coincident(g17,g15)
    c: Coincident(g18,g13)
    c: Coincident(g20,g13)
FEATURE [PartDesign::Pocket] Pocket054  label="hht_tfuse_1-16_pocket"
  BaseFeature = -> Clone030
  Direction = (0,0,-1)
  Length = 5
  Length2 = 5
  Profile = -> Sketch122
  ReferenceAxis = -> Sketch122 [N_Axis]
  Refine = true
  SideType = 0
  Suppressed = false
  Type = 1
  Type2 = 0
FEATURE [PartDesign::Chamfer] Chamfer052  label="hht_tfuse_1-16_face_chmf"
  Angle = 45
  Base = -> Pocket054 [Edge29,Edge31,Edge39,Edge40,Edge28,Edge32,Edge36,Edge37,Edge38,Edge30]
  BaseFeature = -> Pocket054
  ChamferType = 0
  FlipDirection = false
  Refine = true
  Size = 0.199
  Size2 = 1
  SupportTransform = false
  Suppressed = false
  UseAllEdges = false
FEATURE [PartDesign::Body] Body064  label="heater_heatsink_template_tfuse_1-16"
  AllowCompound = false
  Group = -> [Clone030,Sketch122,Pocket054,Chamfer052]
  Origin = -> Origin204
  Tip = -> Chamfer052
FEATURE [Sketcher::SketchObject] Sketch123  label="hht_tfuse_1-8_pocket_s"
  ArcFitTolerance = 1e-06
  AttachmentSupport = -> [Origin206]
  ExternalTypes = [0]
  FullyConstrained = true
  MakeInternals = false
  MapMode = 5
  _ExternalGeoVersion = 1
  expr: .Constraints.block_width = <<block_params>>.heatsink_width
  expr: .Constraints.edge_length = <<block_params>>.tfuse_pocket_length + 2 * <<template_params>>.router_offset_1_8
  expr: .Constraints.edge_width = <<block_params>>.tfuse_pocket_width + 2 * <<template_params>>.router_offset_1_8
  expr: .Constraints.placement_length = <<block_params>>.tfuse_placement_length
  expr: .Constraints.placement_width = <<block_params>>.tfuse_placement_width
  expr: .Constraints.router_bushing = <<template_params>>.router_bushing
  sketch-geometry (19):
    g0: LineSegment [constr] StartX=-25 StartY=25 StartZ=0 EndX=-25 EndY=-25 EndZ=0
    g1: LineSegment [constr] StartX=-25 StartY=-25 StartZ=0 EndX=25 EndY=-25 EndZ=0
    g2: LineSegment [constr] StartX=25 StartY=-25 StartZ=0 EndX=25 EndY=25 EndZ=0
    g3: LineSegment [constr] StartX=25 StartY=25 StartZ=0 EndX=-25 EndY=25 EndZ=0
    g4: Circle [constr] CenterX=0 CenterY=0 CenterZ=0 NormalX=0 NormalY=0 NormalZ=1 AngleXU=0 Radius=25
    g5: Circle [constr] CenterX=-3e-16 CenterY=-16 CenterZ=0 NormalX=0 NormalY=0 NormalZ=1 AngleXU=0 Radius=14.1813
    g6: Circle [constr] CenterX=-3e-16 CenterY=-16 CenterZ=0 NormalX=0 NormalY=0 NormalZ=1 AngleXU=0 Radius=8.38125
    g7: LineSegment StartX=-14.1813 StartY=-11.5875 StartZ=0 EndX=-14.1813 EndY=-20.4125 EndZ=0
    g8: LineSegment StartX=-10.2125 StartY=-24.3813 StartZ=0 EndX=10.2125 EndY=-24.3813 EndZ=0
    g9: LineSegment StartX=14.1812 StartY=-20.4125 StartZ=0 EndX=14.1812 EndY=-11.5875 EndZ=0
    g10: LineSegment StartX=10.2125 StartY=-7.61875 StartZ=0 EndX=-10.2125 EndY=-7.61875 EndZ=0
    g11: ArcOfCircle CenterX=10.2125 CenterY=-11.5875 CenterZ=0 NormalX=0 NormalY=0 NormalZ=1 AngleXU=0 Radius=3.96875 StartAngle=0 EndAngle=1.5708
    g12: GeomPoint [constr] X=14.1813 Y=-7.61875 Z=0
    g13: ArcOfCircle CenterX=-10.2125 CenterY=-11.5875 CenterZ=0 NormalX=0 NormalY=0 NormalZ=1 AngleXU=0 Radius=3.96875 StartAngle=1.5708 EndAngle=3.14159
    g14: GeomPoint [constr] X=-14.1813 Y=-7.61875 Z=0
    g15: ArcOfCircle CenterX=-10.2125 CenterY=-20.4125 CenterZ=0 NormalX=0 NormalY=0 NormalZ=1 AngleXU=0 Radius=3.96875 StartAngle=3.14159 EndAngle=4.71239
    g16: GeomPoint [constr] X=-14.1813 Y=-24.3812 Z=0
    g17: ArcOfCircle CenterX=10.2125 CenterY=-20.4125 CenterZ=0 NormalX=0 NormalY=0 NormalZ=1 AngleXU=0 Radius=3.96875 StartAngle=4.71239 EndAngle=6.28319
    g18: GeomPoint [constr] X=14.1813 Y=-24.3812 Z=0
  constraints (47):
    c: Coincident(g0,g1)
    c: Coincident(g1,g2)
    c: Coincident(g2,g3)
    c: Coincident(g3,g0)
    c: Vertical(g0)
    c: Vertical(g2)
    c: Horizontal(g1)
    c: Horizontal(g3)
    c: Coincident(g4,g-1)
    c: Tangent(g4,g3)
    c: Tangent(g4,g1)
    c: Tangent(g4,g2)
    c: Tangent(g4,g0)
    c: Diameter(g4) = 50  'block_width'
    c: Coincident(g6,g5)
    c: DistanceY(g1,g5) = 9  'placement_width'
    c: DistanceX(g5,g1) = 25  'placement_length'
    c: Vertical(g7)
    c: Vertical(g9)
    c: Horizontal(g8)
    c: Horizontal(g10)
    c: PointOnObject(g12,g10)
    c: PointOnObject(g12,g9)
    c: Tangent(g10,g11) = -1.5708
    c: Tangent(g9,g11) = -1.5708
    c: PointOnObject(g14,g10)
    c: PointOnObject(g14,g7)
    c: Tangent(g10,g13) = -1.5708
    c: Tangent(g7,g13) = -1.5708
    c: PointOnObject(g16,g7)
    c: PointOnObject(g16,g8)
    c: Tangent(g7,g15) = -1.5708
    c: Tangent(g8,g15) = -1.5708
    c: PointOnObject(g18,g8)
    c: PointOnObject(g18,g9)
    c: Tangent(g8,g17) = -1.5708
    c: Tangent(g9,g17) = -1.5708
    c: Equal(g17,g11)
    c: Equal(g11,g13)
    c: Equal(g13,g15)
    c: Diameter(g13) = 7.9375  'router_bushing'
    c: Tangent(g6,g10)
    c: Tangent(g6,g8)
    c: Diameter(g6) = 16.7625  'edge_width'
    c: Tangent(g5,g9)
    c: Tangent(g5,g7)
    c: Diameter(g5) = 28.3625  'edge_length'
FEATURE [PartDesign::Pocket] Pocket055  label="hht_tfuse_1-8_pocket"
  BaseFeature = -> Clone031
  Direction = (0,0,-1)
  Length = 5
  Length2 = 5
  Profile = -> Sketch123
  ReferenceAxis = -> Sketch123 [N_Axis]
  Refine = true
  SideType = 0
  Suppressed = false
  Type = 1
  Type2 = 0
FEATURE [PartDesign::Chamfer] Chamfer053  label="hht_tfuse_face_chmf"
  Angle = 45
  Base = -> Pocket055 [Edge31,Edge39]
  BaseFeature = -> Pocket055
  ChamferType = 0
  FlipDirection = false
  Refine = true
  Size = 0.2
  Size2 = 1
  SupportTransform = false
  Suppressed = false
  UseAllEdges = false
FEATURE [PartDesign::Body] Body065  label="heater_heatsink_template_tfuse_1-8"
  AllowCompound = false
  Group = -> [Clone031,Sketch123,Pocket055,Chamfer053]
  Origin = -> Origin206
  Tip = -> Chamfer053
FEATURE [Part::Cut] Cut004  label="heater_heatsink_template_ptc_1-16_lbl"
  Base = -> Body038
  Tool = -> Extrude005
FEATURE [Part::Cut] Cut005  label="heater_heatsink_template_ptc_1-16_labeled"
  Base = -> Cut004
  Tool = -> Extrude001
FEATURE [Part::Cut] Cut006  label="heater_heatsink_template_ptc_1-8_lbl"
  Base = -> Body043
  Tool = -> Extrude005
FEATURE [Part::Cut] Cut007  label="heater_heatsink_template_ptc_1-8_labeled"
  Base = -> Cut006
  Tool = -> Extrude002
FEATURE [Part::Cut] Cut008  label="heater_heatsink_template_tswitch_1-16_lbl"
  Base = -> Body039
  Tool = -> Extrude006
FEATURE [Part::Cut] Cut009  label="heater_heatsink_template_tswitch_1-8_lbl"
  Base = -> Body044
  Tool = -> Extrude006
FEATURE [Part::Cut] Cut010  label="heater_heatsink_template_tswitch_1-16_labeled"
  Base = -> Cut008
  Tool = -> Extrude001
FEATURE [Part::Cut] Cut011  label="heater_heatsink_template_tswitch_1-8_labeled"
  Base = -> Cut009
  Tool = -> Extrude002
FEATURE [Part::Cut] Cut012  label="heater_heatsink_template_tfuse_1-16_lbl"
  Base = -> Body064
  Tool = -> Extrude
FEATURE [Part::Cut] Cut013  label="heater_heatsink_template_tfuse_1-8_lbl"
  Base = -> Body065
  Tool = -> Extrude
FEATURE [Part::Cut] Cut014  label="heater_heatsink_template_tfuse_1-16_labeled"
  Base = -> Cut012
  Tool = -> Extrude001
FEATURE [Part::Cut] Cut015  label="heater_heatsink_template_tfuse_1-8_labeled"
  Base = -> Cut013
  Tool = -> Extrude002
FEATURE [App::DocumentObjectGroup] Group019  label="heater_block_templates"
  Group = -> [Body036,Cut,Cut001,Cut002,Cut003,Cut005,Cut007,Cut010,Cut011,Cut014,Cut015]
FEATURE [TechDraw::DrawSVGTemplate] Template004
  EditableTexts = date_of_issue=6/3/26; document_type=Component Drawing; general_tolerances=ISO 2768-m; language_code=EN; part_material=6061/6063 Aluminum; revision_index=AAA; scale=1 : 1; sheet_number=1 / 1; title=BedBurner - Block (PTC & TFuse)
  Height = 210
  Orientation = 1
  Template = <path>
  Width = 297
FEATURE [TechDraw::DrawProjGroupItem] View011  label="td_block_ptc-tf_view"
  CoarseView = false
  Direction = (0.58,-0.58,0.58)
  Focus = 100
  HardHidden = false
  IsoCount = 0
  IsoHidden = false
  IsoVisible = false
  LockPosition = false
  Perspective = false
  Rotation = 0
  RotationVector = (1,0,0)
  ScaleType = 0
  ScrubCount = 1
  SeamHidden = false
  SeamVisible = false
  SmoothHidden = false
  SmoothVisible = true
  Source = -> [Body060]
  Type = 0
  X = 77.2081
  XDirection = (0.316534,0.797001,-0.514389)
  Y = 151.862
FEATURE [TechDraw::DrawProjGroupItem] View012  label="td_block_ptc-tf_view_face"
  CoarseView = false
  Direction = (0,0,1)
  Focus = 100
  HardHidden = false
  IsoCount = 0
  IsoHidden = false
  IsoVisible = false
  LockPosition = false
  Perspective = false
  Rotation = 0
  RotationVector = (1,0,0)
  ScaleType = 0
  ScrubCount = 1
  SeamHidden = false
  SeamVisible = false
  SmoothHidden = false
  SmoothVisible = true
  Source = -> [Body060]
  Type = 0
  X = 197.006
  XDirection = (1,0,0)
  Y = 133.938
FEATURE [TechDraw::DrawViewDimension] Dimension144
  AngleOverride = false
  Arbitrary = false
  ArbitraryTolerances = false
  BoxCorners = (2) [(-25,-25,-1e-07),(25,25,1e-07)]
  EqualTolerance = true
  ExtensionAngle = 0
  FormatSpec = %.2w
  FormatSpecOverTolerance = %+.2w
  FormatSpecUnderTolerance = %+.2w
  Inverted = false
  LineAngle = 0
  LockPosition = false
  MeasureType = 1
  OverTolerance = 0
  References2D = -> [View012]
  Rotation = 0
  ScaleType = 0
  ShowUnits = false
  TheoreticalExact = false
  Type = 1
  UnderTolerance = 0
  UseActualArea = true
  X = 35.2118
  Y = 44.2958
FEATURE [TechDraw::DrawViewDimension] Dimension145
  AngleOverride = false
  Arbitrary = false
  ArbitraryTolerances = false
  BoxCorners = (2) [(-25,-25,-1e-07),(25,25,1e-07)]
  EqualTolerance = true
  ExtensionAngle = 0
  FormatSpec = %.2w
  FormatSpecOverTolerance = %+.2w
  FormatSpecUnderTolerance = %+.2w
  Inverted = false
  LineAngle = 0
  LockPosition = false
  MeasureType = 1
  OverTolerance = 0
  References2D = -> [View012]
  Rotation = 0
  ScaleType = 0
  ShowUnits = false
  TheoreticalExact = false
  Type = 0
  UnderTolerance = 0
  UseActualArea = true
  X = 35.3392
  Y = 54.8438
FEATURE [TechDraw::DrawViewDimension] Dimension146
  AngleOverride = false
  Arbitrary = false
  ArbitraryTolerances = false
  BoxCorners = (2) [(-25,-25,-1e-07),(25,25,1e-07)]
  EqualTolerance = true
  ExtensionAngle = 0
  FormatSpec = %.2w
  FormatSpecOverTolerance = %+.2w
  FormatSpecUnderTolerance = %+.2w
  Inverted = false
  LineAngle = 0
  LockPosition = false
  MeasureType = 1
  OverTolerance = 0
  References2D = -> [View012]
  Rotation = 0
  ScaleType = 0
  ShowUnits = false
  TheoreticalExact = false
  Type = 0
  UnderTolerance = 0
  UseActualArea = true
  X = 58.9514
  Y = 41.1345
FEATURE [TechDraw::DrawViewDimension] Dimension147
  AngleOverride = false
  Arbitrary = false
  ArbitraryTolerances = false
  BoxCorners = (2) [(-25,-25,-1e-07),(25,25,1e-07)]
  EqualTolerance = true
  ExtensionAngle = 0
  FormatSpec = %.2w
  FormatSpecOverTolerance = %+.2w
  FormatSpecUnderTolerance = %+.2w
  Inverted = false
  LineAngle = 0
  LockPosition = false
  MeasureType = 1
  OverTolerance = 0
  References2D = -> [View012]
  Rotation = 0
  ScaleType = 0
  ShowUnits = false
  TheoreticalExact = false
  Type = 0
  UnderTolerance = 0
  UseActualArea = true
  X = 52.6572
  Y = 31.6865
FEATURE [TechDraw::DrawViewDimension] Dimension148
  AngleOverride = false
  Arbitrary = false
  ArbitraryTolerances = false
  BoxCorners = (2) [(-25,-25,-1e-07),(25,25,1e-07)]
  EqualTolerance = true
  ExtensionAngle = 0
  FormatSpec = %.2w
  FormatSpecOverTolerance = %+.2w
  FormatSpecUnderTolerance = %+.2w
  Inverted = false
  LineAngle = 0
  LockPosition = false
  MeasureType = 1
  OverTolerance = 0
  References2D = -> [View012]
  Rotation = 0
  ScaleType = 0
  ShowUnits = false
  TheoreticalExact = false
  Type = 1
  UnderTolerance = 0
  UseActualArea = true
  X = 7.13968
  Y = 35.8099
FEATURE [TechDraw::DrawViewDimension] Dimension149
  AngleOverride = false
  Arbitrary = false
  ArbitraryTolerances = false
  BoxCorners = (2) [(-25,-25,-1e-07),(25,25,1e-07)]
  EqualTolerance = true
  ExtensionAngle = 0
  FormatSpec = %.2w
  FormatSpecOverTolerance = %+.2w
  FormatSpecUnderTolerance = %+.2w
  Inverted = false
  LineAngle = 0
  LockPosition = false
  MeasureType = 1
  OverTolerance = 0
  References2D = -> [View012]
  Rotation = 0
  ScaleType = 0
  ShowUnits = false
  TheoreticalExact = false
  Type = 1
  UnderTolerance = 0
  UseActualArea = true
  X = 16.9874
  Y = 32.6032
FEATURE [TechDraw::DrawViewDimension] Dimension150
  AngleOverride = false
  Arbitrary = false
  ArbitraryTolerances = false
  BoxCorners = (2) [(-25,-25,-1e-07),(25,25,1e-07)]
  EqualTolerance = true
  ExtensionAngle = 0
  FormatSpec = %.2w
  FormatSpecOverTolerance = %+.2w
  FormatSpecUnderTolerance = %+.2w
  Inverted = false
  LineAngle = 0
  LockPosition = false
  MeasureType = 1
  OverTolerance = 0
  References2D = -> [View012]
  Rotation = 0
  ScaleType = 0
  ShowUnits = false
  TheoreticalExact = false
  Type = 2
  UnderTolerance = 0
  UseActualArea = true
  X = 48.6619
  Y = 3.5
FEATURE [TechDraw::DrawViewDimension] Dimension151
  AngleOverride = false
  Arbitrary = false
  ArbitraryTolerances = false
  BoxCorners = (2) [(-25,-25,-1e-07),(25,25,1e-07)]
  EqualTolerance = true
  ExtensionAngle = 0
  FormatSpec = %.2w
  FormatSpecOverTolerance = %+.2w
  FormatSpecUnderTolerance = %+.2w
  Inverted = false
  LineAngle = 0
  LockPosition = false
  MeasureType = 1
  OverTolerance = 0
  References2D = -> [View012]
  Rotation = 0
  ScaleType = 0
  ShowUnits = false
  TheoreticalExact = false
  Type = 2
  UnderTolerance = 0
  UseActualArea = true
  X = 36.0844
  Y = 3.5
FEATURE [TechDraw::DrawViewDimension] Dimension152
  AngleOverride = false
  Arbitrary = false
  ArbitraryTolerances = false
  BoxCorners = (2) [(-25,-25,-1e-07),(25,25,1e-07)]
  EqualTolerance = true
  ExtensionAngle = 0
  FormatSpec = %.2w
  FormatSpecOverTolerance = %+.2w
  FormatSpecUnderTolerance = %+.2w
  Inverted = false
  LineAngle = 0
  LockPosition = false
  MeasureType = 1
  OverTolerance = 0
  References2D = -> [View012]
  Rotation = 0
  ScaleType = 0
  ShowUnits = false
  TheoreticalExact = false
  Type = 1
  UnderTolerance = 0
  UseActualArea = true
  X = 20.4531
  Y = -38.1722
FEATURE [TechDraw::DrawViewDimension] Dimension153
  AngleOverride = false
  Arbitrary = false
  ArbitraryTolerances = false
  BoxCorners = (2) [(-25,-25,-1e-07),(25,25,1e-07)]
  EqualTolerance = true
  ExtensionAngle = 0
  FormatSpec = %.2w
  FormatSpecOverTolerance = %+.2w
  FormatSpecUnderTolerance = %+.2w
  Inverted = false
  LineAngle = 0
  LockPosition = false
  MeasureType = 1
  OverTolerance = 0
  References2D = -> [View012]
  Rotation = 0
  ScaleType = 0
  ShowUnits = false
  TheoreticalExact = false
  Type = 0
  UnderTolerance = 0
  UseActualArea = true
  X = 22.6728
  Y = -48.1097
FEATURE [TechDraw::DrawViewDimension] Dimension154
  AngleOverride = false
  Arbitrary = false
  ArbitraryTolerances = false
  BoxCorners = (2) [(-25,-25,-1e-07),(25,25,1e-07)]
  EqualTolerance = true
  ExtensionAngle = 0
  FormatSpec = %.2w
  FormatSpecOverTolerance = %+.2w
  FormatSpecUnderTolerance = %+.2w
  Inverted = false
  LineAngle = 0
  LockPosition = false
  MeasureType = 1
  OverTolerance = 0
  References2D = -> [View012]
  Rotation = 0
  ScaleType = 0
  ShowUnits = false
  TheoreticalExact = false
  Type = 2
  UnderTolerance = 0
  UseActualArea = true
  X = -54.7486
  Y = -17.1478
FEATURE [TechDraw::DrawViewDimension] Dimension155
  AngleOverride = false
  Arbitrary = false
  ArbitraryTolerances = false
  BoxCorners = (2) [(-25,-25,-1e-07),(25,25,1e-07)]
  EqualTolerance = true
  ExtensionAngle = 0
  FormatSpec = %.2w
  FormatSpecOverTolerance = %+.2w
  FormatSpecUnderTolerance = %+.2w
  Inverted = false
  LineAngle = 0
  LockPosition = false
  MeasureType = 1
  OverTolerance = 0
  References2D = -> [View012]
  Rotation = 0
  ScaleType = 0
  ShowUnits = false
  TheoreticalExact = false
  Type = 1
  UnderTolerance = 0
  UseActualArea = true
  X = -37.7501
  Y = -26.6798
FEATURE [TechDraw::DrawViewDimension] Dimension156
  AngleOverride = false
  Arbitrary = false
  ArbitraryTolerances = false
  BoxCorners = (2) [(-25,-25,-1e-07),(25,25,1e-07)]
  EqualTolerance = true
  ExtensionAngle = 0
  FormatSpec = %.2w
  FormatSpecOverTolerance = %+.2w
  FormatSpecUnderTolerance = %+.2w
  Inverted = false
  LineAngle = 0
  LockPosition = false
  MeasureType = 1
  OverTolerance = 0
  References2D = -> [View012]
  Rotation = 0
  ScaleType = 0
  ShowUnits = false
  TheoreticalExact = false
  Type = 0
  UnderTolerance = 0
  UseActualArea = true
  X = -61.0896
  Y = 2.61837
FEATURE [TechDraw::DrawViewDimension] Dimension157
  AngleOverride = false
  Arbitrary = false
  ArbitraryTolerances = false
  BoxCorners = (2) [(-25,-25,-1e-07),(25,25,1e-07)]
  EqualTolerance = true
  ExtensionAngle = 0
  FormatSpec = %.2w
  FormatSpecOverTolerance = %+.2w
  FormatSpecUnderTolerance = %+.2w
  Inverted = false
  LineAngle = 0
  LockPosition = false
  MeasureType = 1
  OverTolerance = 0
  References2D = -> [View012]
  Rotation = 0
  ScaleType = 0
  ShowUnits = false
  TheoreticalExact = false
  Type = 0
  UnderTolerance = 0
  UseActualArea = true
  X = -58.5538
  Y = -9.81512
FEATURE [TechDraw::DrawViewDimension] Dimension158
  AngleOverride = false
  Arbitrary = false
  ArbitraryTolerances = false
  BoxCorners = (2) [(-25,-25,-1e-07),(25,25,1e-07)]
  EqualTolerance = true
  ExtensionAngle = 0
  FormatSpec = %.2w
  FormatSpecOverTolerance = %+.2w
  FormatSpecUnderTolerance = %+.2w
  Inverted = false
  LineAngle = 0
  LockPosition = false
  MeasureType = 1
  OverTolerance = 0
  References2D = -> [View012]
  Rotation = 0
  ScaleType = 0
  ShowUnits = false
  TheoreticalExact = false
  Type = 0
  UnderTolerance = 0
  UseActualArea = true
  X = -35.1482
  Y = -15.4979
FEATURE [TechDraw::DrawViewDimension] Dimension159
  AngleOverride = false
  Arbitrary = false
  ArbitraryTolerances = false
  BoxCorners = (2) [(-25,-25,-1e-07),(25,25,1e-07)]
  EqualTolerance = true
  ExtensionAngle = 0
  FormatSpec = %.2w
  FormatSpecOverTolerance = %+.2w
  FormatSpecUnderTolerance = %+.2w
  Inverted = false
  LineAngle = 0
  LockPosition = false
  MeasureType = 1
  OverTolerance = 0
  References2D = -> [View012]
  Rotation = 0
  ScaleType = 0
  ShowUnits = false
  TheoreticalExact = false
  Type = 2
  UnderTolerance = 0
  UseActualArea = true
  X = 38.6572
  Y = -16
FEATURE [TechDraw::DrawViewDimension] Dimension160
  AngleOverride = false
  Arbitrary = false
  ArbitraryTolerances = false
  BoxCorners = (2) [(-25,-25,-1e-07),(25,25,1e-07)]
  EqualTolerance = true
  ExtensionAngle = 0
  FormatSpec = %.2w
  FormatSpecOverTolerance = %+.2w
  FormatSpecUnderTolerance = %+.2w
  Inverted = false
  LineAngle = 0
  LockPosition = false
  MeasureType = 1
  OverTolerance = 0
  References2D = -> [View012]
  Rotation = 0
  ScaleType = 0
  ShowUnits = false
  TheoreticalExact = false
  Type = 0
  UnderTolerance = 0
  UseActualArea = true
  X = 47.1595
  Y = -16.8
FEATURE [TechDraw::DrawViewDimension] Dimension161
  AngleOverride = false
  Arbitrary = false
  ArbitraryTolerances = false
  BoxCorners = (2) [(-25,-25,-1e-07),(25,25,1e-07)]
  EqualTolerance = true
  ExtensionAngle = 0
  FormatSpec = %.2w
  FormatSpecOverTolerance = %+.2w
  FormatSpecUnderTolerance = %+.2w
  Inverted = false
  LineAngle = 0
  LockPosition = false
  MeasureType = 1
  OverTolerance = 0
  References2D = -> [View012]
  Rotation = 0
  ScaleType = 0
  ShowUnits = false
  TheoreticalExact = false
  Type = 0
  UnderTolerance = 0
  UseActualArea = true
  X = 29.0844
  Y = -30.0639
FEATURE [TechDraw::DrawViewDimension] Dimension162
  AngleOverride = false
  Arbitrary = false
  ArbitraryTolerances = false
  BoxCorners = (2) [(-25,-25,-1e-07),(25,25,1e-07)]
  EqualTolerance = true
  ExtensionAngle = 0
  FormatSpec = %.2w
  FormatSpecOverTolerance = %+.2w
  FormatSpecUnderTolerance = %+.2w
  Inverted = false
  LineAngle = 0
  LockPosition = false
  MeasureType = 1
  OverTolerance = 0
  References2D = -> [View012]
  Rotation = 0
  ScaleType = 0
  ShowUnits = false
  TheoreticalExact = false
  Type = 0
  UnderTolerance = 0
  UseActualArea = true
  X = -50.238
  Y = 15.1607
FEATURE [TechDraw::DrawViewDimension] Dimension163
  AngleOverride = false
  Arbitrary = false
  ArbitraryTolerances = false
  BoxCorners = (2) [(-25,-25,-1e-07),(25,25,1e-07)]
  EqualTolerance = true
  ExtensionAngle = 0
  FormatSpec = ⌀%.2w
  FormatSpecOverTolerance = %+.2w
  FormatSpecUnderTolerance = %+.2w
  Inverted = false
  LineAngle = 0
  LockPosition = false
  MeasureType = 1
  OverTolerance = 0
  References2D = -> [View012]
  Rotation = 0
  ScaleType = 0
  ShowUnits = false
  TheoreticalExact = false
  Type = 5
  UnderTolerance = 0
  UseActualArea = true
  X = -32.2666
  Y = 22.3793
FEATURE [TechDraw::DrawViewSection] SectionView  label="td_block_ptc-tf_cross-section"
  BaseView = -> View012
  CoarseView = false
  CutSurfaceDisplay = 2
  Direction = (-1,-1e-16,0)
  FileGeomPattern = <path>
  FileHatchPattern = <path>
  Focus = 100
  FuseBeforeCut = false
  HardHidden = false
  HatchOffset = (0,0,0)
  HatchRotation = 0
  HatchScale = 1
  IsoCount = 0
  IsoHidden = false
  IsoVisible = false
  LockPosition = false
  NameGeomPattern = Diamond
  Perspective = false
  Rotation = -90
  ScaleType = 0
  ScrubCount = 1
  SeamHidden = false
  SeamVisible = false
  SectionDirection = 4
  SectionLineStretch = 1
  SectionNormal = (-1,-1e-16,0)
  SectionOrigin = (19.5,25,0)
  SmoothHidden = false
  SmoothVisible = true
  Source = -> [Body060]
  TrimAfterCut = false
  UsePreviousCut = false
  X = 69.0703
  XDirection = (1e-16,-1,0)
  Y = 72.7051
FEATURE [TechDraw::DrawViewDimension] Dimension164
  AngleOverride = false
  Arbitrary = false
  ArbitraryTolerances = false
  BoxCorners = (2) [(-10,-25,-1e-07),(10,25,1e-07)]
  EqualTolerance = true
  ExtensionAngle = 0
  FormatSpec = %.2w
  FormatSpecOverTolerance = %+.2w
  FormatSpecUnderTolerance = %+.2w
  Inverted = false
  LineAngle = 0
  LockPosition = false
  MeasureType = 1
  OverTolerance = 0
  References2D = -> [SectionView]
  Rotation = 0
  ScaleType = 0
  ShowUnits = false
  TheoreticalExact = false
  Type = 0
  UnderTolerance = 0
  UseActualArea = true
  X = -15.7878
  Y = 35.0733
FEATURE [TechDraw::DrawViewDimension] Dimension165
  AngleOverride = false
  Arbitrary = false
  ArbitraryTolerances = false
  BoxCorners = (2) [(-10,-25,-1e-07),(10,25,1e-07)]
  EqualTolerance = true
  ExtensionAngle = 0
  FormatSpec = %.2w
  FormatSpecOverTolerance = %+.2w
  FormatSpecUnderTolerance = %+.2w
  Inverted = false
  LineAngle = 0
  LockPosition = false
  MeasureType = 1
  OverTolerance = 0
  References2D = -> [SectionView]
  Rotation = 0
  ScaleType = 0
  ShowUnits = false
  TheoreticalExact = false
  Type = 0
  UnderTolerance = 0
  UseActualArea = true
  X = 18.2747
  Y = 26.3959
FEATURE [TechDraw::DrawViewDimension] Dimension166
  AngleOverride = false
  Arbitrary = false
  ArbitraryTolerances = false
  BoxCorners = (2) [(-10,-25,-1e-07),(10,25,1e-07)]
  EqualTolerance = true
  ExtensionAngle = 0
  FormatSpec = %.2w
  FormatSpecOverTolerance = %+.2w
  FormatSpecUnderTolerance = %+.2w
  Inverted = false
  LineAngle = 0
  LockPosition = false
  MeasureType = 1
  OverTolerance = 0
  References2D = -> [SectionView]
  Rotation = 0
  ScaleType = 0
  ShowUnits = false
  TheoreticalExact = false
  Type = 0
  UnderTolerance = 0
  UseActualArea = true
  X = 23.4282
  Y = 15.3511
FEATURE [TechDraw::DrawViewDimension] Dimension167
  AngleOverride = false
  Arbitrary = false
  ArbitraryTolerances = false
  BoxCorners = (2) [(-10,-25,-1e-07),(10,25,1e-07)]
  EqualTolerance = true
  ExtensionAngle = 0
  FormatSpec = %.2w
  FormatSpecOverTolerance = %+.2w
  FormatSpecUnderTolerance = %+.2w
  Inverted = false
  LineAngle = 0
  LockPosition = false
  MeasureType = 1
  OverTolerance = 0
  References2D = -> [SectionView]
  Rotation = 0
  ScaleType = 0
  ShowUnits = false
  TheoreticalExact = false
  Type = 0
  UnderTolerance = 0
  UseActualArea = true
  X = 18.9447
  Y = -17.6003
FEATURE [TechDraw::DrawViewDimension] Dimension168
  AngleOverride = false
  Arbitrary = false
  ArbitraryTolerances = false
  BoxCorners = (2) [(-10,-25,-1e-07),(10,25,1e-07)]
  EqualTolerance = true
  ExtensionAngle = 0
  FormatSpec = %.2w
  FormatSpecOverTolerance = %+.2w
  FormatSpecUnderTolerance = %+.2w
  Inverted = false
  LineAngle = 0
  LockPosition = false
  MeasureType = 1
  OverTolerance = 0
  References2D = -> [SectionView]
  Rotation = 0
  ScaleType = 0
  ShowUnits = false
  TheoreticalExact = false
  Type = 0
  UnderTolerance = 0
  UseActualArea = true
  X = 19.22
  Y = -7.76233
FEATURE [TechDraw::DrawPage] Page005  label="td_block_ptc_tfuse"
  KeepUpdated = true
  NextBalloonIndex = 1
  ProjectionType = 0
  Template = -> Template004
  Views = -> [View011,View012,Dimension144,Dimension145,Dimension146,Dimension147,Dimension148,Dimension149,Dimension150,Dimension151,Dimension152,Dimension153,Dimension154,Dimension155,Dimension156,Dimension157,Dimension158,Dimension159,Dimension160,Dimension161,Dimension162,Dimension163,SectionView,Dimension164,Dimension165,Dimension166,Dimension167,Dimension168]
FEATURE [TechDraw::DrawViewDimension] Dimension169
  AngleOverride = false
  Arbitrary = false
  ArbitraryTolerances = false
  BoxCorners = (2) [(-25,-25,-1e-07),(25,25,1e-07)]
  EqualTolerance = true
  ExtensionAngle = 0
  FormatSpec = ⌀%.2w
  FormatSpecOverTolerance = %+.2w
  FormatSpecUnderTolerance = %+.2w
  Inverted = false
  LineAngle = 0
  LockPosition = false
  MeasureType = 1
  OverTolerance = 0
  References2D = -> [View]
  Rotation = 0
  ScaleType = 0
  ShowUnits = false
  TheoreticalExact = false
  Type = 5
  UnderTolerance = 0
  UseActualArea = true
  X = -30.2096
  Y = 31.0248
FEATURE [TechDraw::DrawPage] Page  label="td_block_ptc_tswitch"
  KeepUpdated = true
  NextBalloonIndex = 1
  ProjectionType = 0
  Template = -> Template
  Views = -> [View,SectionView001,View008,Dimension056,Dimension057,Dimension058,Dimension059,Dimension060,Dimension061,Dimension064,Dimension067,Dimension068,Dimension069,Dimension070,Dimension073,Dimension075,Dimension085,Dimension086,Dimension088,Dimension089,Dimension090,Dimension091,Dimension092,Dimension093,Dimension094,Dimension095,Dimension096,Dimension169]
FEATURE [App::DocumentObjectGroup] Group027  label="drawings"
  Group = -> [Page,Page005,Page003,Page004]
note: 8 file-system paths scrubbed to <path> (originals preserved in the JSON sidecar)
